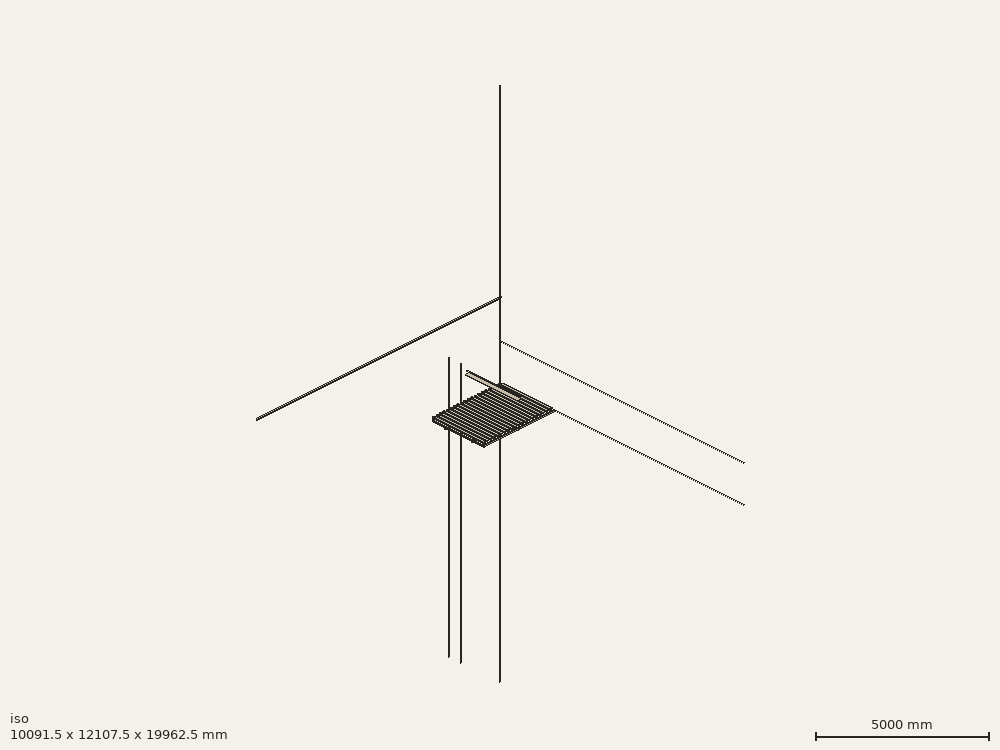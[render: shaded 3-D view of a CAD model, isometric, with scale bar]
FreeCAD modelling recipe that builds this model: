
FCSTD DOCUMENT  (FreeCAD 0.15R4671 (Git))
Label: Assemblage
License: All rights reserved
LicenseURL: http://en.wikipedia.org/wiki/All_rights_reserved
objects: Part::Extrusion×475, Sketcher::SketchObject×454, Part::Cut×180, Part::MultiFuse×62, Part::Chamfer×60, Part::Fuse×40, Part::Fillet×40, App::DocumentObjectGroup×35, Part::Feature×20, PartDesign::Pocket×18, PartDesign::LinearPattern×6, PartDesign::Pad×2
note: 1377 computed .brp shape members not serialized (recipe doc carries the construction recipe); baked Part::Feature solids carry a one-line shape summary decoded from their .brp

FEATURE [Sketcher::SketchObject] Sketch
  Placement = pos=(0,0,0) rot=(1,0,0;1.5708rad)
  sketch-geometry (8):
    g0: LineSegment StartX=-21.15 StartY=16.15 StartZ=0 EndX=-16.15 EndY=21.15 EndZ=0
    g1: LineSegment StartX=-16.15 StartY=21.15 StartZ=0 EndX=16.15 EndY=21.15 EndZ=0
    g2: LineSegment StartX=16.15 StartY=21.15 StartZ=0 EndX=21.15 EndY=16.15 EndZ=0
    g3: LineSegment StartX=21.15 StartY=16.15 StartZ=0 EndX=21.15 EndY=-16.15 EndZ=0
    g4: LineSegment StartX=21.15 StartY=-16.15 StartZ=0 EndX=16.15 EndY=-21.15 EndZ=0
    g5: LineSegment StartX=16.15 StartY=-21.15 StartZ=0 EndX=-16.15 EndY=-21.15 EndZ=0
    g6: LineSegment StartX=-16.15 StartY=-21.15 StartZ=0 EndX=-21.15 EndY=-16.15 EndZ=0
    g7: LineSegment StartX=-21.15 StartY=-16.15 StartZ=0 EndX=-21.15 EndY=16.15 EndZ=0
  constraints (21):
    c: Coincident(g0,g1)
    c: Horizontal(g1)
    c: Coincident(g1,g2)
    c: Coincident(g2,g3)
    c: Vertical(g3)
    c: Coincident(g3,g4)
    c: Coincident(g4,g5)
    c: Horizontal(g5)
    c: Coincident(g5,g6)
    c: Coincident(g6,g7)
    c: Coincident(g7,g0)
    c: Angle(g7,g0) = 2.35619
    c: Distance(g0,g7) = 5
    c: Distance(g2,g7) = 42.3
    c: Distance(g5,g1) = 42.3
    c: Symmetric(g6,g3,g-2)
    c: Symmetric(g5,g4,g-2)
    c: Symmetric(g0,g2,g-2)
    c: Symmetric(g0,g1,g-2)
    c: Symmetric(g0,g6,g-1)
    c: Symmetric(g0,g5,g-1)
FEATURE [Part::Extrusion] Extrude
  Base = -> Sketch
  Dir = (0,48,0)
  Solid = true
FEATURE [Sketcher::SketchObject] Sketch001
  Placement = pos=(0,0,0) rot=(1,0,0;1.5708rad)
  Support = -> Extrude [Face9]
  sketch-geometry (1):
    g0: Circle CenterX=0 CenterY=0 CenterZ=0 NormalX=0 NormalY=0 NormalZ=1 Radius=11
  constraints (2):
    c: Coincident(g0,g-1)
    c: Radius(g0) = 11
FEATURE [Part::Extrusion] Extrude001
  Base = -> Sketch001
  Dir = (0,-2,0)
  Solid = true
FEATURE [Sketcher::SketchObject] Sketch002
  Placement = pos=(0,-2,0) rot=(1,0,0;1.5708rad)
  Support = -> Extrude001 [Face3]
  sketch-geometry (1):
    g0: Circle CenterX=0 CenterY=0 CenterZ=0 NormalX=0 NormalY=0 NormalZ=1 Radius=2.5
  constraints (2):
    c: Coincident(g0,g-1)
    c: Radius(g0) = 2.5
FEATURE [Part::Extrusion] Extrude002
  Base = -> Sketch002
  Dir = (0,-22,0)
  Solid = true
FEATURE [Part::Chamfer] Chamfer
  Base = -> Extrude002
  Edges = 1 edges r=0.8: [Edge3]
FEATURE [Sketcher::SketchObject] Sketch003
  Placement = pos=(0,0,0) rot=(1,0,0;1.5708rad)
  Support = -> Extrude [Face9]
  sketch-geometry (4):
    g0: Circle CenterX=-15.5 CenterY=15.5 CenterZ=0 NormalX=0 NormalY=0 NormalZ=1 Radius=2
    g1: Circle CenterX=15.5 CenterY=15.5 CenterZ=0 NormalX=0 NormalY=0 NormalZ=1 Radius=2
    g2: Circle CenterX=-15.5 CenterY=-15.5 CenterZ=0 NormalX=0 NormalY=0 NormalZ=1 Radius=2
    g3: Circle CenterX=15.5 CenterY=-15.5 CenterZ=0 NormalX=0 NormalY=0 NormalZ=1 Radius=2
  constraints (9):
    c: Distance(g0,g1) = 31
    c: Distance(g0,g2) = 31
    c: Symmetric(g0,g2,g-1)
    c: Symmetric(g0,g1,g-2)
    c: Symmetric(g2,g3,g-2)
    c: Radius(g0) = 2
    c: Equal(g0,g1)
    c: Equal(g0,g2)
    c: Equal(g0,g3)
FEATURE [Part::Extrusion] Extrude003
  Base = -> Sketch003
  Dir = (0,4.5,0)
  Solid = true
FEATURE [Part::Cut] Cut
  Base = -> Extrude
  Tool = -> Extrude003
FEATURE [Sketcher::SketchObject] Sketch004
  Placement = pos=(0,0,0) rot=(1,0,0;1.5708rad)
  sketch-geometry (1):
    g0: Circle CenterX=0 CenterY=0 CenterZ=0 NormalX=0 NormalY=0 NormalZ=1 Radius=9
  constraints (2):
    c: Coincident(g0,g-1)
    c: Radius(g0) = 9
FEATURE [Part::Extrusion] Extrude004
  Base = -> Sketch004
  Dir = (0,25,0)
  Solid = true
FEATURE [Sketcher::SketchObject] Sketch005
  Placement = pos=(0,0,0) rot=(1,0,0;1.5708rad)
  sketch-geometry (1):
    g0: Circle CenterX=0 CenterY=0 CenterZ=0 NormalX=0 NormalY=0 NormalZ=1 Radius=2.5
  constraints (2):
    c: Coincident(g0,g-1)
    c: Radius(g0) = 2.5
FEATURE [Part::Extrusion] Extrude005
  Base = -> Sketch005
  Dir = (0,10,0)
  Solid = true
FEATURE [Part::Cut] Cut001
  Base = -> Extrude004
  Tool = -> Extrude005
FEATURE [Sketcher::SketchObject] Sketch006
  Placement = pos=(0,25,0) rot=(0,0.707107,0.707107;3.14159rad)
  Support = -> Cut001 [Face3]
  sketch-geometry (1):
    g0: Circle CenterX=0 CenterY=0 CenterZ=0 NormalX=0 NormalY=0 NormalZ=1 Radius=4
  constraints (2):
    c: Coincident(g0,g-1)
    c: Radius(g0) = 4
FEATURE [Part::Extrusion] Extrude006
  Base = -> Sketch006
  Dir = (0,-10,0)
  Solid = true
FEATURE [Part::Cut] Cut002  label="Accouplement_001"
  Base = -> Cut001
  Placement = pos=(0,-12,0) rot=(1,0,0;3.14159rad)
  Tool = -> Extrude006
FEATURE [Part::Fuse] Fusion
  Base = -> Extrude001
  Tool = -> Cut
FEATURE [Part::Fuse] Fusion001  label="Moteur_001"
  Base = -> Chamfer
  Tool = -> Fusion
FEATURE [Sketcher::SketchObject] Sketch007
  Placement = pos=(0,0,0) rot=(1,0,0;1.5708rad)
  sketch-geometry (4):
    g0: LineSegment StartX=-50 StartY=0 StartZ=0 EndX=-47 EndY=0 EndZ=0
    g1: LineSegment StartX=47 StartY=0 StartZ=0 EndX=50 EndY=0 EndZ=0
    g2: ArcOfCircle CenterX=0 CenterY=0 CenterZ=0 NormalX=0 NormalY=0 NormalZ=1 Radius=47 StartAngle=3.14159 EndAngle=6.28319
    g3: ArcOfCircle CenterX=0 CenterY=0 CenterZ=0 NormalX=0 NormalY=0 NormalZ=1 Radius=50 StartAngle=3.14159 EndAngle=6.28319
  constraints (13):
    c: Horizontal(g0)
    c: PointOnObject(g1,g-1)
    c: Horizontal(g1)
    c: Coincident(g2,g-1)
    c: PointOnObject(g2,g-1)
    c: Coincident(g3,g-1)
    c: Coincident(g3,g1)
    c: PointOnObject(g3,g-1)
    c: Coincident(g0,g3)
    c: Coincident(g0,g2)
    c: Distance(g0,g1) = 100
    c: Distance(g0,g0) = 3
    c: Coincident(g1,g2)
FEATURE [Part::Extrusion] Extrude007  label="Demi_tube_sous_miroir_001"
  Base = -> Sketch007
  Dir = (0,2000,0)
  Placement = pos=(0,-62,20) rot=(0,0,1;3.14159rad)
  Solid = true
FEATURE [Part::Feature] Part__Feature  label="Coussinet_autolub_C2-151-8-128_001"
  Placement = pos=(0,-46,0) rot=(0,0,1;1.5708rad)
  shape: bbox 16 x 8 x 16 mm, 12 faces (baked)
FEATURE [Sketcher::SketchObject] Sketch008
  Placement = pos=(0,0,0) rot=(1,0,0;1.5708rad)
  sketch-geometry (21):
    g0: Circle CenterX=0 CenterY=0 CenterZ=0 NormalX=0 NormalY=0 NormalZ=1 Radius=6
    g1: LineSegment StartX=-20.5 StartY=15 StartZ=0 EndX=20.5 EndY=15 EndZ=0
    g2: ArcOfCircle CenterX=20.5 CenterY=13 CenterZ=0 NormalX=0 NormalY=0 NormalZ=1 Radius=2 StartAngle=6.28319 EndAngle=7.85398
    g3: LineSegment StartX=22.5 StartY=13 StartZ=0 EndX=22.5 EndY=-73 EndZ=0
    g4: LineSegment StartX=-22.5 StartY=13 StartZ=0 EndX=-22.5 EndY=-73 EndZ=0
    g5: ArcOfCircle CenterX=-20.5 CenterY=13 CenterZ=0 NormalX=0 NormalY=0 NormalZ=1 Radius=2 StartAngle=1.5708 EndAngle=3.14159
    g6: ArcOfCircle CenterX=-20.5 CenterY=-73 CenterZ=0 NormalX=0 NormalY=0 NormalZ=1 Radius=2 StartAngle=3.14159 EndAngle=4.71239
    g7: ArcOfCircle CenterX=20.5 CenterY=-73 CenterZ=0 NormalX=0 NormalY=0 NormalZ=1 Radius=2 StartAngle=4.71239 EndAngle=6.28319
    g8: LineSegment StartX=-20.5 StartY=-75 StartZ=0 EndX=20.5 EndY=-75 EndZ=0
    g9: ArcOfCircle CenterX=0 CenterY=-16.7 CenterZ=0 NormalX=0 NormalY=0 NormalZ=1 Radius=1.5 StartAngle=0 EndAngle=3.14159
    g10: ArcOfCircle CenterX=0 CenterY=-24.3 CenterZ=0 NormalX=0 NormalY=0 NormalZ=1 Radius=1.5 StartAngle=3.14159 EndAngle=6.28319
    g11: LineSegment StartX=-1.5 StartY=-16.7 StartZ=0 EndX=-1.5 EndY=-24.3 EndZ=0
    g12: LineSegment StartX=1.5 StartY=-16.7 StartZ=0 EndX=1.5 EndY=-24.3 EndZ=0
    g13: Circle CenterX=-12.5 CenterY=-45 CenterZ=0 NormalX=0 NormalY=0 NormalZ=1 Radius=3.5
    g14: Circle CenterX=12.5 CenterY=-45 CenterZ=0 NormalX=0 NormalY=0 NormalZ=1 Radius=3.5
    g15: Circle CenterX=-12.5 CenterY=-65 CenterZ=0 NormalX=0 NormalY=0 NormalZ=1 Radius=3.5
    g16: Circle CenterX=12.5 CenterY=-65 CenterZ=0 NormalX=0 NormalY=0 NormalZ=1 Radius=3.5
    g17: LineSegment [constr] StartX=-12.5 StartY=-45 StartZ=0 EndX=12.5 EndY=-45 EndZ=0
    g18: LineSegment [constr] StartX=-12.5 StartY=-45 StartZ=0 EndX=-12.5 EndY=-65 EndZ=0
    g19: LineSegment [constr] StartX=-12.5 StartY=-65 StartZ=0 EndX=12.5 EndY=-65 EndZ=0
    g20: LineSegment [constr] StartX=12.5 StartY=-45 StartZ=0 EndX=12.5 EndY=-65 EndZ=0
  constraints (59):
    c: Coincident(g0,g-1)
    c: Radius(g0) = 6
    c: Horizontal(g1)
    c: Coincident(g2,g1)
    c: Coincident(g3,g2)
    c: Vertical(g3)
    c: Vertical(g4)
    c: Coincident(g5,g1)
    c: Coincident(g5,g4)
    c: Coincident(g7,g3)
    c: Coincident(g8,g6)
    c: Coincident(g8,g7)
    c: Tangent(g8,g7)
    c: Tangent(g5,g4)
    c: Tangent(g5,g1)
    c: Tangent(g1,g2)
    c: Tangent(g2,g3)
    c: Coincident(g4,g6)
    c: Tangent(g6,g4)
    c: Tangent(g6,g8)
    c: Horizontal(g8)
    c: Tangent(g7,g3)
    c: Distance(g4,g2) = 45
    c: Symmetric(g4,g2,g-2)
    c: Distance(g1,g6) = 90
    c: DistanceY(g-1,g1) = 15
    c: Tangent(g9,g12) = 1.5708
    c: Tangent(g9,g11) = -1.5708
    c: Tangent(g11,g10) = -1.5708
    c: Tangent(g12,g10) = 1.5708
    c: Vertical(g11)
    c: Equal(g9,g10)
    c: PointOnObject(g9,g-2)
    c: Distance(g-1,g9) = 16.7
    c: Distance(g9,g10) = 7.6
    c: Radius(g9) = 1.5
    c: Radius(g13) = 3.5
    c: Equal(g13,g14)
    c: Equal(g13,g16)
    c: Equal(g13,g15)
    c: Radius(g5) = 2
    c: Equal(g5,g7)
    c: Equal(g5,g6)
    c: DistanceY(g-1,g13) = -45
    c: Coincident(g17,g13)
    c: Coincident(g17,g14)
    c: Horizontal(g17)
    c: Coincident(g18,g13)
    c: Coincident(g18,g15)
    c: Coincident(g19,g15)
    c: Coincident(g19,g16)
    c: Horizontal(g19)
    c: Coincident(g20,g14)
    c: Coincident(g20,g16)
    c: Vertical(g18)
    c: Vertical(g20)
    c: Distance(g13,g15) = 20
    c: Distance(g13,g14) = 25
    c: Symmetric(g13,g14,g-2)
FEATURE [Part::Extrusion] Extrude008  label="Plaque_support_001"
  Base = -> Sketch008
  Dir = (0,6,0)
  Placement = pos=(0,-46,0) rot=(0,0,1;0rad)
  Solid = true
FEATURE [Sketcher::SketchObject] Sketch009
  Placement = pos=(0,0,0) rot=(0.57735,0.57735,0.57735;2.0944rad)
  sketch-geometry (8):
    g0: LineSegment StartX=0 StartY=33 StartZ=0 EndX=-2 EndY=33 EndZ=0
    g1: LineSegment StartX=-2 StartY=33 StartZ=0 EndX=-2 EndY=-24 EndZ=0
    g2: ArcOfCircle CenterX=-4 CenterY=-24 CenterZ=0 NormalX=0 NormalY=0 NormalZ=1 Radius=2 StartAngle=4.71239 EndAngle=6.28319
    g3: LineSegment StartX=-4 StartY=-26 StartZ=0 EndX=-38 EndY=-26 EndZ=0
    g4: LineSegment StartX=-38 StartY=-26 StartZ=0 EndX=-38 EndY=-28 EndZ=0
    g5: LineSegment StartX=-38 StartY=-28 StartZ=0 EndX=-4 EndY=-28 EndZ=0
    g6: ArcOfCircle CenterX=-4 CenterY=-24 CenterZ=0 NormalX=0 NormalY=0 NormalZ=1 Radius=4 StartAngle=4.71239 EndAngle=6.28319
    g7: LineSegment StartX=0 StartY=-24 StartZ=0 EndX=0 EndY=33 EndZ=0
  constraints (22):
    c: PointOnObject(g0,g-2)
    c: Horizontal(g0)
    c: Coincident(g0,g1)
    c: Vertical(g1)
    c: Tangent(g1,g2) = 1.5708
    c: Tangent(g2,g3) = 1.5708
    c: Coincident(g3,g4)
    c: Vertical(g4)
    c: Coincident(g4,g5)
    c: Horizontal(g5)
    c: Tangent(g5,g6) = -1.5708
    c: PointOnObject(g6,g-2)
    c: Tangent(g6,g7) = -1.5708
    c: Coincident(g7,g0)
    c: Horizontal(g3)
    c: DistanceX(g0,g0) = 2
    c: Radius(g2) = 2
    c: Radius(g6) = 4
    c: DistanceY(g3,g4) = -2
    c: Distance(g-1,g0) = 33
    c: DistanceY(g-1,g5) = -28
    c: DistanceX(g6,g4) = -38
FEATURE [Part::Extrusion] Extrude009
  Base = -> Sketch009
  Dir = (-32.5,0,0)
  Solid = true
FEATURE [Part::Extrusion] Extrude010
  Base = -> Sketch009
  Dir = (32.5,0,0)
  Solid = true
FEATURE [Part::MultiFuse] Fusion002
  Shapes = -> [Extrude009,Extrude010]
FEATURE [Sketcher::SketchObject] Sketch010
  Placement = pos=(0,-2,0) rot=(1,0,0;1.5708rad)
  Support = -> Fusion002 [Face3]
  sketch-geometry (9):
    g0: ArcOfCircle CenterX=0 CenterY=0 CenterZ=0 NormalX=0 NormalY=0 NormalZ=1 Radius=32.5 StartAngle=0 EndAngle=3.14159
    g1: LineSegment StartX=-32.5 StartY=0 StartZ=0 EndX=-32.5 EndY=34 EndZ=0
    g2: LineSegment StartX=-32.5 StartY=34 StartZ=0 EndX=32.5 EndY=34 EndZ=0
    g3: LineSegment StartX=32.5 StartY=34 StartZ=0 EndX=32.5 EndY=0 EndZ=0
    g4: Circle CenterX=0 CenterY=0 CenterZ=0 NormalX=0 NormalY=0 NormalZ=1 Radius=11
    g5: Circle CenterX=-15.5 CenterY=15.5 CenterZ=0 NormalX=0 NormalY=0 NormalZ=1 Radius=2
    g6: Circle CenterX=15.5 CenterY=15.5 CenterZ=0 NormalX=0 NormalY=0 NormalZ=1 Radius=2
    g7: Circle CenterX=-15.5 CenterY=-15.5 CenterZ=0 NormalX=0 NormalY=0 NormalZ=1 Radius=2
    g8: Circle CenterX=15.5 CenterY=-15.5 CenterZ=0 NormalX=0 NormalY=0 NormalZ=1 Radius=2
  constraints (23):
    c: Coincident(g0,g-1)
    c: PointOnObject(g0,g-1)
    c: PointOnObject(g0,g-1)
    c: Coincident(g1,g0)
    c: Vertical(g1)
    c: Coincident(g1,g2)
    c: Horizontal(g2)
    c: Coincident(g2,g3)
    c: Coincident(g3,g0)
    c: Vertical(g3)
    c: DistanceY(g1,g0) = -34
    c: Coincident(g4,g-1)
    c: Radius(g4) = 11
    c: DistanceX(g1,g2) = 65
    c: Radius(g5) = 2
    c: Equal(g5,g6)
    c: Equal(g5,g8)
    c: Equal(g5,g7)
    c: Symmetric(g5,g6,g-2)
    c: Symmetric(g5,g7,g-1)
    c: Symmetric(g7,g8,g-2)
    c: DistanceX(g5,g6) = 31
    c: DistanceY(g5,g7) = -31
FEATURE [Part::Extrusion] Extrude011
  Base = -> Sketch010
  Dir = (0,2,0)
  Solid = true
FEATURE [Part::Cut] Cut003
  Base = -> Fusion002
  Tool = -> Extrude011
FEATURE [Sketcher::SketchObject] Sketch011
  ExternalGeometry = -> [Cut003]
  Placement = pos=(0,0,-26) rot=(0,0,1;0rad)
  Support = -> Cut003 [Face5]
  sketch-geometry (5):
    g0: Circle CenterX=-25 CenterY=-12 CenterZ=0 NormalX=0 NormalY=0 NormalZ=1 Radius=3.5
    g1: Circle CenterX=-25 CenterY=-30 CenterZ=0 NormalX=0 NormalY=0 NormalZ=1 Radius=3.5
    g2: Circle CenterX=25 CenterY=-12 CenterZ=0 NormalX=0 NormalY=0 NormalZ=1 Radius=3.5
    g3: Circle CenterX=25 CenterY=-30 CenterZ=0 NormalX=0 NormalY=0 NormalZ=1 Radius=3.5
    g4: LineSegment [constr] StartX=-25 StartY=-12 StartZ=0 EndX=-25 EndY=-30 EndZ=0
  constraints (12):
    c: Radius(g0) = 3.5
    c: Equal(g0,g2)
    c: Equal(g0,g3)
    c: Equal(g0,g1)
    c: Symmetric(g0,g2,g-2)
    c: Symmetric(g1,g3,g-2)
    c: Coincident(g4,g0)
    c: Coincident(g4,g1)
    c: Vertical(g4)
    c: DistanceY(g0,g1) = -18
    c: DistanceY(g-3,g1) = 8
    c: DistanceX(g0,g2) = 50
FEATURE [Part::Extrusion] Extrude012
  Base = -> Sketch011
  Dir = (0,0,-2)
  Solid = true
FEATURE [Part::Cut] Cut004
  Base = -> Cut003
  Tool = -> Extrude012
FEATURE [Part::Fillet] Fillet  label="Plaque_moteur_001"
  Base = -> Cut004
  Edges = 2 edges r=4: [Edge5,Edge59]
FEATURE [Sketcher::SketchObject] Sketch012
  Placement = pos=(0,0,0) rot=(1,0,0;1.5708rad)
  sketch-geometry (4):
    g0: LineSegment StartX=-3.15 StartY=5.95 StartZ=0 EndX=3.15 EndY=5.95 EndZ=0
    g1: LineSegment StartX=3.15 StartY=5.95 StartZ=0 EndX=3.15 EndY=-5.95 EndZ=0
    g2: LineSegment StartX=3.15 StartY=-5.95 StartZ=0 EndX=-3.15 EndY=-5.95 EndZ=0
    g3: LineSegment StartX=-3.15 StartY=-5.95 StartZ=0 EndX=-3.15 EndY=5.95 EndZ=0
  constraints (12):
    c: Coincident(g0,g1)
    c: Coincident(g1,g2)
    c: Coincident(g2,g3)
    c: Coincident(g3,g0)
    c: Horizontal(g0)
    c: Horizontal(g2)
    c: Vertical(g1)
    c: Vertical(g3)
    c: DistanceX(g0,g0) = 6.3
    c: DistanceY(g0,g2) = -11.9
    c: Symmetric(g0,g0,g-2)
    c: Symmetric(g0,g1,g-1)
FEATURE [Part::Extrusion] Extrude013
  Base = -> Sketch012
  Dir = (0,-10.8,0)
  Solid = true
FEATURE [Sketcher::SketchObject] Sketch013
  ExternalGeometry = -> [Extrude013]
  Placement = pos=(0,-10.8,0) rot=(1,0,0;1.5708rad)
  Support = -> Extrude013 [Face6]
  sketch-geometry (4):
    g0: LineSegment StartX=-3.15 StartY=1.55 StartZ=0 EndX=3.15 EndY=1.55 EndZ=0
    g1: LineSegment StartX=3.15 StartY=1.55 StartZ=0 EndX=3.15 EndY=-1.55 EndZ=0
    g2: LineSegment StartX=3.15 StartY=-1.55 StartZ=0 EndX=-3.15 EndY=-1.55 EndZ=0
    g3: LineSegment StartX=-3.15 StartY=-1.55 StartZ=0 EndX=-3.15 EndY=1.55 EndZ=0
  constraints (12):
    c: Coincident(g0,g1)
    c: Coincident(g1,g2)
    c: Coincident(g2,g3)
    c: Coincident(g3,g0)
    c: Horizontal(g0)
    c: Horizontal(g2)
    c: Vertical(g1)
    c: Vertical(g3)
    c: PointOnObject(g0,g-4)
    c: PointOnObject(g0,g-3)
    c: DistanceY(g0,g2) = -3.1
    c: Symmetric(g0,g1,g-1)
FEATURE [Part::Extrusion] Extrude014
  Base = -> Sketch013
  Dir = (0,7.7,0)
  Solid = true
FEATURE [Part::Cut] Cut005
  Base = -> Extrude013
  Tool = -> Extrude014
FEATURE [Part::Chamfer] Chamfer001
  Base = -> Cut005
  Edges = 4 edges r=0.5: [Edge7,Edge9,Edge15,Edge17]
FEATURE [Part::Chamfer] Chamfer002
  Base = -> Chamfer001
  Edges = 1 edges r=1.2: [Edge13]
FEATURE [Sketcher::SketchObject] Sketch014
  ExternalGeometry = -> [Chamfer002]
  Placement = pos=(0,0,5.95) rot=(0,0,1;0rad)
  Support = -> Chamfer002 [Face5]
  sketch-geometry (4):
    g0: LineSegment StartX=-3 StartY=0 StartZ=0 EndX=3 EndY=0 EndZ=0
    g1: LineSegment StartX=3 StartY=0 StartZ=0 EndX=3 EndY=-3.1 EndZ=0
    g2: LineSegment StartX=3 StartY=-3.1 StartZ=0 EndX=-3 EndY=-3.1 EndZ=0
    g3: LineSegment StartX=-3 StartY=-3.1 StartZ=0 EndX=-3 EndY=0 EndZ=0
  constraints (12):
    c: Coincident(g0,g1)
    c: Coincident(g1,g2)
    c: Coincident(g2,g3)
    c: Coincident(g3,g0)
    c: Horizontal(g0)
    c: Horizontal(g2)
    c: Vertical(g1)
    c: Vertical(g3)
    c: PointOnObject(g0,g-1)
    c: DistanceX(g-3,g0) = 0.15
    c: Symmetric(g0,g0,g-2)
    c: DistanceY(g0,g1) = -3.1
FEATURE [Part::Extrusion] Extrude015
  Base = -> Sketch014
  Dir = (0,0,6.3)
  Solid = true
FEATURE [Sketcher::SketchObject] Sketch015
  ExternalGeometry = -> [Extrude015]
  Placement = pos=(0,-3.1,0) rot=(1,0,0;1.5708rad)
  Support = -> Extrude015 [Face3]
  sketch-geometry (1):
    g0: Circle CenterX=0 CenterY=9.5 CenterZ=0 NormalX=0 NormalY=0 NormalZ=1 Radius=1.65
  constraints (3):
    c: PointOnObject(g0,g-2)
    c: Radius(g0) = 1.65
    c: DistanceY(g0,g-3) = -3.55
FEATURE [Part::Extrusion] Extrude016
  Base = -> Sketch015
  Dir = (0,6,0)
  Solid = true
FEATURE [Part::Cut] Cut006
  Base = -> Extrude015
  Tool = -> Extrude016
FEATURE [Part::Fillet] Fillet001
  Base = -> Cut006
  Edges = 2 edges r=1.35: [Edge8,Edge11]
FEATURE [Part::MultiFuse] Fusion003
  Shapes = -> [Chamfer002]
FEATURE [Sketcher::SketchObject] Sketch016
  Placement = pos=(0,0,0) rot=(0,0.707107,0.707107;3.14159rad)
  Support = -> Fusion003 [Face7]
  sketch-geometry (4):
    g0: Circle CenterX=-1.27 CenterY=3.8 CenterZ=0 NormalX=0 NormalY=0 NormalZ=1 Radius=0.2
    g1: Circle CenterX=1.27 CenterY=3.8 CenterZ=0 NormalX=0 NormalY=0 NormalZ=1 Radius=0.2
    g2: Circle CenterX=-1.27 CenterY=-3.8 CenterZ=0 NormalX=0 NormalY=0 NormalZ=1 Radius=0.2
    g3: Circle CenterX=1.27 CenterY=-3.8 CenterZ=0 NormalX=0 NormalY=0 NormalZ=1 Radius=0.2
  constraints (9):
    c: Radius(g0) = 0.2
    c: Equal(g0,g1)
    c: Equal(g0,g3)
    c: Equal(g0,g2)
    c: Symmetric(g0,g1,g-2)
    c: Symmetric(g2,g3,g-2)
    c: Symmetric(g0,g2,g-1)
    c: DistanceX(g0,g1) = 2.54
    c: DistanceY(g1,g3) = -7.6
FEATURE [Part::Extrusion] Extrude017
  Base = -> Sketch016
  Dir = (0,7.8,0)
  Solid = true
FEATURE [Part::MultiFuse] Fusion004  label="Capteur_optique_001"
  Placement = pos=(0,-46,-20.7) rot=(0,0,1;0rad)
  Shapes = -> [Fusion003,Fillet001,Extrude017]
FEATURE [Sketcher::SketchObject] Sketch017
  Placement = pos=(0,0,0) rot=(1,0,0;1.5708rad)
  sketch-geometry (1):
    g0: Circle CenterX=0 CenterY=0 CenterZ=0 NormalX=0 NormalY=0 NormalZ=1 Radius=4
  constraints (2):
    c: Coincident(g0,g-1)
    c: Radius(g0) = 4
FEATURE [Part::Extrusion] Extrude018
  Base = -> Sketch017
  Dir = (0,50,0)
  Solid = true
FEATURE [Sketcher::SketchObject] Sketch018
  Placement = pos=(0,0,0) rot=(0.57735,0.57735,0.57735;2.0944rad)
  sketch-geometry (1):
    g0: Circle CenterX=6 CenterY=0 CenterZ=0 NormalX=0 NormalY=0 NormalZ=1 Radius=2
  constraints (3):
    c: DistanceX(g-1,g0) = 6
    c: Radius(g0) = 2
    c: PointOnObject(g0,g-1)
FEATURE [Part::Extrusion] Extrude019
  Base = -> Sketch018
  Dir = (4,0,0)
  Solid = true
FEATURE [Part::Extrusion] Extrude020
  Base = -> Sketch018
  Dir = (-4,0,0)
  Solid = true
FEATURE [Part::Cut] Cut007
  Base = -> Extrude018
  Tool = -> Extrude019
FEATURE [Part::Cut] Cut008  label="Axe_D8_001"
  Base = -> Cut007
  Placement = pos=(0,-86,0) rot=(0,0,1;0rad)
  Tool = -> Extrude020
FEATURE [Sketcher::SketchObject] Sketch019
  Placement = pos=(0,0,0) rot=(1,0,0;1.5708rad)
  sketch-geometry (1):
    g0: Circle CenterX=0 CenterY=0 CenterZ=0 NormalX=0 NormalY=0 NormalZ=1 Radius=2
  constraints (2):
    c: Coincident(g0,g-1)
    c: Radius(g0) = 2
FEATURE [Part::Extrusion] Extrude021  label="Axe_D4_001"
  Base = -> Sketch019
  Dir = (0,103.6,0)
  Placement = pos=(51.8,-80,0) rot=(0,0,1;1.5708rad)
  Solid = true
FEATURE [Sketcher::SketchObject] Sketch020
  Placement = pos=(0,0,0) rot=(1,0,0;1.5708rad)
  sketch-geometry (8):
    g0: LineSegment StartX=-50 StartY=0 StartZ=0 EndX=50 EndY=0 EndZ=0
    g1: LineSegment StartX=50 StartY=0 StartZ=0 EndX=50 EndY=-2 EndZ=0
    g2: LineSegment StartX=50 StartY=-2 StartZ=0 EndX=47 EndY=-2 EndZ=0
    g3: LineSegment StartX=47 StartY=-2 StartZ=0 EndX=44 EndY=-16 EndZ=0
    g4: LineSegment StartX=44 StartY=-16 StartZ=0 EndX=-44 EndY=-16 EndZ=0
    g5: LineSegment StartX=-44 StartY=-16 StartZ=0 EndX=-47 EndY=-2 EndZ=0
    g6: LineSegment StartX=-47 StartY=-2 StartZ=0 EndX=-50 EndY=-2 EndZ=0
    g7: LineSegment StartX=-50 StartY=-2 StartZ=0 EndX=-50 EndY=0 EndZ=0
  constraints (24):
    c: PointOnObject(g0,g-1)
    c: Horizontal(g0)
    c: Coincident(g0,g1)
    c: Vertical(g1)
    c: Coincident(g1,g2)
    c: Horizontal(g2)
    c: Coincident(g2,g3)
    c: Coincident(g3,g4)
    c: Horizontal(g4)
    c: Coincident(g4,g5)
    c: Coincident(g5,g6)
    c: Horizontal(g6)
    c: Coincident(g6,g7)
    c: Coincident(g7,g0)
    c: Vertical(g7)
    c: DistanceY(g0,g6) = -2
    c: DistanceX(g6,g5) = 3
    c: DistanceX(g0,g0) = 100
    c: Symmetric(g0,g0,g-2)
    c: Symmetric(g6,g1,g-2)
    c: Symmetric(g5,g2,g-2)
    c: Symmetric(g4,g3,g-2)
    c: DistanceX(g4,g3) = 88
    c: DistanceY(g0,g4) = -16
FEATURE [Part::Extrusion] Extrude022  label="Plaque_alveolaire_001"
  Base = -> Sketch020
  Dir = (0,2000,0)
  Placement = pos=(0,-62,22) rot=(0,0,1;3.14159rad)
  Solid = true
FEATURE [App::DocumentObjectGroup] Groupe  label="Assemblage_miroir_001"
  Group = -> [Cut002,Fusion001,Extrude007,Part__Feature,Extrude008,Fillet,Fusion004,Cut008,Extrude021,Extrude022]
FEATURE [Sketcher::SketchObject] Sketch021
  Placement = pos=(0,0,0) rot=(1,0,0;1.5708rad)
  sketch-geometry (8):
    g0: LineSegment StartX=-21.15 StartY=16.15 StartZ=0 EndX=-16.15 EndY=21.15 EndZ=0
    g1: LineSegment StartX=-16.15 StartY=21.15 StartZ=0 EndX=16.15 EndY=21.15 EndZ=0
    g2: LineSegment StartX=16.15 StartY=21.15 StartZ=0 EndX=21.15 EndY=16.15 EndZ=0
    g3: LineSegment StartX=21.15 StartY=16.15 StartZ=0 EndX=21.15 EndY=-16.15 EndZ=0
    g4: LineSegment StartX=21.15 StartY=-16.15 StartZ=0 EndX=16.15 EndY=-21.15 EndZ=0
    g5: LineSegment StartX=16.15 StartY=-21.15 StartZ=0 EndX=-16.15 EndY=-21.15 EndZ=0
    g6: LineSegment StartX=-16.15 StartY=-21.15 StartZ=0 EndX=-21.15 EndY=-16.15 EndZ=0
    g7: LineSegment StartX=-21.15 StartY=-16.15 StartZ=0 EndX=-21.15 EndY=16.15 EndZ=0
  constraints (21):
    c: Coincident(g0,g1)
    c: Horizontal(g1)
    c: Coincident(g1,g2)
    c: Coincident(g2,g3)
    c: Vertical(g3)
    c: Coincident(g3,g4)
    c: Coincident(g4,g5)
    c: Horizontal(g5)
    c: Coincident(g5,g6)
    c: Coincident(g6,g7)
    c: Coincident(g7,g0)
    c: Angle(g7,g0) = 2.35619
    c: Distance(g0,g7) = 5
    c: Distance(g2,g7) = 42.3
    c: Distance(g5,g1) = 42.3
    c: Symmetric(g6,g3,g-2)
    c: Symmetric(g5,g4,g-2)
    c: Symmetric(g0,g2,g-2)
    c: Symmetric(g0,g1,g-2)
    c: Symmetric(g0,g6,g-1)
    c: Symmetric(g0,g5,g-1)
FEATURE [Part::Extrusion] Extrude023
  Base = -> Sketch021
  Dir = (0,48,0)
  Solid = true
FEATURE [Sketcher::SketchObject] Sketch022
  Placement = pos=(0,0,0) rot=(1,0,0;1.5708rad)
  Support = -> Extrude023 [Face9]
  sketch-geometry (1):
    g0: Circle CenterX=0 CenterY=0 CenterZ=0 NormalX=0 NormalY=0 NormalZ=1 Radius=11
  constraints (2):
    c: Coincident(g0,g-1)
    c: Radius(g0) = 11
FEATURE [Part::Extrusion] Extrude024
  Base = -> Sketch022
  Dir = (0,-2,0)
  Solid = true
FEATURE [Sketcher::SketchObject] Sketch023
  Placement = pos=(0,-2,0) rot=(1,0,0;1.5708rad)
  Support = -> Extrude024 [Face3]
  sketch-geometry (1):
    g0: Circle CenterX=0 CenterY=0 CenterZ=0 NormalX=0 NormalY=0 NormalZ=1 Radius=2.5
  constraints (2):
    c: Coincident(g0,g-1)
    c: Radius(g0) = 2.5
FEATURE [Part::Extrusion] Extrude025
  Base = -> Sketch023
  Dir = (0,-22,0)
  Solid = true
FEATURE [Part::Chamfer] Chamfer003
  Base = -> Extrude025
  Edges = 1 edges r=0.8: [Edge3]
FEATURE [Sketcher::SketchObject] Sketch024
  Placement = pos=(0,0,0) rot=(1,0,0;1.5708rad)
  Support = -> Extrude023 [Face9]
  sketch-geometry (4):
    g0: Circle CenterX=-15.5 CenterY=15.5 CenterZ=0 NormalX=0 NormalY=0 NormalZ=1 Radius=2
    g1: Circle CenterX=15.5 CenterY=15.5 CenterZ=0 NormalX=0 NormalY=0 NormalZ=1 Radius=2
    g2: Circle CenterX=-15.5 CenterY=-15.5 CenterZ=0 NormalX=0 NormalY=0 NormalZ=1 Radius=2
    g3: Circle CenterX=15.5 CenterY=-15.5 CenterZ=0 NormalX=0 NormalY=0 NormalZ=1 Radius=2
  constraints (9):
    c: Distance(g0,g1) = 31
    c: Distance(g0,g2) = 31
    c: Symmetric(g0,g2,g-1)
    c: Symmetric(g0,g1,g-2)
    c: Symmetric(g2,g3,g-2)
    c: Radius(g0) = 2
    c: Equal(g0,g1)
    c: Equal(g0,g2)
    c: Equal(g0,g3)
FEATURE [Part::Extrusion] Extrude026
  Base = -> Sketch024
  Dir = (0,4.5,0)
  Solid = true
FEATURE [Part::Cut] Cut009
  Base = -> Extrude023
  Tool = -> Extrude026
FEATURE [Sketcher::SketchObject] Sketch025
  Placement = pos=(0,0,0) rot=(1,0,0;1.5708rad)
  sketch-geometry (1):
    g0: Circle CenterX=0 CenterY=0 CenterZ=0 NormalX=0 NormalY=0 NormalZ=1 Radius=9
  constraints (2):
    c: Coincident(g0,g-1)
    c: Radius(g0) = 9
FEATURE [Part::Extrusion] Extrude027
  Base = -> Sketch025
  Dir = (0,25,0)
  Solid = true
FEATURE [Sketcher::SketchObject] Sketch026
  Placement = pos=(0,0,0) rot=(1,0,0;1.5708rad)
  sketch-geometry (1):
    g0: Circle CenterX=0 CenterY=0 CenterZ=0 NormalX=0 NormalY=0 NormalZ=1 Radius=2.5
  constraints (2):
    c: Coincident(g0,g-1)
    c: Radius(g0) = 2.5
FEATURE [Part::Extrusion] Extrude028
  Base = -> Sketch026
  Dir = (0,10,0)
  Solid = true
FEATURE [Part::Cut] Cut010
  Base = -> Extrude027
  Tool = -> Extrude028
FEATURE [Sketcher::SketchObject] Sketch027
  Placement = pos=(0,25,0) rot=(0,0.707107,0.707107;3.14159rad)
  Support = -> Cut010 [Face3]
  sketch-geometry (1):
    g0: Circle CenterX=0 CenterY=0 CenterZ=0 NormalX=0 NormalY=0 NormalZ=1 Radius=4
  constraints (2):
    c: Coincident(g0,g-1)
    c: Radius(g0) = 4
FEATURE [Part::Extrusion] Extrude029
  Base = -> Sketch027
  Dir = (0,-10,0)
  Solid = true
FEATURE [Part::Cut] Cut011  label="Accouplement_002"
  Base = -> Cut010
  Placement = pos=(-143,-12,0) rot=(1,0,0;3.14159rad)
  Tool = -> Extrude029
FEATURE [Part::Fuse] Fusion005
  Base = -> Extrude024
  Tool = -> Cut009
FEATURE [Part::Fuse] Fusion006  label="Moteur_002"
  Base = -> Chamfer003
  Placement = pos=(-143,0,0) rot=(0,0,1;0rad)
  Tool = -> Fusion005
FEATURE [Sketcher::SketchObject] Sketch028
  Placement = pos=(0,0,0) rot=(1,0,0;1.5708rad)
  sketch-geometry (4):
    g0: LineSegment StartX=-50 StartY=0 StartZ=0 EndX=-47 EndY=0 EndZ=0
    g1: LineSegment StartX=47 StartY=0 StartZ=0 EndX=50 EndY=0 EndZ=0
    g2: ArcOfCircle CenterX=0 CenterY=0 CenterZ=0 NormalX=0 NormalY=0 NormalZ=1 Radius=47 StartAngle=3.14159 EndAngle=6.28319
    g3: ArcOfCircle CenterX=0 CenterY=0 CenterZ=0 NormalX=0 NormalY=0 NormalZ=1 Radius=50 StartAngle=3.14159 EndAngle=6.28319
  constraints (13):
    c: Horizontal(g0)
    c: PointOnObject(g1,g-1)
    c: Horizontal(g1)
    c: Coincident(g2,g-1)
    c: PointOnObject(g2,g-1)
    c: Coincident(g3,g-1)
    c: Coincident(g3,g1)
    c: PointOnObject(g3,g-1)
    c: Coincident(g0,g3)
    c: Coincident(g0,g2)
    c: Distance(g0,g1) = 100
    c: Distance(g0,g0) = 3
    c: Coincident(g1,g2)
FEATURE [Part::Extrusion] Extrude030  label="Demi_tube_sous_miroir_002"
  Base = -> Sketch028
  Dir = (0,2000,0)
  Placement = pos=(-143,-62,20) rot=(0,0,1;3.14159rad)
  Solid = true
FEATURE [Part::Feature] Part__Feature001  label="Coussinet_autolub_C2-151-8-128_002"
  Placement = pos=(-143,-46,0) rot=(0,0,1;1.5708rad)
  shape: bbox 16 x 8 x 16 mm, 12 faces (baked)
FEATURE [Sketcher::SketchObject] Sketch029
  Placement = pos=(0,0,0) rot=(1,0,0;1.5708rad)
  sketch-geometry (21):
    g0: Circle CenterX=0 CenterY=0 CenterZ=0 NormalX=0 NormalY=0 NormalZ=1 Radius=6
    g1: LineSegment StartX=-20.5 StartY=15 StartZ=0 EndX=20.5 EndY=15 EndZ=0
    g2: ArcOfCircle CenterX=20.5 CenterY=13 CenterZ=0 NormalX=0 NormalY=0 NormalZ=1 Radius=2 StartAngle=6.28319 EndAngle=7.85398
    g3: LineSegment StartX=22.5 StartY=13 StartZ=0 EndX=22.5 EndY=-73 EndZ=0
    g4: LineSegment StartX=-22.5 StartY=13 StartZ=0 EndX=-22.5 EndY=-73 EndZ=0
    g5: ArcOfCircle CenterX=-20.5 CenterY=13 CenterZ=0 NormalX=0 NormalY=0 NormalZ=1 Radius=2 StartAngle=1.5708 EndAngle=3.14159
    g6: ArcOfCircle CenterX=-20.5 CenterY=-73 CenterZ=0 NormalX=0 NormalY=0 NormalZ=1 Radius=2 StartAngle=3.14159 EndAngle=4.71239
    g7: ArcOfCircle CenterX=20.5 CenterY=-73 CenterZ=0 NormalX=0 NormalY=0 NormalZ=1 Radius=2 StartAngle=4.71239 EndAngle=6.28319
    g8: LineSegment StartX=-20.5 StartY=-75 StartZ=0 EndX=20.5 EndY=-75 EndZ=0
    g9: ArcOfCircle CenterX=0 CenterY=-16.7 CenterZ=0 NormalX=0 NormalY=0 NormalZ=1 Radius=1.5 StartAngle=0 EndAngle=3.14159
    g10: ArcOfCircle CenterX=0 CenterY=-24.3 CenterZ=0 NormalX=0 NormalY=0 NormalZ=1 Radius=1.5 StartAngle=3.14159 EndAngle=6.28319
    g11: LineSegment StartX=-1.5 StartY=-16.7 StartZ=0 EndX=-1.5 EndY=-24.3 EndZ=0
    g12: LineSegment StartX=1.5 StartY=-16.7 StartZ=0 EndX=1.5 EndY=-24.3 EndZ=0
    g13: Circle CenterX=-12.5 CenterY=-45 CenterZ=0 NormalX=0 NormalY=0 NormalZ=1 Radius=3.5
    g14: Circle CenterX=12.5 CenterY=-45 CenterZ=0 NormalX=0 NormalY=0 NormalZ=1 Radius=3.5
    g15: Circle CenterX=-12.5 CenterY=-65 CenterZ=0 NormalX=0 NormalY=0 NormalZ=1 Radius=3.5
    g16: Circle CenterX=12.5 CenterY=-65 CenterZ=0 NormalX=0 NormalY=0 NormalZ=1 Radius=3.5
    g17: LineSegment [constr] StartX=-12.5 StartY=-45 StartZ=0 EndX=12.5 EndY=-45 EndZ=0
    g18: LineSegment [constr] StartX=-12.5 StartY=-45 StartZ=0 EndX=-12.5 EndY=-65 EndZ=0
    g19: LineSegment [constr] StartX=-12.5 StartY=-65 StartZ=0 EndX=12.5 EndY=-65 EndZ=0
    g20: LineSegment [constr] StartX=12.5 StartY=-45 StartZ=0 EndX=12.5 EndY=-65 EndZ=0
  constraints (59):
    c: Coincident(g0,g-1)
    c: Radius(g0) = 6
    c: Horizontal(g1)
    c: Coincident(g2,g1)
    c: Coincident(g3,g2)
    c: Vertical(g3)
    c: Vertical(g4)
    c: Coincident(g5,g1)
    c: Coincident(g5,g4)
    c: Coincident(g7,g3)
    c: Coincident(g8,g6)
    c: Coincident(g8,g7)
    c: Tangent(g8,g7)
    c: Tangent(g5,g4)
    c: Tangent(g5,g1)
    c: Tangent(g1,g2)
    c: Tangent(g2,g3)
    c: Coincident(g4,g6)
    c: Tangent(g6,g4)
    c: Tangent(g6,g8)
    c: Horizontal(g8)
    c: Tangent(g7,g3)
    c: Distance(g4,g2) = 45
    c: Symmetric(g4,g2,g-2)
    c: Distance(g1,g6) = 90
    c: DistanceY(g-1,g1) = 15
    c: Tangent(g9,g12) = 1.5708
    c: Tangent(g9,g11) = -1.5708
    c: Tangent(g11,g10) = -1.5708
    c: Tangent(g12,g10) = 1.5708
    c: Vertical(g11)
    c: Equal(g9,g10)
    c: PointOnObject(g9,g-2)
    c: Distance(g-1,g9) = 16.7
    c: Distance(g9,g10) = 7.6
    c: Radius(g9) = 1.5
    c: Radius(g13) = 3.5
    c: Equal(g13,g14)
    c: Equal(g13,g16)
    c: Equal(g13,g15)
    c: Radius(g5) = 2
    c: Equal(g5,g7)
    c: Equal(g5,g6)
    c: DistanceY(g-1,g13) = -45
    c: Coincident(g17,g13)
    c: Coincident(g17,g14)
    c: Horizontal(g17)
    c: Coincident(g18,g13)
    c: Coincident(g18,g15)
    c: Coincident(g19,g15)
    c: Coincident(g19,g16)
    c: Horizontal(g19)
    c: Coincident(g20,g14)
    c: Coincident(g20,g16)
    c: Vertical(g18)
    c: Vertical(g20)
    c: Distance(g13,g15) = 20
    c: Distance(g13,g14) = 25
    c: Symmetric(g13,g14,g-2)
FEATURE [Part::Extrusion] Extrude031  label="Plaque_support_002"
  Base = -> Sketch029
  Dir = (0,6,0)
  Placement = pos=(-143,-46,0) rot=(0,0,1;0rad)
  Solid = true
FEATURE [Sketcher::SketchObject] Sketch030
  Placement = pos=(0,0,0) rot=(0.57735,0.57735,0.57735;2.0944rad)
  sketch-geometry (8):
    g0: LineSegment StartX=0 StartY=33 StartZ=0 EndX=-2 EndY=33 EndZ=0
    g1: LineSegment StartX=-2 StartY=33 StartZ=0 EndX=-2 EndY=-24 EndZ=0
    g2: ArcOfCircle CenterX=-4 CenterY=-24 CenterZ=0 NormalX=0 NormalY=0 NormalZ=1 Radius=2 StartAngle=4.71239 EndAngle=6.28319
    g3: LineSegment StartX=-4 StartY=-26 StartZ=0 EndX=-38 EndY=-26 EndZ=0
    g4: LineSegment StartX=-38 StartY=-26 StartZ=0 EndX=-38 EndY=-28 EndZ=0
    g5: LineSegment StartX=-38 StartY=-28 StartZ=0 EndX=-4 EndY=-28 EndZ=0
    g6: ArcOfCircle CenterX=-4 CenterY=-24 CenterZ=0 NormalX=0 NormalY=0 NormalZ=1 Radius=4 StartAngle=4.71239 EndAngle=6.28319
    g7: LineSegment StartX=0 StartY=-24 StartZ=0 EndX=0 EndY=33 EndZ=0
  constraints (22):
    c: PointOnObject(g0,g-2)
    c: Horizontal(g0)
    c: Coincident(g0,g1)
    c: Vertical(g1)
    c: Tangent(g1,g2) = 1.5708
    c: Tangent(g2,g3) = 1.5708
    c: Coincident(g3,g4)
    c: Vertical(g4)
    c: Coincident(g4,g5)
    c: Horizontal(g5)
    c: Tangent(g5,g6) = -1.5708
    c: PointOnObject(g6,g-2)
    c: Tangent(g6,g7) = -1.5708
    c: Coincident(g7,g0)
    c: Horizontal(g3)
    c: DistanceX(g0,g0) = 2
    c: Radius(g2) = 2
    c: Radius(g6) = 4
    c: DistanceY(g3,g4) = -2
    c: Distance(g-1,g0) = 33
    c: DistanceY(g-1,g5) = -28
    c: DistanceX(g6,g4) = -38
FEATURE [Part::Extrusion] Extrude032
  Base = -> Sketch030
  Dir = (-32.5,0,0)
  Solid = true
FEATURE [Part::Extrusion] Extrude033
  Base = -> Sketch030
  Dir = (32.5,0,0)
  Solid = true
FEATURE [Part::MultiFuse] Fusion007
  Shapes = -> [Extrude032,Extrude033]
FEATURE [Sketcher::SketchObject] Sketch031
  Placement = pos=(0,-2,0) rot=(1,0,0;1.5708rad)
  Support = -> Fusion007 [Face3]
  sketch-geometry (9):
    g0: ArcOfCircle CenterX=0 CenterY=0 CenterZ=0 NormalX=0 NormalY=0 NormalZ=1 Radius=32.5 StartAngle=0 EndAngle=3.14159
    g1: LineSegment StartX=-32.5 StartY=0 StartZ=0 EndX=-32.5 EndY=34 EndZ=0
    g2: LineSegment StartX=-32.5 StartY=34 StartZ=0 EndX=32.5 EndY=34 EndZ=0
    g3: LineSegment StartX=32.5 StartY=34 StartZ=0 EndX=32.5 EndY=0 EndZ=0
    g4: Circle CenterX=0 CenterY=0 CenterZ=0 NormalX=0 NormalY=0 NormalZ=1 Radius=11
    g5: Circle CenterX=-15.5 CenterY=15.5 CenterZ=0 NormalX=0 NormalY=0 NormalZ=1 Radius=2
    g6: Circle CenterX=15.5 CenterY=15.5 CenterZ=0 NormalX=0 NormalY=0 NormalZ=1 Radius=2
    g7: Circle CenterX=-15.5 CenterY=-15.5 CenterZ=0 NormalX=0 NormalY=0 NormalZ=1 Radius=2
    g8: Circle CenterX=15.5 CenterY=-15.5 CenterZ=0 NormalX=0 NormalY=0 NormalZ=1 Radius=2
  constraints (23):
    c: Coincident(g0,g-1)
    c: PointOnObject(g0,g-1)
    c: PointOnObject(g0,g-1)
    c: Coincident(g1,g0)
    c: Vertical(g1)
    c: Coincident(g1,g2)
    c: Horizontal(g2)
    c: Coincident(g2,g3)
    c: Coincident(g3,g0)
    c: Vertical(g3)
    c: DistanceY(g1,g0) = -34
    c: Coincident(g4,g-1)
    c: Radius(g4) = 11
    c: DistanceX(g1,g2) = 65
    c: Radius(g5) = 2
    c: Equal(g5,g6)
    c: Equal(g5,g8)
    c: Equal(g5,g7)
    c: Symmetric(g5,g6,g-2)
    c: Symmetric(g5,g7,g-1)
    c: Symmetric(g7,g8,g-2)
    c: DistanceX(g5,g6) = 31
    c: DistanceY(g5,g7) = -31
FEATURE [Part::Extrusion] Extrude034
  Base = -> Sketch031
  Dir = (0,2,0)
  Solid = true
FEATURE [Part::Cut] Cut012
  Base = -> Fusion007
  Tool = -> Extrude034
FEATURE [Sketcher::SketchObject] Sketch032
  ExternalGeometry = -> [Cut012]
  Placement = pos=(0,0,-26) rot=(0,0,1;0rad)
  Support = -> Cut012 [Face5]
  sketch-geometry (5):
    g0: Circle CenterX=-25 CenterY=-12 CenterZ=0 NormalX=0 NormalY=0 NormalZ=1 Radius=3.5
    g1: Circle CenterX=-25 CenterY=-30 CenterZ=0 NormalX=0 NormalY=0 NormalZ=1 Radius=3.5
    g2: Circle CenterX=25 CenterY=-12 CenterZ=0 NormalX=0 NormalY=0 NormalZ=1 Radius=3.5
    g3: Circle CenterX=25 CenterY=-30 CenterZ=0 NormalX=0 NormalY=0 NormalZ=1 Radius=3.5
    g4: LineSegment [constr] StartX=-25 StartY=-12 StartZ=0 EndX=-25 EndY=-30 EndZ=0
  constraints (12):
    c: Radius(g0) = 3.5
    c: Equal(g0,g2)
    c: Equal(g0,g3)
    c: Equal(g0,g1)
    c: Symmetric(g0,g2,g-2)
    c: Symmetric(g1,g3,g-2)
    c: Coincident(g4,g0)
    c: Coincident(g4,g1)
    c: Vertical(g4)
    c: DistanceY(g0,g1) = -18
    c: DistanceY(g-3,g1) = 8
    c: DistanceX(g0,g2) = 50
FEATURE [Part::Extrusion] Extrude035
  Base = -> Sketch032
  Dir = (0,0,-2)
  Solid = true
FEATURE [Part::Cut] Cut013
  Base = -> Cut012
  Tool = -> Extrude035
FEATURE [Part::Fillet] Fillet002  label="Plaque_moteur_002"
  Base = -> Cut013
  Edges = 2 edges r=4: [Edge5,Edge59]
  Placement = pos=(-143,0,0) rot=(0,0,1;0rad)
FEATURE [Sketcher::SketchObject] Sketch033
  Placement = pos=(0,0,0) rot=(1,0,0;1.5708rad)
  sketch-geometry (4):
    g0: LineSegment StartX=-3.15 StartY=5.95 StartZ=0 EndX=3.15 EndY=5.95 EndZ=0
    g1: LineSegment StartX=3.15 StartY=5.95 StartZ=0 EndX=3.15 EndY=-5.95 EndZ=0
    g2: LineSegment StartX=3.15 StartY=-5.95 StartZ=0 EndX=-3.15 EndY=-5.95 EndZ=0
    g3: LineSegment StartX=-3.15 StartY=-5.95 StartZ=0 EndX=-3.15 EndY=5.95 EndZ=0
  constraints (12):
    c: Coincident(g0,g1)
    c: Coincident(g1,g2)
    c: Coincident(g2,g3)
    c: Coincident(g3,g0)
    c: Horizontal(g0)
    c: Horizontal(g2)
    c: Vertical(g1)
    c: Vertical(g3)
    c: DistanceX(g0,g0) = 6.3
    c: DistanceY(g0,g2) = -11.9
    c: Symmetric(g0,g0,g-2)
    c: Symmetric(g0,g1,g-1)
FEATURE [Part::Extrusion] Extrude036
  Base = -> Sketch033
  Dir = (0,-10.8,0)
  Solid = true
FEATURE [Sketcher::SketchObject] Sketch034
  ExternalGeometry = -> [Extrude036]
  Placement = pos=(0,-10.8,0) rot=(1,0,0;1.5708rad)
  Support = -> Extrude036 [Face6]
  sketch-geometry (4):
    g0: LineSegment StartX=-3.15 StartY=1.55 StartZ=0 EndX=3.15 EndY=1.55 EndZ=0
    g1: LineSegment StartX=3.15 StartY=1.55 StartZ=0 EndX=3.15 EndY=-1.55 EndZ=0
    g2: LineSegment StartX=3.15 StartY=-1.55 StartZ=0 EndX=-3.15 EndY=-1.55 EndZ=0
    g3: LineSegment StartX=-3.15 StartY=-1.55 StartZ=0 EndX=-3.15 EndY=1.55 EndZ=0
  constraints (12):
    c: Coincident(g0,g1)
    c: Coincident(g1,g2)
    c: Coincident(g2,g3)
    c: Coincident(g3,g0)
    c: Horizontal(g0)
    c: Horizontal(g2)
    c: Vertical(g1)
    c: Vertical(g3)
    c: PointOnObject(g0,g-4)
    c: PointOnObject(g0,g-3)
    c: DistanceY(g0,g2) = -3.1
    c: Symmetric(g0,g1,g-1)
FEATURE [Part::Extrusion] Extrude037
  Base = -> Sketch034
  Dir = (0,7.7,0)
  Solid = true
FEATURE [Part::Cut] Cut014
  Base = -> Extrude036
  Tool = -> Extrude037
FEATURE [Part::Chamfer] Chamfer004
  Base = -> Cut014
  Edges = 4 edges r=0.5: [Edge7,Edge9,Edge15,Edge17]
FEATURE [Part::Chamfer] Chamfer005
  Base = -> Chamfer004
  Edges = 1 edges r=1.2: [Edge13]
FEATURE [Sketcher::SketchObject] Sketch035
  ExternalGeometry = -> [Chamfer005]
  Placement = pos=(0,0,5.95) rot=(0,0,1;0rad)
  Support = -> Chamfer005 [Face5]
  sketch-geometry (4):
    g0: LineSegment StartX=-3 StartY=0 StartZ=0 EndX=3 EndY=0 EndZ=0
    g1: LineSegment StartX=3 StartY=0 StartZ=0 EndX=3 EndY=-3.1 EndZ=0
    g2: LineSegment StartX=3 StartY=-3.1 StartZ=0 EndX=-3 EndY=-3.1 EndZ=0
    g3: LineSegment StartX=-3 StartY=-3.1 StartZ=0 EndX=-3 EndY=0 EndZ=0
  constraints (12):
    c: Coincident(g0,g1)
    c: Coincident(g1,g2)
    c: Coincident(g2,g3)
    c: Coincident(g3,g0)
    c: Horizontal(g0)
    c: Horizontal(g2)
    c: Vertical(g1)
    c: Vertical(g3)
    c: PointOnObject(g0,g-1)
    c: DistanceX(g-3,g0) = 0.15
    c: Symmetric(g0,g0,g-2)
    c: DistanceY(g0,g1) = -3.1
FEATURE [Part::Extrusion] Extrude038
  Base = -> Sketch035
  Dir = (0,0,6.3)
  Solid = true
FEATURE [Sketcher::SketchObject] Sketch036
  ExternalGeometry = -> [Extrude038]
  Placement = pos=(0,-3.1,0) rot=(1,0,0;1.5708rad)
  Support = -> Extrude038 [Face3]
  sketch-geometry (1):
    g0: Circle CenterX=0 CenterY=9.5 CenterZ=0 NormalX=0 NormalY=0 NormalZ=1 Radius=1.65
  constraints (3):
    c: PointOnObject(g0,g-2)
    c: Radius(g0) = 1.65
    c: DistanceY(g0,g-3) = -3.55
FEATURE [Part::Extrusion] Extrude039
  Base = -> Sketch036
  Dir = (0,6,0)
  Solid = true
FEATURE [Part::Cut] Cut015
  Base = -> Extrude038
  Tool = -> Extrude039
FEATURE [Part::Fillet] Fillet003
  Base = -> Cut015
  Edges = 2 edges r=1.35: [Edge8,Edge11]
FEATURE [Part::MultiFuse] Fusion008
  Shapes = -> [Chamfer005]
FEATURE [Sketcher::SketchObject] Sketch037
  Placement = pos=(0,0,0) rot=(0,0.707107,0.707107;3.14159rad)
  Support = -> Fusion008 [Face7]
  sketch-geometry (4):
    g0: Circle CenterX=-1.27 CenterY=3.8 CenterZ=0 NormalX=0 NormalY=0 NormalZ=1 Radius=0.2
    g1: Circle CenterX=1.27 CenterY=3.8 CenterZ=0 NormalX=0 NormalY=0 NormalZ=1 Radius=0.2
    g2: Circle CenterX=-1.27 CenterY=-3.8 CenterZ=0 NormalX=0 NormalY=0 NormalZ=1 Radius=0.2
    g3: Circle CenterX=1.27 CenterY=-3.8 CenterZ=0 NormalX=0 NormalY=0 NormalZ=1 Radius=0.2
  constraints (9):
    c: Radius(g0) = 0.2
    c: Equal(g0,g1)
    c: Equal(g0,g3)
    c: Equal(g0,g2)
    c: Symmetric(g0,g1,g-2)
    c: Symmetric(g2,g3,g-2)
    c: Symmetric(g0,g2,g-1)
    c: DistanceX(g0,g1) = 2.54
    c: DistanceY(g1,g3) = -7.6
FEATURE [Part::Extrusion] Extrude040
  Base = -> Sketch037
  Dir = (0,7.8,0)
  Solid = true
FEATURE [Part::MultiFuse] Fusion009  label="Capteur_optique_002"
  Placement = pos=(-143,-46,-20.7) rot=(0,0,1;0rad)
  Shapes = -> [Fusion008,Fillet003,Extrude040]
FEATURE [Sketcher::SketchObject] Sketch038
  Placement = pos=(0,0,0) rot=(1,0,0;1.5708rad)
  sketch-geometry (1):
    g0: Circle CenterX=0 CenterY=0 CenterZ=0 NormalX=0 NormalY=0 NormalZ=1 Radius=4
  constraints (2):
    c: Coincident(g0,g-1)
    c: Radius(g0) = 4
FEATURE [Part::Extrusion] Extrude041
  Base = -> Sketch038
  Dir = (0,50,0)
  Solid = true
FEATURE [Sketcher::SketchObject] Sketch039
  Placement = pos=(0,0,0) rot=(0.57735,0.57735,0.57735;2.0944rad)
  sketch-geometry (1):
    g0: Circle CenterX=6 CenterY=0 CenterZ=0 NormalX=0 NormalY=0 NormalZ=1 Radius=2
  constraints (3):
    c: DistanceX(g-1,g0) = 6
    c: Radius(g0) = 2
    c: PointOnObject(g0,g-1)
FEATURE [Part::Extrusion] Extrude042
  Base = -> Sketch039
  Dir = (4,0,0)
  Solid = true
FEATURE [Part::Extrusion] Extrude043
  Base = -> Sketch039
  Dir = (-4,0,0)
  Solid = true
FEATURE [Part::Cut] Cut016
  Base = -> Extrude041
  Tool = -> Extrude042
FEATURE [Part::Cut] Cut017  label="Axe_D8_002"
  Base = -> Cut016
  Placement = pos=(-143,-86,0) rot=(0,0,1;0rad)
  Tool = -> Extrude043
FEATURE [Sketcher::SketchObject] Sketch040
  Placement = pos=(0,0,0) rot=(1,0,0;1.5708rad)
  sketch-geometry (1):
    g0: Circle CenterX=0 CenterY=0 CenterZ=0 NormalX=0 NormalY=0 NormalZ=1 Radius=2
  constraints (2):
    c: Coincident(g0,g-1)
    c: Radius(g0) = 2
FEATURE [Part::Extrusion] Extrude044  label="Axe_D4_002"
  Base = -> Sketch040
  Dir = (0,103.6,0)
  Placement = pos=(-91.2,-80,0) rot=(0,0,1;1.5708rad)
  Solid = true
FEATURE [Sketcher::SketchObject] Sketch041
  Placement = pos=(0,0,0) rot=(1,0,0;1.5708rad)
  sketch-geometry (8):
    g0: LineSegment StartX=-50 StartY=0 StartZ=0 EndX=50 EndY=0 EndZ=0
    g1: LineSegment StartX=50 StartY=0 StartZ=0 EndX=50 EndY=-2 EndZ=0
    g2: LineSegment StartX=50 StartY=-2 StartZ=0 EndX=47 EndY=-2 EndZ=0
    g3: LineSegment StartX=47 StartY=-2 StartZ=0 EndX=44 EndY=-16 EndZ=0
    g4: LineSegment StartX=44 StartY=-16 StartZ=0 EndX=-44 EndY=-16 EndZ=0
    g5: LineSegment StartX=-44 StartY=-16 StartZ=0 EndX=-47 EndY=-2 EndZ=0
    g6: LineSegment StartX=-47 StartY=-2 StartZ=0 EndX=-50 EndY=-2 EndZ=0
    g7: LineSegment StartX=-50 StartY=-2 StartZ=0 EndX=-50 EndY=0 EndZ=0
  constraints (24):
    c: PointOnObject(g0,g-1)
    c: Horizontal(g0)
    c: Coincident(g0,g1)
    c: Vertical(g1)
    c: Coincident(g1,g2)
    c: Horizontal(g2)
    c: Coincident(g2,g3)
    c: Coincident(g3,g4)
    c: Horizontal(g4)
    c: Coincident(g4,g5)
    c: Coincident(g5,g6)
    c: Horizontal(g6)
    c: Coincident(g6,g7)
    c: Coincident(g7,g0)
    c: Vertical(g7)
    c: DistanceY(g0,g6) = -2
    c: DistanceX(g6,g5) = 3
    c: DistanceX(g0,g0) = 100
    c: Symmetric(g0,g0,g-2)
    c: Symmetric(g6,g1,g-2)
    c: Symmetric(g5,g2,g-2)
    c: Symmetric(g4,g3,g-2)
    c: DistanceX(g4,g3) = 88
    c: DistanceY(g0,g4) = -16
FEATURE [Part::Extrusion] Extrude045  label="Plaque_alveolaire_002"
  Base = -> Sketch041
  Dir = (0,2000,0)
  Placement = pos=(-143,-62,22) rot=(0,0,1;3.14159rad)
  Solid = true
FEATURE [App::DocumentObjectGroup] Groupe001  label="Assemblage_miroir X=-143_001"
  Group = -> [Cut011,Fusion006,Extrude030,Part__Feature001,Extrude031,Fillet002,Fusion009,Cut017,Extrude044,Extrude045]
FEATURE [Sketcher::SketchObject] Sketch064
  Placement = pos=(0,0,0) rot=(1,0,0;1.5708rad)
  sketch-geometry (8):
    g0: LineSegment StartX=-21.15 StartY=16.15 StartZ=0 EndX=-16.15 EndY=21.15 EndZ=0
    g1: LineSegment StartX=-16.15 StartY=21.15 StartZ=0 EndX=16.15 EndY=21.15 EndZ=0
    g2: LineSegment StartX=16.15 StartY=21.15 StartZ=0 EndX=21.15 EndY=16.15 EndZ=0
    g3: LineSegment StartX=21.15 StartY=16.15 StartZ=0 EndX=21.15 EndY=-16.15 EndZ=0
    g4: LineSegment StartX=21.15 StartY=-16.15 StartZ=0 EndX=16.15 EndY=-21.15 EndZ=0
    g5: LineSegment StartX=16.15 StartY=-21.15 StartZ=0 EndX=-16.15 EndY=-21.15 EndZ=0
    g6: LineSegment StartX=-16.15 StartY=-21.15 StartZ=0 EndX=-21.15 EndY=-16.15 EndZ=0
    g7: LineSegment StartX=-21.15 StartY=-16.15 StartZ=0 EndX=-21.15 EndY=16.15 EndZ=0
  constraints (21):
    c: Coincident(g0,g1)
    c: Horizontal(g1)
    c: Coincident(g1,g2)
    c: Coincident(g2,g3)
    c: Vertical(g3)
    c: Coincident(g3,g4)
    c: Coincident(g4,g5)
    c: Horizontal(g5)
    c: Coincident(g5,g6)
    c: Coincident(g6,g7)
    c: Coincident(g7,g0)
    c: Angle(g7,g0) = 2.35619
    c: Distance(g0,g7) = 5
    c: Distance(g2,g7) = 42.3
    c: Distance(g5,g1) = 42.3
    c: Symmetric(g6,g3,g-2)
    c: Symmetric(g5,g4,g-2)
    c: Symmetric(g0,g2,g-2)
    c: Symmetric(g0,g1,g-2)
    c: Symmetric(g0,g6,g-1)
    c: Symmetric(g0,g5,g-1)
FEATURE [Part::Extrusion] Extrude097
  Base = -> Sketch064
  Dir = (0,48,0)
  Solid = true
FEATURE [Sketcher::SketchObject] Sketch065
  Placement = pos=(0,0,0) rot=(1,0,0;1.5708rad)
  Support = -> Extrude097 [Face9]
  sketch-geometry (1):
    g0: Circle CenterX=0 CenterY=0 CenterZ=0 NormalX=0 NormalY=0 NormalZ=1 Radius=11
  constraints (2):
    c: Coincident(g0,g-1)
    c: Radius(g0) = 11
FEATURE [Part::Extrusion] Extrude098
  Base = -> Sketch065
  Dir = (0,-2,0)
  Solid = true
FEATURE [Sketcher::SketchObject] Sketch066
  Placement = pos=(0,-2,0) rot=(1,0,0;1.5708rad)
  Support = -> Extrude098 [Face3]
  sketch-geometry (1):
    g0: Circle CenterX=0 CenterY=0 CenterZ=0 NormalX=0 NormalY=0 NormalZ=1 Radius=2.5
  constraints (2):
    c: Coincident(g0,g-1)
    c: Radius(g0) = 2.5
FEATURE [Part::Extrusion] Extrude099
  Base = -> Sketch066
  Dir = (0,-22,0)
  Solid = true
FEATURE [Part::Chamfer] Chamfer009
  Base = -> Extrude099
  Edges = 1 edges r=0.8: [Edge3]
FEATURE [Sketcher::SketchObject] Sketch067
  Placement = pos=(0,0,0) rot=(1,0,0;1.5708rad)
  Support = -> Extrude097 [Face9]
  sketch-geometry (4):
    g0: Circle CenterX=-15.5 CenterY=15.5 CenterZ=0 NormalX=0 NormalY=0 NormalZ=1 Radius=2
    g1: Circle CenterX=15.5 CenterY=15.5 CenterZ=0 NormalX=0 NormalY=0 NormalZ=1 Radius=2
    g2: Circle CenterX=-15.5 CenterY=-15.5 CenterZ=0 NormalX=0 NormalY=0 NormalZ=1 Radius=2
    g3: Circle CenterX=15.5 CenterY=-15.5 CenterZ=0 NormalX=0 NormalY=0 NormalZ=1 Radius=2
  constraints (9):
    c: Distance(g0,g1) = 31
    c: Distance(g0,g2) = 31
    c: Symmetric(g0,g2,g-1)
    c: Symmetric(g0,g1,g-2)
    c: Symmetric(g2,g3,g-2)
    c: Radius(g0) = 2
    c: Equal(g0,g1)
    c: Equal(g0,g2)
    c: Equal(g0,g3)
FEATURE [Part::Extrusion] Extrude100
  Base = -> Sketch067
  Dir = (0,4.5,0)
  Solid = true
FEATURE [Part::Cut] Cut038
  Base = -> Extrude097
  Tool = -> Extrude100
FEATURE [Sketcher::SketchObject] Sketch068
  Placement = pos=(0,0,0) rot=(1,0,0;1.5708rad)
  sketch-geometry (1):
    g0: Circle CenterX=0 CenterY=0 CenterZ=0 NormalX=0 NormalY=0 NormalZ=1 Radius=9
  constraints (2):
    c: Coincident(g0,g-1)
    c: Radius(g0) = 9
FEATURE [Part::Extrusion] Extrude101
  Base = -> Sketch068
  Dir = (0,25,0)
  Solid = true
FEATURE [Sketcher::SketchObject] Sketch069
  Placement = pos=(0,0,0) rot=(1,0,0;1.5708rad)
  sketch-geometry (1):
    g0: Circle CenterX=0 CenterY=0 CenterZ=0 NormalX=0 NormalY=0 NormalZ=1 Radius=2.5
  constraints (2):
    c: Coincident(g0,g-1)
    c: Radius(g0) = 2.5
FEATURE [Part::Extrusion] Extrude102
  Base = -> Sketch069
  Dir = (0,10,0)
  Solid = true
FEATURE [Part::Cut] Cut039
  Base = -> Extrude101
  Tool = -> Extrude102
FEATURE [Sketcher::SketchObject] Sketch070
  Placement = pos=(0,25,0) rot=(0,0.707107,0.707107;3.14159rad)
  Support = -> Cut039 [Face3]
  sketch-geometry (1):
    g0: Circle CenterX=0 CenterY=0 CenterZ=0 NormalX=0 NormalY=0 NormalZ=1 Radius=4
  constraints (2):
    c: Coincident(g0,g-1)
    c: Radius(g0) = 4
FEATURE [Part::Extrusion] Extrude103
  Base = -> Sketch070
  Dir = (0,-10,0)
  Solid = true
FEATURE [Part::Cut] Cut040  label="Accouplement_003"
  Base = -> Cut039
  Placement = pos=(-286,-12,0) rot=(1,0,0;3.14159rad)
  Tool = -> Extrude103
FEATURE [Part::Fuse] Fusion022
  Base = -> Extrude098
  Tool = -> Cut038
FEATURE [Part::Fuse] Fusion023  label="Moteur_003"
  Base = -> Chamfer009
  Placement = pos=(-286,0,0) rot=(0,0,1;0rad)
  Tool = -> Fusion022
FEATURE [Sketcher::SketchObject] Sketch071
  Placement = pos=(0,0,0) rot=(1,0,0;1.5708rad)
  sketch-geometry (4):
    g0: LineSegment StartX=-50 StartY=0 StartZ=0 EndX=-47 EndY=0 EndZ=0
    g1: LineSegment StartX=47 StartY=0 StartZ=0 EndX=50 EndY=0 EndZ=0
    g2: ArcOfCircle CenterX=0 CenterY=0 CenterZ=0 NormalX=0 NormalY=0 NormalZ=1 Radius=47 StartAngle=3.14159 EndAngle=6.28319
    g3: ArcOfCircle CenterX=0 CenterY=0 CenterZ=0 NormalX=0 NormalY=0 NormalZ=1 Radius=50 StartAngle=3.14159 EndAngle=6.28319
  constraints (13):
    c: Horizontal(g0)
    c: PointOnObject(g1,g-1)
    c: Horizontal(g1)
    c: Coincident(g2,g-1)
    c: PointOnObject(g2,g-1)
    c: Coincident(g3,g-1)
    c: Coincident(g3,g1)
    c: PointOnObject(g3,g-1)
    c: Coincident(g0,g3)
    c: Coincident(g0,g2)
    c: Distance(g0,g1) = 100
    c: Distance(g0,g0) = 3
    c: Coincident(g1,g2)
FEATURE [Part::Extrusion] Extrude104  label="Demi_tube_sous_miroir_003"
  Base = -> Sketch071
  Dir = (0,2000,0)
  Placement = pos=(-286,-62,20) rot=(0,0,1;3.14159rad)
  Solid = true
FEATURE [Part::Feature] Part__Feature005  label="Coussinet_autolub_C2-151-8-128_003"
  Placement = pos=(-286,-46,0) rot=(0,0,1;1.5708rad)
  shape: bbox 16 x 8 x 16 mm, 12 faces (baked)
FEATURE [Sketcher::SketchObject] Sketch072
  Placement = pos=(0,0,0) rot=(1,0,0;1.5708rad)
  sketch-geometry (21):
    g0: Circle CenterX=0 CenterY=0 CenterZ=0 NormalX=0 NormalY=0 NormalZ=1 Radius=6
    g1: LineSegment StartX=-20.5 StartY=15 StartZ=0 EndX=20.5 EndY=15 EndZ=0
    g2: ArcOfCircle CenterX=20.5 CenterY=13 CenterZ=0 NormalX=0 NormalY=0 NormalZ=1 Radius=2 StartAngle=6.28319 EndAngle=7.85398
    g3: LineSegment StartX=22.5 StartY=13 StartZ=0 EndX=22.5 EndY=-73 EndZ=0
    g4: LineSegment StartX=-22.5 StartY=13 StartZ=0 EndX=-22.5 EndY=-73 EndZ=0
    g5: ArcOfCircle CenterX=-20.5 CenterY=13 CenterZ=0 NormalX=0 NormalY=0 NormalZ=1 Radius=2 StartAngle=1.5708 EndAngle=3.14159
    g6: ArcOfCircle CenterX=-20.5 CenterY=-73 CenterZ=0 NormalX=0 NormalY=0 NormalZ=1 Radius=2 StartAngle=3.14159 EndAngle=4.71239
    g7: ArcOfCircle CenterX=20.5 CenterY=-73 CenterZ=0 NormalX=0 NormalY=0 NormalZ=1 Radius=2 StartAngle=4.71239 EndAngle=6.28319
    g8: LineSegment StartX=-20.5 StartY=-75 StartZ=0 EndX=20.5 EndY=-75 EndZ=0
    g9: ArcOfCircle CenterX=0 CenterY=-16.7 CenterZ=0 NormalX=0 NormalY=0 NormalZ=1 Radius=1.5 StartAngle=0 EndAngle=3.14159
    g10: ArcOfCircle CenterX=0 CenterY=-24.3 CenterZ=0 NormalX=0 NormalY=0 NormalZ=1 Radius=1.5 StartAngle=3.14159 EndAngle=6.28319
    g11: LineSegment StartX=-1.5 StartY=-16.7 StartZ=0 EndX=-1.5 EndY=-24.3 EndZ=0
    g12: LineSegment StartX=1.5 StartY=-16.7 StartZ=0 EndX=1.5 EndY=-24.3 EndZ=0
    g13: Circle CenterX=-12.5 CenterY=-45 CenterZ=0 NormalX=0 NormalY=0 NormalZ=1 Radius=3.5
    g14: Circle CenterX=12.5 CenterY=-45 CenterZ=0 NormalX=0 NormalY=0 NormalZ=1 Radius=3.5
    g15: Circle CenterX=-12.5 CenterY=-65 CenterZ=0 NormalX=0 NormalY=0 NormalZ=1 Radius=3.5
    g16: Circle CenterX=12.5 CenterY=-65 CenterZ=0 NormalX=0 NormalY=0 NormalZ=1 Radius=3.5
    g17: LineSegment [constr] StartX=-12.5 StartY=-45 StartZ=0 EndX=12.5 EndY=-45 EndZ=0
    g18: LineSegment [constr] StartX=-12.5 StartY=-45 StartZ=0 EndX=-12.5 EndY=-65 EndZ=0
    g19: LineSegment [constr] StartX=-12.5 StartY=-65 StartZ=0 EndX=12.5 EndY=-65 EndZ=0
    g20: LineSegment [constr] StartX=12.5 StartY=-45 StartZ=0 EndX=12.5 EndY=-65 EndZ=0
  constraints (59):
    c: Coincident(g0,g-1)
    c: Radius(g0) = 6
    c: Horizontal(g1)
    c: Coincident(g2,g1)
    c: Coincident(g3,g2)
    c: Vertical(g3)
    c: Vertical(g4)
    c: Coincident(g5,g1)
    c: Coincident(g5,g4)
    c: Coincident(g7,g3)
    c: Coincident(g8,g6)
    c: Coincident(g8,g7)
    c: Tangent(g8,g7)
    c: Tangent(g5,g4)
    c: Tangent(g5,g1)
    c: Tangent(g1,g2)
    c: Tangent(g2,g3)
    c: Coincident(g4,g6)
    c: Tangent(g6,g4)
    c: Tangent(g6,g8)
    c: Horizontal(g8)
    c: Tangent(g7,g3)
    c: Distance(g4,g2) = 45
    c: Symmetric(g4,g2,g-2)
    c: Distance(g1,g6) = 90
    c: DistanceY(g-1,g1) = 15
    c: Tangent(g9,g12) = 1.5708
    c: Tangent(g9,g11) = -1.5708
    c: Tangent(g11,g10) = -1.5708
    c: Tangent(g12,g10) = 1.5708
    c: Vertical(g11)
    c: Equal(g9,g10)
    c: PointOnObject(g9,g-2)
    c: Distance(g-1,g9) = 16.7
    c: Distance(g9,g10) = 7.6
    c: Radius(g9) = 1.5
    c: Radius(g13) = 3.5
    c: Equal(g13,g14)
    c: Equal(g13,g16)
    c: Equal(g13,g15)
    c: Radius(g5) = 2
    c: Equal(g5,g7)
    c: Equal(g5,g6)
    c: DistanceY(g-1,g13) = -45
    c: Coincident(g17,g13)
    c: Coincident(g17,g14)
    c: Horizontal(g17)
    c: Coincident(g18,g13)
    c: Coincident(g18,g15)
    c: Coincident(g19,g15)
    c: Coincident(g19,g16)
    c: Horizontal(g19)
    c: Coincident(g20,g14)
    c: Coincident(g20,g16)
    c: Vertical(g18)
    c: Vertical(g20)
    c: Distance(g13,g15) = 20
    c: Distance(g13,g14) = 25
    c: Symmetric(g13,g14,g-2)
FEATURE [Part::Extrusion] Extrude105  label="Plaque_support_003"
  Base = -> Sketch072
  Dir = (0,6,0)
  Placement = pos=(-286,-46,0) rot=(0,0,1;0rad)
  Solid = true
FEATURE [Sketcher::SketchObject] Sketch073
  Placement = pos=(0,0,0) rot=(0.57735,0.57735,0.57735;2.0944rad)
  sketch-geometry (8):
    g0: LineSegment StartX=0 StartY=33 StartZ=0 EndX=-2 EndY=33 EndZ=0
    g1: LineSegment StartX=-2 StartY=33 StartZ=0 EndX=-2 EndY=-24 EndZ=0
    g2: ArcOfCircle CenterX=-4 CenterY=-24 CenterZ=0 NormalX=0 NormalY=0 NormalZ=1 Radius=2 StartAngle=4.71239 EndAngle=6.28319
    g3: LineSegment StartX=-4 StartY=-26 StartZ=0 EndX=-38 EndY=-26 EndZ=0
    g4: LineSegment StartX=-38 StartY=-26 StartZ=0 EndX=-38 EndY=-28 EndZ=0
    g5: LineSegment StartX=-38 StartY=-28 StartZ=0 EndX=-4 EndY=-28 EndZ=0
    g6: ArcOfCircle CenterX=-4 CenterY=-24 CenterZ=0 NormalX=0 NormalY=0 NormalZ=1 Radius=4 StartAngle=4.71239 EndAngle=6.28319
    g7: LineSegment StartX=0 StartY=-24 StartZ=0 EndX=0 EndY=33 EndZ=0
  constraints (22):
    c: PointOnObject(g0,g-2)
    c: Horizontal(g0)
    c: Coincident(g0,g1)
    c: Vertical(g1)
    c: Tangent(g1,g2) = 1.5708
    c: Tangent(g2,g3) = 1.5708
    c: Coincident(g3,g4)
    c: Vertical(g4)
    c: Coincident(g4,g5)
    c: Horizontal(g5)
    c: Tangent(g5,g6) = -1.5708
    c: PointOnObject(g6,g-2)
    c: Tangent(g6,g7) = -1.5708
    c: Coincident(g7,g0)
    c: Horizontal(g3)
    c: DistanceX(g0,g0) = 2
    c: Radius(g2) = 2
    c: Radius(g6) = 4
    c: DistanceY(g3,g4) = -2
    c: Distance(g-1,g0) = 33
    c: DistanceY(g-1,g5) = -28
    c: DistanceX(g6,g4) = -38
FEATURE [Part::Extrusion] Extrude106
  Base = -> Sketch073
  Dir = (-32.5,0,0)
  Solid = true
FEATURE [Part::Extrusion] Extrude107
  Base = -> Sketch073
  Dir = (32.5,0,0)
  Solid = true
FEATURE [Part::MultiFuse] Fusion024
  Shapes = -> [Extrude106,Extrude107]
FEATURE [Sketcher::SketchObject] Sketch074
  Placement = pos=(0,-2,0) rot=(1,0,0;1.5708rad)
  Support = -> Fusion024 [Face3]
  sketch-geometry (9):
    g0: ArcOfCircle CenterX=0 CenterY=0 CenterZ=0 NormalX=0 NormalY=0 NormalZ=1 Radius=32.5 StartAngle=0 EndAngle=3.14159
    g1: LineSegment StartX=-32.5 StartY=0 StartZ=0 EndX=-32.5 EndY=34 EndZ=0
    g2: LineSegment StartX=-32.5 StartY=34 StartZ=0 EndX=32.5 EndY=34 EndZ=0
    g3: LineSegment StartX=32.5 StartY=34 StartZ=0 EndX=32.5 EndY=0 EndZ=0
    g4: Circle CenterX=0 CenterY=0 CenterZ=0 NormalX=0 NormalY=0 NormalZ=1 Radius=11
    g5: Circle CenterX=-15.5 CenterY=15.5 CenterZ=0 NormalX=0 NormalY=0 NormalZ=1 Radius=2
    g6: Circle CenterX=15.5 CenterY=15.5 CenterZ=0 NormalX=0 NormalY=0 NormalZ=1 Radius=2
    g7: Circle CenterX=-15.5 CenterY=-15.5 CenterZ=0 NormalX=0 NormalY=0 NormalZ=1 Radius=2
    g8: Circle CenterX=15.5 CenterY=-15.5 CenterZ=0 NormalX=0 NormalY=0 NormalZ=1 Radius=2
  constraints (23):
    c: Coincident(g0,g-1)
    c: PointOnObject(g0,g-1)
    c: PointOnObject(g0,g-1)
    c: Coincident(g1,g0)
    c: Vertical(g1)
    c: Coincident(g1,g2)
    c: Horizontal(g2)
    c: Coincident(g2,g3)
    c: Coincident(g3,g0)
    c: Vertical(g3)
    c: DistanceY(g1,g0) = -34
    c: Coincident(g4,g-1)
    c: Radius(g4) = 11
    c: DistanceX(g1,g2) = 65
    c: Radius(g5) = 2
    c: Equal(g5,g6)
    c: Equal(g5,g8)
    c: Equal(g5,g7)
    c: Symmetric(g5,g6,g-2)
    c: Symmetric(g5,g7,g-1)
    c: Symmetric(g7,g8,g-2)
    c: DistanceX(g5,g6) = 31
    c: DistanceY(g5,g7) = -31
FEATURE [Part::Extrusion] Extrude108
  Base = -> Sketch074
  Dir = (0,2,0)
  Solid = true
FEATURE [Part::Cut] Cut041
  Base = -> Fusion024
  Tool = -> Extrude108
FEATURE [Sketcher::SketchObject] Sketch075
  ExternalGeometry = -> [Cut041]
  Placement = pos=(0,0,-26) rot=(0,0,1;0rad)
  Support = -> Cut041 [Face5]
  sketch-geometry (5):
    g0: Circle CenterX=-25 CenterY=-12 CenterZ=0 NormalX=0 NormalY=0 NormalZ=1 Radius=3.5
    g1: Circle CenterX=-25 CenterY=-30 CenterZ=0 NormalX=0 NormalY=0 NormalZ=1 Radius=3.5
    g2: Circle CenterX=25 CenterY=-12 CenterZ=0 NormalX=0 NormalY=0 NormalZ=1 Radius=3.5
    g3: Circle CenterX=25 CenterY=-30 CenterZ=0 NormalX=0 NormalY=0 NormalZ=1 Radius=3.5
    g4: LineSegment [constr] StartX=-25 StartY=-12 StartZ=0 EndX=-25 EndY=-30 EndZ=0
  constraints (12):
    c: Radius(g0) = 3.5
    c: Equal(g0,g2)
    c: Equal(g0,g3)
    c: Equal(g0,g1)
    c: Symmetric(g0,g2,g-2)
    c: Symmetric(g1,g3,g-2)
    c: Coincident(g4,g0)
    c: Coincident(g4,g1)
    c: Vertical(g4)
    c: DistanceY(g0,g1) = -18
    c: DistanceY(g-3,g1) = 8
    c: DistanceX(g0,g2) = 50
FEATURE [Part::Extrusion] Extrude109
  Base = -> Sketch075
  Dir = (0,0,-2)
  Solid = true
FEATURE [Part::Cut] Cut042
  Base = -> Cut041
  Tool = -> Extrude109
FEATURE [Part::Fillet] Fillet009  label="Plaque_moteur_003"
  Base = -> Cut042
  Edges = 2 edges r=4: [Edge5,Edge59]
  Placement = pos=(-286,0,0) rot=(0,0,1;0rad)
FEATURE [Sketcher::SketchObject] Sketch076
  Placement = pos=(0,0,0) rot=(1,0,0;1.5708rad)
  sketch-geometry (4):
    g0: LineSegment StartX=-3.15 StartY=5.95 StartZ=0 EndX=3.15 EndY=5.95 EndZ=0
    g1: LineSegment StartX=3.15 StartY=5.95 StartZ=0 EndX=3.15 EndY=-5.95 EndZ=0
    g2: LineSegment StartX=3.15 StartY=-5.95 StartZ=0 EndX=-3.15 EndY=-5.95 EndZ=0
    g3: LineSegment StartX=-3.15 StartY=-5.95 StartZ=0 EndX=-3.15 EndY=5.95 EndZ=0
  constraints (12):
    c: Coincident(g0,g1)
    c: Coincident(g1,g2)
    c: Coincident(g2,g3)
    c: Coincident(g3,g0)
    c: Horizontal(g0)
    c: Horizontal(g2)
    c: Vertical(g1)
    c: Vertical(g3)
    c: DistanceX(g0,g0) = 6.3
    c: DistanceY(g0,g2) = -11.9
    c: Symmetric(g0,g0,g-2)
    c: Symmetric(g0,g1,g-1)
FEATURE [Part::Extrusion] Extrude110
  Base = -> Sketch076
  Dir = (0,-10.8,0)
  Solid = true
FEATURE [Sketcher::SketchObject] Sketch077
  ExternalGeometry = -> [Extrude110]
  Placement = pos=(0,-10.8,0) rot=(1,0,0;1.5708rad)
  Support = -> Extrude110 [Face6]
  sketch-geometry (4):
    g0: LineSegment StartX=-3.15 StartY=1.55 StartZ=0 EndX=3.15 EndY=1.55 EndZ=0
    g1: LineSegment StartX=3.15 StartY=1.55 StartZ=0 EndX=3.15 EndY=-1.55 EndZ=0
    g2: LineSegment StartX=3.15 StartY=-1.55 StartZ=0 EndX=-3.15 EndY=-1.55 EndZ=0
    g3: LineSegment StartX=-3.15 StartY=-1.55 StartZ=0 EndX=-3.15 EndY=1.55 EndZ=0
  constraints (12):
    c: Coincident(g0,g1)
    c: Coincident(g1,g2)
    c: Coincident(g2,g3)
    c: Coincident(g3,g0)
    c: Horizontal(g0)
    c: Horizontal(g2)
    c: Vertical(g1)
    c: Vertical(g3)
    c: PointOnObject(g0,g-4)
    c: PointOnObject(g0,g-3)
    c: DistanceY(g0,g2) = -3.1
    c: Symmetric(g0,g1,g-1)
FEATURE [Part::Extrusion] Extrude111
  Base = -> Sketch077
  Dir = (0,7.7,0)
  Solid = true
FEATURE [Part::Cut] Cut043
  Base = -> Extrude110
  Tool = -> Extrude111
FEATURE [Part::Chamfer] Chamfer010
  Base = -> Cut043
  Edges = 4 edges r=0.5: [Edge7,Edge9,Edge15,Edge17]
FEATURE [Part::Chamfer] Chamfer011
  Base = -> Chamfer010
  Edges = 1 edges r=1.2: [Edge13]
FEATURE [Sketcher::SketchObject] Sketch078
  ExternalGeometry = -> [Chamfer011]
  Placement = pos=(0,0,5.95) rot=(0,0,1;0rad)
  Support = -> Chamfer011 [Face5]
  sketch-geometry (4):
    g0: LineSegment StartX=-3 StartY=0 StartZ=0 EndX=3 EndY=0 EndZ=0
    g1: LineSegment StartX=3 StartY=0 StartZ=0 EndX=3 EndY=-3.1 EndZ=0
    g2: LineSegment StartX=3 StartY=-3.1 StartZ=0 EndX=-3 EndY=-3.1 EndZ=0
    g3: LineSegment StartX=-3 StartY=-3.1 StartZ=0 EndX=-3 EndY=0 EndZ=0
  constraints (12):
    c: Coincident(g0,g1)
    c: Coincident(g1,g2)
    c: Coincident(g2,g3)
    c: Coincident(g3,g0)
    c: Horizontal(g0)
    c: Horizontal(g2)
    c: Vertical(g1)
    c: Vertical(g3)
    c: PointOnObject(g0,g-1)
    c: DistanceX(g-3,g0) = 0.15
    c: Symmetric(g0,g0,g-2)
    c: DistanceY(g0,g1) = -3.1
FEATURE [Part::Extrusion] Extrude112
  Base = -> Sketch078
  Dir = (0,0,6.3)
  Solid = true
FEATURE [Sketcher::SketchObject] Sketch079
  ExternalGeometry = -> [Extrude112]
  Placement = pos=(0,-3.1,0) rot=(1,0,0;1.5708rad)
  Support = -> Extrude112 [Face3]
  sketch-geometry (1):
    g0: Circle CenterX=0 CenterY=9.5 CenterZ=0 NormalX=0 NormalY=0 NormalZ=1 Radius=1.65
  constraints (3):
    c: PointOnObject(g0,g-2)
    c: Radius(g0) = 1.65
    c: DistanceY(g0,g-3) = -3.55
FEATURE [Part::Extrusion] Extrude113
  Base = -> Sketch079
  Dir = (0,6,0)
  Solid = true
FEATURE [Part::Cut] Cut044
  Base = -> Extrude112
  Tool = -> Extrude113
FEATURE [Part::Fillet] Fillet010
  Base = -> Cut044
  Edges = 2 edges r=1.35: [Edge8,Edge11]
FEATURE [Part::MultiFuse] Fusion025
  Shapes = -> [Chamfer011]
FEATURE [Sketcher::SketchObject] Sketch080
  Placement = pos=(0,0,0) rot=(0,0.707107,0.707107;3.14159rad)
  Support = -> Fusion025 [Face7]
  sketch-geometry (4):
    g0: Circle CenterX=-1.27 CenterY=3.8 CenterZ=0 NormalX=0 NormalY=0 NormalZ=1 Radius=0.2
    g1: Circle CenterX=1.27 CenterY=3.8 CenterZ=0 NormalX=0 NormalY=0 NormalZ=1 Radius=0.2
    g2: Circle CenterX=-1.27 CenterY=-3.8 CenterZ=0 NormalX=0 NormalY=0 NormalZ=1 Radius=0.2
    g3: Circle CenterX=1.27 CenterY=-3.8 CenterZ=0 NormalX=0 NormalY=0 NormalZ=1 Radius=0.2
  constraints (9):
    c: Radius(g0) = 0.2
    c: Equal(g0,g1)
    c: Equal(g0,g3)
    c: Equal(g0,g2)
    c: Symmetric(g0,g1,g-2)
    c: Symmetric(g2,g3,g-2)
    c: Symmetric(g0,g2,g-1)
    c: DistanceX(g0,g1) = 2.54
    c: DistanceY(g1,g3) = -7.6
FEATURE [Part::Extrusion] Extrude114
  Base = -> Sketch080
  Dir = (0,7.8,0)
  Solid = true
FEATURE [Part::MultiFuse] Fusion026  label="Capteur_optique_003"
  Placement = pos=(-286,-46,-20.7) rot=(0,0,1;0rad)
  Shapes = -> [Fusion025,Fillet010,Extrude114]
FEATURE [Sketcher::SketchObject] Sketch081
  Placement = pos=(0,0,0) rot=(1,0,0;1.5708rad)
  sketch-geometry (1):
    g0: Circle CenterX=0 CenterY=0 CenterZ=0 NormalX=0 NormalY=0 NormalZ=1 Radius=4
  constraints (2):
    c: Coincident(g0,g-1)
    c: Radius(g0) = 4
FEATURE [Part::Extrusion] Extrude115
  Base = -> Sketch081
  Dir = (0,50,0)
  Solid = true
FEATURE [Sketcher::SketchObject] Sketch082
  Placement = pos=(0,0,0) rot=(0.57735,0.57735,0.57735;2.0944rad)
  sketch-geometry (1):
    g0: Circle CenterX=6 CenterY=0 CenterZ=0 NormalX=0 NormalY=0 NormalZ=1 Radius=2
  constraints (3):
    c: DistanceX(g-1,g0) = 6
    c: Radius(g0) = 2
    c: PointOnObject(g0,g-1)
FEATURE [Part::Extrusion] Extrude116
  Base = -> Sketch082
  Dir = (4,0,0)
  Solid = true
FEATURE [Part::Extrusion] Extrude117
  Base = -> Sketch082
  Dir = (-4,0,0)
  Solid = true
FEATURE [Part::Cut] Cut045
  Base = -> Extrude115
  Tool = -> Extrude116
FEATURE [Part::Cut] Cut046  label="Axe_D8_003"
  Base = -> Cut045
  Placement = pos=(-286,-86,0) rot=(0,0,1;0rad)
  Tool = -> Extrude117
FEATURE [Sketcher::SketchObject] Sketch083
  Placement = pos=(0,0,0) rot=(1,0,0;1.5708rad)
  sketch-geometry (1):
    g0: Circle CenterX=0 CenterY=0 CenterZ=0 NormalX=0 NormalY=0 NormalZ=1 Radius=2
  constraints (2):
    c: Coincident(g0,g-1)
    c: Radius(g0) = 2
FEATURE [Part::Extrusion] Extrude118  label="Axe_D4_003"
  Base = -> Sketch083
  Dir = (0,103.6,0)
  Placement = pos=(-234.2,-80,0) rot=(0,0,1;1.5708rad)
  Solid = true
FEATURE [Sketcher::SketchObject] Sketch084
  Placement = pos=(0,0,0) rot=(1,0,0;1.5708rad)
  sketch-geometry (8):
    g0: LineSegment StartX=-50 StartY=0 StartZ=0 EndX=50 EndY=0 EndZ=0
    g1: LineSegment StartX=50 StartY=0 StartZ=0 EndX=50 EndY=-2 EndZ=0
    g2: LineSegment StartX=50 StartY=-2 StartZ=0 EndX=47 EndY=-2 EndZ=0
    g3: LineSegment StartX=47 StartY=-2 StartZ=0 EndX=44 EndY=-16 EndZ=0
    g4: LineSegment StartX=44 StartY=-16 StartZ=0 EndX=-44 EndY=-16 EndZ=0
    g5: LineSegment StartX=-44 StartY=-16 StartZ=0 EndX=-47 EndY=-2 EndZ=0
    g6: LineSegment StartX=-47 StartY=-2 StartZ=0 EndX=-50 EndY=-2 EndZ=0
    g7: LineSegment StartX=-50 StartY=-2 StartZ=0 EndX=-50 EndY=0 EndZ=0
  constraints (24):
    c: PointOnObject(g0,g-1)
    c: Horizontal(g0)
    c: Coincident(g0,g1)
    c: Vertical(g1)
    c: Coincident(g1,g2)
    c: Horizontal(g2)
    c: Coincident(g2,g3)
    c: Coincident(g3,g4)
    c: Horizontal(g4)
    c: Coincident(g4,g5)
    c: Coincident(g5,g6)
    c: Horizontal(g6)
    c: Coincident(g6,g7)
    c: Coincident(g7,g0)
    c: Vertical(g7)
    c: DistanceY(g0,g6) = -2
    c: DistanceX(g6,g5) = 3
    c: DistanceX(g0,g0) = 100
    c: Symmetric(g0,g0,g-2)
    c: Symmetric(g6,g1,g-2)
    c: Symmetric(g5,g2,g-2)
    c: Symmetric(g4,g3,g-2)
    c: DistanceX(g4,g3) = 88
    c: DistanceY(g0,g4) = -16
FEATURE [Part::Extrusion] Extrude119  label="Plaque_alveolaire_003"
  Base = -> Sketch084
  Dir = (0,2000,0)
  Placement = pos=(-286,-62,22) rot=(0,0,1;3.14159rad)
  Solid = true
FEATURE [App::DocumentObjectGroup] Groupe005  label="Assemblage_miroir X=-286_001"
  Group = -> [Cut040,Fusion023,Extrude104,Part__Feature005,Extrude105,Fillet009,Fusion026,Cut046,Extrude118,Extrude119]
FEATURE [Sketcher::SketchObject] Sketch086
  Placement = pos=(0,0,0) rot=(1,0,0;1.5708rad)
  sketch-geometry (8):
    g0: LineSegment StartX=-21.15 StartY=16.15 StartZ=0 EndX=-16.15 EndY=21.15 EndZ=0
    g1: LineSegment StartX=-16.15 StartY=21.15 StartZ=0 EndX=16.15 EndY=21.15 EndZ=0
    g2: LineSegment StartX=16.15 StartY=21.15 StartZ=0 EndX=21.15 EndY=16.15 EndZ=0
    g3: LineSegment StartX=21.15 StartY=16.15 StartZ=0 EndX=21.15 EndY=-16.15 EndZ=0
    g4: LineSegment StartX=21.15 StartY=-16.15 StartZ=0 EndX=16.15 EndY=-21.15 EndZ=0
    g5: LineSegment StartX=16.15 StartY=-21.15 StartZ=0 EndX=-16.15 EndY=-21.15 EndZ=0
    g6: LineSegment StartX=-16.15 StartY=-21.15 StartZ=0 EndX=-21.15 EndY=-16.15 EndZ=0
    g7: LineSegment StartX=-21.15 StartY=-16.15 StartZ=0 EndX=-21.15 EndY=16.15 EndZ=0
  constraints (21):
    c: Coincident(g0,g1)
    c: Horizontal(g1)
    c: Coincident(g1,g2)
    c: Coincident(g2,g3)
    c: Vertical(g3)
    c: Coincident(g3,g4)
    c: Coincident(g4,g5)
    c: Horizontal(g5)
    c: Coincident(g5,g6)
    c: Coincident(g6,g7)
    c: Coincident(g7,g0)
    c: Angle(g7,g0) = 2.35619
    c: Distance(g0,g7) = 5
    c: Distance(g2,g7) = 42.3
    c: Distance(g5,g1) = 42.3
    c: Symmetric(g6,g3,g-2)
    c: Symmetric(g5,g4,g-2)
    c: Symmetric(g0,g2,g-2)
    c: Symmetric(g0,g1,g-2)
    c: Symmetric(g0,g6,g-1)
    c: Symmetric(g0,g5,g-1)
FEATURE [Part::Extrusion] Extrude121
  Base = -> Sketch086
  Dir = (0,48,0)
  Solid = true
FEATURE [Sketcher::SketchObject] Sketch087
  Placement = pos=(0,0,0) rot=(1,0,0;1.5708rad)
  Support = -> Extrude121 [Face9]
  sketch-geometry (1):
    g0: Circle CenterX=0 CenterY=0 CenterZ=0 NormalX=0 NormalY=0 NormalZ=1 Radius=11
  constraints (2):
    c: Coincident(g0,g-1)
    c: Radius(g0) = 11
FEATURE [Part::Extrusion] Extrude122
  Base = -> Sketch087
  Dir = (0,-2,0)
  Solid = true
FEATURE [Sketcher::SketchObject] Sketch088
  Placement = pos=(0,-2,0) rot=(1,0,0;1.5708rad)
  Support = -> Extrude122 [Face3]
  sketch-geometry (1):
    g0: Circle CenterX=0 CenterY=0 CenterZ=0 NormalX=0 NormalY=0 NormalZ=1 Radius=2.5
  constraints (2):
    c: Coincident(g0,g-1)
    c: Radius(g0) = 2.5
FEATURE [Part::Extrusion] Extrude123
  Base = -> Sketch088
  Dir = (0,-22,0)
  Solid = true
FEATURE [Part::Chamfer] Chamfer012
  Base = -> Extrude123
  Edges = 1 edges r=0.8: [Edge3]
FEATURE [Sketcher::SketchObject] Sketch089
  Placement = pos=(0,0,0) rot=(1,0,0;1.5708rad)
  Support = -> Extrude121 [Face9]
  sketch-geometry (4):
    g0: Circle CenterX=-15.5 CenterY=15.5 CenterZ=0 NormalX=0 NormalY=0 NormalZ=1 Radius=2
    g1: Circle CenterX=15.5 CenterY=15.5 CenterZ=0 NormalX=0 NormalY=0 NormalZ=1 Radius=2
    g2: Circle CenterX=-15.5 CenterY=-15.5 CenterZ=0 NormalX=0 NormalY=0 NormalZ=1 Radius=2
    g3: Circle CenterX=15.5 CenterY=-15.5 CenterZ=0 NormalX=0 NormalY=0 NormalZ=1 Radius=2
  constraints (9):
    c: Distance(g0,g1) = 31
    c: Distance(g0,g2) = 31
    c: Symmetric(g0,g2,g-1)
    c: Symmetric(g0,g1,g-2)
    c: Symmetric(g2,g3,g-2)
    c: Radius(g0) = 2
    c: Equal(g0,g1)
    c: Equal(g0,g2)
    c: Equal(g0,g3)
FEATURE [Part::Extrusion] Extrude124
  Base = -> Sketch089
  Dir = (0,4.5,0)
  Solid = true
FEATURE [Part::Cut] Cut047
  Base = -> Extrude121
  Tool = -> Extrude124
FEATURE [Sketcher::SketchObject] Sketch090
  Placement = pos=(0,0,0) rot=(1,0,0;1.5708rad)
  sketch-geometry (1):
    g0: Circle CenterX=0 CenterY=0 CenterZ=0 NormalX=0 NormalY=0 NormalZ=1 Radius=9
  constraints (2):
    c: Coincident(g0,g-1)
    c: Radius(g0) = 9
FEATURE [Part::Extrusion] Extrude125
  Base = -> Sketch090
  Dir = (0,25,0)
  Solid = true
FEATURE [Sketcher::SketchObject] Sketch091
  Placement = pos=(0,0,0) rot=(1,0,0;1.5708rad)
  sketch-geometry (1):
    g0: Circle CenterX=0 CenterY=0 CenterZ=0 NormalX=0 NormalY=0 NormalZ=1 Radius=2.5
  constraints (2):
    c: Coincident(g0,g-1)
    c: Radius(g0) = 2.5
FEATURE [Part::Extrusion] Extrude126
  Base = -> Sketch091
  Dir = (0,10,0)
  Solid = true
FEATURE [Part::Cut] Cut048
  Base = -> Extrude125
  Tool = -> Extrude126
FEATURE [Sketcher::SketchObject] Sketch092
  Placement = pos=(0,25,0) rot=(0,0.707107,0.707107;3.14159rad)
  Support = -> Cut048 [Face3]
  sketch-geometry (1):
    g0: Circle CenterX=0 CenterY=0 CenterZ=0 NormalX=0 NormalY=0 NormalZ=1 Radius=4
  constraints (2):
    c: Coincident(g0,g-1)
    c: Radius(g0) = 4
FEATURE [Part::Extrusion] Extrude127
  Base = -> Sketch092
  Dir = (0,-10,0)
  Solid = true
FEATURE [Part::Cut] Cut049  label="Accouplement_004"
  Base = -> Cut048
  Placement = pos=(-429,-12,0) rot=(1,0,0;3.14159rad)
  Tool = -> Extrude127
FEATURE [Part::Fuse] Fusion027
  Base = -> Extrude122
  Tool = -> Cut047
FEATURE [Part::Fuse] Fusion028  label="Moteur_004"
  Base = -> Chamfer012
  Placement = pos=(-429,0,0) rot=(0,0,1;0rad)
  Tool = -> Fusion027
FEATURE [Sketcher::SketchObject] Sketch093
  Placement = pos=(0,0,0) rot=(1,0,0;1.5708rad)
  sketch-geometry (4):
    g0: LineSegment StartX=-50 StartY=0 StartZ=0 EndX=-47 EndY=0 EndZ=0
    g1: LineSegment StartX=47 StartY=0 StartZ=0 EndX=50 EndY=0 EndZ=0
    g2: ArcOfCircle CenterX=0 CenterY=0 CenterZ=0 NormalX=0 NormalY=0 NormalZ=1 Radius=47 StartAngle=3.14159 EndAngle=6.28319
    g3: ArcOfCircle CenterX=0 CenterY=0 CenterZ=0 NormalX=0 NormalY=0 NormalZ=1 Radius=50 StartAngle=3.14159 EndAngle=6.28319
  constraints (13):
    c: Horizontal(g0)
    c: PointOnObject(g1,g-1)
    c: Horizontal(g1)
    c: Coincident(g2,g-1)
    c: PointOnObject(g2,g-1)
    c: Coincident(g3,g-1)
    c: Coincident(g3,g1)
    c: PointOnObject(g3,g-1)
    c: Coincident(g0,g3)
    c: Coincident(g0,g2)
    c: Distance(g0,g1) = 100
    c: Distance(g0,g0) = 3
    c: Coincident(g1,g2)
FEATURE [Part::Extrusion] Extrude128  label="Demi_tube_sous_miroir_004"
  Base = -> Sketch093
  Dir = (0,2000,0)
  Placement = pos=(-429,-62,20) rot=(0,0,1;3.14159rad)
  Solid = true
FEATURE [Part::Feature] Part__Feature006  label="Coussinet_autolub_C2-151-8-128_004"
  Placement = pos=(-429,-46,0) rot=(0,0,1;1.5708rad)
  shape: bbox 16 x 8 x 16 mm, 12 faces (baked)
FEATURE [Sketcher::SketchObject] Sketch094
  Placement = pos=(0,0,0) rot=(1,0,0;1.5708rad)
  sketch-geometry (21):
    g0: Circle CenterX=0 CenterY=0 CenterZ=0 NormalX=0 NormalY=0 NormalZ=1 Radius=6
    g1: LineSegment StartX=-20.5 StartY=15 StartZ=0 EndX=20.5 EndY=15 EndZ=0
    g2: ArcOfCircle CenterX=20.5 CenterY=13 CenterZ=0 NormalX=0 NormalY=0 NormalZ=1 Radius=2 StartAngle=6.28319 EndAngle=7.85398
    g3: LineSegment StartX=22.5 StartY=13 StartZ=0 EndX=22.5 EndY=-73 EndZ=0
    g4: LineSegment StartX=-22.5 StartY=13 StartZ=0 EndX=-22.5 EndY=-73 EndZ=0
    g5: ArcOfCircle CenterX=-20.5 CenterY=13 CenterZ=0 NormalX=0 NormalY=0 NormalZ=1 Radius=2 StartAngle=1.5708 EndAngle=3.14159
    g6: ArcOfCircle CenterX=-20.5 CenterY=-73 CenterZ=0 NormalX=0 NormalY=0 NormalZ=1 Radius=2 StartAngle=3.14159 EndAngle=4.71239
    g7: ArcOfCircle CenterX=20.5 CenterY=-73 CenterZ=0 NormalX=0 NormalY=0 NormalZ=1 Radius=2 StartAngle=4.71239 EndAngle=6.28319
    g8: LineSegment StartX=-20.5 StartY=-75 StartZ=0 EndX=20.5 EndY=-75 EndZ=0
    g9: ArcOfCircle CenterX=0 CenterY=-16.7 CenterZ=0 NormalX=0 NormalY=0 NormalZ=1 Radius=1.5 StartAngle=0 EndAngle=3.14159
    g10: ArcOfCircle CenterX=0 CenterY=-24.3 CenterZ=0 NormalX=0 NormalY=0 NormalZ=1 Radius=1.5 StartAngle=3.14159 EndAngle=6.28319
    g11: LineSegment StartX=-1.5 StartY=-16.7 StartZ=0 EndX=-1.5 EndY=-24.3 EndZ=0
    g12: LineSegment StartX=1.5 StartY=-16.7 StartZ=0 EndX=1.5 EndY=-24.3 EndZ=0
    g13: Circle CenterX=-12.5 CenterY=-45 CenterZ=0 NormalX=0 NormalY=0 NormalZ=1 Radius=3.5
    g14: Circle CenterX=12.5 CenterY=-45 CenterZ=0 NormalX=0 NormalY=0 NormalZ=1 Radius=3.5
    g15: Circle CenterX=-12.5 CenterY=-65 CenterZ=0 NormalX=0 NormalY=0 NormalZ=1 Radius=3.5
    g16: Circle CenterX=12.5 CenterY=-65 CenterZ=0 NormalX=0 NormalY=0 NormalZ=1 Radius=3.5
    g17: LineSegment [constr] StartX=-12.5 StartY=-45 StartZ=0 EndX=12.5 EndY=-45 EndZ=0
    g18: LineSegment [constr] StartX=-12.5 StartY=-45 StartZ=0 EndX=-12.5 EndY=-65 EndZ=0
    g19: LineSegment [constr] StartX=-12.5 StartY=-65 StartZ=0 EndX=12.5 EndY=-65 EndZ=0
    g20: LineSegment [constr] StartX=12.5 StartY=-45 StartZ=0 EndX=12.5 EndY=-65 EndZ=0
  constraints (59):
    c: Coincident(g0,g-1)
    c: Radius(g0) = 6
    c: Horizontal(g1)
    c: Coincident(g2,g1)
    c: Coincident(g3,g2)
    c: Vertical(g3)
    c: Vertical(g4)
    c: Coincident(g5,g1)
    c: Coincident(g5,g4)
    c: Coincident(g7,g3)
    c: Coincident(g8,g6)
    c: Coincident(g8,g7)
    c: Tangent(g8,g7)
    c: Tangent(g5,g4)
    c: Tangent(g5,g1)
    c: Tangent(g1,g2)
    c: Tangent(g2,g3)
    c: Coincident(g4,g6)
    c: Tangent(g6,g4)
    c: Tangent(g6,g8)
    c: Horizontal(g8)
    c: Tangent(g7,g3)
    c: Distance(g4,g2) = 45
    c: Symmetric(g4,g2,g-2)
    c: Distance(g1,g6) = 90
    c: DistanceY(g-1,g1) = 15
    c: Tangent(g9,g12) = 1.5708
    c: Tangent(g9,g11) = -1.5708
    c: Tangent(g11,g10) = -1.5708
    c: Tangent(g12,g10) = 1.5708
    c: Vertical(g11)
    c: Equal(g9,g10)
    c: PointOnObject(g9,g-2)
    c: Distance(g-1,g9) = 16.7
    c: Distance(g9,g10) = 7.6
    c: Radius(g9) = 1.5
    c: Radius(g13) = 3.5
    c: Equal(g13,g14)
    c: Equal(g13,g16)
    c: Equal(g13,g15)
    c: Radius(g5) = 2
    c: Equal(g5,g7)
    c: Equal(g5,g6)
    c: DistanceY(g-1,g13) = -45
    c: Coincident(g17,g13)
    c: Coincident(g17,g14)
    c: Horizontal(g17)
    c: Coincident(g18,g13)
    c: Coincident(g18,g15)
    c: Coincident(g19,g15)
    c: Coincident(g19,g16)
    c: Horizontal(g19)
    c: Coincident(g20,g14)
    c: Coincident(g20,g16)
    c: Vertical(g18)
    c: Vertical(g20)
    c: Distance(g13,g15) = 20
    c: Distance(g13,g14) = 25
    c: Symmetric(g13,g14,g-2)
FEATURE [Part::Extrusion] Extrude129  label="Plaque_support_004"
  Base = -> Sketch094
  Dir = (0,6,0)
  Placement = pos=(-429,-46,0) rot=(0,0,1;0rad)
  Solid = true
FEATURE [Sketcher::SketchObject] Sketch095
  Placement = pos=(0,0,0) rot=(0.57735,0.57735,0.57735;2.0944rad)
  sketch-geometry (8):
    g0: LineSegment StartX=0 StartY=33 StartZ=0 EndX=-2 EndY=33 EndZ=0
    g1: LineSegment StartX=-2 StartY=33 StartZ=0 EndX=-2 EndY=-24 EndZ=0
    g2: ArcOfCircle CenterX=-4 CenterY=-24 CenterZ=0 NormalX=0 NormalY=0 NormalZ=1 Radius=2 StartAngle=4.71239 EndAngle=6.28319
    g3: LineSegment StartX=-4 StartY=-26 StartZ=0 EndX=-38 EndY=-26 EndZ=0
    g4: LineSegment StartX=-38 StartY=-26 StartZ=0 EndX=-38 EndY=-28 EndZ=0
    g5: LineSegment StartX=-38 StartY=-28 StartZ=0 EndX=-4 EndY=-28 EndZ=0
    g6: ArcOfCircle CenterX=-4 CenterY=-24 CenterZ=0 NormalX=0 NormalY=0 NormalZ=1 Radius=4 StartAngle=4.71239 EndAngle=6.28319
    g7: LineSegment StartX=0 StartY=-24 StartZ=0 EndX=0 EndY=33 EndZ=0
  constraints (22):
    c: PointOnObject(g0,g-2)
    c: Horizontal(g0)
    c: Coincident(g0,g1)
    c: Vertical(g1)
    c: Tangent(g1,g2) = 1.5708
    c: Tangent(g2,g3) = 1.5708
    c: Coincident(g3,g4)
    c: Vertical(g4)
    c: Coincident(g4,g5)
    c: Horizontal(g5)
    c: Tangent(g5,g6) = -1.5708
    c: PointOnObject(g6,g-2)
    c: Tangent(g6,g7) = -1.5708
    c: Coincident(g7,g0)
    c: Horizontal(g3)
    c: DistanceX(g0,g0) = 2
    c: Radius(g2) = 2
    c: Radius(g6) = 4
    c: DistanceY(g3,g4) = -2
    c: Distance(g-1,g0) = 33
    c: DistanceY(g-1,g5) = -28
    c: DistanceX(g6,g4) = -38
FEATURE [Part::Extrusion] Extrude130
  Base = -> Sketch095
  Dir = (-32.5,0,0)
  Solid = true
FEATURE [Part::Extrusion] Extrude131
  Base = -> Sketch095
  Dir = (32.5,0,0)
  Solid = true
FEATURE [Part::MultiFuse] Fusion029
  Shapes = -> [Extrude130,Extrude131]
FEATURE [Sketcher::SketchObject] Sketch096
  Placement = pos=(0,-2,0) rot=(1,0,0;1.5708rad)
  Support = -> Fusion029 [Face3]
  sketch-geometry (9):
    g0: ArcOfCircle CenterX=0 CenterY=0 CenterZ=0 NormalX=0 NormalY=0 NormalZ=1 Radius=32.5 StartAngle=0 EndAngle=3.14159
    g1: LineSegment StartX=-32.5 StartY=0 StartZ=0 EndX=-32.5 EndY=34 EndZ=0
    g2: LineSegment StartX=-32.5 StartY=34 StartZ=0 EndX=32.5 EndY=34 EndZ=0
    g3: LineSegment StartX=32.5 StartY=34 StartZ=0 EndX=32.5 EndY=0 EndZ=0
    g4: Circle CenterX=0 CenterY=0 CenterZ=0 NormalX=0 NormalY=0 NormalZ=1 Radius=11
    g5: Circle CenterX=-15.5 CenterY=15.5 CenterZ=0 NormalX=0 NormalY=0 NormalZ=1 Radius=2
    g6: Circle CenterX=15.5 CenterY=15.5 CenterZ=0 NormalX=0 NormalY=0 NormalZ=1 Radius=2
    g7: Circle CenterX=-15.5 CenterY=-15.5 CenterZ=0 NormalX=0 NormalY=0 NormalZ=1 Radius=2
    g8: Circle CenterX=15.5 CenterY=-15.5 CenterZ=0 NormalX=0 NormalY=0 NormalZ=1 Radius=2
  constraints (23):
    c: Coincident(g0,g-1)
    c: PointOnObject(g0,g-1)
    c: PointOnObject(g0,g-1)
    c: Coincident(g1,g0)
    c: Vertical(g1)
    c: Coincident(g1,g2)
    c: Horizontal(g2)
    c: Coincident(g2,g3)
    c: Coincident(g3,g0)
    c: Vertical(g3)
    c: DistanceY(g1,g0) = -34
    c: Coincident(g4,g-1)
    c: Radius(g4) = 11
    c: DistanceX(g1,g2) = 65
    c: Radius(g5) = 2
    c: Equal(g5,g6)
    c: Equal(g5,g8)
    c: Equal(g5,g7)
    c: Symmetric(g5,g6,g-2)
    c: Symmetric(g5,g7,g-1)
    c: Symmetric(g7,g8,g-2)
    c: DistanceX(g5,g6) = 31
    c: DistanceY(g5,g7) = -31
FEATURE [Part::Extrusion] Extrude132
  Base = -> Sketch096
  Dir = (0,2,0)
  Solid = true
FEATURE [Part::Cut] Cut050
  Base = -> Fusion029
  Tool = -> Extrude132
FEATURE [Sketcher::SketchObject] Sketch097
  ExternalGeometry = -> [Cut050]
  Placement = pos=(0,0,-26) rot=(0,0,1;0rad)
  Support = -> Cut050 [Face5]
  sketch-geometry (5):
    g0: Circle CenterX=-25 CenterY=-12 CenterZ=0 NormalX=0 NormalY=0 NormalZ=1 Radius=3.5
    g1: Circle CenterX=-25 CenterY=-30 CenterZ=0 NormalX=0 NormalY=0 NormalZ=1 Radius=3.5
    g2: Circle CenterX=25 CenterY=-12 CenterZ=0 NormalX=0 NormalY=0 NormalZ=1 Radius=3.5
    g3: Circle CenterX=25 CenterY=-30 CenterZ=0 NormalX=0 NormalY=0 NormalZ=1 Radius=3.5
    g4: LineSegment [constr] StartX=-25 StartY=-12 StartZ=0 EndX=-25 EndY=-30 EndZ=0
  constraints (12):
    c: Radius(g0) = 3.5
    c: Equal(g0,g2)
    c: Equal(g0,g3)
    c: Equal(g0,g1)
    c: Symmetric(g0,g2,g-2)
    c: Symmetric(g1,g3,g-2)
    c: Coincident(g4,g0)
    c: Coincident(g4,g1)
    c: Vertical(g4)
    c: DistanceY(g0,g1) = -18
    c: DistanceY(g-3,g1) = 8
    c: DistanceX(g0,g2) = 50
FEATURE [Part::Extrusion] Extrude133
  Base = -> Sketch097
  Dir = (0,0,-2)
  Solid = true
FEATURE [Part::Cut] Cut051
  Base = -> Cut050
  Tool = -> Extrude133
FEATURE [Part::Fillet] Fillet011  label="Plaque_moteur_004"
  Base = -> Cut051
  Edges = 2 edges r=4: [Edge5,Edge59]
  Placement = pos=(-429,0,0) rot=(0,0,1;0rad)
FEATURE [Sketcher::SketchObject] Sketch098
  Placement = pos=(0,0,0) rot=(1,0,0;1.5708rad)
  sketch-geometry (4):
    g0: LineSegment StartX=-3.15 StartY=5.95 StartZ=0 EndX=3.15 EndY=5.95 EndZ=0
    g1: LineSegment StartX=3.15 StartY=5.95 StartZ=0 EndX=3.15 EndY=-5.95 EndZ=0
    g2: LineSegment StartX=3.15 StartY=-5.95 StartZ=0 EndX=-3.15 EndY=-5.95 EndZ=0
    g3: LineSegment StartX=-3.15 StartY=-5.95 StartZ=0 EndX=-3.15 EndY=5.95 EndZ=0
  constraints (12):
    c: Coincident(g0,g1)
    c: Coincident(g1,g2)
    c: Coincident(g2,g3)
    c: Coincident(g3,g0)
    c: Horizontal(g0)
    c: Horizontal(g2)
    c: Vertical(g1)
    c: Vertical(g3)
    c: DistanceX(g0,g0) = 6.3
    c: DistanceY(g0,g2) = -11.9
    c: Symmetric(g0,g0,g-2)
    c: Symmetric(g0,g1,g-1)
FEATURE [Part::Extrusion] Extrude134
  Base = -> Sketch098
  Dir = (0,-10.8,0)
  Solid = true
FEATURE [Sketcher::SketchObject] Sketch099
  ExternalGeometry = -> [Extrude134]
  Placement = pos=(0,-10.8,0) rot=(1,0,0;1.5708rad)
  Support = -> Extrude134 [Face6]
  sketch-geometry (4):
    g0: LineSegment StartX=-3.15 StartY=1.55 StartZ=0 EndX=3.15 EndY=1.55 EndZ=0
    g1: LineSegment StartX=3.15 StartY=1.55 StartZ=0 EndX=3.15 EndY=-1.55 EndZ=0
    g2: LineSegment StartX=3.15 StartY=-1.55 StartZ=0 EndX=-3.15 EndY=-1.55 EndZ=0
    g3: LineSegment StartX=-3.15 StartY=-1.55 StartZ=0 EndX=-3.15 EndY=1.55 EndZ=0
  constraints (12):
    c: Coincident(g0,g1)
    c: Coincident(g1,g2)
    c: Coincident(g2,g3)
    c: Coincident(g3,g0)
    c: Horizontal(g0)
    c: Horizontal(g2)
    c: Vertical(g1)
    c: Vertical(g3)
    c: PointOnObject(g0,g-4)
    c: PointOnObject(g0,g-3)
    c: DistanceY(g0,g2) = -3.1
    c: Symmetric(g0,g1,g-1)
FEATURE [Part::Extrusion] Extrude135
  Base = -> Sketch099
  Dir = (0,7.7,0)
  Solid = true
FEATURE [Part::Cut] Cut052
  Base = -> Extrude134
  Tool = -> Extrude135
FEATURE [Part::Chamfer] Chamfer013
  Base = -> Cut052
  Edges = 4 edges r=0.5: [Edge7,Edge9,Edge15,Edge17]
FEATURE [Part::Chamfer] Chamfer014
  Base = -> Chamfer013
  Edges = 1 edges r=1.2: [Edge13]
FEATURE [Sketcher::SketchObject] Sketch100
  ExternalGeometry = -> [Chamfer014]
  Placement = pos=(0,0,5.95) rot=(0,0,1;0rad)
  Support = -> Chamfer014 [Face5]
  sketch-geometry (4):
    g0: LineSegment StartX=-3 StartY=0 StartZ=0 EndX=3 EndY=0 EndZ=0
    g1: LineSegment StartX=3 StartY=0 StartZ=0 EndX=3 EndY=-3.1 EndZ=0
    g2: LineSegment StartX=3 StartY=-3.1 StartZ=0 EndX=-3 EndY=-3.1 EndZ=0
    g3: LineSegment StartX=-3 StartY=-3.1 StartZ=0 EndX=-3 EndY=0 EndZ=0
  constraints (12):
    c: Coincident(g0,g1)
    c: Coincident(g1,g2)
    c: Coincident(g2,g3)
    c: Coincident(g3,g0)
    c: Horizontal(g0)
    c: Horizontal(g2)
    c: Vertical(g1)
    c: Vertical(g3)
    c: PointOnObject(g0,g-1)
    c: DistanceX(g-3,g0) = 0.15
    c: Symmetric(g0,g0,g-2)
    c: DistanceY(g0,g1) = -3.1
FEATURE [Part::Extrusion] Extrude136
  Base = -> Sketch100
  Dir = (0,0,6.3)
  Solid = true
FEATURE [Sketcher::SketchObject] Sketch101
  ExternalGeometry = -> [Extrude136]
  Placement = pos=(0,-3.1,0) rot=(1,0,0;1.5708rad)
  Support = -> Extrude136 [Face3]
  sketch-geometry (1):
    g0: Circle CenterX=0 CenterY=9.5 CenterZ=0 NormalX=0 NormalY=0 NormalZ=1 Radius=1.65
  constraints (3):
    c: PointOnObject(g0,g-2)
    c: Radius(g0) = 1.65
    c: DistanceY(g0,g-3) = -3.55
FEATURE [Part::Extrusion] Extrude137
  Base = -> Sketch101
  Dir = (0,6,0)
  Solid = true
FEATURE [Part::Cut] Cut053
  Base = -> Extrude136
  Tool = -> Extrude137
FEATURE [Part::Fillet] Fillet012
  Base = -> Cut053
  Edges = 2 edges r=1.35: [Edge8,Edge11]
FEATURE [Part::MultiFuse] Fusion030
  Shapes = -> [Chamfer014]
FEATURE [Sketcher::SketchObject] Sketch102
  Placement = pos=(0,0,0) rot=(0,0.707107,0.707107;3.14159rad)
  Support = -> Fusion030 [Face7]
  sketch-geometry (4):
    g0: Circle CenterX=-1.27 CenterY=3.8 CenterZ=0 NormalX=0 NormalY=0 NormalZ=1 Radius=0.2
    g1: Circle CenterX=1.27 CenterY=3.8 CenterZ=0 NormalX=0 NormalY=0 NormalZ=1 Radius=0.2
    g2: Circle CenterX=-1.27 CenterY=-3.8 CenterZ=0 NormalX=0 NormalY=0 NormalZ=1 Radius=0.2
    g3: Circle CenterX=1.27 CenterY=-3.8 CenterZ=0 NormalX=0 NormalY=0 NormalZ=1 Radius=0.2
  constraints (9):
    c: Radius(g0) = 0.2
    c: Equal(g0,g1)
    c: Equal(g0,g3)
    c: Equal(g0,g2)
    c: Symmetric(g0,g1,g-2)
    c: Symmetric(g2,g3,g-2)
    c: Symmetric(g0,g2,g-1)
    c: DistanceX(g0,g1) = 2.54
    c: DistanceY(g1,g3) = -7.6
FEATURE [Part::Extrusion] Extrude138
  Base = -> Sketch102
  Dir = (0,7.8,0)
  Solid = true
FEATURE [Part::MultiFuse] Fusion031  label="Capteur_optique_004"
  Placement = pos=(-429,-46,-20.7) rot=(0,0,1;0rad)
  Shapes = -> [Fusion030,Fillet012,Extrude138]
FEATURE [Sketcher::SketchObject] Sketch103
  Placement = pos=(0,0,0) rot=(1,0,0;1.5708rad)
  sketch-geometry (1):
    g0: Circle CenterX=0 CenterY=0 CenterZ=0 NormalX=0 NormalY=0 NormalZ=1 Radius=4
  constraints (2):
    c: Coincident(g0,g-1)
    c: Radius(g0) = 4
FEATURE [Part::Extrusion] Extrude139
  Base = -> Sketch103
  Dir = (0,50,0)
  Solid = true
FEATURE [Sketcher::SketchObject] Sketch104
  Placement = pos=(0,0,0) rot=(0.57735,0.57735,0.57735;2.0944rad)
  sketch-geometry (1):
    g0: Circle CenterX=6 CenterY=0 CenterZ=0 NormalX=0 NormalY=0 NormalZ=1 Radius=2
  constraints (3):
    c: DistanceX(g-1,g0) = 6
    c: Radius(g0) = 2
    c: PointOnObject(g0,g-1)
FEATURE [Part::Extrusion] Extrude140
  Base = -> Sketch104
  Dir = (4,0,0)
  Solid = true
FEATURE [Part::Extrusion] Extrude141
  Base = -> Sketch104
  Dir = (-4,0,0)
  Solid = true
FEATURE [Part::Cut] Cut054
  Base = -> Extrude139
  Tool = -> Extrude140
FEATURE [Part::Cut] Cut055  label="Axe_D8_004"
  Base = -> Cut054
  Placement = pos=(-429,-86,0) rot=(0,0,1;0rad)
  Tool = -> Extrude141
FEATURE [Sketcher::SketchObject] Sketch105
  Placement = pos=(0,0,0) rot=(1,0,0;1.5708rad)
  sketch-geometry (1):
    g0: Circle CenterX=0 CenterY=0 CenterZ=0 NormalX=0 NormalY=0 NormalZ=1 Radius=2
  constraints (2):
    c: Coincident(g0,g-1)
    c: Radius(g0) = 2
FEATURE [Part::Extrusion] Extrude142  label="Axe_D4_004"
  Base = -> Sketch105
  Dir = (0,103.6,0)
  Placement = pos=(-377.2,-80,0) rot=(0,0,1;1.5708rad)
  Solid = true
FEATURE [Sketcher::SketchObject] Sketch106
  Placement = pos=(0,0,0) rot=(1,0,0;1.5708rad)
  sketch-geometry (8):
    g0: LineSegment StartX=-50 StartY=0 StartZ=0 EndX=50 EndY=0 EndZ=0
    g1: LineSegment StartX=50 StartY=0 StartZ=0 EndX=50 EndY=-2 EndZ=0
    g2: LineSegment StartX=50 StartY=-2 StartZ=0 EndX=47 EndY=-2 EndZ=0
    g3: LineSegment StartX=47 StartY=-2 StartZ=0 EndX=44 EndY=-16 EndZ=0
    g4: LineSegment StartX=44 StartY=-16 StartZ=0 EndX=-44 EndY=-16 EndZ=0
    g5: LineSegment StartX=-44 StartY=-16 StartZ=0 EndX=-47 EndY=-2 EndZ=0
    g6: LineSegment StartX=-47 StartY=-2 StartZ=0 EndX=-50 EndY=-2 EndZ=0
    g7: LineSegment StartX=-50 StartY=-2 StartZ=0 EndX=-50 EndY=0 EndZ=0
  constraints (24):
    c: PointOnObject(g0,g-1)
    c: Horizontal(g0)
    c: Coincident(g0,g1)
    c: Vertical(g1)
    c: Coincident(g1,g2)
    c: Horizontal(g2)
    c: Coincident(g2,g3)
    c: Coincident(g3,g4)
    c: Horizontal(g4)
    c: Coincident(g4,g5)
    c: Coincident(g5,g6)
    c: Horizontal(g6)
    c: Coincident(g6,g7)
    c: Coincident(g7,g0)
    c: Vertical(g7)
    c: DistanceY(g0,g6) = -2
    c: DistanceX(g6,g5) = 3
    c: DistanceX(g0,g0) = 100
    c: Symmetric(g0,g0,g-2)
    c: Symmetric(g6,g1,g-2)
    c: Symmetric(g5,g2,g-2)
    c: Symmetric(g4,g3,g-2)
    c: DistanceX(g4,g3) = 88
    c: DistanceY(g0,g4) = -16
FEATURE [Part::Extrusion] Extrude143  label="Plaque_alveolaire_004"
  Base = -> Sketch106
  Dir = (0,2000,0)
  Placement = pos=(-429,-62,22) rot=(0,0,1;3.14159rad)
  Solid = true
FEATURE [App::DocumentObjectGroup] Groupe006  label="Assemblage_miroir X=-429_001"
  Group = -> [Cut049,Fusion028,Extrude128,Part__Feature006,Extrude129,Fillet011,Fusion031,Cut055,Extrude142,Extrude143]
FEATURE [Sketcher::SketchObject] Sketch107
  Placement = pos=(0,0,0) rot=(1,0,0;1.5708rad)
  sketch-geometry (8):
    g0: LineSegment StartX=-21.15 StartY=16.15 StartZ=0 EndX=-16.15 EndY=21.15 EndZ=0
    g1: LineSegment StartX=-16.15 StartY=21.15 StartZ=0 EndX=16.15 EndY=21.15 EndZ=0
    g2: LineSegment StartX=16.15 StartY=21.15 StartZ=0 EndX=21.15 EndY=16.15 EndZ=0
    g3: LineSegment StartX=21.15 StartY=16.15 StartZ=0 EndX=21.15 EndY=-16.15 EndZ=0
    g4: LineSegment StartX=21.15 StartY=-16.15 StartZ=0 EndX=16.15 EndY=-21.15 EndZ=0
    g5: LineSegment StartX=16.15 StartY=-21.15 StartZ=0 EndX=-16.15 EndY=-21.15 EndZ=0
    g6: LineSegment StartX=-16.15 StartY=-21.15 StartZ=0 EndX=-21.15 EndY=-16.15 EndZ=0
    g7: LineSegment StartX=-21.15 StartY=-16.15 StartZ=0 EndX=-21.15 EndY=16.15 EndZ=0
  constraints (21):
    c: Coincident(g0,g1)
    c: Horizontal(g1)
    c: Coincident(g1,g2)
    c: Coincident(g2,g3)
    c: Vertical(g3)
    c: Coincident(g3,g4)
    c: Coincident(g4,g5)
    c: Horizontal(g5)
    c: Coincident(g5,g6)
    c: Coincident(g6,g7)
    c: Coincident(g7,g0)
    c: Angle(g7,g0) = 2.35619
    c: Distance(g0,g7) = 5
    c: Distance(g2,g7) = 42.3
    c: Distance(g5,g1) = 42.3
    c: Symmetric(g6,g3,g-2)
    c: Symmetric(g5,g4,g-2)
    c: Symmetric(g0,g2,g-2)
    c: Symmetric(g0,g1,g-2)
    c: Symmetric(g0,g6,g-1)
    c: Symmetric(g0,g5,g-1)
FEATURE [Part::Extrusion] Extrude144
  Base = -> Sketch107
  Dir = (0,48,0)
  Solid = true
FEATURE [Sketcher::SketchObject] Sketch108
  Placement = pos=(0,0,0) rot=(1,0,0;1.5708rad)
  Support = -> Extrude144 [Face9]
  sketch-geometry (1):
    g0: Circle CenterX=0 CenterY=0 CenterZ=0 NormalX=0 NormalY=0 NormalZ=1 Radius=11
  constraints (2):
    c: Coincident(g0,g-1)
    c: Radius(g0) = 11
FEATURE [Part::Extrusion] Extrude145
  Base = -> Sketch108
  Dir = (0,-2,0)
  Solid = true
FEATURE [Sketcher::SketchObject] Sketch109
  Placement = pos=(0,-2,0) rot=(1,0,0;1.5708rad)
  Support = -> Extrude145 [Face3]
  sketch-geometry (1):
    g0: Circle CenterX=0 CenterY=0 CenterZ=0 NormalX=0 NormalY=0 NormalZ=1 Radius=2.5
  constraints (2):
    c: Coincident(g0,g-1)
    c: Radius(g0) = 2.5
FEATURE [Part::Extrusion] Extrude146
  Base = -> Sketch109
  Dir = (0,-22,0)
  Solid = true
FEATURE [Part::Chamfer] Chamfer015
  Base = -> Extrude146
  Edges = 1 edges r=0.8: [Edge3]
FEATURE [Sketcher::SketchObject] Sketch110
  Placement = pos=(0,0,0) rot=(1,0,0;1.5708rad)
  Support = -> Extrude144 [Face9]
  sketch-geometry (4):
    g0: Circle CenterX=-15.5 CenterY=15.5 CenterZ=0 NormalX=0 NormalY=0 NormalZ=1 Radius=2
    g1: Circle CenterX=15.5 CenterY=15.5 CenterZ=0 NormalX=0 NormalY=0 NormalZ=1 Radius=2
    g2: Circle CenterX=-15.5 CenterY=-15.5 CenterZ=0 NormalX=0 NormalY=0 NormalZ=1 Radius=2
    g3: Circle CenterX=15.5 CenterY=-15.5 CenterZ=0 NormalX=0 NormalY=0 NormalZ=1 Radius=2
  constraints (9):
    c: Distance(g0,g1) = 31
    c: Distance(g0,g2) = 31
    c: Symmetric(g0,g2,g-1)
    c: Symmetric(g0,g1,g-2)
    c: Symmetric(g2,g3,g-2)
    c: Radius(g0) = 2
    c: Equal(g0,g1)
    c: Equal(g0,g2)
    c: Equal(g0,g3)
FEATURE [Part::Extrusion] Extrude147
  Base = -> Sketch110
  Dir = (0,4.5,0)
  Solid = true
FEATURE [Part::Cut] Cut056
  Base = -> Extrude144
  Tool = -> Extrude147
FEATURE [Sketcher::SketchObject] Sketch111
  Placement = pos=(0,0,0) rot=(1,0,0;1.5708rad)
  sketch-geometry (1):
    g0: Circle CenterX=0 CenterY=0 CenterZ=0 NormalX=0 NormalY=0 NormalZ=1 Radius=9
  constraints (2):
    c: Coincident(g0,g-1)
    c: Radius(g0) = 9
FEATURE [Part::Extrusion] Extrude148
  Base = -> Sketch111
  Dir = (0,25,0)
  Solid = true
FEATURE [Sketcher::SketchObject] Sketch112
  Placement = pos=(0,0,0) rot=(1,0,0;1.5708rad)
  sketch-geometry (1):
    g0: Circle CenterX=0 CenterY=0 CenterZ=0 NormalX=0 NormalY=0 NormalZ=1 Radius=2.5
  constraints (2):
    c: Coincident(g0,g-1)
    c: Radius(g0) = 2.5
FEATURE [Part::Extrusion] Extrude149
  Base = -> Sketch112
  Dir = (0,10,0)
  Solid = true
FEATURE [Part::Cut] Cut057
  Base = -> Extrude148
  Tool = -> Extrude149
FEATURE [Sketcher::SketchObject] Sketch113
  Placement = pos=(0,25,0) rot=(0,0.707107,0.707107;3.14159rad)
  Support = -> Cut057 [Face3]
  sketch-geometry (1):
    g0: Circle CenterX=0 CenterY=0 CenterZ=0 NormalX=0 NormalY=0 NormalZ=1 Radius=4
  constraints (2):
    c: Coincident(g0,g-1)
    c: Radius(g0) = 4
FEATURE [Part::Extrusion] Extrude150
  Base = -> Sketch113
  Dir = (0,-10,0)
  Solid = true
FEATURE [Part::Cut] Cut058  label="Accouplement_005"
  Base = -> Cut057
  Placement = pos=(-572,-12,0) rot=(1,0,0;3.14159rad)
  Tool = -> Extrude150
FEATURE [Part::Fuse] Fusion032
  Base = -> Extrude145
  Tool = -> Cut056
FEATURE [Part::Fuse] Fusion033  label="Moteur_005"
  Base = -> Chamfer015
  Placement = pos=(-572,0,0) rot=(0,0,1;0rad)
  Tool = -> Fusion032
FEATURE [Sketcher::SketchObject] Sketch114
  Placement = pos=(0,0,0) rot=(1,0,0;1.5708rad)
  sketch-geometry (4):
    g0: LineSegment StartX=-50 StartY=0 StartZ=0 EndX=-47 EndY=0 EndZ=0
    g1: LineSegment StartX=47 StartY=0 StartZ=0 EndX=50 EndY=0 EndZ=0
    g2: ArcOfCircle CenterX=0 CenterY=0 CenterZ=0 NormalX=0 NormalY=0 NormalZ=1 Radius=47 StartAngle=3.14159 EndAngle=6.28319
    g3: ArcOfCircle CenterX=0 CenterY=0 CenterZ=0 NormalX=0 NormalY=0 NormalZ=1 Radius=50 StartAngle=3.14159 EndAngle=6.28319
  constraints (13):
    c: Horizontal(g0)
    c: PointOnObject(g1,g-1)
    c: Horizontal(g1)
    c: Coincident(g2,g-1)
    c: PointOnObject(g2,g-1)
    c: Coincident(g3,g-1)
    c: Coincident(g3,g1)
    c: PointOnObject(g3,g-1)
    c: Coincident(g0,g3)
    c: Coincident(g0,g2)
    c: Distance(g0,g1) = 100
    c: Distance(g0,g0) = 3
    c: Coincident(g1,g2)
FEATURE [Part::Extrusion] Extrude151  label="Demi_tube_sous_miroir_005"
  Base = -> Sketch114
  Dir = (0,2000,0)
  Placement = pos=(-572,-62,20) rot=(0,0,1;3.14159rad)
  Solid = true
FEATURE [Part::Feature] Part__Feature007  label="Coussinet_autolub_C2-151-8-128_005"
  Placement = pos=(-572,-46,0) rot=(0,0,1;1.5708rad)
  shape: bbox 16 x 8 x 16 mm, 12 faces (baked)
FEATURE [Sketcher::SketchObject] Sketch115
  Placement = pos=(0,0,0) rot=(1,0,0;1.5708rad)
  sketch-geometry (21):
    g0: Circle CenterX=0 CenterY=0 CenterZ=0 NormalX=0 NormalY=0 NormalZ=1 Radius=6
    g1: LineSegment StartX=-20.5 StartY=15 StartZ=0 EndX=20.5 EndY=15 EndZ=0
    g2: ArcOfCircle CenterX=20.5 CenterY=13 CenterZ=0 NormalX=0 NormalY=0 NormalZ=1 Radius=2 StartAngle=6.28319 EndAngle=7.85398
    g3: LineSegment StartX=22.5 StartY=13 StartZ=0 EndX=22.5 EndY=-73 EndZ=0
    g4: LineSegment StartX=-22.5 StartY=13 StartZ=0 EndX=-22.5 EndY=-73 EndZ=0
    g5: ArcOfCircle CenterX=-20.5 CenterY=13 CenterZ=0 NormalX=0 NormalY=0 NormalZ=1 Radius=2 StartAngle=1.5708 EndAngle=3.14159
    g6: ArcOfCircle CenterX=-20.5 CenterY=-73 CenterZ=0 NormalX=0 NormalY=0 NormalZ=1 Radius=2 StartAngle=3.14159 EndAngle=4.71239
    g7: ArcOfCircle CenterX=20.5 CenterY=-73 CenterZ=0 NormalX=0 NormalY=0 NormalZ=1 Radius=2 StartAngle=4.71239 EndAngle=6.28319
    g8: LineSegment StartX=-20.5 StartY=-75 StartZ=0 EndX=20.5 EndY=-75 EndZ=0
    g9: ArcOfCircle CenterX=0 CenterY=-16.7 CenterZ=0 NormalX=0 NormalY=0 NormalZ=1 Radius=1.5 StartAngle=0 EndAngle=3.14159
    g10: ArcOfCircle CenterX=0 CenterY=-24.3 CenterZ=0 NormalX=0 NormalY=0 NormalZ=1 Radius=1.5 StartAngle=3.14159 EndAngle=6.28319
    g11: LineSegment StartX=-1.5 StartY=-16.7 StartZ=0 EndX=-1.5 EndY=-24.3 EndZ=0
    g12: LineSegment StartX=1.5 StartY=-16.7 StartZ=0 EndX=1.5 EndY=-24.3 EndZ=0
    g13: Circle CenterX=-12.5 CenterY=-45 CenterZ=0 NormalX=0 NormalY=0 NormalZ=1 Radius=3.5
    g14: Circle CenterX=12.5 CenterY=-45 CenterZ=0 NormalX=0 NormalY=0 NormalZ=1 Radius=3.5
    g15: Circle CenterX=-12.5 CenterY=-65 CenterZ=0 NormalX=0 NormalY=0 NormalZ=1 Radius=3.5
    g16: Circle CenterX=12.5 CenterY=-65 CenterZ=0 NormalX=0 NormalY=0 NormalZ=1 Radius=3.5
    g17: LineSegment [constr] StartX=-12.5 StartY=-45 StartZ=0 EndX=12.5 EndY=-45 EndZ=0
    g18: LineSegment [constr] StartX=-12.5 StartY=-45 StartZ=0 EndX=-12.5 EndY=-65 EndZ=0
    g19: LineSegment [constr] StartX=-12.5 StartY=-65 StartZ=0 EndX=12.5 EndY=-65 EndZ=0
    g20: LineSegment [constr] StartX=12.5 StartY=-45 StartZ=0 EndX=12.5 EndY=-65 EndZ=0
  constraints (59):
    c: Coincident(g0,g-1)
    c: Radius(g0) = 6
    c: Horizontal(g1)
    c: Coincident(g2,g1)
    c: Coincident(g3,g2)
    c: Vertical(g3)
    c: Vertical(g4)
    c: Coincident(g5,g1)
    c: Coincident(g5,g4)
    c: Coincident(g7,g3)
    c: Coincident(g8,g6)
    c: Coincident(g8,g7)
    c: Tangent(g8,g7)
    c: Tangent(g5,g4)
    c: Tangent(g5,g1)
    c: Tangent(g1,g2)
    c: Tangent(g2,g3)
    c: Coincident(g4,g6)
    c: Tangent(g6,g4)
    c: Tangent(g6,g8)
    c: Horizontal(g8)
    c: Tangent(g7,g3)
    c: Distance(g4,g2) = 45
    c: Symmetric(g4,g2,g-2)
    c: Distance(g1,g6) = 90
    c: DistanceY(g-1,g1) = 15
    c: Tangent(g9,g12) = 1.5708
    c: Tangent(g9,g11) = -1.5708
    c: Tangent(g11,g10) = -1.5708
    c: Tangent(g12,g10) = 1.5708
    c: Vertical(g11)
    c: Equal(g9,g10)
    c: PointOnObject(g9,g-2)
    c: Distance(g-1,g9) = 16.7
    c: Distance(g9,g10) = 7.6
    c: Radius(g9) = 1.5
    c: Radius(g13) = 3.5
    c: Equal(g13,g14)
    c: Equal(g13,g16)
    c: Equal(g13,g15)
    c: Radius(g5) = 2
    c: Equal(g5,g7)
    c: Equal(g5,g6)
    c: DistanceY(g-1,g13) = -45
    c: Coincident(g17,g13)
    c: Coincident(g17,g14)
    c: Horizontal(g17)
    c: Coincident(g18,g13)
    c: Coincident(g18,g15)
    c: Coincident(g19,g15)
    c: Coincident(g19,g16)
    c: Horizontal(g19)
    c: Coincident(g20,g14)
    c: Coincident(g20,g16)
    c: Vertical(g18)
    c: Vertical(g20)
    c: Distance(g13,g15) = 20
    c: Distance(g13,g14) = 25
    c: Symmetric(g13,g14,g-2)
FEATURE [Part::Extrusion] Extrude152  label="Plaque_support_005"
  Base = -> Sketch115
  Dir = (0,6,0)
  Placement = pos=(-572,-46,0) rot=(0,0,1;0rad)
  Solid = true
FEATURE [Sketcher::SketchObject] Sketch116
  Placement = pos=(0,0,0) rot=(0.57735,0.57735,0.57735;2.0944rad)
  sketch-geometry (8):
    g0: LineSegment StartX=0 StartY=33 StartZ=0 EndX=-2 EndY=33 EndZ=0
    g1: LineSegment StartX=-2 StartY=33 StartZ=0 EndX=-2 EndY=-24 EndZ=0
    g2: ArcOfCircle CenterX=-4 CenterY=-24 CenterZ=0 NormalX=0 NormalY=0 NormalZ=1 Radius=2 StartAngle=4.71239 EndAngle=6.28319
    g3: LineSegment StartX=-4 StartY=-26 StartZ=0 EndX=-38 EndY=-26 EndZ=0
    g4: LineSegment StartX=-38 StartY=-26 StartZ=0 EndX=-38 EndY=-28 EndZ=0
    g5: LineSegment StartX=-38 StartY=-28 StartZ=0 EndX=-4 EndY=-28 EndZ=0
    g6: ArcOfCircle CenterX=-4 CenterY=-24 CenterZ=0 NormalX=0 NormalY=0 NormalZ=1 Radius=4 StartAngle=4.71239 EndAngle=6.28319
    g7: LineSegment StartX=0 StartY=-24 StartZ=0 EndX=0 EndY=33 EndZ=0
  constraints (22):
    c: PointOnObject(g0,g-2)
    c: Horizontal(g0)
    c: Coincident(g0,g1)
    c: Vertical(g1)
    c: Tangent(g1,g2) = 1.5708
    c: Tangent(g2,g3) = 1.5708
    c: Coincident(g3,g4)
    c: Vertical(g4)
    c: Coincident(g4,g5)
    c: Horizontal(g5)
    c: Tangent(g5,g6) = -1.5708
    c: PointOnObject(g6,g-2)
    c: Tangent(g6,g7) = -1.5708
    c: Coincident(g7,g0)
    c: Horizontal(g3)
    c: DistanceX(g0,g0) = 2
    c: Radius(g2) = 2
    c: Radius(g6) = 4
    c: DistanceY(g3,g4) = -2
    c: Distance(g-1,g0) = 33
    c: DistanceY(g-1,g5) = -28
    c: DistanceX(g6,g4) = -38
FEATURE [Part::Extrusion] Extrude153
  Base = -> Sketch116
  Dir = (-32.5,0,0)
  Solid = true
FEATURE [Part::Extrusion] Extrude154
  Base = -> Sketch116
  Dir = (32.5,0,0)
  Solid = true
FEATURE [Part::MultiFuse] Fusion034
  Shapes = -> [Extrude153,Extrude154]
FEATURE [Sketcher::SketchObject] Sketch117
  Placement = pos=(0,-2,0) rot=(1,0,0;1.5708rad)
  Support = -> Fusion034 [Face3]
  sketch-geometry (9):
    g0: ArcOfCircle CenterX=0 CenterY=0 CenterZ=0 NormalX=0 NormalY=0 NormalZ=1 Radius=32.5 StartAngle=0 EndAngle=3.14159
    g1: LineSegment StartX=-32.5 StartY=0 StartZ=0 EndX=-32.5 EndY=34 EndZ=0
    g2: LineSegment StartX=-32.5 StartY=34 StartZ=0 EndX=32.5 EndY=34 EndZ=0
    g3: LineSegment StartX=32.5 StartY=34 StartZ=0 EndX=32.5 EndY=0 EndZ=0
    g4: Circle CenterX=0 CenterY=0 CenterZ=0 NormalX=0 NormalY=0 NormalZ=1 Radius=11
    g5: Circle CenterX=-15.5 CenterY=15.5 CenterZ=0 NormalX=0 NormalY=0 NormalZ=1 Radius=2
    g6: Circle CenterX=15.5 CenterY=15.5 CenterZ=0 NormalX=0 NormalY=0 NormalZ=1 Radius=2
    g7: Circle CenterX=-15.5 CenterY=-15.5 CenterZ=0 NormalX=0 NormalY=0 NormalZ=1 Radius=2
    g8: Circle CenterX=15.5 CenterY=-15.5 CenterZ=0 NormalX=0 NormalY=0 NormalZ=1 Radius=2
  constraints (23):
    c: Coincident(g0,g-1)
    c: PointOnObject(g0,g-1)
    c: PointOnObject(g0,g-1)
    c: Coincident(g1,g0)
    c: Vertical(g1)
    c: Coincident(g1,g2)
    c: Horizontal(g2)
    c: Coincident(g2,g3)
    c: Coincident(g3,g0)
    c: Vertical(g3)
    c: DistanceY(g1,g0) = -34
    c: Coincident(g4,g-1)
    c: Radius(g4) = 11
    c: DistanceX(g1,g2) = 65
    c: Radius(g5) = 2
    c: Equal(g5,g6)
    c: Equal(g5,g8)
    c: Equal(g5,g7)
    c: Symmetric(g5,g6,g-2)
    c: Symmetric(g5,g7,g-1)
    c: Symmetric(g7,g8,g-2)
    c: DistanceX(g5,g6) = 31
    c: DistanceY(g5,g7) = -31
FEATURE [Part::Extrusion] Extrude155
  Base = -> Sketch117
  Dir = (0,2,0)
  Solid = true
FEATURE [Part::Cut] Cut059
  Base = -> Fusion034
  Tool = -> Extrude155
FEATURE [Sketcher::SketchObject] Sketch118
  ExternalGeometry = -> [Cut059]
  Placement = pos=(0,0,-26) rot=(0,0,1;0rad)
  Support = -> Cut059 [Face5]
  sketch-geometry (5):
    g0: Circle CenterX=-25 CenterY=-12 CenterZ=0 NormalX=0 NormalY=0 NormalZ=1 Radius=3.5
    g1: Circle CenterX=-25 CenterY=-30 CenterZ=0 NormalX=0 NormalY=0 NormalZ=1 Radius=3.5
    g2: Circle CenterX=25 CenterY=-12 CenterZ=0 NormalX=0 NormalY=0 NormalZ=1 Radius=3.5
    g3: Circle CenterX=25 CenterY=-30 CenterZ=0 NormalX=0 NormalY=0 NormalZ=1 Radius=3.5
    g4: LineSegment [constr] StartX=-25 StartY=-12 StartZ=0 EndX=-25 EndY=-30 EndZ=0
  constraints (12):
    c: Radius(g0) = 3.5
    c: Equal(g0,g2)
    c: Equal(g0,g3)
    c: Equal(g0,g1)
    c: Symmetric(g0,g2,g-2)
    c: Symmetric(g1,g3,g-2)
    c: Coincident(g4,g0)
    c: Coincident(g4,g1)
    c: Vertical(g4)
    c: DistanceY(g0,g1) = -18
    c: DistanceY(g-3,g1) = 8
    c: DistanceX(g0,g2) = 50
FEATURE [Part::Extrusion] Extrude156
  Base = -> Sketch118
  Dir = (0,0,-2)
  Solid = true
FEATURE [Part::Cut] Cut060
  Base = -> Cut059
  Tool = -> Extrude156
FEATURE [Part::Fillet] Fillet013  label="Plaque_moteur_005"
  Base = -> Cut060
  Edges = 2 edges r=4: [Edge5,Edge59]
  Placement = pos=(-572,0,0) rot=(0,0,1;0rad)
FEATURE [Sketcher::SketchObject] Sketch119
  Placement = pos=(0,0,0) rot=(1,0,0;1.5708rad)
  sketch-geometry (4):
    g0: LineSegment StartX=-3.15 StartY=5.95 StartZ=0 EndX=3.15 EndY=5.95 EndZ=0
    g1: LineSegment StartX=3.15 StartY=5.95 StartZ=0 EndX=3.15 EndY=-5.95 EndZ=0
    g2: LineSegment StartX=3.15 StartY=-5.95 StartZ=0 EndX=-3.15 EndY=-5.95 EndZ=0
    g3: LineSegment StartX=-3.15 StartY=-5.95 StartZ=0 EndX=-3.15 EndY=5.95 EndZ=0
  constraints (12):
    c: Coincident(g0,g1)
    c: Coincident(g1,g2)
    c: Coincident(g2,g3)
    c: Coincident(g3,g0)
    c: Horizontal(g0)
    c: Horizontal(g2)
    c: Vertical(g1)
    c: Vertical(g3)
    c: DistanceX(g0,g0) = 6.3
    c: DistanceY(g0,g2) = -11.9
    c: Symmetric(g0,g0,g-2)
    c: Symmetric(g0,g1,g-1)
FEATURE [Part::Extrusion] Extrude157
  Base = -> Sketch119
  Dir = (0,-10.8,0)
  Solid = true
FEATURE [Sketcher::SketchObject] Sketch120
  ExternalGeometry = -> [Extrude157]
  Placement = pos=(0,-10.8,0) rot=(1,0,0;1.5708rad)
  Support = -> Extrude157 [Face6]
  sketch-geometry (4):
    g0: LineSegment StartX=-3.15 StartY=1.55 StartZ=0 EndX=3.15 EndY=1.55 EndZ=0
    g1: LineSegment StartX=3.15 StartY=1.55 StartZ=0 EndX=3.15 EndY=-1.55 EndZ=0
    g2: LineSegment StartX=3.15 StartY=-1.55 StartZ=0 EndX=-3.15 EndY=-1.55 EndZ=0
    g3: LineSegment StartX=-3.15 StartY=-1.55 StartZ=0 EndX=-3.15 EndY=1.55 EndZ=0
  constraints (12):
    c: Coincident(g0,g1)
    c: Coincident(g1,g2)
    c: Coincident(g2,g3)
    c: Coincident(g3,g0)
    c: Horizontal(g0)
    c: Horizontal(g2)
    c: Vertical(g1)
    c: Vertical(g3)
    c: PointOnObject(g0,g-4)
    c: PointOnObject(g0,g-3)
    c: DistanceY(g0,g2) = -3.1
    c: Symmetric(g0,g1,g-1)
FEATURE [Part::Extrusion] Extrude158
  Base = -> Sketch120
  Dir = (0,7.7,0)
  Solid = true
FEATURE [Part::Cut] Cut061
  Base = -> Extrude157
  Tool = -> Extrude158
FEATURE [Part::Chamfer] Chamfer016
  Base = -> Cut061
  Edges = 4 edges r=0.5: [Edge7,Edge9,Edge15,Edge17]
FEATURE [Part::Chamfer] Chamfer017
  Base = -> Chamfer016
  Edges = 1 edges r=1.2: [Edge13]
FEATURE [Sketcher::SketchObject] Sketch121
  ExternalGeometry = -> [Chamfer017]
  Placement = pos=(0,0,5.95) rot=(0,0,1;0rad)
  Support = -> Chamfer017 [Face5]
  sketch-geometry (4):
    g0: LineSegment StartX=-3 StartY=0 StartZ=0 EndX=3 EndY=0 EndZ=0
    g1: LineSegment StartX=3 StartY=0 StartZ=0 EndX=3 EndY=-3.1 EndZ=0
    g2: LineSegment StartX=3 StartY=-3.1 StartZ=0 EndX=-3 EndY=-3.1 EndZ=0
    g3: LineSegment StartX=-3 StartY=-3.1 StartZ=0 EndX=-3 EndY=0 EndZ=0
  constraints (12):
    c: Coincident(g0,g1)
    c: Coincident(g1,g2)
    c: Coincident(g2,g3)
    c: Coincident(g3,g0)
    c: Horizontal(g0)
    c: Horizontal(g2)
    c: Vertical(g1)
    c: Vertical(g3)
    c: PointOnObject(g0,g-1)
    c: DistanceX(g-3,g0) = 0.15
    c: Symmetric(g0,g0,g-2)
    c: DistanceY(g0,g1) = -3.1
FEATURE [Part::Extrusion] Extrude159
  Base = -> Sketch121
  Dir = (0,0,6.3)
  Solid = true
FEATURE [Sketcher::SketchObject] Sketch122
  ExternalGeometry = -> [Extrude159]
  Placement = pos=(0,-3.1,0) rot=(1,0,0;1.5708rad)
  Support = -> Extrude159 [Face3]
  sketch-geometry (1):
    g0: Circle CenterX=0 CenterY=9.5 CenterZ=0 NormalX=0 NormalY=0 NormalZ=1 Radius=1.65
  constraints (3):
    c: PointOnObject(g0,g-2)
    c: Radius(g0) = 1.65
    c: DistanceY(g0,g-3) = -3.55
FEATURE [Part::Extrusion] Extrude160
  Base = -> Sketch122
  Dir = (0,6,0)
  Solid = true
FEATURE [Part::Cut] Cut062
  Base = -> Extrude159
  Tool = -> Extrude160
FEATURE [Part::Fillet] Fillet014
  Base = -> Cut062
  Edges = 2 edges r=1.35: [Edge8,Edge11]
FEATURE [Part::MultiFuse] Fusion035
  Shapes = -> [Chamfer017]
FEATURE [Sketcher::SketchObject] Sketch123
  Placement = pos=(0,0,0) rot=(0,0.707107,0.707107;3.14159rad)
  Support = -> Fusion035 [Face7]
  sketch-geometry (4):
    g0: Circle CenterX=-1.27 CenterY=3.8 CenterZ=0 NormalX=0 NormalY=0 NormalZ=1 Radius=0.2
    g1: Circle CenterX=1.27 CenterY=3.8 CenterZ=0 NormalX=0 NormalY=0 NormalZ=1 Radius=0.2
    g2: Circle CenterX=-1.27 CenterY=-3.8 CenterZ=0 NormalX=0 NormalY=0 NormalZ=1 Radius=0.2
    g3: Circle CenterX=1.27 CenterY=-3.8 CenterZ=0 NormalX=0 NormalY=0 NormalZ=1 Radius=0.2
  constraints (9):
    c: Radius(g0) = 0.2
    c: Equal(g0,g1)
    c: Equal(g0,g3)
    c: Equal(g0,g2)
    c: Symmetric(g0,g1,g-2)
    c: Symmetric(g2,g3,g-2)
    c: Symmetric(g0,g2,g-1)
    c: DistanceX(g0,g1) = 2.54
    c: DistanceY(g1,g3) = -7.6
FEATURE [Part::Extrusion] Extrude161
  Base = -> Sketch123
  Dir = (0,7.8,0)
  Solid = true
FEATURE [Part::MultiFuse] Fusion036  label="Capteur_optique_005"
  Placement = pos=(-572,-46,-20.7) rot=(0,0,1;0rad)
  Shapes = -> [Fusion035,Fillet014,Extrude161]
FEATURE [Sketcher::SketchObject] Sketch124
  Placement = pos=(0,0,0) rot=(1,0,0;1.5708rad)
  sketch-geometry (1):
    g0: Circle CenterX=0 CenterY=0 CenterZ=0 NormalX=0 NormalY=0 NormalZ=1 Radius=4
  constraints (2):
    c: Coincident(g0,g-1)
    c: Radius(g0) = 4
FEATURE [Part::Extrusion] Extrude162
  Base = -> Sketch124
  Dir = (0,50,0)
  Solid = true
FEATURE [Sketcher::SketchObject] Sketch125
  Placement = pos=(0,0,0) rot=(0.57735,0.57735,0.57735;2.0944rad)
  sketch-geometry (1):
    g0: Circle CenterX=6 CenterY=0 CenterZ=0 NormalX=0 NormalY=0 NormalZ=1 Radius=2
  constraints (3):
    c: DistanceX(g-1,g0) = 6
    c: Radius(g0) = 2
    c: PointOnObject(g0,g-1)
FEATURE [Part::Extrusion] Extrude163
  Base = -> Sketch125
  Dir = (4,0,0)
  Solid = true
FEATURE [Part::Extrusion] Extrude164
  Base = -> Sketch125
  Dir = (-4,0,0)
  Solid = true
FEATURE [Part::Cut] Cut063
  Base = -> Extrude162
  Tool = -> Extrude163
FEATURE [Part::Cut] Cut064  label="Axe_D8_005"
  Base = -> Cut063
  Placement = pos=(-572,-86,0) rot=(0,0,1;0rad)
  Tool = -> Extrude164
FEATURE [Sketcher::SketchObject] Sketch126
  Placement = pos=(0,0,0) rot=(1,0,0;1.5708rad)
  sketch-geometry (1):
    g0: Circle CenterX=0 CenterY=0 CenterZ=0 NormalX=0 NormalY=0 NormalZ=1 Radius=2
  constraints (2):
    c: Coincident(g0,g-1)
    c: Radius(g0) = 2
FEATURE [Part::Extrusion] Extrude165  label="Axe_D4_005"
  Base = -> Sketch126
  Dir = (0,103.6,0)
  Placement = pos=(-520.2,-80,0) rot=(0,0,1;1.5708rad)
  Solid = true
FEATURE [Sketcher::SketchObject] Sketch127
  Placement = pos=(0,0,0) rot=(1,0,0;1.5708rad)
  sketch-geometry (8):
    g0: LineSegment StartX=-50 StartY=0 StartZ=0 EndX=50 EndY=0 EndZ=0
    g1: LineSegment StartX=50 StartY=0 StartZ=0 EndX=50 EndY=-2 EndZ=0
    g2: LineSegment StartX=50 StartY=-2 StartZ=0 EndX=47 EndY=-2 EndZ=0
    g3: LineSegment StartX=47 StartY=-2 StartZ=0 EndX=44 EndY=-16 EndZ=0
    g4: LineSegment StartX=44 StartY=-16 StartZ=0 EndX=-44 EndY=-16 EndZ=0
    g5: LineSegment StartX=-44 StartY=-16 StartZ=0 EndX=-47 EndY=-2 EndZ=0
    g6: LineSegment StartX=-47 StartY=-2 StartZ=0 EndX=-50 EndY=-2 EndZ=0
    g7: LineSegment StartX=-50 StartY=-2 StartZ=0 EndX=-50 EndY=0 EndZ=0
  constraints (24):
    c: PointOnObject(g0,g-1)
    c: Horizontal(g0)
    c: Coincident(g0,g1)
    c: Vertical(g1)
    c: Coincident(g1,g2)
    c: Horizontal(g2)
    c: Coincident(g2,g3)
    c: Coincident(g3,g4)
    c: Horizontal(g4)
    c: Coincident(g4,g5)
    c: Coincident(g5,g6)
    c: Horizontal(g6)
    c: Coincident(g6,g7)
    c: Coincident(g7,g0)
    c: Vertical(g7)
    c: DistanceY(g0,g6) = -2
    c: DistanceX(g6,g5) = 3
    c: DistanceX(g0,g0) = 100
    c: Symmetric(g0,g0,g-2)
    c: Symmetric(g6,g1,g-2)
    c: Symmetric(g5,g2,g-2)
    c: Symmetric(g4,g3,g-2)
    c: DistanceX(g4,g3) = 88
    c: DistanceY(g0,g4) = -16
FEATURE [Part::Extrusion] Extrude166  label="Plaque_alveolaire_005"
  Base = -> Sketch127
  Dir = (0,2000,0)
  Placement = pos=(-572,-62,22) rot=(0,0,1;3.14159rad)
  Solid = true
FEATURE [App::DocumentObjectGroup] Groupe007  label="Assemblage_miroir X=-572_001"
  Group = -> [Cut058,Fusion033,Extrude151,Part__Feature007,Extrude152,Fillet013,Fusion036,Cut064,Extrude165,Extrude166]
FEATURE [Sketcher::SketchObject] Sketch128
  Placement = pos=(0,0,0) rot=(1,0,0;1.5708rad)
  sketch-geometry (8):
    g0: LineSegment StartX=-21.15 StartY=16.15 StartZ=0 EndX=-16.15 EndY=21.15 EndZ=0
    g1: LineSegment StartX=-16.15 StartY=21.15 StartZ=0 EndX=16.15 EndY=21.15 EndZ=0
    g2: LineSegment StartX=16.15 StartY=21.15 StartZ=0 EndX=21.15 EndY=16.15 EndZ=0
    g3: LineSegment StartX=21.15 StartY=16.15 StartZ=0 EndX=21.15 EndY=-16.15 EndZ=0
    g4: LineSegment StartX=21.15 StartY=-16.15 StartZ=0 EndX=16.15 EndY=-21.15 EndZ=0
    g5: LineSegment StartX=16.15 StartY=-21.15 StartZ=0 EndX=-16.15 EndY=-21.15 EndZ=0
    g6: LineSegment StartX=-16.15 StartY=-21.15 StartZ=0 EndX=-21.15 EndY=-16.15 EndZ=0
    g7: LineSegment StartX=-21.15 StartY=-16.15 StartZ=0 EndX=-21.15 EndY=16.15 EndZ=0
  constraints (21):
    c: Coincident(g0,g1)
    c: Horizontal(g1)
    c: Coincident(g1,g2)
    c: Coincident(g2,g3)
    c: Vertical(g3)
    c: Coincident(g3,g4)
    c: Coincident(g4,g5)
    c: Horizontal(g5)
    c: Coincident(g5,g6)
    c: Coincident(g6,g7)
    c: Coincident(g7,g0)
    c: Angle(g7,g0) = 2.35619
    c: Distance(g0,g7) = 5
    c: Distance(g2,g7) = 42.3
    c: Distance(g5,g1) = 42.3
    c: Symmetric(g6,g3,g-2)
    c: Symmetric(g5,g4,g-2)
    c: Symmetric(g0,g2,g-2)
    c: Symmetric(g0,g1,g-2)
    c: Symmetric(g0,g6,g-1)
    c: Symmetric(g0,g5,g-1)
FEATURE [Part::Extrusion] Extrude167
  Base = -> Sketch128
  Dir = (0,48,0)
  Solid = true
FEATURE [Sketcher::SketchObject] Sketch129
  Placement = pos=(0,0,0) rot=(1,0,0;1.5708rad)
  Support = -> Extrude167 [Face9]
  sketch-geometry (1):
    g0: Circle CenterX=0 CenterY=0 CenterZ=0 NormalX=0 NormalY=0 NormalZ=1 Radius=11
  constraints (2):
    c: Coincident(g0,g-1)
    c: Radius(g0) = 11
FEATURE [Part::Extrusion] Extrude168
  Base = -> Sketch129
  Dir = (0,-2,0)
  Solid = true
FEATURE [Sketcher::SketchObject] Sketch130
  Placement = pos=(0,-2,0) rot=(1,0,0;1.5708rad)
  Support = -> Extrude168 [Face3]
  sketch-geometry (1):
    g0: Circle CenterX=0 CenterY=0 CenterZ=0 NormalX=0 NormalY=0 NormalZ=1 Radius=2.5
  constraints (2):
    c: Coincident(g0,g-1)
    c: Radius(g0) = 2.5
FEATURE [Part::Extrusion] Extrude169
  Base = -> Sketch130
  Dir = (0,-22,0)
  Solid = true
FEATURE [Part::Chamfer] Chamfer018
  Base = -> Extrude169
  Edges = 1 edges r=0.8: [Edge3]
FEATURE [Sketcher::SketchObject] Sketch131
  Placement = pos=(0,0,0) rot=(1,0,0;1.5708rad)
  Support = -> Extrude167 [Face9]
  sketch-geometry (4):
    g0: Circle CenterX=-15.5 CenterY=15.5 CenterZ=0 NormalX=0 NormalY=0 NormalZ=1 Radius=2
    g1: Circle CenterX=15.5 CenterY=15.5 CenterZ=0 NormalX=0 NormalY=0 NormalZ=1 Radius=2
    g2: Circle CenterX=-15.5 CenterY=-15.5 CenterZ=0 NormalX=0 NormalY=0 NormalZ=1 Radius=2
    g3: Circle CenterX=15.5 CenterY=-15.5 CenterZ=0 NormalX=0 NormalY=0 NormalZ=1 Radius=2
  constraints (9):
    c: Distance(g0,g1) = 31
    c: Distance(g0,g2) = 31
    c: Symmetric(g0,g2,g-1)
    c: Symmetric(g0,g1,g-2)
    c: Symmetric(g2,g3,g-2)
    c: Radius(g0) = 2
    c: Equal(g0,g1)
    c: Equal(g0,g2)
    c: Equal(g0,g3)
FEATURE [Part::Extrusion] Extrude170
  Base = -> Sketch131
  Dir = (0,4.5,0)
  Solid = true
FEATURE [Part::Cut] Cut065
  Base = -> Extrude167
  Tool = -> Extrude170
FEATURE [Sketcher::SketchObject] Sketch132
  Placement = pos=(0,0,0) rot=(1,0,0;1.5708rad)
  sketch-geometry (1):
    g0: Circle CenterX=0 CenterY=0 CenterZ=0 NormalX=0 NormalY=0 NormalZ=1 Radius=9
  constraints (2):
    c: Coincident(g0,g-1)
    c: Radius(g0) = 9
FEATURE [Part::Extrusion] Extrude171
  Base = -> Sketch132
  Dir = (0,25,0)
  Solid = true
FEATURE [Sketcher::SketchObject] Sketch133
  Placement = pos=(0,0,0) rot=(1,0,0;1.5708rad)
  sketch-geometry (1):
    g0: Circle CenterX=0 CenterY=0 CenterZ=0 NormalX=0 NormalY=0 NormalZ=1 Radius=2.5
  constraints (2):
    c: Coincident(g0,g-1)
    c: Radius(g0) = 2.5
FEATURE [Part::Extrusion] Extrude172
  Base = -> Sketch133
  Dir = (0,10,0)
  Solid = true
FEATURE [Part::Cut] Cut066
  Base = -> Extrude171
  Tool = -> Extrude172
FEATURE [Sketcher::SketchObject] Sketch134
  Placement = pos=(0,25,0) rot=(0,0.707107,0.707107;3.14159rad)
  Support = -> Cut066 [Face3]
  sketch-geometry (1):
    g0: Circle CenterX=0 CenterY=0 CenterZ=0 NormalX=0 NormalY=0 NormalZ=1 Radius=4
  constraints (2):
    c: Coincident(g0,g-1)
    c: Radius(g0) = 4
FEATURE [Part::Extrusion] Extrude173
  Base = -> Sketch134
  Dir = (0,-10,0)
  Solid = true
FEATURE [Part::Cut] Cut067  label="Accouplement_006"
  Base = -> Cut066
  Placement = pos=(-715,-12,0) rot=(1,0,0;3.14159rad)
  Tool = -> Extrude173
FEATURE [Part::Fuse] Fusion037
  Base = -> Extrude168
  Tool = -> Cut065
FEATURE [Part::Fuse] Fusion038  label="Moteur_006"
  Base = -> Chamfer018
  Placement = pos=(-715,0,0) rot=(0,0,1;0rad)
  Tool = -> Fusion037
FEATURE [Sketcher::SketchObject] Sketch135
  Placement = pos=(0,0,0) rot=(1,0,0;1.5708rad)
  sketch-geometry (4):
    g0: LineSegment StartX=-50 StartY=0 StartZ=0 EndX=-47 EndY=0 EndZ=0
    g1: LineSegment StartX=47 StartY=0 StartZ=0 EndX=50 EndY=0 EndZ=0
    g2: ArcOfCircle CenterX=0 CenterY=0 CenterZ=0 NormalX=0 NormalY=0 NormalZ=1 Radius=47 StartAngle=3.14159 EndAngle=6.28319
    g3: ArcOfCircle CenterX=0 CenterY=0 CenterZ=0 NormalX=0 NormalY=0 NormalZ=1 Radius=50 StartAngle=3.14159 EndAngle=6.28319
  constraints (13):
    c: Horizontal(g0)
    c: PointOnObject(g1,g-1)
    c: Horizontal(g1)
    c: Coincident(g2,g-1)
    c: PointOnObject(g2,g-1)
    c: Coincident(g3,g-1)
    c: Coincident(g3,g1)
    c: PointOnObject(g3,g-1)
    c: Coincident(g0,g3)
    c: Coincident(g0,g2)
    c: Distance(g0,g1) = 100
    c: Distance(g0,g0) = 3
    c: Coincident(g1,g2)
FEATURE [Part::Extrusion] Extrude174  label="Demi_tube_sous_miroir_006"
  Base = -> Sketch135
  Dir = (0,2000,0)
  Placement = pos=(-715,-62,20) rot=(0,0,1;3.14159rad)
  Solid = true
FEATURE [Part::Feature] Part__Feature008  label="Coussinet_autolub_C2-151-8-128_006"
  Placement = pos=(-715,-46,0) rot=(0,0,1;1.5708rad)
  shape: bbox 16 x 8 x 16 mm, 12 faces (baked)
FEATURE [Sketcher::SketchObject] Sketch136
  Placement = pos=(0,0,0) rot=(1,0,0;1.5708rad)
  sketch-geometry (21):
    g0: Circle CenterX=0 CenterY=0 CenterZ=0 NormalX=0 NormalY=0 NormalZ=1 Radius=6
    g1: LineSegment StartX=-20.5 StartY=15 StartZ=0 EndX=20.5 EndY=15 EndZ=0
    g2: ArcOfCircle CenterX=20.5 CenterY=13 CenterZ=0 NormalX=0 NormalY=0 NormalZ=1 Radius=2 StartAngle=6.28319 EndAngle=7.85398
    g3: LineSegment StartX=22.5 StartY=13 StartZ=0 EndX=22.5 EndY=-73 EndZ=0
    g4: LineSegment StartX=-22.5 StartY=13 StartZ=0 EndX=-22.5 EndY=-73 EndZ=0
    g5: ArcOfCircle CenterX=-20.5 CenterY=13 CenterZ=0 NormalX=0 NormalY=0 NormalZ=1 Radius=2 StartAngle=1.5708 EndAngle=3.14159
    g6: ArcOfCircle CenterX=-20.5 CenterY=-73 CenterZ=0 NormalX=0 NormalY=0 NormalZ=1 Radius=2 StartAngle=3.14159 EndAngle=4.71239
    g7: ArcOfCircle CenterX=20.5 CenterY=-73 CenterZ=0 NormalX=0 NormalY=0 NormalZ=1 Radius=2 StartAngle=4.71239 EndAngle=6.28319
    g8: LineSegment StartX=-20.5 StartY=-75 StartZ=0 EndX=20.5 EndY=-75 EndZ=0
    g9: ArcOfCircle CenterX=0 CenterY=-16.7 CenterZ=0 NormalX=0 NormalY=0 NormalZ=1 Radius=1.5 StartAngle=0 EndAngle=3.14159
    g10: ArcOfCircle CenterX=0 CenterY=-24.3 CenterZ=0 NormalX=0 NormalY=0 NormalZ=1 Radius=1.5 StartAngle=3.14159 EndAngle=6.28319
    g11: LineSegment StartX=-1.5 StartY=-16.7 StartZ=0 EndX=-1.5 EndY=-24.3 EndZ=0
    g12: LineSegment StartX=1.5 StartY=-16.7 StartZ=0 EndX=1.5 EndY=-24.3 EndZ=0
    g13: Circle CenterX=-12.5 CenterY=-45 CenterZ=0 NormalX=0 NormalY=0 NormalZ=1 Radius=3.5
    g14: Circle CenterX=12.5 CenterY=-45 CenterZ=0 NormalX=0 NormalY=0 NormalZ=1 Radius=3.5
    g15: Circle CenterX=-12.5 CenterY=-65 CenterZ=0 NormalX=0 NormalY=0 NormalZ=1 Radius=3.5
    g16: Circle CenterX=12.5 CenterY=-65 CenterZ=0 NormalX=0 NormalY=0 NormalZ=1 Radius=3.5
    g17: LineSegment [constr] StartX=-12.5 StartY=-45 StartZ=0 EndX=12.5 EndY=-45 EndZ=0
    g18: LineSegment [constr] StartX=-12.5 StartY=-45 StartZ=0 EndX=-12.5 EndY=-65 EndZ=0
    g19: LineSegment [constr] StartX=-12.5 StartY=-65 StartZ=0 EndX=12.5 EndY=-65 EndZ=0
    g20: LineSegment [constr] StartX=12.5 StartY=-45 StartZ=0 EndX=12.5 EndY=-65 EndZ=0
  constraints (59):
    c: Coincident(g0,g-1)
    c: Radius(g0) = 6
    c: Horizontal(g1)
    c: Coincident(g2,g1)
    c: Coincident(g3,g2)
    c: Vertical(g3)
    c: Vertical(g4)
    c: Coincident(g5,g1)
    c: Coincident(g5,g4)
    c: Coincident(g7,g3)
    c: Coincident(g8,g6)
    c: Coincident(g8,g7)
    c: Tangent(g8,g7)
    c: Tangent(g5,g4)
    c: Tangent(g5,g1)
    c: Tangent(g1,g2)
    c: Tangent(g2,g3)
    c: Coincident(g4,g6)
    c: Tangent(g6,g4)
    c: Tangent(g6,g8)
    c: Horizontal(g8)
    c: Tangent(g7,g3)
    c: Distance(g4,g2) = 45
    c: Symmetric(g4,g2,g-2)
    c: Distance(g1,g6) = 90
    c: DistanceY(g-1,g1) = 15
    c: Tangent(g9,g12) = 1.5708
    c: Tangent(g9,g11) = -1.5708
    c: Tangent(g11,g10) = -1.5708
    c: Tangent(g12,g10) = 1.5708
    c: Vertical(g11)
    c: Equal(g9,g10)
    c: PointOnObject(g9,g-2)
    c: Distance(g-1,g9) = 16.7
    c: Distance(g9,g10) = 7.6
    c: Radius(g9) = 1.5
    c: Radius(g13) = 3.5
    c: Equal(g13,g14)
    c: Equal(g13,g16)
    c: Equal(g13,g15)
    c: Radius(g5) = 2
    c: Equal(g5,g7)
    c: Equal(g5,g6)
    c: DistanceY(g-1,g13) = -45
    c: Coincident(g17,g13)
    c: Coincident(g17,g14)
    c: Horizontal(g17)
    c: Coincident(g18,g13)
    c: Coincident(g18,g15)
    c: Coincident(g19,g15)
    c: Coincident(g19,g16)
    c: Horizontal(g19)
    c: Coincident(g20,g14)
    c: Coincident(g20,g16)
    c: Vertical(g18)
    c: Vertical(g20)
    c: Distance(g13,g15) = 20
    c: Distance(g13,g14) = 25
    c: Symmetric(g13,g14,g-2)
FEATURE [Part::Extrusion] Extrude175  label="Plaque_support_006"
  Base = -> Sketch136
  Dir = (0,6,0)
  Placement = pos=(-715,-46,0) rot=(0,0,1;0rad)
  Solid = true
FEATURE [Sketcher::SketchObject] Sketch137
  Placement = pos=(0,0,0) rot=(0.57735,0.57735,0.57735;2.0944rad)
  sketch-geometry (8):
    g0: LineSegment StartX=0 StartY=33 StartZ=0 EndX=-2 EndY=33 EndZ=0
    g1: LineSegment StartX=-2 StartY=33 StartZ=0 EndX=-2 EndY=-24 EndZ=0
    g2: ArcOfCircle CenterX=-4 CenterY=-24 CenterZ=0 NormalX=0 NormalY=0 NormalZ=1 Radius=2 StartAngle=4.71239 EndAngle=6.28319
    g3: LineSegment StartX=-4 StartY=-26 StartZ=0 EndX=-38 EndY=-26 EndZ=0
    g4: LineSegment StartX=-38 StartY=-26 StartZ=0 EndX=-38 EndY=-28 EndZ=0
    g5: LineSegment StartX=-38 StartY=-28 StartZ=0 EndX=-4 EndY=-28 EndZ=0
    g6: ArcOfCircle CenterX=-4 CenterY=-24 CenterZ=0 NormalX=0 NormalY=0 NormalZ=1 Radius=4 StartAngle=4.71239 EndAngle=6.28319
    g7: LineSegment StartX=0 StartY=-24 StartZ=0 EndX=0 EndY=33 EndZ=0
  constraints (22):
    c: PointOnObject(g0,g-2)
    c: Horizontal(g0)
    c: Coincident(g0,g1)
    c: Vertical(g1)
    c: Tangent(g1,g2) = 1.5708
    c: Tangent(g2,g3) = 1.5708
    c: Coincident(g3,g4)
    c: Vertical(g4)
    c: Coincident(g4,g5)
    c: Horizontal(g5)
    c: Tangent(g5,g6) = -1.5708
    c: PointOnObject(g6,g-2)
    c: Tangent(g6,g7) = -1.5708
    c: Coincident(g7,g0)
    c: Horizontal(g3)
    c: DistanceX(g0,g0) = 2
    c: Radius(g2) = 2
    c: Radius(g6) = 4
    c: DistanceY(g3,g4) = -2
    c: Distance(g-1,g0) = 33
    c: DistanceY(g-1,g5) = -28
    c: DistanceX(g6,g4) = -38
FEATURE [Part::Extrusion] Extrude176
  Base = -> Sketch137
  Dir = (-32.5,0,0)
  Solid = true
FEATURE [Part::Extrusion] Extrude177
  Base = -> Sketch137
  Dir = (32.5,0,0)
  Solid = true
FEATURE [Part::MultiFuse] Fusion039
  Shapes = -> [Extrude176,Extrude177]
FEATURE [Sketcher::SketchObject] Sketch138
  Placement = pos=(0,-2,0) rot=(1,0,0;1.5708rad)
  Support = -> Fusion039 [Face3]
  sketch-geometry (9):
    g0: ArcOfCircle CenterX=0 CenterY=0 CenterZ=0 NormalX=0 NormalY=0 NormalZ=1 Radius=32.5 StartAngle=0 EndAngle=3.14159
    g1: LineSegment StartX=-32.5 StartY=0 StartZ=0 EndX=-32.5 EndY=34 EndZ=0
    g2: LineSegment StartX=-32.5 StartY=34 StartZ=0 EndX=32.5 EndY=34 EndZ=0
    g3: LineSegment StartX=32.5 StartY=34 StartZ=0 EndX=32.5 EndY=0 EndZ=0
    g4: Circle CenterX=0 CenterY=0 CenterZ=0 NormalX=0 NormalY=0 NormalZ=1 Radius=11
    g5: Circle CenterX=-15.5 CenterY=15.5 CenterZ=0 NormalX=0 NormalY=0 NormalZ=1 Radius=2
    g6: Circle CenterX=15.5 CenterY=15.5 CenterZ=0 NormalX=0 NormalY=0 NormalZ=1 Radius=2
    g7: Circle CenterX=-15.5 CenterY=-15.5 CenterZ=0 NormalX=0 NormalY=0 NormalZ=1 Radius=2
    g8: Circle CenterX=15.5 CenterY=-15.5 CenterZ=0 NormalX=0 NormalY=0 NormalZ=1 Radius=2
  constraints (23):
    c: Coincident(g0,g-1)
    c: PointOnObject(g0,g-1)
    c: PointOnObject(g0,g-1)
    c: Coincident(g1,g0)
    c: Vertical(g1)
    c: Coincident(g1,g2)
    c: Horizontal(g2)
    c: Coincident(g2,g3)
    c: Coincident(g3,g0)
    c: Vertical(g3)
    c: DistanceY(g1,g0) = -34
    c: Coincident(g4,g-1)
    c: Radius(g4) = 11
    c: DistanceX(g1,g2) = 65
    c: Radius(g5) = 2
    c: Equal(g5,g6)
    c: Equal(g5,g8)
    c: Equal(g5,g7)
    c: Symmetric(g5,g6,g-2)
    c: Symmetric(g5,g7,g-1)
    c: Symmetric(g7,g8,g-2)
    c: DistanceX(g5,g6) = 31
    c: DistanceY(g5,g7) = -31
FEATURE [Part::Extrusion] Extrude178
  Base = -> Sketch138
  Dir = (0,2,0)
  Solid = true
FEATURE [Part::Cut] Cut068
  Base = -> Fusion039
  Tool = -> Extrude178
FEATURE [Sketcher::SketchObject] Sketch139
  ExternalGeometry = -> [Cut068]
  Placement = pos=(0,0,-26) rot=(0,0,1;0rad)
  Support = -> Cut068 [Face5]
  sketch-geometry (5):
    g0: Circle CenterX=-25 CenterY=-12 CenterZ=0 NormalX=0 NormalY=0 NormalZ=1 Radius=3.5
    g1: Circle CenterX=-25 CenterY=-30 CenterZ=0 NormalX=0 NormalY=0 NormalZ=1 Radius=3.5
    g2: Circle CenterX=25 CenterY=-12 CenterZ=0 NormalX=0 NormalY=0 NormalZ=1 Radius=3.5
    g3: Circle CenterX=25 CenterY=-30 CenterZ=0 NormalX=0 NormalY=0 NormalZ=1 Radius=3.5
    g4: LineSegment [constr] StartX=-25 StartY=-12 StartZ=0 EndX=-25 EndY=-30 EndZ=0
  constraints (12):
    c: Radius(g0) = 3.5
    c: Equal(g0,g2)
    c: Equal(g0,g3)
    c: Equal(g0,g1)
    c: Symmetric(g0,g2,g-2)
    c: Symmetric(g1,g3,g-2)
    c: Coincident(g4,g0)
    c: Coincident(g4,g1)
    c: Vertical(g4)
    c: DistanceY(g0,g1) = -18
    c: DistanceY(g-3,g1) = 8
    c: DistanceX(g0,g2) = 50
FEATURE [Part::Extrusion] Extrude179
  Base = -> Sketch139
  Dir = (0,0,-2)
  Solid = true
FEATURE [Part::Cut] Cut069
  Base = -> Cut068
  Tool = -> Extrude179
FEATURE [Part::Fillet] Fillet015  label="Plaque_moteur_006"
  Base = -> Cut069
  Edges = 2 edges r=4: [Edge5,Edge59]
  Placement = pos=(-715,0,0) rot=(0,0,1;0rad)
FEATURE [Sketcher::SketchObject] Sketch140
  Placement = pos=(0,0,0) rot=(1,0,0;1.5708rad)
  sketch-geometry (4):
    g0: LineSegment StartX=-3.15 StartY=5.95 StartZ=0 EndX=3.15 EndY=5.95 EndZ=0
    g1: LineSegment StartX=3.15 StartY=5.95 StartZ=0 EndX=3.15 EndY=-5.95 EndZ=0
    g2: LineSegment StartX=3.15 StartY=-5.95 StartZ=0 EndX=-3.15 EndY=-5.95 EndZ=0
    g3: LineSegment StartX=-3.15 StartY=-5.95 StartZ=0 EndX=-3.15 EndY=5.95 EndZ=0
  constraints (12):
    c: Coincident(g0,g1)
    c: Coincident(g1,g2)
    c: Coincident(g2,g3)
    c: Coincident(g3,g0)
    c: Horizontal(g0)
    c: Horizontal(g2)
    c: Vertical(g1)
    c: Vertical(g3)
    c: DistanceX(g0,g0) = 6.3
    c: DistanceY(g0,g2) = -11.9
    c: Symmetric(g0,g0,g-2)
    c: Symmetric(g0,g1,g-1)
FEATURE [Part::Extrusion] Extrude180
  Base = -> Sketch140
  Dir = (0,-10.8,0)
  Solid = true
FEATURE [Sketcher::SketchObject] Sketch141
  ExternalGeometry = -> [Extrude180]
  Placement = pos=(0,-10.8,0) rot=(1,0,0;1.5708rad)
  Support = -> Extrude180 [Face6]
  sketch-geometry (4):
    g0: LineSegment StartX=-3.15 StartY=1.55 StartZ=0 EndX=3.15 EndY=1.55 EndZ=0
    g1: LineSegment StartX=3.15 StartY=1.55 StartZ=0 EndX=3.15 EndY=-1.55 EndZ=0
    g2: LineSegment StartX=3.15 StartY=-1.55 StartZ=0 EndX=-3.15 EndY=-1.55 EndZ=0
    g3: LineSegment StartX=-3.15 StartY=-1.55 StartZ=0 EndX=-3.15 EndY=1.55 EndZ=0
  constraints (12):
    c: Coincident(g0,g1)
    c: Coincident(g1,g2)
    c: Coincident(g2,g3)
    c: Coincident(g3,g0)
    c: Horizontal(g0)
    c: Horizontal(g2)
    c: Vertical(g1)
    c: Vertical(g3)
    c: PointOnObject(g0,g-4)
    c: PointOnObject(g0,g-3)
    c: DistanceY(g0,g2) = -3.1
    c: Symmetric(g0,g1,g-1)
FEATURE [Part::Extrusion] Extrude181
  Base = -> Sketch141
  Dir = (0,7.7,0)
  Solid = true
FEATURE [Part::Cut] Cut070
  Base = -> Extrude180
  Tool = -> Extrude181
FEATURE [Part::Chamfer] Chamfer019
  Base = -> Cut070
  Edges = 4 edges r=0.5: [Edge7,Edge9,Edge15,Edge17]
FEATURE [Part::Chamfer] Chamfer020
  Base = -> Chamfer019
  Edges = 1 edges r=1.2: [Edge13]
FEATURE [Sketcher::SketchObject] Sketch142
  ExternalGeometry = -> [Chamfer020]
  Placement = pos=(0,0,5.95) rot=(0,0,1;0rad)
  Support = -> Chamfer020 [Face5]
  sketch-geometry (4):
    g0: LineSegment StartX=-3 StartY=0 StartZ=0 EndX=3 EndY=0 EndZ=0
    g1: LineSegment StartX=3 StartY=0 StartZ=0 EndX=3 EndY=-3.1 EndZ=0
    g2: LineSegment StartX=3 StartY=-3.1 StartZ=0 EndX=-3 EndY=-3.1 EndZ=0
    g3: LineSegment StartX=-3 StartY=-3.1 StartZ=0 EndX=-3 EndY=0 EndZ=0
  constraints (12):
    c: Coincident(g0,g1)
    c: Coincident(g1,g2)
    c: Coincident(g2,g3)
    c: Coincident(g3,g0)
    c: Horizontal(g0)
    c: Horizontal(g2)
    c: Vertical(g1)
    c: Vertical(g3)
    c: PointOnObject(g0,g-1)
    c: DistanceX(g-3,g0) = 0.15
    c: Symmetric(g0,g0,g-2)
    c: DistanceY(g0,g1) = -3.1
FEATURE [Part::Extrusion] Extrude182
  Base = -> Sketch142
  Dir = (0,0,6.3)
  Solid = true
FEATURE [Sketcher::SketchObject] Sketch143
  ExternalGeometry = -> [Extrude182]
  Placement = pos=(0,-3.1,0) rot=(1,0,0;1.5708rad)
  Support = -> Extrude182 [Face3]
  sketch-geometry (1):
    g0: Circle CenterX=0 CenterY=9.5 CenterZ=0 NormalX=0 NormalY=0 NormalZ=1 Radius=1.65
  constraints (3):
    c: PointOnObject(g0,g-2)
    c: Radius(g0) = 1.65
    c: DistanceY(g0,g-3) = -3.55
FEATURE [Part::Extrusion] Extrude183
  Base = -> Sketch143
  Dir = (0,6,0)
  Solid = true
FEATURE [Part::Cut] Cut071
  Base = -> Extrude182
  Tool = -> Extrude183
FEATURE [Part::Fillet] Fillet016
  Base = -> Cut071
  Edges = 2 edges r=1.35: [Edge8,Edge11]
FEATURE [Part::MultiFuse] Fusion040
  Shapes = -> [Chamfer020]
FEATURE [Sketcher::SketchObject] Sketch144
  Placement = pos=(0,0,0) rot=(0,0.707107,0.707107;3.14159rad)
  Support = -> Fusion040 [Face7]
  sketch-geometry (4):
    g0: Circle CenterX=-1.27 CenterY=3.8 CenterZ=0 NormalX=0 NormalY=0 NormalZ=1 Radius=0.2
    g1: Circle CenterX=1.27 CenterY=3.8 CenterZ=0 NormalX=0 NormalY=0 NormalZ=1 Radius=0.2
    g2: Circle CenterX=-1.27 CenterY=-3.8 CenterZ=0 NormalX=0 NormalY=0 NormalZ=1 Radius=0.2
    g3: Circle CenterX=1.27 CenterY=-3.8 CenterZ=0 NormalX=0 NormalY=0 NormalZ=1 Radius=0.2
  constraints (9):
    c: Radius(g0) = 0.2
    c: Equal(g0,g1)
    c: Equal(g0,g3)
    c: Equal(g0,g2)
    c: Symmetric(g0,g1,g-2)
    c: Symmetric(g2,g3,g-2)
    c: Symmetric(g0,g2,g-1)
    c: DistanceX(g0,g1) = 2.54
    c: DistanceY(g1,g3) = -7.6
FEATURE [Part::Extrusion] Extrude184
  Base = -> Sketch144
  Dir = (0,7.8,0)
  Solid = true
FEATURE [Part::MultiFuse] Fusion041  label="Capteur_optique_006"
  Placement = pos=(-715,-46,-20.7) rot=(0,0,1;0rad)
  Shapes = -> [Fusion040,Fillet016,Extrude184]
FEATURE [Sketcher::SketchObject] Sketch145
  Placement = pos=(0,0,0) rot=(1,0,0;1.5708rad)
  sketch-geometry (1):
    g0: Circle CenterX=0 CenterY=0 CenterZ=0 NormalX=0 NormalY=0 NormalZ=1 Radius=4
  constraints (2):
    c: Coincident(g0,g-1)
    c: Radius(g0) = 4
FEATURE [Part::Extrusion] Extrude185
  Base = -> Sketch145
  Dir = (0,50,0)
  Solid = true
FEATURE [Sketcher::SketchObject] Sketch146
  Placement = pos=(0,0,0) rot=(0.57735,0.57735,0.57735;2.0944rad)
  sketch-geometry (1):
    g0: Circle CenterX=6 CenterY=0 CenterZ=0 NormalX=0 NormalY=0 NormalZ=1 Radius=2
  constraints (3):
    c: DistanceX(g-1,g0) = 6
    c: Radius(g0) = 2
    c: PointOnObject(g0,g-1)
FEATURE [Part::Extrusion] Extrude186
  Base = -> Sketch146
  Dir = (4,0,0)
  Solid = true
FEATURE [Part::Extrusion] Extrude187
  Base = -> Sketch146
  Dir = (-4,0,0)
  Solid = true
FEATURE [Part::Cut] Cut072
  Base = -> Extrude185
  Tool = -> Extrude186
FEATURE [Part::Cut] Cut073  label="Axe_D8_006"
  Base = -> Cut072
  Placement = pos=(-715,-86,0) rot=(0,0,1;0rad)
  Tool = -> Extrude187
FEATURE [Sketcher::SketchObject] Sketch147
  Placement = pos=(0,0,0) rot=(1,0,0;1.5708rad)
  sketch-geometry (1):
    g0: Circle CenterX=0 CenterY=0 CenterZ=0 NormalX=0 NormalY=0 NormalZ=1 Radius=2
  constraints (2):
    c: Coincident(g0,g-1)
    c: Radius(g0) = 2
FEATURE [Part::Extrusion] Extrude188  label="Axe_D4_006"
  Base = -> Sketch147
  Dir = (0,103.6,0)
  Placement = pos=(-663.2,-80,0) rot=(0,0,1;1.5708rad)
  Solid = true
FEATURE [Sketcher::SketchObject] Sketch148
  Placement = pos=(0,0,0) rot=(1,0,0;1.5708rad)
  sketch-geometry (8):
    g0: LineSegment StartX=-50 StartY=0 StartZ=0 EndX=50 EndY=0 EndZ=0
    g1: LineSegment StartX=50 StartY=0 StartZ=0 EndX=50 EndY=-2 EndZ=0
    g2: LineSegment StartX=50 StartY=-2 StartZ=0 EndX=47 EndY=-2 EndZ=0
    g3: LineSegment StartX=47 StartY=-2 StartZ=0 EndX=44 EndY=-16 EndZ=0
    g4: LineSegment StartX=44 StartY=-16 StartZ=0 EndX=-44 EndY=-16 EndZ=0
    g5: LineSegment StartX=-44 StartY=-16 StartZ=0 EndX=-47 EndY=-2 EndZ=0
    g6: LineSegment StartX=-47 StartY=-2 StartZ=0 EndX=-50 EndY=-2 EndZ=0
    g7: LineSegment StartX=-50 StartY=-2 StartZ=0 EndX=-50 EndY=0 EndZ=0
  constraints (24):
    c: PointOnObject(g0,g-1)
    c: Horizontal(g0)
    c: Coincident(g0,g1)
    c: Vertical(g1)
    c: Coincident(g1,g2)
    c: Horizontal(g2)
    c: Coincident(g2,g3)
    c: Coincident(g3,g4)
    c: Horizontal(g4)
    c: Coincident(g4,g5)
    c: Coincident(g5,g6)
    c: Horizontal(g6)
    c: Coincident(g6,g7)
    c: Coincident(g7,g0)
    c: Vertical(g7)
    c: DistanceY(g0,g6) = -2
    c: DistanceX(g6,g5) = 3
    c: DistanceX(g0,g0) = 100
    c: Symmetric(g0,g0,g-2)
    c: Symmetric(g6,g1,g-2)
    c: Symmetric(g5,g2,g-2)
    c: Symmetric(g4,g3,g-2)
    c: DistanceX(g4,g3) = 88
    c: DistanceY(g0,g4) = -16
FEATURE [Part::Extrusion] Extrude189  label="Plaque_alveolaire_006"
  Base = -> Sketch148
  Dir = (0,2000,0)
  Placement = pos=(-715,-62,22) rot=(0,0,1;3.14159rad)
  Solid = true
FEATURE [App::DocumentObjectGroup] Groupe008  label="Assemblage_miroir X=-715_001"
  Group = -> [Cut067,Fusion038,Extrude174,Part__Feature008,Extrude175,Fillet015,Fusion041,Cut073,Extrude188,Extrude189]
FEATURE [Sketcher::SketchObject] Sketch149
  Placement = pos=(0,0,0) rot=(1,0,0;1.5708rad)
  sketch-geometry (8):
    g0: LineSegment StartX=-21.15 StartY=16.15 StartZ=0 EndX=-16.15 EndY=21.15 EndZ=0
    g1: LineSegment StartX=-16.15 StartY=21.15 StartZ=0 EndX=16.15 EndY=21.15 EndZ=0
    g2: LineSegment StartX=16.15 StartY=21.15 StartZ=0 EndX=21.15 EndY=16.15 EndZ=0
    g3: LineSegment StartX=21.15 StartY=16.15 StartZ=0 EndX=21.15 EndY=-16.15 EndZ=0
    g4: LineSegment StartX=21.15 StartY=-16.15 StartZ=0 EndX=16.15 EndY=-21.15 EndZ=0
    g5: LineSegment StartX=16.15 StartY=-21.15 StartZ=0 EndX=-16.15 EndY=-21.15 EndZ=0
    g6: LineSegment StartX=-16.15 StartY=-21.15 StartZ=0 EndX=-21.15 EndY=-16.15 EndZ=0
    g7: LineSegment StartX=-21.15 StartY=-16.15 StartZ=0 EndX=-21.15 EndY=16.15 EndZ=0
  constraints (21):
    c: Coincident(g0,g1)
    c: Horizontal(g1)
    c: Coincident(g1,g2)
    c: Coincident(g2,g3)
    c: Vertical(g3)
    c: Coincident(g3,g4)
    c: Coincident(g4,g5)
    c: Horizontal(g5)
    c: Coincident(g5,g6)
    c: Coincident(g6,g7)
    c: Coincident(g7,g0)
    c: Angle(g7,g0) = 2.35619
    c: Distance(g0,g7) = 5
    c: Distance(g2,g7) = 42.3
    c: Distance(g5,g1) = 42.3
    c: Symmetric(g6,g3,g-2)
    c: Symmetric(g5,g4,g-2)
    c: Symmetric(g0,g2,g-2)
    c: Symmetric(g0,g1,g-2)
    c: Symmetric(g0,g6,g-1)
    c: Symmetric(g0,g5,g-1)
FEATURE [Part::Extrusion] Extrude190
  Base = -> Sketch149
  Dir = (0,48,0)
  Solid = true
FEATURE [Sketcher::SketchObject] Sketch150
  Placement = pos=(0,0,0) rot=(1,0,0;1.5708rad)
  Support = -> Extrude190 [Face9]
  sketch-geometry (1):
    g0: Circle CenterX=0 CenterY=0 CenterZ=0 NormalX=0 NormalY=0 NormalZ=1 Radius=11
  constraints (2):
    c: Coincident(g0,g-1)
    c: Radius(g0) = 11
FEATURE [Part::Extrusion] Extrude191
  Base = -> Sketch150
  Dir = (0,-2,0)
  Solid = true
FEATURE [Sketcher::SketchObject] Sketch151
  Placement = pos=(0,-2,0) rot=(1,0,0;1.5708rad)
  Support = -> Extrude191 [Face3]
  sketch-geometry (1):
    g0: Circle CenterX=0 CenterY=0 CenterZ=0 NormalX=0 NormalY=0 NormalZ=1 Radius=2.5
  constraints (2):
    c: Coincident(g0,g-1)
    c: Radius(g0) = 2.5
FEATURE [Part::Extrusion] Extrude192
  Base = -> Sketch151
  Dir = (0,-22,0)
  Solid = true
FEATURE [Part::Chamfer] Chamfer021
  Base = -> Extrude192
  Edges = 1 edges r=0.8: [Edge3]
FEATURE [Sketcher::SketchObject] Sketch152
  Placement = pos=(0,0,0) rot=(1,0,0;1.5708rad)
  Support = -> Extrude190 [Face9]
  sketch-geometry (4):
    g0: Circle CenterX=-15.5 CenterY=15.5 CenterZ=0 NormalX=0 NormalY=0 NormalZ=1 Radius=2
    g1: Circle CenterX=15.5 CenterY=15.5 CenterZ=0 NormalX=0 NormalY=0 NormalZ=1 Radius=2
    g2: Circle CenterX=-15.5 CenterY=-15.5 CenterZ=0 NormalX=0 NormalY=0 NormalZ=1 Radius=2
    g3: Circle CenterX=15.5 CenterY=-15.5 CenterZ=0 NormalX=0 NormalY=0 NormalZ=1 Radius=2
  constraints (9):
    c: Distance(g0,g1) = 31
    c: Distance(g0,g2) = 31
    c: Symmetric(g0,g2,g-1)
    c: Symmetric(g0,g1,g-2)
    c: Symmetric(g2,g3,g-2)
    c: Radius(g0) = 2
    c: Equal(g0,g1)
    c: Equal(g0,g2)
    c: Equal(g0,g3)
FEATURE [Part::Extrusion] Extrude193
  Base = -> Sketch152
  Dir = (0,4.5,0)
  Solid = true
FEATURE [Part::Cut] Cut074
  Base = -> Extrude190
  Tool = -> Extrude193
FEATURE [Sketcher::SketchObject] Sketch153
  Placement = pos=(0,0,0) rot=(1,0,0;1.5708rad)
  sketch-geometry (1):
    g0: Circle CenterX=0 CenterY=0 CenterZ=0 NormalX=0 NormalY=0 NormalZ=1 Radius=9
  constraints (2):
    c: Coincident(g0,g-1)
    c: Radius(g0) = 9
FEATURE [Part::Extrusion] Extrude194
  Base = -> Sketch153
  Dir = (0,25,0)
  Solid = true
FEATURE [Sketcher::SketchObject] Sketch154
  Placement = pos=(0,0,0) rot=(1,0,0;1.5708rad)
  sketch-geometry (1):
    g0: Circle CenterX=0 CenterY=0 CenterZ=0 NormalX=0 NormalY=0 NormalZ=1 Radius=2.5
  constraints (2):
    c: Coincident(g0,g-1)
    c: Radius(g0) = 2.5
FEATURE [Part::Extrusion] Extrude195
  Base = -> Sketch154
  Dir = (0,10,0)
  Solid = true
FEATURE [Part::Cut] Cut075
  Base = -> Extrude194
  Tool = -> Extrude195
FEATURE [Sketcher::SketchObject] Sketch155
  Placement = pos=(0,25,0) rot=(0,0.707107,0.707107;3.14159rad)
  Support = -> Cut075 [Face3]
  sketch-geometry (1):
    g0: Circle CenterX=0 CenterY=0 CenterZ=0 NormalX=0 NormalY=0 NormalZ=1 Radius=4
  constraints (2):
    c: Coincident(g0,g-1)
    c: Radius(g0) = 4
FEATURE [Part::Extrusion] Extrude196
  Base = -> Sketch155
  Dir = (0,-10,0)
  Solid = true
FEATURE [Part::Cut] Cut076  label="Accouplement_007"
  Base = -> Cut075
  Placement = pos=(-858,-12,0) rot=(1,0,0;3.14159rad)
  Tool = -> Extrude196
FEATURE [Part::Fuse] Fusion042
  Base = -> Extrude191
  Tool = -> Cut074
FEATURE [Part::Fuse] Fusion043  label="Moteur_007"
  Base = -> Chamfer021
  Placement = pos=(-858,0,0) rot=(0,0,1;0rad)
  Tool = -> Fusion042
FEATURE [Sketcher::SketchObject] Sketch156
  Placement = pos=(0,0,0) rot=(1,0,0;1.5708rad)
  sketch-geometry (4):
    g0: LineSegment StartX=-50 StartY=0 StartZ=0 EndX=-47 EndY=0 EndZ=0
    g1: LineSegment StartX=47 StartY=0 StartZ=0 EndX=50 EndY=0 EndZ=0
    g2: ArcOfCircle CenterX=0 CenterY=0 CenterZ=0 NormalX=0 NormalY=0 NormalZ=1 Radius=47 StartAngle=3.14159 EndAngle=6.28319
    g3: ArcOfCircle CenterX=0 CenterY=0 CenterZ=0 NormalX=0 NormalY=0 NormalZ=1 Radius=50 StartAngle=3.14159 EndAngle=6.28319
  constraints (13):
    c: Horizontal(g0)
    c: PointOnObject(g1,g-1)
    c: Horizontal(g1)
    c: Coincident(g2,g-1)
    c: PointOnObject(g2,g-1)
    c: Coincident(g3,g-1)
    c: Coincident(g3,g1)
    c: PointOnObject(g3,g-1)
    c: Coincident(g0,g3)
    c: Coincident(g0,g2)
    c: Distance(g0,g1) = 100
    c: Distance(g0,g0) = 3
    c: Coincident(g1,g2)
FEATURE [Part::Extrusion] Extrude197  label="Demi_tube_sous_miroir_007"
  Base = -> Sketch156
  Dir = (0,2000,0)
  Placement = pos=(-858,-62,20) rot=(0,0,1;3.14159rad)
  Solid = true
FEATURE [Part::Feature] Part__Feature009  label="Coussinet_autolub_C2-151-8-128_007"
  Placement = pos=(-858,-46,0) rot=(0,0,1;1.5708rad)
  shape: bbox 16 x 8 x 16 mm, 12 faces (baked)
FEATURE [Sketcher::SketchObject] Sketch157
  Placement = pos=(0,0,0) rot=(1,0,0;1.5708rad)
  sketch-geometry (21):
    g0: Circle CenterX=0 CenterY=0 CenterZ=0 NormalX=0 NormalY=0 NormalZ=1 Radius=6
    g1: LineSegment StartX=-20.5 StartY=15 StartZ=0 EndX=20.5 EndY=15 EndZ=0
    g2: ArcOfCircle CenterX=20.5 CenterY=13 CenterZ=0 NormalX=0 NormalY=0 NormalZ=1 Radius=2 StartAngle=6.28319 EndAngle=7.85398
    g3: LineSegment StartX=22.5 StartY=13 StartZ=0 EndX=22.5 EndY=-73 EndZ=0
    g4: LineSegment StartX=-22.5 StartY=13 StartZ=0 EndX=-22.5 EndY=-73 EndZ=0
    g5: ArcOfCircle CenterX=-20.5 CenterY=13 CenterZ=0 NormalX=0 NormalY=0 NormalZ=1 Radius=2 StartAngle=1.5708 EndAngle=3.14159
    g6: ArcOfCircle CenterX=-20.5 CenterY=-73 CenterZ=0 NormalX=0 NormalY=0 NormalZ=1 Radius=2 StartAngle=3.14159 EndAngle=4.71239
    g7: ArcOfCircle CenterX=20.5 CenterY=-73 CenterZ=0 NormalX=0 NormalY=0 NormalZ=1 Radius=2 StartAngle=4.71239 EndAngle=6.28319
    g8: LineSegment StartX=-20.5 StartY=-75 StartZ=0 EndX=20.5 EndY=-75 EndZ=0
    g9: ArcOfCircle CenterX=0 CenterY=-16.7 CenterZ=0 NormalX=0 NormalY=0 NormalZ=1 Radius=1.5 StartAngle=0 EndAngle=3.14159
    g10: ArcOfCircle CenterX=0 CenterY=-24.3 CenterZ=0 NormalX=0 NormalY=0 NormalZ=1 Radius=1.5 StartAngle=3.14159 EndAngle=6.28319
    g11: LineSegment StartX=-1.5 StartY=-16.7 StartZ=0 EndX=-1.5 EndY=-24.3 EndZ=0
    g12: LineSegment StartX=1.5 StartY=-16.7 StartZ=0 EndX=1.5 EndY=-24.3 EndZ=0
    g13: Circle CenterX=-12.5 CenterY=-45 CenterZ=0 NormalX=0 NormalY=0 NormalZ=1 Radius=3.5
    g14: Circle CenterX=12.5 CenterY=-45 CenterZ=0 NormalX=0 NormalY=0 NormalZ=1 Radius=3.5
    g15: Circle CenterX=-12.5 CenterY=-65 CenterZ=0 NormalX=0 NormalY=0 NormalZ=1 Radius=3.5
    g16: Circle CenterX=12.5 CenterY=-65 CenterZ=0 NormalX=0 NormalY=0 NormalZ=1 Radius=3.5
    g17: LineSegment [constr] StartX=-12.5 StartY=-45 StartZ=0 EndX=12.5 EndY=-45 EndZ=0
    g18: LineSegment [constr] StartX=-12.5 StartY=-45 StartZ=0 EndX=-12.5 EndY=-65 EndZ=0
    g19: LineSegment [constr] StartX=-12.5 StartY=-65 StartZ=0 EndX=12.5 EndY=-65 EndZ=0
    g20: LineSegment [constr] StartX=12.5 StartY=-45 StartZ=0 EndX=12.5 EndY=-65 EndZ=0
  constraints (59):
    c: Coincident(g0,g-1)
    c: Radius(g0) = 6
    c: Horizontal(g1)
    c: Coincident(g2,g1)
    c: Coincident(g3,g2)
    c: Vertical(g3)
    c: Vertical(g4)
    c: Coincident(g5,g1)
    c: Coincident(g5,g4)
    c: Coincident(g7,g3)
    c: Coincident(g8,g6)
    c: Coincident(g8,g7)
    c: Tangent(g8,g7)
    c: Tangent(g5,g4)
    c: Tangent(g5,g1)
    c: Tangent(g1,g2)
    c: Tangent(g2,g3)
    c: Coincident(g4,g6)
    c: Tangent(g6,g4)
    c: Tangent(g6,g8)
    c: Horizontal(g8)
    c: Tangent(g7,g3)
    c: Distance(g4,g2) = 45
    c: Symmetric(g4,g2,g-2)
    c: Distance(g1,g6) = 90
    c: DistanceY(g-1,g1) = 15
    c: Tangent(g9,g12) = 1.5708
    c: Tangent(g9,g11) = -1.5708
    c: Tangent(g11,g10) = -1.5708
    c: Tangent(g12,g10) = 1.5708
    c: Vertical(g11)
    c: Equal(g9,g10)
    c: PointOnObject(g9,g-2)
    c: Distance(g-1,g9) = 16.7
    c: Distance(g9,g10) = 7.6
    c: Radius(g9) = 1.5
    c: Radius(g13) = 3.5
    c: Equal(g13,g14)
    c: Equal(g13,g16)
    c: Equal(g13,g15)
    c: Radius(g5) = 2
    c: Equal(g5,g7)
    c: Equal(g5,g6)
    c: DistanceY(g-1,g13) = -45
    c: Coincident(g17,g13)
    c: Coincident(g17,g14)
    c: Horizontal(g17)
    c: Coincident(g18,g13)
    c: Coincident(g18,g15)
    c: Coincident(g19,g15)
    c: Coincident(g19,g16)
    c: Horizontal(g19)
    c: Coincident(g20,g14)
    c: Coincident(g20,g16)
    c: Vertical(g18)
    c: Vertical(g20)
    c: Distance(g13,g15) = 20
    c: Distance(g13,g14) = 25
    c: Symmetric(g13,g14,g-2)
FEATURE [Part::Extrusion] Extrude198  label="Plaque_support_007"
  Base = -> Sketch157
  Dir = (0,6,0)
  Placement = pos=(-858,-46,0) rot=(0,0,1;0rad)
  Solid = true
FEATURE [Sketcher::SketchObject] Sketch158
  Placement = pos=(0,0,0) rot=(0.57735,0.57735,0.57735;2.0944rad)
  sketch-geometry (8):
    g0: LineSegment StartX=0 StartY=33 StartZ=0 EndX=-2 EndY=33 EndZ=0
    g1: LineSegment StartX=-2 StartY=33 StartZ=0 EndX=-2 EndY=-24 EndZ=0
    g2: ArcOfCircle CenterX=-4 CenterY=-24 CenterZ=0 NormalX=0 NormalY=0 NormalZ=1 Radius=2 StartAngle=4.71239 EndAngle=6.28319
    g3: LineSegment StartX=-4 StartY=-26 StartZ=0 EndX=-38 EndY=-26 EndZ=0
    g4: LineSegment StartX=-38 StartY=-26 StartZ=0 EndX=-38 EndY=-28 EndZ=0
    g5: LineSegment StartX=-38 StartY=-28 StartZ=0 EndX=-4 EndY=-28 EndZ=0
    g6: ArcOfCircle CenterX=-4 CenterY=-24 CenterZ=0 NormalX=0 NormalY=0 NormalZ=1 Radius=4 StartAngle=4.71239 EndAngle=6.28319
    g7: LineSegment StartX=0 StartY=-24 StartZ=0 EndX=0 EndY=33 EndZ=0
  constraints (22):
    c: PointOnObject(g0,g-2)
    c: Horizontal(g0)
    c: Coincident(g0,g1)
    c: Vertical(g1)
    c: Tangent(g1,g2) = 1.5708
    c: Tangent(g2,g3) = 1.5708
    c: Coincident(g3,g4)
    c: Vertical(g4)
    c: Coincident(g4,g5)
    c: Horizontal(g5)
    c: Tangent(g5,g6) = -1.5708
    c: PointOnObject(g6,g-2)
    c: Tangent(g6,g7) = -1.5708
    c: Coincident(g7,g0)
    c: Horizontal(g3)
    c: DistanceX(g0,g0) = 2
    c: Radius(g2) = 2
    c: Radius(g6) = 4
    c: DistanceY(g3,g4) = -2
    c: Distance(g-1,g0) = 33
    c: DistanceY(g-1,g5) = -28
    c: DistanceX(g6,g4) = -38
FEATURE [Part::Extrusion] Extrude199
  Base = -> Sketch158
  Dir = (-32.5,0,0)
  Solid = true
FEATURE [Part::Extrusion] Extrude200
  Base = -> Sketch158
  Dir = (32.5,0,0)
  Solid = true
FEATURE [Part::MultiFuse] Fusion044
  Shapes = -> [Extrude199,Extrude200]
FEATURE [Sketcher::SketchObject] Sketch159
  Placement = pos=(0,-2,0) rot=(1,0,0;1.5708rad)
  Support = -> Fusion044 [Face3]
  sketch-geometry (9):
    g0: ArcOfCircle CenterX=0 CenterY=0 CenterZ=0 NormalX=0 NormalY=0 NormalZ=1 Radius=32.5 StartAngle=0 EndAngle=3.14159
    g1: LineSegment StartX=-32.5 StartY=0 StartZ=0 EndX=-32.5 EndY=34 EndZ=0
    g2: LineSegment StartX=-32.5 StartY=34 StartZ=0 EndX=32.5 EndY=34 EndZ=0
    g3: LineSegment StartX=32.5 StartY=34 StartZ=0 EndX=32.5 EndY=0 EndZ=0
    g4: Circle CenterX=0 CenterY=0 CenterZ=0 NormalX=0 NormalY=0 NormalZ=1 Radius=11
    g5: Circle CenterX=-15.5 CenterY=15.5 CenterZ=0 NormalX=0 NormalY=0 NormalZ=1 Radius=2
    g6: Circle CenterX=15.5 CenterY=15.5 CenterZ=0 NormalX=0 NormalY=0 NormalZ=1 Radius=2
    g7: Circle CenterX=-15.5 CenterY=-15.5 CenterZ=0 NormalX=0 NormalY=0 NormalZ=1 Radius=2
    g8: Circle CenterX=15.5 CenterY=-15.5 CenterZ=0 NormalX=0 NormalY=0 NormalZ=1 Radius=2
  constraints (23):
    c: Coincident(g0,g-1)
    c: PointOnObject(g0,g-1)
    c: PointOnObject(g0,g-1)
    c: Coincident(g1,g0)
    c: Vertical(g1)
    c: Coincident(g1,g2)
    c: Horizontal(g2)
    c: Coincident(g2,g3)
    c: Coincident(g3,g0)
    c: Vertical(g3)
    c: DistanceY(g1,g0) = -34
    c: Coincident(g4,g-1)
    c: Radius(g4) = 11
    c: DistanceX(g1,g2) = 65
    c: Radius(g5) = 2
    c: Equal(g5,g6)
    c: Equal(g5,g8)
    c: Equal(g5,g7)
    c: Symmetric(g5,g6,g-2)
    c: Symmetric(g5,g7,g-1)
    c: Symmetric(g7,g8,g-2)
    c: DistanceX(g5,g6) = 31
    c: DistanceY(g5,g7) = -31
FEATURE [Part::Extrusion] Extrude201
  Base = -> Sketch159
  Dir = (0,2,0)
  Solid = true
FEATURE [Part::Cut] Cut077
  Base = -> Fusion044
  Tool = -> Extrude201
FEATURE [Sketcher::SketchObject] Sketch160
  ExternalGeometry = -> [Cut077]
  Placement = pos=(0,0,-26) rot=(0,0,1;0rad)
  Support = -> Cut077 [Face5]
  sketch-geometry (5):
    g0: Circle CenterX=-25 CenterY=-12 CenterZ=0 NormalX=0 NormalY=0 NormalZ=1 Radius=3.5
    g1: Circle CenterX=-25 CenterY=-30 CenterZ=0 NormalX=0 NormalY=0 NormalZ=1 Radius=3.5
    g2: Circle CenterX=25 CenterY=-12 CenterZ=0 NormalX=0 NormalY=0 NormalZ=1 Radius=3.5
    g3: Circle CenterX=25 CenterY=-30 CenterZ=0 NormalX=0 NormalY=0 NormalZ=1 Radius=3.5
    g4: LineSegment [constr] StartX=-25 StartY=-12 StartZ=0 EndX=-25 EndY=-30 EndZ=0
  constraints (12):
    c: Radius(g0) = 3.5
    c: Equal(g0,g2)
    c: Equal(g0,g3)
    c: Equal(g0,g1)
    c: Symmetric(g0,g2,g-2)
    c: Symmetric(g1,g3,g-2)
    c: Coincident(g4,g0)
    c: Coincident(g4,g1)
    c: Vertical(g4)
    c: DistanceY(g0,g1) = -18
    c: DistanceY(g-3,g1) = 8
    c: DistanceX(g0,g2) = 50
FEATURE [Part::Extrusion] Extrude202
  Base = -> Sketch160
  Dir = (0,0,-2)
  Solid = true
FEATURE [Part::Cut] Cut078
  Base = -> Cut077
  Tool = -> Extrude202
FEATURE [Part::Fillet] Fillet017  label="Plaque_moteur_007"
  Base = -> Cut078
  Edges = 2 edges r=4: [Edge5,Edge59]
  Placement = pos=(-858,0,0) rot=(0,0,1;0rad)
FEATURE [Sketcher::SketchObject] Sketch161
  Placement = pos=(0,0,0) rot=(1,0,0;1.5708rad)
  sketch-geometry (4):
    g0: LineSegment StartX=-3.15 StartY=5.95 StartZ=0 EndX=3.15 EndY=5.95 EndZ=0
    g1: LineSegment StartX=3.15 StartY=5.95 StartZ=0 EndX=3.15 EndY=-5.95 EndZ=0
    g2: LineSegment StartX=3.15 StartY=-5.95 StartZ=0 EndX=-3.15 EndY=-5.95 EndZ=0
    g3: LineSegment StartX=-3.15 StartY=-5.95 StartZ=0 EndX=-3.15 EndY=5.95 EndZ=0
  constraints (12):
    c: Coincident(g0,g1)
    c: Coincident(g1,g2)
    c: Coincident(g2,g3)
    c: Coincident(g3,g0)
    c: Horizontal(g0)
    c: Horizontal(g2)
    c: Vertical(g1)
    c: Vertical(g3)
    c: DistanceX(g0,g0) = 6.3
    c: DistanceY(g0,g2) = -11.9
    c: Symmetric(g0,g0,g-2)
    c: Symmetric(g0,g1,g-1)
FEATURE [Part::Extrusion] Extrude203
  Base = -> Sketch161
  Dir = (0,-10.8,0)
  Solid = true
FEATURE [Sketcher::SketchObject] Sketch162
  ExternalGeometry = -> [Extrude203]
  Placement = pos=(0,-10.8,0) rot=(1,0,0;1.5708rad)
  Support = -> Extrude203 [Face6]
  sketch-geometry (4):
    g0: LineSegment StartX=-3.15 StartY=1.55 StartZ=0 EndX=3.15 EndY=1.55 EndZ=0
    g1: LineSegment StartX=3.15 StartY=1.55 StartZ=0 EndX=3.15 EndY=-1.55 EndZ=0
    g2: LineSegment StartX=3.15 StartY=-1.55 StartZ=0 EndX=-3.15 EndY=-1.55 EndZ=0
    g3: LineSegment StartX=-3.15 StartY=-1.55 StartZ=0 EndX=-3.15 EndY=1.55 EndZ=0
  constraints (12):
    c: Coincident(g0,g1)
    c: Coincident(g1,g2)
    c: Coincident(g2,g3)
    c: Coincident(g3,g0)
    c: Horizontal(g0)
    c: Horizontal(g2)
    c: Vertical(g1)
    c: Vertical(g3)
    c: PointOnObject(g0,g-4)
    c: PointOnObject(g0,g-3)
    c: DistanceY(g0,g2) = -3.1
    c: Symmetric(g0,g1,g-1)
FEATURE [Part::Extrusion] Extrude204
  Base = -> Sketch162
  Dir = (0,7.7,0)
  Solid = true
FEATURE [Part::Cut] Cut079
  Base = -> Extrude203
  Tool = -> Extrude204
FEATURE [Part::Chamfer] Chamfer022
  Base = -> Cut079
  Edges = 4 edges r=0.5: [Edge7,Edge9,Edge15,Edge17]
FEATURE [Part::Chamfer] Chamfer023
  Base = -> Chamfer022
  Edges = 1 edges r=1.2: [Edge13]
FEATURE [Sketcher::SketchObject] Sketch163
  ExternalGeometry = -> [Chamfer023]
  Placement = pos=(0,0,5.95) rot=(0,0,1;0rad)
  Support = -> Chamfer023 [Face5]
  sketch-geometry (4):
    g0: LineSegment StartX=-3 StartY=0 StartZ=0 EndX=3 EndY=0 EndZ=0
    g1: LineSegment StartX=3 StartY=0 StartZ=0 EndX=3 EndY=-3.1 EndZ=0
    g2: LineSegment StartX=3 StartY=-3.1 StartZ=0 EndX=-3 EndY=-3.1 EndZ=0
    g3: LineSegment StartX=-3 StartY=-3.1 StartZ=0 EndX=-3 EndY=0 EndZ=0
  constraints (12):
    c: Coincident(g0,g1)
    c: Coincident(g1,g2)
    c: Coincident(g2,g3)
    c: Coincident(g3,g0)
    c: Horizontal(g0)
    c: Horizontal(g2)
    c: Vertical(g1)
    c: Vertical(g3)
    c: PointOnObject(g0,g-1)
    c: DistanceX(g-3,g0) = 0.15
    c: Symmetric(g0,g0,g-2)
    c: DistanceY(g0,g1) = -3.1
FEATURE [Part::Extrusion] Extrude205
  Base = -> Sketch163
  Dir = (0,0,6.3)
  Solid = true
FEATURE [Sketcher::SketchObject] Sketch164
  ExternalGeometry = -> [Extrude205]
  Placement = pos=(0,-3.1,0) rot=(1,0,0;1.5708rad)
  Support = -> Extrude205 [Face3]
  sketch-geometry (1):
    g0: Circle CenterX=0 CenterY=9.5 CenterZ=0 NormalX=0 NormalY=0 NormalZ=1 Radius=1.65
  constraints (3):
    c: PointOnObject(g0,g-2)
    c: Radius(g0) = 1.65
    c: DistanceY(g0,g-3) = -3.55
FEATURE [Part::Extrusion] Extrude206
  Base = -> Sketch164
  Dir = (0,6,0)
  Solid = true
FEATURE [Part::Cut] Cut080
  Base = -> Extrude205
  Tool = -> Extrude206
FEATURE [Part::Fillet] Fillet018
  Base = -> Cut080
  Edges = 2 edges r=1.35: [Edge8,Edge11]
FEATURE [Part::MultiFuse] Fusion045
  Shapes = -> [Chamfer023]
FEATURE [Sketcher::SketchObject] Sketch165
  Placement = pos=(0,0,0) rot=(0,0.707107,0.707107;3.14159rad)
  Support = -> Fusion045 [Face7]
  sketch-geometry (4):
    g0: Circle CenterX=-1.27 CenterY=3.8 CenterZ=0 NormalX=0 NormalY=0 NormalZ=1 Radius=0.2
    g1: Circle CenterX=1.27 CenterY=3.8 CenterZ=0 NormalX=0 NormalY=0 NormalZ=1 Radius=0.2
    g2: Circle CenterX=-1.27 CenterY=-3.8 CenterZ=0 NormalX=0 NormalY=0 NormalZ=1 Radius=0.2
    g3: Circle CenterX=1.27 CenterY=-3.8 CenterZ=0 NormalX=0 NormalY=0 NormalZ=1 Radius=0.2
  constraints (9):
    c: Radius(g0) = 0.2
    c: Equal(g0,g1)
    c: Equal(g0,g3)
    c: Equal(g0,g2)
    c: Symmetric(g0,g1,g-2)
    c: Symmetric(g2,g3,g-2)
    c: Symmetric(g0,g2,g-1)
    c: DistanceX(g0,g1) = 2.54
    c: DistanceY(g1,g3) = -7.6
FEATURE [Part::Extrusion] Extrude207
  Base = -> Sketch165
  Dir = (0,7.8,0)
  Solid = true
FEATURE [Part::MultiFuse] Fusion046  label="Capteur_optique_007"
  Placement = pos=(-858,-46,-20.7) rot=(0,0,1;0rad)
  Shapes = -> [Fusion045,Fillet018,Extrude207]
FEATURE [Sketcher::SketchObject] Sketch166
  Placement = pos=(0,0,0) rot=(1,0,0;1.5708rad)
  sketch-geometry (1):
    g0: Circle CenterX=0 CenterY=0 CenterZ=0 NormalX=0 NormalY=0 NormalZ=1 Radius=4
  constraints (2):
    c: Coincident(g0,g-1)
    c: Radius(g0) = 4
FEATURE [Part::Extrusion] Extrude208
  Base = -> Sketch166
  Dir = (0,50,0)
  Solid = true
FEATURE [Sketcher::SketchObject] Sketch167
  Placement = pos=(0,0,0) rot=(0.57735,0.57735,0.57735;2.0944rad)
  sketch-geometry (1):
    g0: Circle CenterX=6 CenterY=0 CenterZ=0 NormalX=0 NormalY=0 NormalZ=1 Radius=2
  constraints (3):
    c: DistanceX(g-1,g0) = 6
    c: Radius(g0) = 2
    c: PointOnObject(g0,g-1)
FEATURE [Part::Extrusion] Extrude209
  Base = -> Sketch167
  Dir = (4,0,0)
  Solid = true
FEATURE [Part::Extrusion] Extrude210
  Base = -> Sketch167
  Dir = (-4,0,0)
  Solid = true
FEATURE [Part::Cut] Cut081
  Base = -> Extrude208
  Tool = -> Extrude209
FEATURE [Part::Cut] Cut082  label="Axe_D8_007"
  Base = -> Cut081
  Placement = pos=(-858,-86,0) rot=(0,0,1;0rad)
  Tool = -> Extrude210
FEATURE [Sketcher::SketchObject] Sketch168
  Placement = pos=(0,0,0) rot=(1,0,0;1.5708rad)
  sketch-geometry (1):
    g0: Circle CenterX=0 CenterY=0 CenterZ=0 NormalX=0 NormalY=0 NormalZ=1 Radius=2
  constraints (2):
    c: Coincident(g0,g-1)
    c: Radius(g0) = 2
FEATURE [Part::Extrusion] Extrude211  label="Axe_D4_007"
  Base = -> Sketch168
  Dir = (0,103.6,0)
  Placement = pos=(-806.2,-80,0) rot=(0,0,1;1.5708rad)
  Solid = true
FEATURE [Sketcher::SketchObject] Sketch169
  Placement = pos=(0,0,0) rot=(1,0,0;1.5708rad)
  sketch-geometry (8):
    g0: LineSegment StartX=-50 StartY=0 StartZ=0 EndX=50 EndY=0 EndZ=0
    g1: LineSegment StartX=50 StartY=0 StartZ=0 EndX=50 EndY=-2 EndZ=0
    g2: LineSegment StartX=50 StartY=-2 StartZ=0 EndX=47 EndY=-2 EndZ=0
    g3: LineSegment StartX=47 StartY=-2 StartZ=0 EndX=44 EndY=-16 EndZ=0
    g4: LineSegment StartX=44 StartY=-16 StartZ=0 EndX=-44 EndY=-16 EndZ=0
    g5: LineSegment StartX=-44 StartY=-16 StartZ=0 EndX=-47 EndY=-2 EndZ=0
    g6: LineSegment StartX=-47 StartY=-2 StartZ=0 EndX=-50 EndY=-2 EndZ=0
    g7: LineSegment StartX=-50 StartY=-2 StartZ=0 EndX=-50 EndY=0 EndZ=0
  constraints (24):
    c: PointOnObject(g0,g-1)
    c: Horizontal(g0)
    c: Coincident(g0,g1)
    c: Vertical(g1)
    c: Coincident(g1,g2)
    c: Horizontal(g2)
    c: Coincident(g2,g3)
    c: Coincident(g3,g4)
    c: Horizontal(g4)
    c: Coincident(g4,g5)
    c: Coincident(g5,g6)
    c: Horizontal(g6)
    c: Coincident(g6,g7)
    c: Coincident(g7,g0)
    c: Vertical(g7)
    c: DistanceY(g0,g6) = -2
    c: DistanceX(g6,g5) = 3
    c: DistanceX(g0,g0) = 100
    c: Symmetric(g0,g0,g-2)
    c: Symmetric(g6,g1,g-2)
    c: Symmetric(g5,g2,g-2)
    c: Symmetric(g4,g3,g-2)
    c: DistanceX(g4,g3) = 88
    c: DistanceY(g0,g4) = -16
FEATURE [Part::Extrusion] Extrude212  label="Plaque_alveolaire_007"
  Base = -> Sketch169
  Dir = (0,2000,0)
  Placement = pos=(-858,-62,22) rot=(0,0,1;3.14159rad)
  Solid = true
FEATURE [App::DocumentObjectGroup] Groupe009  label="Assemblage_miroir X=-858_001"
  Group = -> [Cut076,Fusion043,Extrude197,Part__Feature009,Extrude198,Fillet017,Fusion046,Cut082,Extrude211,Extrude212]
FEATURE [Sketcher::SketchObject] Sketch170
  Placement = pos=(0,0,0) rot=(1,0,0;1.5708rad)
  sketch-geometry (8):
    g0: LineSegment StartX=-21.15 StartY=16.15 StartZ=0 EndX=-16.15 EndY=21.15 EndZ=0
    g1: LineSegment StartX=-16.15 StartY=21.15 StartZ=0 EndX=16.15 EndY=21.15 EndZ=0
    g2: LineSegment StartX=16.15 StartY=21.15 StartZ=0 EndX=21.15 EndY=16.15 EndZ=0
    g3: LineSegment StartX=21.15 StartY=16.15 StartZ=0 EndX=21.15 EndY=-16.15 EndZ=0
    g4: LineSegment StartX=21.15 StartY=-16.15 StartZ=0 EndX=16.15 EndY=-21.15 EndZ=0
    g5: LineSegment StartX=16.15 StartY=-21.15 StartZ=0 EndX=-16.15 EndY=-21.15 EndZ=0
    g6: LineSegment StartX=-16.15 StartY=-21.15 StartZ=0 EndX=-21.15 EndY=-16.15 EndZ=0
    g7: LineSegment StartX=-21.15 StartY=-16.15 StartZ=0 EndX=-21.15 EndY=16.15 EndZ=0
  constraints (21):
    c: Coincident(g0,g1)
    c: Horizontal(g1)
    c: Coincident(g1,g2)
    c: Coincident(g2,g3)
    c: Vertical(g3)
    c: Coincident(g3,g4)
    c: Coincident(g4,g5)
    c: Horizontal(g5)
    c: Coincident(g5,g6)
    c: Coincident(g6,g7)
    c: Coincident(g7,g0)
    c: Angle(g7,g0) = 2.35619
    c: Distance(g0,g7) = 5
    c: Distance(g2,g7) = 42.3
    c: Distance(g5,g1) = 42.3
    c: Symmetric(g6,g3,g-2)
    c: Symmetric(g5,g4,g-2)
    c: Symmetric(g0,g2,g-2)
    c: Symmetric(g0,g1,g-2)
    c: Symmetric(g0,g6,g-1)
    c: Symmetric(g0,g5,g-1)
FEATURE [Part::Extrusion] Extrude213
  Base = -> Sketch170
  Dir = (0,48,0)
  Solid = true
FEATURE [Sketcher::SketchObject] Sketch171
  Placement = pos=(0,0,0) rot=(1,0,0;1.5708rad)
  Support = -> Extrude213 [Face9]
  sketch-geometry (1):
    g0: Circle CenterX=0 CenterY=0 CenterZ=0 NormalX=0 NormalY=0 NormalZ=1 Radius=11
  constraints (2):
    c: Coincident(g0,g-1)
    c: Radius(g0) = 11
FEATURE [Part::Extrusion] Extrude214
  Base = -> Sketch171
  Dir = (0,-2,0)
  Solid = true
FEATURE [Sketcher::SketchObject] Sketch172
  Placement = pos=(0,-2,0) rot=(1,0,0;1.5708rad)
  Support = -> Extrude214 [Face3]
  sketch-geometry (1):
    g0: Circle CenterX=0 CenterY=0 CenterZ=0 NormalX=0 NormalY=0 NormalZ=1 Radius=2.5
  constraints (2):
    c: Coincident(g0,g-1)
    c: Radius(g0) = 2.5
FEATURE [Part::Extrusion] Extrude215
  Base = -> Sketch172
  Dir = (0,-22,0)
  Solid = true
FEATURE [Part::Chamfer] Chamfer024
  Base = -> Extrude215
  Edges = 1 edges r=0.8: [Edge3]
FEATURE [Sketcher::SketchObject] Sketch173
  Placement = pos=(0,0,0) rot=(1,0,0;1.5708rad)
  Support = -> Extrude213 [Face9]
  sketch-geometry (4):
    g0: Circle CenterX=-15.5 CenterY=15.5 CenterZ=0 NormalX=0 NormalY=0 NormalZ=1 Radius=2
    g1: Circle CenterX=15.5 CenterY=15.5 CenterZ=0 NormalX=0 NormalY=0 NormalZ=1 Radius=2
    g2: Circle CenterX=-15.5 CenterY=-15.5 CenterZ=0 NormalX=0 NormalY=0 NormalZ=1 Radius=2
    g3: Circle CenterX=15.5 CenterY=-15.5 CenterZ=0 NormalX=0 NormalY=0 NormalZ=1 Radius=2
  constraints (9):
    c: Distance(g0,g1) = 31
    c: Distance(g0,g2) = 31
    c: Symmetric(g0,g2,g-1)
    c: Symmetric(g0,g1,g-2)
    c: Symmetric(g2,g3,g-2)
    c: Radius(g0) = 2
    c: Equal(g0,g1)
    c: Equal(g0,g2)
    c: Equal(g0,g3)
FEATURE [Part::Extrusion] Extrude216
  Base = -> Sketch173
  Dir = (0,4.5,0)
  Solid = true
FEATURE [Part::Cut] Cut083
  Base = -> Extrude213
  Tool = -> Extrude216
FEATURE [Sketcher::SketchObject] Sketch174
  Placement = pos=(0,0,0) rot=(1,0,0;1.5708rad)
  sketch-geometry (1):
    g0: Circle CenterX=0 CenterY=0 CenterZ=0 NormalX=0 NormalY=0 NormalZ=1 Radius=9
  constraints (2):
    c: Coincident(g0,g-1)
    c: Radius(g0) = 9
FEATURE [Part::Extrusion] Extrude217
  Base = -> Sketch174
  Dir = (0,25,0)
  Solid = true
FEATURE [Sketcher::SketchObject] Sketch175
  Placement = pos=(0,0,0) rot=(1,0,0;1.5708rad)
  sketch-geometry (1):
    g0: Circle CenterX=0 CenterY=0 CenterZ=0 NormalX=0 NormalY=0 NormalZ=1 Radius=2.5
  constraints (2):
    c: Coincident(g0,g-1)
    c: Radius(g0) = 2.5
FEATURE [Part::Extrusion] Extrude218
  Base = -> Sketch175
  Dir = (0,10,0)
  Solid = true
FEATURE [Part::Cut] Cut084
  Base = -> Extrude217
  Tool = -> Extrude218
FEATURE [Sketcher::SketchObject] Sketch176
  Placement = pos=(0,25,0) rot=(0,0.707107,0.707107;3.14159rad)
  Support = -> Cut084 [Face3]
  sketch-geometry (1):
    g0: Circle CenterX=0 CenterY=0 CenterZ=0 NormalX=0 NormalY=0 NormalZ=1 Radius=4
  constraints (2):
    c: Coincident(g0,g-1)
    c: Radius(g0) = 4
FEATURE [Part::Extrusion] Extrude219
  Base = -> Sketch176
  Dir = (0,-10,0)
  Solid = true
FEATURE [Part::Cut] Cut085  label="Accouplement_008"
  Base = -> Cut084
  Placement = pos=(-1001,-12,0) rot=(1,0,0;3.14159rad)
  Tool = -> Extrude219
FEATURE [Part::Fuse] Fusion047
  Base = -> Extrude214
  Tool = -> Cut083
FEATURE [Part::Fuse] Fusion048  label="Moteur_008"
  Base = -> Chamfer024
  Placement = pos=(-1001,0,0) rot=(0,0,1;0rad)
  Tool = -> Fusion047
FEATURE [Sketcher::SketchObject] Sketch177
  Placement = pos=(0,0,0) rot=(1,0,0;1.5708rad)
  sketch-geometry (4):
    g0: LineSegment StartX=-50 StartY=0 StartZ=0 EndX=-47 EndY=0 EndZ=0
    g1: LineSegment StartX=47 StartY=0 StartZ=0 EndX=50 EndY=0 EndZ=0
    g2: ArcOfCircle CenterX=0 CenterY=0 CenterZ=0 NormalX=0 NormalY=0 NormalZ=1 Radius=47 StartAngle=3.14159 EndAngle=6.28319
    g3: ArcOfCircle CenterX=0 CenterY=0 CenterZ=0 NormalX=0 NormalY=0 NormalZ=1 Radius=50 StartAngle=3.14159 EndAngle=6.28319
  constraints (13):
    c: Horizontal(g0)
    c: PointOnObject(g1,g-1)
    c: Horizontal(g1)
    c: Coincident(g2,g-1)
    c: PointOnObject(g2,g-1)
    c: Coincident(g3,g-1)
    c: Coincident(g3,g1)
    c: PointOnObject(g3,g-1)
    c: Coincident(g0,g3)
    c: Coincident(g0,g2)
    c: Distance(g0,g1) = 100
    c: Distance(g0,g0) = 3
    c: Coincident(g1,g2)
FEATURE [Part::Extrusion] Extrude220  label="Demi_tube_sous_miroir_008"
  Base = -> Sketch177
  Dir = (0,2000,0)
  Placement = pos=(-1001,-62,20) rot=(0,0,1;3.14159rad)
  Solid = true
FEATURE [Part::Feature] Part__Feature010  label="Coussinet_autolub_C2-151-8-128_008"
  Placement = pos=(-1001,-46,0) rot=(0,0,1;1.5708rad)
  shape: bbox 16 x 8 x 16 mm, 12 faces (baked)
FEATURE [Sketcher::SketchObject] Sketch178
  Placement = pos=(0,0,0) rot=(1,0,0;1.5708rad)
  sketch-geometry (21):
    g0: Circle CenterX=0 CenterY=0 CenterZ=0 NormalX=0 NormalY=0 NormalZ=1 Radius=6
    g1: LineSegment StartX=-20.5 StartY=15 StartZ=0 EndX=20.5 EndY=15 EndZ=0
    g2: ArcOfCircle CenterX=20.5 CenterY=13 CenterZ=0 NormalX=0 NormalY=0 NormalZ=1 Radius=2 StartAngle=6.28319 EndAngle=7.85398
    g3: LineSegment StartX=22.5 StartY=13 StartZ=0 EndX=22.5 EndY=-73 EndZ=0
    g4: LineSegment StartX=-22.5 StartY=13 StartZ=0 EndX=-22.5 EndY=-73 EndZ=0
    g5: ArcOfCircle CenterX=-20.5 CenterY=13 CenterZ=0 NormalX=0 NormalY=0 NormalZ=1 Radius=2 StartAngle=1.5708 EndAngle=3.14159
    g6: ArcOfCircle CenterX=-20.5 CenterY=-73 CenterZ=0 NormalX=0 NormalY=0 NormalZ=1 Radius=2 StartAngle=3.14159 EndAngle=4.71239
    g7: ArcOfCircle CenterX=20.5 CenterY=-73 CenterZ=0 NormalX=0 NormalY=0 NormalZ=1 Radius=2 StartAngle=4.71239 EndAngle=6.28319
    g8: LineSegment StartX=-20.5 StartY=-75 StartZ=0 EndX=20.5 EndY=-75 EndZ=0
    g9: ArcOfCircle CenterX=0 CenterY=-16.7 CenterZ=0 NormalX=0 NormalY=0 NormalZ=1 Radius=1.5 StartAngle=0 EndAngle=3.14159
    g10: ArcOfCircle CenterX=0 CenterY=-24.3 CenterZ=0 NormalX=0 NormalY=0 NormalZ=1 Radius=1.5 StartAngle=3.14159 EndAngle=6.28319
    g11: LineSegment StartX=-1.5 StartY=-16.7 StartZ=0 EndX=-1.5 EndY=-24.3 EndZ=0
    g12: LineSegment StartX=1.5 StartY=-16.7 StartZ=0 EndX=1.5 EndY=-24.3 EndZ=0
    g13: Circle CenterX=-12.5 CenterY=-45 CenterZ=0 NormalX=0 NormalY=0 NormalZ=1 Radius=3.5
    g14: Circle CenterX=12.5 CenterY=-45 CenterZ=0 NormalX=0 NormalY=0 NormalZ=1 Radius=3.5
    g15: Circle CenterX=-12.5 CenterY=-65 CenterZ=0 NormalX=0 NormalY=0 NormalZ=1 Radius=3.5
    g16: Circle CenterX=12.5 CenterY=-65 CenterZ=0 NormalX=0 NormalY=0 NormalZ=1 Radius=3.5
    g17: LineSegment [constr] StartX=-12.5 StartY=-45 StartZ=0 EndX=12.5 EndY=-45 EndZ=0
    g18: LineSegment [constr] StartX=-12.5 StartY=-45 StartZ=0 EndX=-12.5 EndY=-65 EndZ=0
    g19: LineSegment [constr] StartX=-12.5 StartY=-65 StartZ=0 EndX=12.5 EndY=-65 EndZ=0
    g20: LineSegment [constr] StartX=12.5 StartY=-45 StartZ=0 EndX=12.5 EndY=-65 EndZ=0
  constraints (59):
    c: Coincident(g0,g-1)
    c: Radius(g0) = 6
    c: Horizontal(g1)
    c: Coincident(g2,g1)
    c: Coincident(g3,g2)
    c: Vertical(g3)
    c: Vertical(g4)
    c: Coincident(g5,g1)
    c: Coincident(g5,g4)
    c: Coincident(g7,g3)
    c: Coincident(g8,g6)
    c: Coincident(g8,g7)
    c: Tangent(g8,g7)
    c: Tangent(g5,g4)
    c: Tangent(g5,g1)
    c: Tangent(g1,g2)
    c: Tangent(g2,g3)
    c: Coincident(g4,g6)
    c: Tangent(g6,g4)
    c: Tangent(g6,g8)
    c: Horizontal(g8)
    c: Tangent(g7,g3)
    c: Distance(g4,g2) = 45
    c: Symmetric(g4,g2,g-2)
    c: Distance(g1,g6) = 90
    c: DistanceY(g-1,g1) = 15
    c: Tangent(g9,g12) = 1.5708
    c: Tangent(g9,g11) = -1.5708
    c: Tangent(g11,g10) = -1.5708
    c: Tangent(g12,g10) = 1.5708
    c: Vertical(g11)
    c: Equal(g9,g10)
    c: PointOnObject(g9,g-2)
    c: Distance(g-1,g9) = 16.7
    c: Distance(g9,g10) = 7.6
    c: Radius(g9) = 1.5
    c: Radius(g13) = 3.5
    c: Equal(g13,g14)
    c: Equal(g13,g16)
    c: Equal(g13,g15)
    c: Radius(g5) = 2
    c: Equal(g5,g7)
    c: Equal(g5,g6)
    c: DistanceY(g-1,g13) = -45
    c: Coincident(g17,g13)
    c: Coincident(g17,g14)
    c: Horizontal(g17)
    c: Coincident(g18,g13)
    c: Coincident(g18,g15)
    c: Coincident(g19,g15)
    c: Coincident(g19,g16)
    c: Horizontal(g19)
    c: Coincident(g20,g14)
    c: Coincident(g20,g16)
    c: Vertical(g18)
    c: Vertical(g20)
    c: Distance(g13,g15) = 20
    c: Distance(g13,g14) = 25
    c: Symmetric(g13,g14,g-2)
FEATURE [Part::Extrusion] Extrude221  label="Plaque_support_008"
  Base = -> Sketch178
  Dir = (0,6,0)
  Placement = pos=(-1001,-46,0) rot=(0,0,1;0rad)
  Solid = true
FEATURE [Sketcher::SketchObject] Sketch179
  Placement = pos=(0,0,0) rot=(0.57735,0.57735,0.57735;2.0944rad)
  sketch-geometry (8):
    g0: LineSegment StartX=0 StartY=33 StartZ=0 EndX=-2 EndY=33 EndZ=0
    g1: LineSegment StartX=-2 StartY=33 StartZ=0 EndX=-2 EndY=-24 EndZ=0
    g2: ArcOfCircle CenterX=-4 CenterY=-24 CenterZ=0 NormalX=0 NormalY=0 NormalZ=1 Radius=2 StartAngle=4.71239 EndAngle=6.28319
    g3: LineSegment StartX=-4 StartY=-26 StartZ=0 EndX=-38 EndY=-26 EndZ=0
    g4: LineSegment StartX=-38 StartY=-26 StartZ=0 EndX=-38 EndY=-28 EndZ=0
    g5: LineSegment StartX=-38 StartY=-28 StartZ=0 EndX=-4 EndY=-28 EndZ=0
    g6: ArcOfCircle CenterX=-4 CenterY=-24 CenterZ=0 NormalX=0 NormalY=0 NormalZ=1 Radius=4 StartAngle=4.71239 EndAngle=6.28319
    g7: LineSegment StartX=0 StartY=-24 StartZ=0 EndX=0 EndY=33 EndZ=0
  constraints (22):
    c: PointOnObject(g0,g-2)
    c: Horizontal(g0)
    c: Coincident(g0,g1)
    c: Vertical(g1)
    c: Tangent(g1,g2) = 1.5708
    c: Tangent(g2,g3) = 1.5708
    c: Coincident(g3,g4)
    c: Vertical(g4)
    c: Coincident(g4,g5)
    c: Horizontal(g5)
    c: Tangent(g5,g6) = -1.5708
    c: PointOnObject(g6,g-2)
    c: Tangent(g6,g7) = -1.5708
    c: Coincident(g7,g0)
    c: Horizontal(g3)
    c: DistanceX(g0,g0) = 2
    c: Radius(g2) = 2
    c: Radius(g6) = 4
    c: DistanceY(g3,g4) = -2
    c: Distance(g-1,g0) = 33
    c: DistanceY(g-1,g5) = -28
    c: DistanceX(g6,g4) = -38
FEATURE [Part::Extrusion] Extrude222
  Base = -> Sketch179
  Dir = (-32.5,0,0)
  Solid = true
FEATURE [Part::Extrusion] Extrude223
  Base = -> Sketch179
  Dir = (32.5,0,0)
  Solid = true
FEATURE [Part::MultiFuse] Fusion049
  Shapes = -> [Extrude222,Extrude223]
FEATURE [Sketcher::SketchObject] Sketch180
  Placement = pos=(0,-2,0) rot=(1,0,0;1.5708rad)
  Support = -> Fusion049 [Face3]
  sketch-geometry (9):
    g0: ArcOfCircle CenterX=0 CenterY=0 CenterZ=0 NormalX=0 NormalY=0 NormalZ=1 Radius=32.5 StartAngle=0 EndAngle=3.14159
    g1: LineSegment StartX=-32.5 StartY=0 StartZ=0 EndX=-32.5 EndY=34 EndZ=0
    g2: LineSegment StartX=-32.5 StartY=34 StartZ=0 EndX=32.5 EndY=34 EndZ=0
    g3: LineSegment StartX=32.5 StartY=34 StartZ=0 EndX=32.5 EndY=0 EndZ=0
    g4: Circle CenterX=0 CenterY=0 CenterZ=0 NormalX=0 NormalY=0 NormalZ=1 Radius=11
    g5: Circle CenterX=-15.5 CenterY=15.5 CenterZ=0 NormalX=0 NormalY=0 NormalZ=1 Radius=2
    g6: Circle CenterX=15.5 CenterY=15.5 CenterZ=0 NormalX=0 NormalY=0 NormalZ=1 Radius=2
    g7: Circle CenterX=-15.5 CenterY=-15.5 CenterZ=0 NormalX=0 NormalY=0 NormalZ=1 Radius=2
    g8: Circle CenterX=15.5 CenterY=-15.5 CenterZ=0 NormalX=0 NormalY=0 NormalZ=1 Radius=2
  constraints (23):
    c: Coincident(g0,g-1)
    c: PointOnObject(g0,g-1)
    c: PointOnObject(g0,g-1)
    c: Coincident(g1,g0)
    c: Vertical(g1)
    c: Coincident(g1,g2)
    c: Horizontal(g2)
    c: Coincident(g2,g3)
    c: Coincident(g3,g0)
    c: Vertical(g3)
    c: DistanceY(g1,g0) = -34
    c: Coincident(g4,g-1)
    c: Radius(g4) = 11
    c: DistanceX(g1,g2) = 65
    c: Radius(g5) = 2
    c: Equal(g5,g6)
    c: Equal(g5,g8)
    c: Equal(g5,g7)
    c: Symmetric(g5,g6,g-2)
    c: Symmetric(g5,g7,g-1)
    c: Symmetric(g7,g8,g-2)
    c: DistanceX(g5,g6) = 31
    c: DistanceY(g5,g7) = -31
FEATURE [Part::Extrusion] Extrude224
  Base = -> Sketch180
  Dir = (0,2,0)
  Solid = true
FEATURE [Part::Cut] Cut086
  Base = -> Fusion049
  Tool = -> Extrude224
FEATURE [Sketcher::SketchObject] Sketch181
  ExternalGeometry = -> [Cut086]
  Placement = pos=(0,0,-26) rot=(0,0,1;0rad)
  Support = -> Cut086 [Face5]
  sketch-geometry (5):
    g0: Circle CenterX=-25 CenterY=-12 CenterZ=0 NormalX=0 NormalY=0 NormalZ=1 Radius=3.5
    g1: Circle CenterX=-25 CenterY=-30 CenterZ=0 NormalX=0 NormalY=0 NormalZ=1 Radius=3.5
    g2: Circle CenterX=25 CenterY=-12 CenterZ=0 NormalX=0 NormalY=0 NormalZ=1 Radius=3.5
    g3: Circle CenterX=25 CenterY=-30 CenterZ=0 NormalX=0 NormalY=0 NormalZ=1 Radius=3.5
    g4: LineSegment [constr] StartX=-25 StartY=-12 StartZ=0 EndX=-25 EndY=-30 EndZ=0
  constraints (12):
    c: Radius(g0) = 3.5
    c: Equal(g0,g2)
    c: Equal(g0,g3)
    c: Equal(g0,g1)
    c: Symmetric(g0,g2,g-2)
    c: Symmetric(g1,g3,g-2)
    c: Coincident(g4,g0)
    c: Coincident(g4,g1)
    c: Vertical(g4)
    c: DistanceY(g0,g1) = -18
    c: DistanceY(g-3,g1) = 8
    c: DistanceX(g0,g2) = 50
FEATURE [Part::Extrusion] Extrude225
  Base = -> Sketch181
  Dir = (0,0,-2)
  Solid = true
FEATURE [Part::Cut] Cut087
  Base = -> Cut086
  Tool = -> Extrude225
FEATURE [Part::Fillet] Fillet019  label="Plaque_moteur_008"
  Base = -> Cut087
  Edges = 2 edges r=4: [Edge5,Edge59]
  Placement = pos=(-1001,0,0) rot=(0,0,1;0rad)
FEATURE [Sketcher::SketchObject] Sketch182
  Placement = pos=(0,0,0) rot=(1,0,0;1.5708rad)
  sketch-geometry (4):
    g0: LineSegment StartX=-3.15 StartY=5.95 StartZ=0 EndX=3.15 EndY=5.95 EndZ=0
    g1: LineSegment StartX=3.15 StartY=5.95 StartZ=0 EndX=3.15 EndY=-5.95 EndZ=0
    g2: LineSegment StartX=3.15 StartY=-5.95 StartZ=0 EndX=-3.15 EndY=-5.95 EndZ=0
    g3: LineSegment StartX=-3.15 StartY=-5.95 StartZ=0 EndX=-3.15 EndY=5.95 EndZ=0
  constraints (12):
    c: Coincident(g0,g1)
    c: Coincident(g1,g2)
    c: Coincident(g2,g3)
    c: Coincident(g3,g0)
    c: Horizontal(g0)
    c: Horizontal(g2)
    c: Vertical(g1)
    c: Vertical(g3)
    c: DistanceX(g0,g0) = 6.3
    c: DistanceY(g0,g2) = -11.9
    c: Symmetric(g0,g0,g-2)
    c: Symmetric(g0,g1,g-1)
FEATURE [Part::Extrusion] Extrude226
  Base = -> Sketch182
  Dir = (0,-10.8,0)
  Solid = true
FEATURE [Sketcher::SketchObject] Sketch183
  ExternalGeometry = -> [Extrude226]
  Placement = pos=(0,-10.8,0) rot=(1,0,0;1.5708rad)
  Support = -> Extrude226 [Face6]
  sketch-geometry (4):
    g0: LineSegment StartX=-3.15 StartY=1.55 StartZ=0 EndX=3.15 EndY=1.55 EndZ=0
    g1: LineSegment StartX=3.15 StartY=1.55 StartZ=0 EndX=3.15 EndY=-1.55 EndZ=0
    g2: LineSegment StartX=3.15 StartY=-1.55 StartZ=0 EndX=-3.15 EndY=-1.55 EndZ=0
    g3: LineSegment StartX=-3.15 StartY=-1.55 StartZ=0 EndX=-3.15 EndY=1.55 EndZ=0
  constraints (12):
    c: Coincident(g0,g1)
    c: Coincident(g1,g2)
    c: Coincident(g2,g3)
    c: Coincident(g3,g0)
    c: Horizontal(g0)
    c: Horizontal(g2)
    c: Vertical(g1)
    c: Vertical(g3)
    c: PointOnObject(g0,g-4)
    c: PointOnObject(g0,g-3)
    c: DistanceY(g0,g2) = -3.1
    c: Symmetric(g0,g1,g-1)
FEATURE [Part::Extrusion] Extrude227
  Base = -> Sketch183
  Dir = (0,7.7,0)
  Solid = true
FEATURE [Part::Cut] Cut088
  Base = -> Extrude226
  Tool = -> Extrude227
FEATURE [Part::Chamfer] Chamfer025
  Base = -> Cut088
  Edges = 4 edges r=0.5: [Edge7,Edge9,Edge15,Edge17]
FEATURE [Part::Chamfer] Chamfer026
  Base = -> Chamfer025
  Edges = 1 edges r=1.2: [Edge13]
FEATURE [Sketcher::SketchObject] Sketch184
  ExternalGeometry = -> [Chamfer026]
  Placement = pos=(0,0,5.95) rot=(0,0,1;0rad)
  Support = -> Chamfer026 [Face5]
  sketch-geometry (4):
    g0: LineSegment StartX=-3 StartY=0 StartZ=0 EndX=3 EndY=0 EndZ=0
    g1: LineSegment StartX=3 StartY=0 StartZ=0 EndX=3 EndY=-3.1 EndZ=0
    g2: LineSegment StartX=3 StartY=-3.1 StartZ=0 EndX=-3 EndY=-3.1 EndZ=0
    g3: LineSegment StartX=-3 StartY=-3.1 StartZ=0 EndX=-3 EndY=0 EndZ=0
  constraints (12):
    c: Coincident(g0,g1)
    c: Coincident(g1,g2)
    c: Coincident(g2,g3)
    c: Coincident(g3,g0)
    c: Horizontal(g0)
    c: Horizontal(g2)
    c: Vertical(g1)
    c: Vertical(g3)
    c: PointOnObject(g0,g-1)
    c: DistanceX(g-3,g0) = 0.15
    c: Symmetric(g0,g0,g-2)
    c: DistanceY(g0,g1) = -3.1
FEATURE [Part::Extrusion] Extrude228
  Base = -> Sketch184
  Dir = (0,0,6.3)
  Solid = true
FEATURE [Sketcher::SketchObject] Sketch185
  ExternalGeometry = -> [Extrude228]
  Placement = pos=(0,-3.1,0) rot=(1,0,0;1.5708rad)
  Support = -> Extrude228 [Face3]
  sketch-geometry (1):
    g0: Circle CenterX=0 CenterY=9.5 CenterZ=0 NormalX=0 NormalY=0 NormalZ=1 Radius=1.65
  constraints (3):
    c: PointOnObject(g0,g-2)
    c: Radius(g0) = 1.65
    c: DistanceY(g0,g-3) = -3.55
FEATURE [Part::Extrusion] Extrude229
  Base = -> Sketch185
  Dir = (0,6,0)
  Solid = true
FEATURE [Part::Cut] Cut089
  Base = -> Extrude228
  Tool = -> Extrude229
FEATURE [Part::Fillet] Fillet020
  Base = -> Cut089
  Edges = 2 edges r=1.35: [Edge8,Edge11]
FEATURE [Part::MultiFuse] Fusion050
  Shapes = -> [Chamfer026]
FEATURE [Sketcher::SketchObject] Sketch186
  Placement = pos=(0,0,0) rot=(0,0.707107,0.707107;3.14159rad)
  Support = -> Fusion050 [Face7]
  sketch-geometry (4):
    g0: Circle CenterX=-1.27 CenterY=3.8 CenterZ=0 NormalX=0 NormalY=0 NormalZ=1 Radius=0.2
    g1: Circle CenterX=1.27 CenterY=3.8 CenterZ=0 NormalX=0 NormalY=0 NormalZ=1 Radius=0.2
    g2: Circle CenterX=-1.27 CenterY=-3.8 CenterZ=0 NormalX=0 NormalY=0 NormalZ=1 Radius=0.2
    g3: Circle CenterX=1.27 CenterY=-3.8 CenterZ=0 NormalX=0 NormalY=0 NormalZ=1 Radius=0.2
  constraints (9):
    c: Radius(g0) = 0.2
    c: Equal(g0,g1)
    c: Equal(g0,g3)
    c: Equal(g0,g2)
    c: Symmetric(g0,g1,g-2)
    c: Symmetric(g2,g3,g-2)
    c: Symmetric(g0,g2,g-1)
    c: DistanceX(g0,g1) = 2.54
    c: DistanceY(g1,g3) = -7.6
FEATURE [Part::Extrusion] Extrude230
  Base = -> Sketch186
  Dir = (0,7.8,0)
  Solid = true
FEATURE [Part::MultiFuse] Fusion051  label="Capteur_optique_008"
  Placement = pos=(-1001,-46,-20.7) rot=(0,0,1;0rad)
  Shapes = -> [Fusion050,Fillet020,Extrude230]
FEATURE [Sketcher::SketchObject] Sketch187
  Placement = pos=(0,0,0) rot=(1,0,0;1.5708rad)
  sketch-geometry (1):
    g0: Circle CenterX=0 CenterY=0 CenterZ=0 NormalX=0 NormalY=0 NormalZ=1 Radius=4
  constraints (2):
    c: Coincident(g0,g-1)
    c: Radius(g0) = 4
FEATURE [Part::Extrusion] Extrude231
  Base = -> Sketch187
  Dir = (0,50,0)
  Solid = true
FEATURE [Sketcher::SketchObject] Sketch188
  Placement = pos=(0,0,0) rot=(0.57735,0.57735,0.57735;2.0944rad)
  sketch-geometry (1):
    g0: Circle CenterX=6 CenterY=0 CenterZ=0 NormalX=0 NormalY=0 NormalZ=1 Radius=2
  constraints (3):
    c: DistanceX(g-1,g0) = 6
    c: Radius(g0) = 2
    c: PointOnObject(g0,g-1)
FEATURE [Part::Extrusion] Extrude232
  Base = -> Sketch188
  Dir = (4,0,0)
  Solid = true
FEATURE [Part::Extrusion] Extrude233
  Base = -> Sketch188
  Dir = (-4,0,0)
  Solid = true
FEATURE [Part::Cut] Cut090
  Base = -> Extrude231
  Tool = -> Extrude232
FEATURE [Part::Cut] Cut091  label="Axe_D8_008"
  Base = -> Cut090
  Placement = pos=(-1001,-86,0) rot=(0,0,1;0rad)
  Tool = -> Extrude233
FEATURE [Sketcher::SketchObject] Sketch189
  Placement = pos=(0,0,0) rot=(1,0,0;1.5708rad)
  sketch-geometry (1):
    g0: Circle CenterX=0 CenterY=0 CenterZ=0 NormalX=0 NormalY=0 NormalZ=1 Radius=2
  constraints (2):
    c: Coincident(g0,g-1)
    c: Radius(g0) = 2
FEATURE [Part::Extrusion] Extrude234  label="Axe_D4_008"
  Base = -> Sketch189
  Dir = (0,103.6,0)
  Placement = pos=(-949.2,-80,0) rot=(0,0,1;1.5708rad)
  Solid = true
FEATURE [Sketcher::SketchObject] Sketch190
  Placement = pos=(0,0,0) rot=(1,0,0;1.5708rad)
  sketch-geometry (8):
    g0: LineSegment StartX=-50 StartY=0 StartZ=0 EndX=50 EndY=0 EndZ=0
    g1: LineSegment StartX=50 StartY=0 StartZ=0 EndX=50 EndY=-2 EndZ=0
    g2: LineSegment StartX=50 StartY=-2 StartZ=0 EndX=47 EndY=-2 EndZ=0
    g3: LineSegment StartX=47 StartY=-2 StartZ=0 EndX=44 EndY=-16 EndZ=0
    g4: LineSegment StartX=44 StartY=-16 StartZ=0 EndX=-44 EndY=-16 EndZ=0
    g5: LineSegment StartX=-44 StartY=-16 StartZ=0 EndX=-47 EndY=-2 EndZ=0
    g6: LineSegment StartX=-47 StartY=-2 StartZ=0 EndX=-50 EndY=-2 EndZ=0
    g7: LineSegment StartX=-50 StartY=-2 StartZ=0 EndX=-50 EndY=0 EndZ=0
  constraints (24):
    c: PointOnObject(g0,g-1)
    c: Horizontal(g0)
    c: Coincident(g0,g1)
    c: Vertical(g1)
    c: Coincident(g1,g2)
    c: Horizontal(g2)
    c: Coincident(g2,g3)
    c: Coincident(g3,g4)
    c: Horizontal(g4)
    c: Coincident(g4,g5)
    c: Coincident(g5,g6)
    c: Horizontal(g6)
    c: Coincident(g6,g7)
    c: Coincident(g7,g0)
    c: Vertical(g7)
    c: DistanceY(g0,g6) = -2
    c: DistanceX(g6,g5) = 3
    c: DistanceX(g0,g0) = 100
    c: Symmetric(g0,g0,g-2)
    c: Symmetric(g6,g1,g-2)
    c: Symmetric(g5,g2,g-2)
    c: Symmetric(g4,g3,g-2)
    c: DistanceX(g4,g3) = 88
    c: DistanceY(g0,g4) = -16
FEATURE [Part::Extrusion] Extrude235  label="Plaque_alveolaire_008"
  Base = -> Sketch190
  Dir = (0,2000,0)
  Placement = pos=(-1001,-62,22) rot=(0,0,1;3.14159rad)
  Solid = true
FEATURE [App::DocumentObjectGroup] Groupe010  label="Assemblage_miroir X=-1001_001"
  Group = -> [Cut085,Fusion048,Extrude220,Part__Feature010,Extrude221,Fillet019,Fusion051,Cut091,Extrude234,Extrude235]
FEATURE [Sketcher::SketchObject] Sketch191
  Placement = pos=(0,0,0) rot=(1,0,0;1.5708rad)
  sketch-geometry (8):
    g0: LineSegment StartX=-21.15 StartY=16.15 StartZ=0 EndX=-16.15 EndY=21.15 EndZ=0
    g1: LineSegment StartX=-16.15 StartY=21.15 StartZ=0 EndX=16.15 EndY=21.15 EndZ=0
    g2: LineSegment StartX=16.15 StartY=21.15 StartZ=0 EndX=21.15 EndY=16.15 EndZ=0
    g3: LineSegment StartX=21.15 StartY=16.15 StartZ=0 EndX=21.15 EndY=-16.15 EndZ=0
    g4: LineSegment StartX=21.15 StartY=-16.15 StartZ=0 EndX=16.15 EndY=-21.15 EndZ=0
    g5: LineSegment StartX=16.15 StartY=-21.15 StartZ=0 EndX=-16.15 EndY=-21.15 EndZ=0
    g6: LineSegment StartX=-16.15 StartY=-21.15 StartZ=0 EndX=-21.15 EndY=-16.15 EndZ=0
    g7: LineSegment StartX=-21.15 StartY=-16.15 StartZ=0 EndX=-21.15 EndY=16.15 EndZ=0
  constraints (21):
    c: Coincident(g0,g1)
    c: Horizontal(g1)
    c: Coincident(g1,g2)
    c: Coincident(g2,g3)
    c: Vertical(g3)
    c: Coincident(g3,g4)
    c: Coincident(g4,g5)
    c: Horizontal(g5)
    c: Coincident(g5,g6)
    c: Coincident(g6,g7)
    c: Coincident(g7,g0)
    c: Angle(g7,g0) = 2.35619
    c: Distance(g0,g7) = 5
    c: Distance(g2,g7) = 42.3
    c: Distance(g5,g1) = 42.3
    c: Symmetric(g6,g3,g-2)
    c: Symmetric(g5,g4,g-2)
    c: Symmetric(g0,g2,g-2)
    c: Symmetric(g0,g1,g-2)
    c: Symmetric(g0,g6,g-1)
    c: Symmetric(g0,g5,g-1)
FEATURE [Part::Extrusion] Extrude236
  Base = -> Sketch191
  Dir = (0,48,0)
  Solid = true
FEATURE [Sketcher::SketchObject] Sketch192
  Placement = pos=(0,0,0) rot=(1,0,0;1.5708rad)
  Support = -> Extrude236 [Face9]
  sketch-geometry (1):
    g0: Circle CenterX=0 CenterY=0 CenterZ=0 NormalX=0 NormalY=0 NormalZ=1 Radius=11
  constraints (2):
    c: Coincident(g0,g-1)
    c: Radius(g0) = 11
FEATURE [Part::Extrusion] Extrude237
  Base = -> Sketch192
  Dir = (0,-2,0)
  Solid = true
FEATURE [Sketcher::SketchObject] Sketch193
  Placement = pos=(0,-2,0) rot=(1,0,0;1.5708rad)
  Support = -> Extrude237 [Face3]
  sketch-geometry (1):
    g0: Circle CenterX=0 CenterY=0 CenterZ=0 NormalX=0 NormalY=0 NormalZ=1 Radius=2.5
  constraints (2):
    c: Coincident(g0,g-1)
    c: Radius(g0) = 2.5
FEATURE [Part::Extrusion] Extrude238
  Base = -> Sketch193
  Dir = (0,-22,0)
  Solid = true
FEATURE [Part::Chamfer] Chamfer027
  Base = -> Extrude238
  Edges = 1 edges r=0.8: [Edge3]
FEATURE [Sketcher::SketchObject] Sketch194
  Placement = pos=(0,0,0) rot=(1,0,0;1.5708rad)
  Support = -> Extrude236 [Face9]
  sketch-geometry (4):
    g0: Circle CenterX=-15.5 CenterY=15.5 CenterZ=0 NormalX=0 NormalY=0 NormalZ=1 Radius=2
    g1: Circle CenterX=15.5 CenterY=15.5 CenterZ=0 NormalX=0 NormalY=0 NormalZ=1 Radius=2
    g2: Circle CenterX=-15.5 CenterY=-15.5 CenterZ=0 NormalX=0 NormalY=0 NormalZ=1 Radius=2
    g3: Circle CenterX=15.5 CenterY=-15.5 CenterZ=0 NormalX=0 NormalY=0 NormalZ=1 Radius=2
  constraints (9):
    c: Distance(g0,g1) = 31
    c: Distance(g0,g2) = 31
    c: Symmetric(g0,g2,g-1)
    c: Symmetric(g0,g1,g-2)
    c: Symmetric(g2,g3,g-2)
    c: Radius(g0) = 2
    c: Equal(g0,g1)
    c: Equal(g0,g2)
    c: Equal(g0,g3)
FEATURE [Part::Extrusion] Extrude239
  Base = -> Sketch194
  Dir = (0,4.5,0)
  Solid = true
FEATURE [Part::Cut] Cut092
  Base = -> Extrude236
  Tool = -> Extrude239
FEATURE [Sketcher::SketchObject] Sketch195
  Placement = pos=(0,0,0) rot=(1,0,0;1.5708rad)
  sketch-geometry (1):
    g0: Circle CenterX=0 CenterY=0 CenterZ=0 NormalX=0 NormalY=0 NormalZ=1 Radius=9
  constraints (2):
    c: Coincident(g0,g-1)
    c: Radius(g0) = 9
FEATURE [Part::Extrusion] Extrude240
  Base = -> Sketch195
  Dir = (0,25,0)
  Solid = true
FEATURE [Sketcher::SketchObject] Sketch196
  Placement = pos=(0,0,0) rot=(1,0,0;1.5708rad)
  sketch-geometry (1):
    g0: Circle CenterX=0 CenterY=0 CenterZ=0 NormalX=0 NormalY=0 NormalZ=1 Radius=2.5
  constraints (2):
    c: Coincident(g0,g-1)
    c: Radius(g0) = 2.5
FEATURE [Part::Extrusion] Extrude241
  Base = -> Sketch196
  Dir = (0,10,0)
  Solid = true
FEATURE [Part::Cut] Cut093
  Base = -> Extrude240
  Tool = -> Extrude241
FEATURE [Sketcher::SketchObject] Sketch197
  Placement = pos=(0,25,0) rot=(0,0.707107,0.707107;3.14159rad)
  Support = -> Cut093 [Face3]
  sketch-geometry (1):
    g0: Circle CenterX=0 CenterY=0 CenterZ=0 NormalX=0 NormalY=0 NormalZ=1 Radius=4
  constraints (2):
    c: Coincident(g0,g-1)
    c: Radius(g0) = 4
FEATURE [Part::Extrusion] Extrude242
  Base = -> Sketch197
  Dir = (0,-10,0)
  Solid = true
FEATURE [Part::Cut] Cut094  label="Accouplement_009"
  Base = -> Cut093
  Placement = pos=(-1144,-12,0) rot=(1,0,0;3.14159rad)
  Tool = -> Extrude242
FEATURE [Part::Fuse] Fusion052
  Base = -> Extrude237
  Tool = -> Cut092
FEATURE [Part::Fuse] Fusion053  label="Moteur_009"
  Base = -> Chamfer027
  Placement = pos=(-1144,0,0) rot=(0,0,1;0rad)
  Tool = -> Fusion052
FEATURE [Sketcher::SketchObject] Sketch198
  Placement = pos=(0,0,0) rot=(1,0,0;1.5708rad)
  sketch-geometry (4):
    g0: LineSegment StartX=-50 StartY=0 StartZ=0 EndX=-47 EndY=0 EndZ=0
    g1: LineSegment StartX=47 StartY=0 StartZ=0 EndX=50 EndY=0 EndZ=0
    g2: ArcOfCircle CenterX=0 CenterY=0 CenterZ=0 NormalX=0 NormalY=0 NormalZ=1 Radius=47 StartAngle=3.14159 EndAngle=6.28319
    g3: ArcOfCircle CenterX=0 CenterY=0 CenterZ=0 NormalX=0 NormalY=0 NormalZ=1 Radius=50 StartAngle=3.14159 EndAngle=6.28319
  constraints (13):
    c: Horizontal(g0)
    c: PointOnObject(g1,g-1)
    c: Horizontal(g1)
    c: Coincident(g2,g-1)
    c: PointOnObject(g2,g-1)
    c: Coincident(g3,g-1)
    c: Coincident(g3,g1)
    c: PointOnObject(g3,g-1)
    c: Coincident(g0,g3)
    c: Coincident(g0,g2)
    c: Distance(g0,g1) = 100
    c: Distance(g0,g0) = 3
    c: Coincident(g1,g2)
FEATURE [Part::Extrusion] Extrude243  label="Demi_tube_sous_miroir_009"
  Base = -> Sketch198
  Dir = (0,2000,0)
  Placement = pos=(-1144,-62,20) rot=(0,0,1;3.14159rad)
  Solid = true
FEATURE [Part::Feature] Part__Feature011  label="Coussinet_autolub_C2-151-8-128_009"
  Placement = pos=(-1144,-46,0) rot=(0,0,1;1.5708rad)
  shape: bbox 16 x 8 x 16 mm, 12 faces (baked)
FEATURE [Sketcher::SketchObject] Sketch199
  Placement = pos=(0,0,0) rot=(1,0,0;1.5708rad)
  sketch-geometry (21):
    g0: Circle CenterX=0 CenterY=0 CenterZ=0 NormalX=0 NormalY=0 NormalZ=1 Radius=6
    g1: LineSegment StartX=-20.5 StartY=15 StartZ=0 EndX=20.5 EndY=15 EndZ=0
    g2: ArcOfCircle CenterX=20.5 CenterY=13 CenterZ=0 NormalX=0 NormalY=0 NormalZ=1 Radius=2 StartAngle=6.28319 EndAngle=7.85398
    g3: LineSegment StartX=22.5 StartY=13 StartZ=0 EndX=22.5 EndY=-73 EndZ=0
    g4: LineSegment StartX=-22.5 StartY=13 StartZ=0 EndX=-22.5 EndY=-73 EndZ=0
    g5: ArcOfCircle CenterX=-20.5 CenterY=13 CenterZ=0 NormalX=0 NormalY=0 NormalZ=1 Radius=2 StartAngle=1.5708 EndAngle=3.14159
    g6: ArcOfCircle CenterX=-20.5 CenterY=-73 CenterZ=0 NormalX=0 NormalY=0 NormalZ=1 Radius=2 StartAngle=3.14159 EndAngle=4.71239
    g7: ArcOfCircle CenterX=20.5 CenterY=-73 CenterZ=0 NormalX=0 NormalY=0 NormalZ=1 Radius=2 StartAngle=4.71239 EndAngle=6.28319
    g8: LineSegment StartX=-20.5 StartY=-75 StartZ=0 EndX=20.5 EndY=-75 EndZ=0
    g9: ArcOfCircle CenterX=0 CenterY=-16.7 CenterZ=0 NormalX=0 NormalY=0 NormalZ=1 Radius=1.5 StartAngle=0 EndAngle=3.14159
    g10: ArcOfCircle CenterX=0 CenterY=-24.3 CenterZ=0 NormalX=0 NormalY=0 NormalZ=1 Radius=1.5 StartAngle=3.14159 EndAngle=6.28319
    g11: LineSegment StartX=-1.5 StartY=-16.7 StartZ=0 EndX=-1.5 EndY=-24.3 EndZ=0
    g12: LineSegment StartX=1.5 StartY=-16.7 StartZ=0 EndX=1.5 EndY=-24.3 EndZ=0
    g13: Circle CenterX=-12.5 CenterY=-45 CenterZ=0 NormalX=0 NormalY=0 NormalZ=1 Radius=3.5
    g14: Circle CenterX=12.5 CenterY=-45 CenterZ=0 NormalX=0 NormalY=0 NormalZ=1 Radius=3.5
    g15: Circle CenterX=-12.5 CenterY=-65 CenterZ=0 NormalX=0 NormalY=0 NormalZ=1 Radius=3.5
    g16: Circle CenterX=12.5 CenterY=-65 CenterZ=0 NormalX=0 NormalY=0 NormalZ=1 Radius=3.5
    g17: LineSegment [constr] StartX=-12.5 StartY=-45 StartZ=0 EndX=12.5 EndY=-45 EndZ=0
    g18: LineSegment [constr] StartX=-12.5 StartY=-45 StartZ=0 EndX=-12.5 EndY=-65 EndZ=0
    g19: LineSegment [constr] StartX=-12.5 StartY=-65 StartZ=0 EndX=12.5 EndY=-65 EndZ=0
    g20: LineSegment [constr] StartX=12.5 StartY=-45 StartZ=0 EndX=12.5 EndY=-65 EndZ=0
  constraints (59):
    c: Coincident(g0,g-1)
    c: Radius(g0) = 6
    c: Horizontal(g1)
    c: Coincident(g2,g1)
    c: Coincident(g3,g2)
    c: Vertical(g3)
    c: Vertical(g4)
    c: Coincident(g5,g1)
    c: Coincident(g5,g4)
    c: Coincident(g7,g3)
    c: Coincident(g8,g6)
    c: Coincident(g8,g7)
    c: Tangent(g8,g7)
    c: Tangent(g5,g4)
    c: Tangent(g5,g1)
    c: Tangent(g1,g2)
    c: Tangent(g2,g3)
    c: Coincident(g4,g6)
    c: Tangent(g6,g4)
    c: Tangent(g6,g8)
    c: Horizontal(g8)
    c: Tangent(g7,g3)
    c: Distance(g4,g2) = 45
    c: Symmetric(g4,g2,g-2)
    c: Distance(g1,g6) = 90
    c: DistanceY(g-1,g1) = 15
    c: Tangent(g9,g12) = 1.5708
    c: Tangent(g9,g11) = -1.5708
    c: Tangent(g11,g10) = -1.5708
    c: Tangent(g12,g10) = 1.5708
    c: Vertical(g11)
    c: Equal(g9,g10)
    c: PointOnObject(g9,g-2)
    c: Distance(g-1,g9) = 16.7
    c: Distance(g9,g10) = 7.6
    c: Radius(g9) = 1.5
    c: Radius(g13) = 3.5
    c: Equal(g13,g14)
    c: Equal(g13,g16)
    c: Equal(g13,g15)
    c: Radius(g5) = 2
    c: Equal(g5,g7)
    c: Equal(g5,g6)
    c: DistanceY(g-1,g13) = -45
    c: Coincident(g17,g13)
    c: Coincident(g17,g14)
    c: Horizontal(g17)
    c: Coincident(g18,g13)
    c: Coincident(g18,g15)
    c: Coincident(g19,g15)
    c: Coincident(g19,g16)
    c: Horizontal(g19)
    c: Coincident(g20,g14)
    c: Coincident(g20,g16)
    c: Vertical(g18)
    c: Vertical(g20)
    c: Distance(g13,g15) = 20
    c: Distance(g13,g14) = 25
    c: Symmetric(g13,g14,g-2)
FEATURE [Part::Extrusion] Extrude244  label="Plaque_support_009"
  Base = -> Sketch199
  Dir = (0,6,0)
  Placement = pos=(-1144,-46,0) rot=(0,0,1;0rad)
  Solid = true
FEATURE [Sketcher::SketchObject] Sketch200
  Placement = pos=(0,0,0) rot=(0.57735,0.57735,0.57735;2.0944rad)
  sketch-geometry (8):
    g0: LineSegment StartX=0 StartY=33 StartZ=0 EndX=-2 EndY=33 EndZ=0
    g1: LineSegment StartX=-2 StartY=33 StartZ=0 EndX=-2 EndY=-24 EndZ=0
    g2: ArcOfCircle CenterX=-4 CenterY=-24 CenterZ=0 NormalX=0 NormalY=0 NormalZ=1 Radius=2 StartAngle=4.71239 EndAngle=6.28319
    g3: LineSegment StartX=-4 StartY=-26 StartZ=0 EndX=-38 EndY=-26 EndZ=0
    g4: LineSegment StartX=-38 StartY=-26 StartZ=0 EndX=-38 EndY=-28 EndZ=0
    g5: LineSegment StartX=-38 StartY=-28 StartZ=0 EndX=-4 EndY=-28 EndZ=0
    g6: ArcOfCircle CenterX=-4 CenterY=-24 CenterZ=0 NormalX=0 NormalY=0 NormalZ=1 Radius=4 StartAngle=4.71239 EndAngle=6.28319
    g7: LineSegment StartX=0 StartY=-24 StartZ=0 EndX=0 EndY=33 EndZ=0
  constraints (22):
    c: PointOnObject(g0,g-2)
    c: Horizontal(g0)
    c: Coincident(g0,g1)
    c: Vertical(g1)
    c: Tangent(g1,g2) = 1.5708
    c: Tangent(g2,g3) = 1.5708
    c: Coincident(g3,g4)
    c: Vertical(g4)
    c: Coincident(g4,g5)
    c: Horizontal(g5)
    c: Tangent(g5,g6) = -1.5708
    c: PointOnObject(g6,g-2)
    c: Tangent(g6,g7) = -1.5708
    c: Coincident(g7,g0)
    c: Horizontal(g3)
    c: DistanceX(g0,g0) = 2
    c: Radius(g2) = 2
    c: Radius(g6) = 4
    c: DistanceY(g3,g4) = -2
    c: Distance(g-1,g0) = 33
    c: DistanceY(g-1,g5) = -28
    c: DistanceX(g6,g4) = -38
FEATURE [Part::Extrusion] Extrude245
  Base = -> Sketch200
  Dir = (-32.5,0,0)
  Solid = true
FEATURE [Part::Extrusion] Extrude246
  Base = -> Sketch200
  Dir = (32.5,0,0)
  Solid = true
FEATURE [Part::MultiFuse] Fusion054
  Shapes = -> [Extrude245,Extrude246]
FEATURE [Sketcher::SketchObject] Sketch201
  Placement = pos=(0,-2,0) rot=(1,0,0;1.5708rad)
  Support = -> Fusion054 [Face3]
  sketch-geometry (9):
    g0: ArcOfCircle CenterX=0 CenterY=0 CenterZ=0 NormalX=0 NormalY=0 NormalZ=1 Radius=32.5 StartAngle=0 EndAngle=3.14159
    g1: LineSegment StartX=-32.5 StartY=0 StartZ=0 EndX=-32.5 EndY=34 EndZ=0
    g2: LineSegment StartX=-32.5 StartY=34 StartZ=0 EndX=32.5 EndY=34 EndZ=0
    g3: LineSegment StartX=32.5 StartY=34 StartZ=0 EndX=32.5 EndY=0 EndZ=0
    g4: Circle CenterX=0 CenterY=0 CenterZ=0 NormalX=0 NormalY=0 NormalZ=1 Radius=11
    g5: Circle CenterX=-15.5 CenterY=15.5 CenterZ=0 NormalX=0 NormalY=0 NormalZ=1 Radius=2
    g6: Circle CenterX=15.5 CenterY=15.5 CenterZ=0 NormalX=0 NormalY=0 NormalZ=1 Radius=2
    g7: Circle CenterX=-15.5 CenterY=-15.5 CenterZ=0 NormalX=0 NormalY=0 NormalZ=1 Radius=2
    g8: Circle CenterX=15.5 CenterY=-15.5 CenterZ=0 NormalX=0 NormalY=0 NormalZ=1 Radius=2
  constraints (23):
    c: Coincident(g0,g-1)
    c: PointOnObject(g0,g-1)
    c: PointOnObject(g0,g-1)
    c: Coincident(g1,g0)
    c: Vertical(g1)
    c: Coincident(g1,g2)
    c: Horizontal(g2)
    c: Coincident(g2,g3)
    c: Coincident(g3,g0)
    c: Vertical(g3)
    c: DistanceY(g1,g0) = -34
    c: Coincident(g4,g-1)
    c: Radius(g4) = 11
    c: DistanceX(g1,g2) = 65
    c: Radius(g5) = 2
    c: Equal(g5,g6)
    c: Equal(g5,g8)
    c: Equal(g5,g7)
    c: Symmetric(g5,g6,g-2)
    c: Symmetric(g5,g7,g-1)
    c: Symmetric(g7,g8,g-2)
    c: DistanceX(g5,g6) = 31
    c: DistanceY(g5,g7) = -31
FEATURE [Part::Extrusion] Extrude247
  Base = -> Sketch201
  Dir = (0,2,0)
  Solid = true
FEATURE [Part::Cut] Cut095
  Base = -> Fusion054
  Tool = -> Extrude247
FEATURE [Sketcher::SketchObject] Sketch202
  ExternalGeometry = -> [Cut095]
  Placement = pos=(0,0,-26) rot=(0,0,1;0rad)
  Support = -> Cut095 [Face5]
  sketch-geometry (5):
    g0: Circle CenterX=-25 CenterY=-12 CenterZ=0 NormalX=0 NormalY=0 NormalZ=1 Radius=3.5
    g1: Circle CenterX=-25 CenterY=-30 CenterZ=0 NormalX=0 NormalY=0 NormalZ=1 Radius=3.5
    g2: Circle CenterX=25 CenterY=-12 CenterZ=0 NormalX=0 NormalY=0 NormalZ=1 Radius=3.5
    g3: Circle CenterX=25 CenterY=-30 CenterZ=0 NormalX=0 NormalY=0 NormalZ=1 Radius=3.5
    g4: LineSegment [constr] StartX=-25 StartY=-12 StartZ=0 EndX=-25 EndY=-30 EndZ=0
  constraints (12):
    c: Radius(g0) = 3.5
    c: Equal(g0,g2)
    c: Equal(g0,g3)
    c: Equal(g0,g1)
    c: Symmetric(g0,g2,g-2)
    c: Symmetric(g1,g3,g-2)
    c: Coincident(g4,g0)
    c: Coincident(g4,g1)
    c: Vertical(g4)
    c: DistanceY(g0,g1) = -18
    c: DistanceY(g-3,g1) = 8
    c: DistanceX(g0,g2) = 50
FEATURE [Part::Extrusion] Extrude248
  Base = -> Sketch202
  Dir = (0,0,-2)
  Solid = true
FEATURE [Part::Cut] Cut096
  Base = -> Cut095
  Tool = -> Extrude248
FEATURE [Part::Fillet] Fillet021  label="Plaque_moteur_009"
  Base = -> Cut096
  Edges = 2 edges r=4: [Edge5,Edge59]
  Placement = pos=(-1144,0,0) rot=(0,0,1;0rad)
FEATURE [Sketcher::SketchObject] Sketch203
  Placement = pos=(0,0,0) rot=(1,0,0;1.5708rad)
  sketch-geometry (4):
    g0: LineSegment StartX=-3.15 StartY=5.95 StartZ=0 EndX=3.15 EndY=5.95 EndZ=0
    g1: LineSegment StartX=3.15 StartY=5.95 StartZ=0 EndX=3.15 EndY=-5.95 EndZ=0
    g2: LineSegment StartX=3.15 StartY=-5.95 StartZ=0 EndX=-3.15 EndY=-5.95 EndZ=0
    g3: LineSegment StartX=-3.15 StartY=-5.95 StartZ=0 EndX=-3.15 EndY=5.95 EndZ=0
  constraints (12):
    c: Coincident(g0,g1)
    c: Coincident(g1,g2)
    c: Coincident(g2,g3)
    c: Coincident(g3,g0)
    c: Horizontal(g0)
    c: Horizontal(g2)
    c: Vertical(g1)
    c: Vertical(g3)
    c: DistanceX(g0,g0) = 6.3
    c: DistanceY(g0,g2) = -11.9
    c: Symmetric(g0,g0,g-2)
    c: Symmetric(g0,g1,g-1)
FEATURE [Part::Extrusion] Extrude249
  Base = -> Sketch203
  Dir = (0,-10.8,0)
  Solid = true
FEATURE [Sketcher::SketchObject] Sketch204
  ExternalGeometry = -> [Extrude249]
  Placement = pos=(0,-10.8,0) rot=(1,0,0;1.5708rad)
  Support = -> Extrude249 [Face6]
  sketch-geometry (4):
    g0: LineSegment StartX=-3.15 StartY=1.55 StartZ=0 EndX=3.15 EndY=1.55 EndZ=0
    g1: LineSegment StartX=3.15 StartY=1.55 StartZ=0 EndX=3.15 EndY=-1.55 EndZ=0
    g2: LineSegment StartX=3.15 StartY=-1.55 StartZ=0 EndX=-3.15 EndY=-1.55 EndZ=0
    g3: LineSegment StartX=-3.15 StartY=-1.55 StartZ=0 EndX=-3.15 EndY=1.55 EndZ=0
  constraints (12):
    c: Coincident(g0,g1)
    c: Coincident(g1,g2)
    c: Coincident(g2,g3)
    c: Coincident(g3,g0)
    c: Horizontal(g0)
    c: Horizontal(g2)
    c: Vertical(g1)
    c: Vertical(g3)
    c: PointOnObject(g0,g-4)
    c: PointOnObject(g0,g-3)
    c: DistanceY(g0,g2) = -3.1
    c: Symmetric(g0,g1,g-1)
FEATURE [Part::Extrusion] Extrude250
  Base = -> Sketch204
  Dir = (0,7.7,0)
  Solid = true
FEATURE [Part::Cut] Cut097
  Base = -> Extrude249
  Tool = -> Extrude250
FEATURE [Part::Chamfer] Chamfer028
  Base = -> Cut097
  Edges = 4 edges r=0.5: [Edge7,Edge9,Edge15,Edge17]
FEATURE [Part::Chamfer] Chamfer029
  Base = -> Chamfer028
  Edges = 1 edges r=1.2: [Edge13]
FEATURE [Sketcher::SketchObject] Sketch205
  ExternalGeometry = -> [Chamfer029]
  Placement = pos=(0,0,5.95) rot=(0,0,1;0rad)
  Support = -> Chamfer029 [Face5]
  sketch-geometry (4):
    g0: LineSegment StartX=-3 StartY=0 StartZ=0 EndX=3 EndY=0 EndZ=0
    g1: LineSegment StartX=3 StartY=0 StartZ=0 EndX=3 EndY=-3.1 EndZ=0
    g2: LineSegment StartX=3 StartY=-3.1 StartZ=0 EndX=-3 EndY=-3.1 EndZ=0
    g3: LineSegment StartX=-3 StartY=-3.1 StartZ=0 EndX=-3 EndY=0 EndZ=0
  constraints (12):
    c: Coincident(g0,g1)
    c: Coincident(g1,g2)
    c: Coincident(g2,g3)
    c: Coincident(g3,g0)
    c: Horizontal(g0)
    c: Horizontal(g2)
    c: Vertical(g1)
    c: Vertical(g3)
    c: PointOnObject(g0,g-1)
    c: DistanceX(g-3,g0) = 0.15
    c: Symmetric(g0,g0,g-2)
    c: DistanceY(g0,g1) = -3.1
FEATURE [Part::Extrusion] Extrude251
  Base = -> Sketch205
  Dir = (0,0,6.3)
  Solid = true
FEATURE [Sketcher::SketchObject] Sketch206
  ExternalGeometry = -> [Extrude251]
  Placement = pos=(0,-3.1,0) rot=(1,0,0;1.5708rad)
  Support = -> Extrude251 [Face3]
  sketch-geometry (1):
    g0: Circle CenterX=0 CenterY=9.5 CenterZ=0 NormalX=0 NormalY=0 NormalZ=1 Radius=1.65
  constraints (3):
    c: PointOnObject(g0,g-2)
    c: Radius(g0) = 1.65
    c: DistanceY(g0,g-3) = -3.55
FEATURE [Part::Extrusion] Extrude252
  Base = -> Sketch206
  Dir = (0,6,0)
  Solid = true
FEATURE [Part::Cut] Cut098
  Base = -> Extrude251
  Tool = -> Extrude252
FEATURE [Part::Fillet] Fillet022
  Base = -> Cut098
  Edges = 2 edges r=1.35: [Edge8,Edge11]
FEATURE [Part::MultiFuse] Fusion055
  Shapes = -> [Chamfer029]
FEATURE [Sketcher::SketchObject] Sketch207
  Placement = pos=(0,0,0) rot=(0,0.707107,0.707107;3.14159rad)
  Support = -> Fusion055 [Face7]
  sketch-geometry (4):
    g0: Circle CenterX=-1.27 CenterY=3.8 CenterZ=0 NormalX=0 NormalY=0 NormalZ=1 Radius=0.2
    g1: Circle CenterX=1.27 CenterY=3.8 CenterZ=0 NormalX=0 NormalY=0 NormalZ=1 Radius=0.2
    g2: Circle CenterX=-1.27 CenterY=-3.8 CenterZ=0 NormalX=0 NormalY=0 NormalZ=1 Radius=0.2
    g3: Circle CenterX=1.27 CenterY=-3.8 CenterZ=0 NormalX=0 NormalY=0 NormalZ=1 Radius=0.2
  constraints (9):
    c: Radius(g0) = 0.2
    c: Equal(g0,g1)
    c: Equal(g0,g3)
    c: Equal(g0,g2)
    c: Symmetric(g0,g1,g-2)
    c: Symmetric(g2,g3,g-2)
    c: Symmetric(g0,g2,g-1)
    c: DistanceX(g0,g1) = 2.54
    c: DistanceY(g1,g3) = -7.6
FEATURE [Part::Extrusion] Extrude253
  Base = -> Sketch207
  Dir = (0,7.8,0)
  Solid = true
FEATURE [Part::MultiFuse] Fusion056  label="Capteur_optique_009"
  Placement = pos=(-1144,-46,-20.7) rot=(0,0,1;0rad)
  Shapes = -> [Fusion055,Fillet022,Extrude253]
FEATURE [Sketcher::SketchObject] Sketch208
  Placement = pos=(0,0,0) rot=(1,0,0;1.5708rad)
  sketch-geometry (1):
    g0: Circle CenterX=0 CenterY=0 CenterZ=0 NormalX=0 NormalY=0 NormalZ=1 Radius=4
  constraints (2):
    c: Coincident(g0,g-1)
    c: Radius(g0) = 4
FEATURE [Part::Extrusion] Extrude254
  Base = -> Sketch208
  Dir = (0,50,0)
  Solid = true
FEATURE [Sketcher::SketchObject] Sketch209
  Placement = pos=(0,0,0) rot=(0.57735,0.57735,0.57735;2.0944rad)
  sketch-geometry (1):
    g0: Circle CenterX=6 CenterY=0 CenterZ=0 NormalX=0 NormalY=0 NormalZ=1 Radius=2
  constraints (3):
    c: DistanceX(g-1,g0) = 6
    c: Radius(g0) = 2
    c: PointOnObject(g0,g-1)
FEATURE [Part::Extrusion] Extrude255
  Base = -> Sketch209
  Dir = (4,0,0)
  Solid = true
FEATURE [Part::Extrusion] Extrude256
  Base = -> Sketch209
  Dir = (-4,0,0)
  Solid = true
FEATURE [Part::Cut] Cut099
  Base = -> Extrude254
  Tool = -> Extrude255
FEATURE [Part::Cut] Cut100  label="Axe_D8_009"
  Base = -> Cut099
  Placement = pos=(-1144,-86,0) rot=(0,0,1;0rad)
  Tool = -> Extrude256
FEATURE [Sketcher::SketchObject] Sketch210
  Placement = pos=(0,0,0) rot=(1,0,0;1.5708rad)
  sketch-geometry (1):
    g0: Circle CenterX=0 CenterY=0 CenterZ=0 NormalX=0 NormalY=0 NormalZ=1 Radius=2
  constraints (2):
    c: Coincident(g0,g-1)
    c: Radius(g0) = 2
FEATURE [Part::Extrusion] Extrude257  label="Axe_D4_009"
  Base = -> Sketch210
  Dir = (0,103.6,0)
  Placement = pos=(-1092.2,-80,0) rot=(0,0,1;1.5708rad)
  Solid = true
FEATURE [Sketcher::SketchObject] Sketch211
  Placement = pos=(0,0,0) rot=(1,0,0;1.5708rad)
  sketch-geometry (8):
    g0: LineSegment StartX=-50 StartY=0 StartZ=0 EndX=50 EndY=0 EndZ=0
    g1: LineSegment StartX=50 StartY=0 StartZ=0 EndX=50 EndY=-2 EndZ=0
    g2: LineSegment StartX=50 StartY=-2 StartZ=0 EndX=47 EndY=-2 EndZ=0
    g3: LineSegment StartX=47 StartY=-2 StartZ=0 EndX=44 EndY=-16 EndZ=0
    g4: LineSegment StartX=44 StartY=-16 StartZ=0 EndX=-44 EndY=-16 EndZ=0
    g5: LineSegment StartX=-44 StartY=-16 StartZ=0 EndX=-47 EndY=-2 EndZ=0
    g6: LineSegment StartX=-47 StartY=-2 StartZ=0 EndX=-50 EndY=-2 EndZ=0
    g7: LineSegment StartX=-50 StartY=-2 StartZ=0 EndX=-50 EndY=0 EndZ=0
  constraints (24):
    c: PointOnObject(g0,g-1)
    c: Horizontal(g0)
    c: Coincident(g0,g1)
    c: Vertical(g1)
    c: Coincident(g1,g2)
    c: Horizontal(g2)
    c: Coincident(g2,g3)
    c: Coincident(g3,g4)
    c: Horizontal(g4)
    c: Coincident(g4,g5)
    c: Coincident(g5,g6)
    c: Horizontal(g6)
    c: Coincident(g6,g7)
    c: Coincident(g7,g0)
    c: Vertical(g7)
    c: DistanceY(g0,g6) = -2
    c: DistanceX(g6,g5) = 3
    c: DistanceX(g0,g0) = 100
    c: Symmetric(g0,g0,g-2)
    c: Symmetric(g6,g1,g-2)
    c: Symmetric(g5,g2,g-2)
    c: Symmetric(g4,g3,g-2)
    c: DistanceX(g4,g3) = 88
    c: DistanceY(g0,g4) = -16
FEATURE [Part::Extrusion] Extrude258  label="Plaque_alveolaire_009"
  Base = -> Sketch211
  Dir = (0,2000,0)
  Placement = pos=(-1144,-62,22) rot=(0,0,1;3.14159rad)
  Solid = true
FEATURE [App::DocumentObjectGroup] Groupe011  label="Assemblage_miroir X=-1144_001"
  Group = -> [Cut094,Fusion053,Extrude243,Part__Feature011,Extrude244,Fillet021,Fusion056,Cut100,Extrude257,Extrude258]
FEATURE [Sketcher::SketchObject] Sketch212
  Placement = pos=(0,0,0) rot=(1,0,0;1.5708rad)
  sketch-geometry (8):
    g0: LineSegment StartX=-21.15 StartY=16.15 StartZ=0 EndX=-16.15 EndY=21.15 EndZ=0
    g1: LineSegment StartX=-16.15 StartY=21.15 StartZ=0 EndX=16.15 EndY=21.15 EndZ=0
    g2: LineSegment StartX=16.15 StartY=21.15 StartZ=0 EndX=21.15 EndY=16.15 EndZ=0
    g3: LineSegment StartX=21.15 StartY=16.15 StartZ=0 EndX=21.15 EndY=-16.15 EndZ=0
    g4: LineSegment StartX=21.15 StartY=-16.15 StartZ=0 EndX=16.15 EndY=-21.15 EndZ=0
    g5: LineSegment StartX=16.15 StartY=-21.15 StartZ=0 EndX=-16.15 EndY=-21.15 EndZ=0
    g6: LineSegment StartX=-16.15 StartY=-21.15 StartZ=0 EndX=-21.15 EndY=-16.15 EndZ=0
    g7: LineSegment StartX=-21.15 StartY=-16.15 StartZ=0 EndX=-21.15 EndY=16.15 EndZ=0
  constraints (21):
    c: Coincident(g0,g1)
    c: Horizontal(g1)
    c: Coincident(g1,g2)
    c: Coincident(g2,g3)
    c: Vertical(g3)
    c: Coincident(g3,g4)
    c: Coincident(g4,g5)
    c: Horizontal(g5)
    c: Coincident(g5,g6)
    c: Coincident(g6,g7)
    c: Coincident(g7,g0)
    c: Angle(g7,g0) = 2.35619
    c: Distance(g0,g7) = 5
    c: Distance(g2,g7) = 42.3
    c: Distance(g5,g1) = 42.3
    c: Symmetric(g6,g3,g-2)
    c: Symmetric(g5,g4,g-2)
    c: Symmetric(g0,g2,g-2)
    c: Symmetric(g0,g1,g-2)
    c: Symmetric(g0,g6,g-1)
    c: Symmetric(g0,g5,g-1)
FEATURE [Part::Extrusion] Extrude259
  Base = -> Sketch212
  Dir = (0,48,0)
  Solid = true
FEATURE [Sketcher::SketchObject] Sketch213
  Placement = pos=(0,0,0) rot=(1,0,0;1.5708rad)
  Support = -> Extrude259 [Face9]
  sketch-geometry (1):
    g0: Circle CenterX=0 CenterY=0 CenterZ=0 NormalX=0 NormalY=0 NormalZ=1 Radius=11
  constraints (2):
    c: Coincident(g0,g-1)
    c: Radius(g0) = 11
FEATURE [Part::Extrusion] Extrude260
  Base = -> Sketch213
  Dir = (0,-2,0)
  Solid = true
FEATURE [Sketcher::SketchObject] Sketch214
  Placement = pos=(0,-2,0) rot=(1,0,0;1.5708rad)
  Support = -> Extrude260 [Face3]
  sketch-geometry (1):
    g0: Circle CenterX=0 CenterY=0 CenterZ=0 NormalX=0 NormalY=0 NormalZ=1 Radius=2.5
  constraints (2):
    c: Coincident(g0,g-1)
    c: Radius(g0) = 2.5
FEATURE [Part::Extrusion] Extrude261
  Base = -> Sketch214
  Dir = (0,-22,0)
  Solid = true
FEATURE [Part::Chamfer] Chamfer030
  Base = -> Extrude261
  Edges = 1 edges r=0.8: [Edge3]
FEATURE [Sketcher::SketchObject] Sketch215
  Placement = pos=(0,0,0) rot=(1,0,0;1.5708rad)
  Support = -> Extrude259 [Face9]
  sketch-geometry (4):
    g0: Circle CenterX=-15.5 CenterY=15.5 CenterZ=0 NormalX=0 NormalY=0 NormalZ=1 Radius=2
    g1: Circle CenterX=15.5 CenterY=15.5 CenterZ=0 NormalX=0 NormalY=0 NormalZ=1 Radius=2
    g2: Circle CenterX=-15.5 CenterY=-15.5 CenterZ=0 NormalX=0 NormalY=0 NormalZ=1 Radius=2
    g3: Circle CenterX=15.5 CenterY=-15.5 CenterZ=0 NormalX=0 NormalY=0 NormalZ=1 Radius=2
  constraints (9):
    c: Distance(g0,g1) = 31
    c: Distance(g0,g2) = 31
    c: Symmetric(g0,g2,g-1)
    c: Symmetric(g0,g1,g-2)
    c: Symmetric(g2,g3,g-2)
    c: Radius(g0) = 2
    c: Equal(g0,g1)
    c: Equal(g0,g2)
    c: Equal(g0,g3)
FEATURE [Part::Extrusion] Extrude262
  Base = -> Sketch215
  Dir = (0,4.5,0)
  Solid = true
FEATURE [Part::Cut] Cut101
  Base = -> Extrude259
  Tool = -> Extrude262
FEATURE [Sketcher::SketchObject] Sketch216
  Placement = pos=(0,0,0) rot=(1,0,0;1.5708rad)
  sketch-geometry (1):
    g0: Circle CenterX=0 CenterY=0 CenterZ=0 NormalX=0 NormalY=0 NormalZ=1 Radius=9
  constraints (2):
    c: Coincident(g0,g-1)
    c: Radius(g0) = 9
FEATURE [Part::Extrusion] Extrude263
  Base = -> Sketch216
  Dir = (0,25,0)
  Solid = true
FEATURE [Sketcher::SketchObject] Sketch217
  Placement = pos=(0,0,0) rot=(1,0,0;1.5708rad)
  sketch-geometry (1):
    g0: Circle CenterX=0 CenterY=0 CenterZ=0 NormalX=0 NormalY=0 NormalZ=1 Radius=2.5
  constraints (2):
    c: Coincident(g0,g-1)
    c: Radius(g0) = 2.5
FEATURE [Part::Extrusion] Extrude264
  Base = -> Sketch217
  Dir = (0,10,0)
  Solid = true
FEATURE [Part::Cut] Cut102
  Base = -> Extrude263
  Tool = -> Extrude264
FEATURE [Sketcher::SketchObject] Sketch218
  Placement = pos=(0,25,0) rot=(0,0.707107,0.707107;3.14159rad)
  Support = -> Cut102 [Face3]
  sketch-geometry (1):
    g0: Circle CenterX=0 CenterY=0 CenterZ=0 NormalX=0 NormalY=0 NormalZ=1 Radius=4
  constraints (2):
    c: Coincident(g0,g-1)
    c: Radius(g0) = 4
FEATURE [Part::Extrusion] Extrude265
  Base = -> Sketch218
  Dir = (0,-10,0)
  Solid = true
FEATURE [Part::Cut] Cut103  label="Accouplement_010"
  Base = -> Cut102
  Placement = pos=(-1287,-12,0) rot=(1,0,0;3.14159rad)
  Tool = -> Extrude265
FEATURE [Part::Fuse] Fusion057
  Base = -> Extrude260
  Tool = -> Cut101
FEATURE [Part::Fuse] Fusion058  label="Moteur_010"
  Base = -> Chamfer030
  Placement = pos=(-1287,0,0) rot=(0,0,1;0rad)
  Tool = -> Fusion057
FEATURE [Sketcher::SketchObject] Sketch219
  Placement = pos=(0,0,0) rot=(1,0,0;1.5708rad)
  sketch-geometry (4):
    g0: LineSegment StartX=-50 StartY=0 StartZ=0 EndX=-47 EndY=0 EndZ=0
    g1: LineSegment StartX=47 StartY=0 StartZ=0 EndX=50 EndY=0 EndZ=0
    g2: ArcOfCircle CenterX=0 CenterY=0 CenterZ=0 NormalX=0 NormalY=0 NormalZ=1 Radius=47 StartAngle=3.14159 EndAngle=6.28319
    g3: ArcOfCircle CenterX=0 CenterY=0 CenterZ=0 NormalX=0 NormalY=0 NormalZ=1 Radius=50 StartAngle=3.14159 EndAngle=6.28319
  constraints (13):
    c: Horizontal(g0)
    c: PointOnObject(g1,g-1)
    c: Horizontal(g1)
    c: Coincident(g2,g-1)
    c: PointOnObject(g2,g-1)
    c: Coincident(g3,g-1)
    c: Coincident(g3,g1)
    c: PointOnObject(g3,g-1)
    c: Coincident(g0,g3)
    c: Coincident(g0,g2)
    c: Distance(g0,g1) = 100
    c: Distance(g0,g0) = 3
    c: Coincident(g1,g2)
FEATURE [Part::Extrusion] Extrude266  label="Demi_tube_sous_miroir_010"
  Base = -> Sketch219
  Dir = (0,2000,0)
  Placement = pos=(-1287,-62,20) rot=(0,0,1;3.14159rad)
  Solid = true
FEATURE [Part::Feature] Part__Feature012  label="Coussinet_autolub_C2-151-8-128_010"
  Placement = pos=(-1287,-46,0) rot=(0,0,1;1.5708rad)
  shape: bbox 16 x 8 x 16 mm, 12 faces (baked)
FEATURE [Sketcher::SketchObject] Sketch220
  Placement = pos=(0,0,0) rot=(1,0,0;1.5708rad)
  sketch-geometry (21):
    g0: Circle CenterX=0 CenterY=0 CenterZ=0 NormalX=0 NormalY=0 NormalZ=1 Radius=6
    g1: LineSegment StartX=-20.5 StartY=15 StartZ=0 EndX=20.5 EndY=15 EndZ=0
    g2: ArcOfCircle CenterX=20.5 CenterY=13 CenterZ=0 NormalX=0 NormalY=0 NormalZ=1 Radius=2 StartAngle=6.28319 EndAngle=7.85398
    g3: LineSegment StartX=22.5 StartY=13 StartZ=0 EndX=22.5 EndY=-73 EndZ=0
    g4: LineSegment StartX=-22.5 StartY=13 StartZ=0 EndX=-22.5 EndY=-73 EndZ=0
    g5: ArcOfCircle CenterX=-20.5 CenterY=13 CenterZ=0 NormalX=0 NormalY=0 NormalZ=1 Radius=2 StartAngle=1.5708 EndAngle=3.14159
    g6: ArcOfCircle CenterX=-20.5 CenterY=-73 CenterZ=0 NormalX=0 NormalY=0 NormalZ=1 Radius=2 StartAngle=3.14159 EndAngle=4.71239
    g7: ArcOfCircle CenterX=20.5 CenterY=-73 CenterZ=0 NormalX=0 NormalY=0 NormalZ=1 Radius=2 StartAngle=4.71239 EndAngle=6.28319
    g8: LineSegment StartX=-20.5 StartY=-75 StartZ=0 EndX=20.5 EndY=-75 EndZ=0
    g9: ArcOfCircle CenterX=0 CenterY=-16.7 CenterZ=0 NormalX=0 NormalY=0 NormalZ=1 Radius=1.5 StartAngle=0 EndAngle=3.14159
    g10: ArcOfCircle CenterX=0 CenterY=-24.3 CenterZ=0 NormalX=0 NormalY=0 NormalZ=1 Radius=1.5 StartAngle=3.14159 EndAngle=6.28319
    g11: LineSegment StartX=-1.5 StartY=-16.7 StartZ=0 EndX=-1.5 EndY=-24.3 EndZ=0
    g12: LineSegment StartX=1.5 StartY=-16.7 StartZ=0 EndX=1.5 EndY=-24.3 EndZ=0
    g13: Circle CenterX=-12.5 CenterY=-45 CenterZ=0 NormalX=0 NormalY=0 NormalZ=1 Radius=3.5
    g14: Circle CenterX=12.5 CenterY=-45 CenterZ=0 NormalX=0 NormalY=0 NormalZ=1 Radius=3.5
    g15: Circle CenterX=-12.5 CenterY=-65 CenterZ=0 NormalX=0 NormalY=0 NormalZ=1 Radius=3.5
    g16: Circle CenterX=12.5 CenterY=-65 CenterZ=0 NormalX=0 NormalY=0 NormalZ=1 Radius=3.5
    g17: LineSegment [constr] StartX=-12.5 StartY=-45 StartZ=0 EndX=12.5 EndY=-45 EndZ=0
    g18: LineSegment [constr] StartX=-12.5 StartY=-45 StartZ=0 EndX=-12.5 EndY=-65 EndZ=0
    g19: LineSegment [constr] StartX=-12.5 StartY=-65 StartZ=0 EndX=12.5 EndY=-65 EndZ=0
    g20: LineSegment [constr] StartX=12.5 StartY=-45 StartZ=0 EndX=12.5 EndY=-65 EndZ=0
  constraints (59):
    c: Coincident(g0,g-1)
    c: Radius(g0) = 6
    c: Horizontal(g1)
    c: Coincident(g2,g1)
    c: Coincident(g3,g2)
    c: Vertical(g3)
    c: Vertical(g4)
    c: Coincident(g5,g1)
    c: Coincident(g5,g4)
    c: Coincident(g7,g3)
    c: Coincident(g8,g6)
    c: Coincident(g8,g7)
    c: Tangent(g8,g7)
    c: Tangent(g5,g4)
    c: Tangent(g5,g1)
    c: Tangent(g1,g2)
    c: Tangent(g2,g3)
    c: Coincident(g4,g6)
    c: Tangent(g6,g4)
    c: Tangent(g6,g8)
    c: Horizontal(g8)
    c: Tangent(g7,g3)
    c: Distance(g4,g2) = 45
    c: Symmetric(g4,g2,g-2)
    c: Distance(g1,g6) = 90
    c: DistanceY(g-1,g1) = 15
    c: Tangent(g9,g12) = 1.5708
    c: Tangent(g9,g11) = -1.5708
    c: Tangent(g11,g10) = -1.5708
    c: Tangent(g12,g10) = 1.5708
    c: Vertical(g11)
    c: Equal(g9,g10)
    c: PointOnObject(g9,g-2)
    c: Distance(g-1,g9) = 16.7
    c: Distance(g9,g10) = 7.6
    c: Radius(g9) = 1.5
    c: Radius(g13) = 3.5
    c: Equal(g13,g14)
    c: Equal(g13,g16)
    c: Equal(g13,g15)
    c: Radius(g5) = 2
    c: Equal(g5,g7)
    c: Equal(g5,g6)
    c: DistanceY(g-1,g13) = -45
    c: Coincident(g17,g13)
    c: Coincident(g17,g14)
    c: Horizontal(g17)
    c: Coincident(g18,g13)
    c: Coincident(g18,g15)
    c: Coincident(g19,g15)
    c: Coincident(g19,g16)
    c: Horizontal(g19)
    c: Coincident(g20,g14)
    c: Coincident(g20,g16)
    c: Vertical(g18)
    c: Vertical(g20)
    c: Distance(g13,g15) = 20
    c: Distance(g13,g14) = 25
    c: Symmetric(g13,g14,g-2)
FEATURE [Part::Extrusion] Extrude267  label="Plaque_support_010"
  Base = -> Sketch220
  Dir = (0,6,0)
  Placement = pos=(-1287,-46,0) rot=(0,0,1;0rad)
  Solid = true
FEATURE [Sketcher::SketchObject] Sketch221
  Placement = pos=(0,0,0) rot=(0.57735,0.57735,0.57735;2.0944rad)
  sketch-geometry (8):
    g0: LineSegment StartX=0 StartY=33 StartZ=0 EndX=-2 EndY=33 EndZ=0
    g1: LineSegment StartX=-2 StartY=33 StartZ=0 EndX=-2 EndY=-24 EndZ=0
    g2: ArcOfCircle CenterX=-4 CenterY=-24 CenterZ=0 NormalX=0 NormalY=0 NormalZ=1 Radius=2 StartAngle=4.71239 EndAngle=6.28319
    g3: LineSegment StartX=-4 StartY=-26 StartZ=0 EndX=-38 EndY=-26 EndZ=0
    g4: LineSegment StartX=-38 StartY=-26 StartZ=0 EndX=-38 EndY=-28 EndZ=0
    g5: LineSegment StartX=-38 StartY=-28 StartZ=0 EndX=-4 EndY=-28 EndZ=0
    g6: ArcOfCircle CenterX=-4 CenterY=-24 CenterZ=0 NormalX=0 NormalY=0 NormalZ=1 Radius=4 StartAngle=4.71239 EndAngle=6.28319
    g7: LineSegment StartX=0 StartY=-24 StartZ=0 EndX=0 EndY=33 EndZ=0
  constraints (22):
    c: PointOnObject(g0,g-2)
    c: Horizontal(g0)
    c: Coincident(g0,g1)
    c: Vertical(g1)
    c: Tangent(g1,g2) = 1.5708
    c: Tangent(g2,g3) = 1.5708
    c: Coincident(g3,g4)
    c: Vertical(g4)
    c: Coincident(g4,g5)
    c: Horizontal(g5)
    c: Tangent(g5,g6) = -1.5708
    c: PointOnObject(g6,g-2)
    c: Tangent(g6,g7) = -1.5708
    c: Coincident(g7,g0)
    c: Horizontal(g3)
    c: DistanceX(g0,g0) = 2
    c: Radius(g2) = 2
    c: Radius(g6) = 4
    c: DistanceY(g3,g4) = -2
    c: Distance(g-1,g0) = 33
    c: DistanceY(g-1,g5) = -28
    c: DistanceX(g6,g4) = -38
FEATURE [Part::Extrusion] Extrude268
  Base = -> Sketch221
  Dir = (-32.5,0,0)
  Solid = true
FEATURE [Part::Extrusion] Extrude269
  Base = -> Sketch221
  Dir = (32.5,0,0)
  Solid = true
FEATURE [Part::MultiFuse] Fusion059
  Shapes = -> [Extrude268,Extrude269]
FEATURE [Sketcher::SketchObject] Sketch222
  Placement = pos=(0,-2,0) rot=(1,0,0;1.5708rad)
  Support = -> Fusion059 [Face3]
  sketch-geometry (9):
    g0: ArcOfCircle CenterX=0 CenterY=0 CenterZ=0 NormalX=0 NormalY=0 NormalZ=1 Radius=32.5 StartAngle=0 EndAngle=3.14159
    g1: LineSegment StartX=-32.5 StartY=0 StartZ=0 EndX=-32.5 EndY=34 EndZ=0
    g2: LineSegment StartX=-32.5 StartY=34 StartZ=0 EndX=32.5 EndY=34 EndZ=0
    g3: LineSegment StartX=32.5 StartY=34 StartZ=0 EndX=32.5 EndY=0 EndZ=0
    g4: Circle CenterX=0 CenterY=0 CenterZ=0 NormalX=0 NormalY=0 NormalZ=1 Radius=11
    g5: Circle CenterX=-15.5 CenterY=15.5 CenterZ=0 NormalX=0 NormalY=0 NormalZ=1 Radius=2
    g6: Circle CenterX=15.5 CenterY=15.5 CenterZ=0 NormalX=0 NormalY=0 NormalZ=1 Radius=2
    g7: Circle CenterX=-15.5 CenterY=-15.5 CenterZ=0 NormalX=0 NormalY=0 NormalZ=1 Radius=2
    g8: Circle CenterX=15.5 CenterY=-15.5 CenterZ=0 NormalX=0 NormalY=0 NormalZ=1 Radius=2
  constraints (23):
    c: Coincident(g0,g-1)
    c: PointOnObject(g0,g-1)
    c: PointOnObject(g0,g-1)
    c: Coincident(g1,g0)
    c: Vertical(g1)
    c: Coincident(g1,g2)
    c: Horizontal(g2)
    c: Coincident(g2,g3)
    c: Coincident(g3,g0)
    c: Vertical(g3)
    c: DistanceY(g1,g0) = -34
    c: Coincident(g4,g-1)
    c: Radius(g4) = 11
    c: DistanceX(g1,g2) = 65
    c: Radius(g5) = 2
    c: Equal(g5,g6)
    c: Equal(g5,g8)
    c: Equal(g5,g7)
    c: Symmetric(g5,g6,g-2)
    c: Symmetric(g5,g7,g-1)
    c: Symmetric(g7,g8,g-2)
    c: DistanceX(g5,g6) = 31
    c: DistanceY(g5,g7) = -31
FEATURE [Part::Extrusion] Extrude270
  Base = -> Sketch222
  Dir = (0,2,0)
  Solid = true
FEATURE [Part::Cut] Cut104
  Base = -> Fusion059
  Tool = -> Extrude270
FEATURE [Sketcher::SketchObject] Sketch223
  ExternalGeometry = -> [Cut104]
  Placement = pos=(0,0,-26) rot=(0,0,1;0rad)
  Support = -> Cut104 [Face5]
  sketch-geometry (5):
    g0: Circle CenterX=-25 CenterY=-12 CenterZ=0 NormalX=0 NormalY=0 NormalZ=1 Radius=3.5
    g1: Circle CenterX=-25 CenterY=-30 CenterZ=0 NormalX=0 NormalY=0 NormalZ=1 Radius=3.5
    g2: Circle CenterX=25 CenterY=-12 CenterZ=0 NormalX=0 NormalY=0 NormalZ=1 Radius=3.5
    g3: Circle CenterX=25 CenterY=-30 CenterZ=0 NormalX=0 NormalY=0 NormalZ=1 Radius=3.5
    g4: LineSegment [constr] StartX=-25 StartY=-12 StartZ=0 EndX=-25 EndY=-30 EndZ=0
  constraints (12):
    c: Radius(g0) = 3.5
    c: Equal(g0,g2)
    c: Equal(g0,g3)
    c: Equal(g0,g1)
    c: Symmetric(g0,g2,g-2)
    c: Symmetric(g1,g3,g-2)
    c: Coincident(g4,g0)
    c: Coincident(g4,g1)
    c: Vertical(g4)
    c: DistanceY(g0,g1) = -18
    c: DistanceY(g-3,g1) = 8
    c: DistanceX(g0,g2) = 50
FEATURE [Part::Extrusion] Extrude271
  Base = -> Sketch223
  Dir = (0,0,-2)
  Solid = true
FEATURE [Part::Cut] Cut105
  Base = -> Cut104
  Tool = -> Extrude271
FEATURE [Part::Fillet] Fillet023  label="Plaque_moteur_010"
  Base = -> Cut105
  Edges = 2 edges r=4: [Edge5,Edge59]
  Placement = pos=(-1287,0,0) rot=(0,0,1;0rad)
FEATURE [Sketcher::SketchObject] Sketch224
  Placement = pos=(0,0,0) rot=(1,0,0;1.5708rad)
  sketch-geometry (4):
    g0: LineSegment StartX=-3.15 StartY=5.95 StartZ=0 EndX=3.15 EndY=5.95 EndZ=0
    g1: LineSegment StartX=3.15 StartY=5.95 StartZ=0 EndX=3.15 EndY=-5.95 EndZ=0
    g2: LineSegment StartX=3.15 StartY=-5.95 StartZ=0 EndX=-3.15 EndY=-5.95 EndZ=0
    g3: LineSegment StartX=-3.15 StartY=-5.95 StartZ=0 EndX=-3.15 EndY=5.95 EndZ=0
  constraints (12):
    c: Coincident(g0,g1)
    c: Coincident(g1,g2)
    c: Coincident(g2,g3)
    c: Coincident(g3,g0)
    c: Horizontal(g0)
    c: Horizontal(g2)
    c: Vertical(g1)
    c: Vertical(g3)
    c: DistanceX(g0,g0) = 6.3
    c: DistanceY(g0,g2) = -11.9
    c: Symmetric(g0,g0,g-2)
    c: Symmetric(g0,g1,g-1)
FEATURE [Part::Extrusion] Extrude272
  Base = -> Sketch224
  Dir = (0,-10.8,0)
  Solid = true
FEATURE [Sketcher::SketchObject] Sketch225
  ExternalGeometry = -> [Extrude272]
  Placement = pos=(0,-10.8,0) rot=(1,0,0;1.5708rad)
  Support = -> Extrude272 [Face6]
  sketch-geometry (4):
    g0: LineSegment StartX=-3.15 StartY=1.55 StartZ=0 EndX=3.15 EndY=1.55 EndZ=0
    g1: LineSegment StartX=3.15 StartY=1.55 StartZ=0 EndX=3.15 EndY=-1.55 EndZ=0
    g2: LineSegment StartX=3.15 StartY=-1.55 StartZ=0 EndX=-3.15 EndY=-1.55 EndZ=0
    g3: LineSegment StartX=-3.15 StartY=-1.55 StartZ=0 EndX=-3.15 EndY=1.55 EndZ=0
  constraints (12):
    c: Coincident(g0,g1)
    c: Coincident(g1,g2)
    c: Coincident(g2,g3)
    c: Coincident(g3,g0)
    c: Horizontal(g0)
    c: Horizontal(g2)
    c: Vertical(g1)
    c: Vertical(g3)
    c: PointOnObject(g0,g-4)
    c: PointOnObject(g0,g-3)
    c: DistanceY(g0,g2) = -3.1
    c: Symmetric(g0,g1,g-1)
FEATURE [Part::Extrusion] Extrude273
  Base = -> Sketch225
  Dir = (0,7.7,0)
  Solid = true
FEATURE [Part::Cut] Cut106
  Base = -> Extrude272
  Tool = -> Extrude273
FEATURE [Part::Chamfer] Chamfer031
  Base = -> Cut106
  Edges = 4 edges r=0.5: [Edge7,Edge9,Edge15,Edge17]
FEATURE [Part::Chamfer] Chamfer032
  Base = -> Chamfer031
  Edges = 1 edges r=1.2: [Edge13]
FEATURE [Sketcher::SketchObject] Sketch226
  ExternalGeometry = -> [Chamfer032]
  Placement = pos=(0,0,5.95) rot=(0,0,1;0rad)
  Support = -> Chamfer032 [Face5]
  sketch-geometry (4):
    g0: LineSegment StartX=-3 StartY=0 StartZ=0 EndX=3 EndY=0 EndZ=0
    g1: LineSegment StartX=3 StartY=0 StartZ=0 EndX=3 EndY=-3.1 EndZ=0
    g2: LineSegment StartX=3 StartY=-3.1 StartZ=0 EndX=-3 EndY=-3.1 EndZ=0
    g3: LineSegment StartX=-3 StartY=-3.1 StartZ=0 EndX=-3 EndY=0 EndZ=0
  constraints (12):
    c: Coincident(g0,g1)
    c: Coincident(g1,g2)
    c: Coincident(g2,g3)
    c: Coincident(g3,g0)
    c: Horizontal(g0)
    c: Horizontal(g2)
    c: Vertical(g1)
    c: Vertical(g3)
    c: PointOnObject(g0,g-1)
    c: DistanceX(g-3,g0) = 0.15
    c: Symmetric(g0,g0,g-2)
    c: DistanceY(g0,g1) = -3.1
FEATURE [Part::Extrusion] Extrude274
  Base = -> Sketch226
  Dir = (0,0,6.3)
  Solid = true
FEATURE [Sketcher::SketchObject] Sketch227
  ExternalGeometry = -> [Extrude274]
  Placement = pos=(0,-3.1,0) rot=(1,0,0;1.5708rad)
  Support = -> Extrude274 [Face3]
  sketch-geometry (1):
    g0: Circle CenterX=0 CenterY=9.5 CenterZ=0 NormalX=0 NormalY=0 NormalZ=1 Radius=1.65
  constraints (3):
    c: PointOnObject(g0,g-2)
    c: Radius(g0) = 1.65
    c: DistanceY(g0,g-3) = -3.55
FEATURE [Part::Extrusion] Extrude275
  Base = -> Sketch227
  Dir = (0,6,0)
  Solid = true
FEATURE [Part::Cut] Cut107
  Base = -> Extrude274
  Tool = -> Extrude275
FEATURE [Part::Fillet] Fillet024
  Base = -> Cut107
  Edges = 2 edges r=1.35: [Edge8,Edge11]
FEATURE [Part::MultiFuse] Fusion060
  Shapes = -> [Chamfer032]
FEATURE [Sketcher::SketchObject] Sketch228
  Placement = pos=(0,0,0) rot=(0,0.707107,0.707107;3.14159rad)
  Support = -> Fusion060 [Face7]
  sketch-geometry (4):
    g0: Circle CenterX=-1.27 CenterY=3.8 CenterZ=0 NormalX=0 NormalY=0 NormalZ=1 Radius=0.2
    g1: Circle CenterX=1.27 CenterY=3.8 CenterZ=0 NormalX=0 NormalY=0 NormalZ=1 Radius=0.2
    g2: Circle CenterX=-1.27 CenterY=-3.8 CenterZ=0 NormalX=0 NormalY=0 NormalZ=1 Radius=0.2
    g3: Circle CenterX=1.27 CenterY=-3.8 CenterZ=0 NormalX=0 NormalY=0 NormalZ=1 Radius=0.2
  constraints (9):
    c: Radius(g0) = 0.2
    c: Equal(g0,g1)
    c: Equal(g0,g3)
    c: Equal(g0,g2)
    c: Symmetric(g0,g1,g-2)
    c: Symmetric(g2,g3,g-2)
    c: Symmetric(g0,g2,g-1)
    c: DistanceX(g0,g1) = 2.54
    c: DistanceY(g1,g3) = -7.6
FEATURE [Part::Extrusion] Extrude276
  Base = -> Sketch228
  Dir = (0,7.8,0)
  Solid = true
FEATURE [Part::MultiFuse] Fusion061  label="Capteur_optique_010"
  Placement = pos=(-1287,-46,-20.7) rot=(0,0,1;0rad)
  Shapes = -> [Fusion060,Fillet024,Extrude276]
FEATURE [Sketcher::SketchObject] Sketch229
  Placement = pos=(0,0,0) rot=(1,0,0;1.5708rad)
  sketch-geometry (1):
    g0: Circle CenterX=0 CenterY=0 CenterZ=0 NormalX=0 NormalY=0 NormalZ=1 Radius=4
  constraints (2):
    c: Coincident(g0,g-1)
    c: Radius(g0) = 4
FEATURE [Part::Extrusion] Extrude277
  Base = -> Sketch229
  Dir = (0,50,0)
  Solid = true
FEATURE [Sketcher::SketchObject] Sketch230
  Placement = pos=(0,0,0) rot=(0.57735,0.57735,0.57735;2.0944rad)
  sketch-geometry (1):
    g0: Circle CenterX=6 CenterY=0 CenterZ=0 NormalX=0 NormalY=0 NormalZ=1 Radius=2
  constraints (3):
    c: DistanceX(g-1,g0) = 6
    c: Radius(g0) = 2
    c: PointOnObject(g0,g-1)
FEATURE [Part::Extrusion] Extrude278
  Base = -> Sketch230
  Dir = (4,0,0)
  Solid = true
FEATURE [Part::Extrusion] Extrude279
  Base = -> Sketch230
  Dir = (-4,0,0)
  Solid = true
FEATURE [Part::Cut] Cut108
  Base = -> Extrude277
  Tool = -> Extrude278
FEATURE [Part::Cut] Cut109  label="Axe_D8_010"
  Base = -> Cut108
  Placement = pos=(-1287,-86,0) rot=(0,0,1;0rad)
  Tool = -> Extrude279
FEATURE [Sketcher::SketchObject] Sketch231
  Placement = pos=(0,0,0) rot=(1,0,0;1.5708rad)
  sketch-geometry (1):
    g0: Circle CenterX=0 CenterY=0 CenterZ=0 NormalX=0 NormalY=0 NormalZ=1 Radius=2
  constraints (2):
    c: Coincident(g0,g-1)
    c: Radius(g0) = 2
FEATURE [Part::Extrusion] Extrude280  label="Axe_D4_010"
  Base = -> Sketch231
  Dir = (0,103.6,0)
  Placement = pos=(-1235.2,-80,0) rot=(0,0,1;1.5708rad)
  Solid = true
FEATURE [Sketcher::SketchObject] Sketch232
  Placement = pos=(0,0,0) rot=(1,0,0;1.5708rad)
  sketch-geometry (8):
    g0: LineSegment StartX=-50 StartY=0 StartZ=0 EndX=50 EndY=0 EndZ=0
    g1: LineSegment StartX=50 StartY=0 StartZ=0 EndX=50 EndY=-2 EndZ=0
    g2: LineSegment StartX=50 StartY=-2 StartZ=0 EndX=47 EndY=-2 EndZ=0
    g3: LineSegment StartX=47 StartY=-2 StartZ=0 EndX=44 EndY=-16 EndZ=0
    g4: LineSegment StartX=44 StartY=-16 StartZ=0 EndX=-44 EndY=-16 EndZ=0
    g5: LineSegment StartX=-44 StartY=-16 StartZ=0 EndX=-47 EndY=-2 EndZ=0
    g6: LineSegment StartX=-47 StartY=-2 StartZ=0 EndX=-50 EndY=-2 EndZ=0
    g7: LineSegment StartX=-50 StartY=-2 StartZ=0 EndX=-50 EndY=0 EndZ=0
  constraints (24):
    c: PointOnObject(g0,g-1)
    c: Horizontal(g0)
    c: Coincident(g0,g1)
    c: Vertical(g1)
    c: Coincident(g1,g2)
    c: Horizontal(g2)
    c: Coincident(g2,g3)
    c: Coincident(g3,g4)
    c: Horizontal(g4)
    c: Coincident(g4,g5)
    c: Coincident(g5,g6)
    c: Horizontal(g6)
    c: Coincident(g6,g7)
    c: Coincident(g7,g0)
    c: Vertical(g7)
    c: DistanceY(g0,g6) = -2
    c: DistanceX(g6,g5) = 3
    c: DistanceX(g0,g0) = 100
    c: Symmetric(g0,g0,g-2)
    c: Symmetric(g6,g1,g-2)
    c: Symmetric(g5,g2,g-2)
    c: Symmetric(g4,g3,g-2)
    c: DistanceX(g4,g3) = 88
    c: DistanceY(g0,g4) = -16
FEATURE [Part::Extrusion] Extrude281  label="Plaque_alveolaire_010"
  Base = -> Sketch232
  Dir = (0,2000,0)
  Placement = pos=(-1287,-62,22) rot=(0,0,1;3.14159rad)
  Solid = true
FEATURE [App::DocumentObjectGroup] Groupe012  label="Assemblage_miroir X=-1287_001"
  Group = -> [Cut103,Fusion058,Extrude266,Part__Feature012,Extrude267,Fillet023,Fusion061,Cut109,Extrude280,Extrude281]
FEATURE [Sketcher::SketchObject] Sketch235
  Placement = pos=(0,0,0) rot=(1,0,0;1.5708rad)
  sketch-geometry (10):
    g0: LineSegment StartX=14.1421 StartY=0 StartZ=0 EndX=0 EndY=14.1421 EndZ=0
    g1: LineSegment StartX=0 StartY=14.1421 StartZ=0 EndX=-14.1421 EndY=0 EndZ=0
    g2: LineSegment StartX=-14.1421 StartY=0 StartZ=0 EndX=0 EndY=-14.1421 EndZ=0
    g3: LineSegment StartX=0 StartY=-14.1421 StartZ=0 EndX=14.1421 EndY=0 EndZ=0
    g4: Circle [constr] CenterX=0 CenterY=0 CenterZ=0 NormalX=0 NormalY=0 NormalZ=1 Radius=14.1421
    g5: LineSegment StartX=11.3137 StartY=0 StartZ=0 EndX=0 EndY=11.3137 EndZ=0
    g6: LineSegment StartX=0 StartY=11.3137 StartZ=0 EndX=-11.3137 EndY=0 EndZ=0
    g7: LineSegment StartX=-11.3137 StartY=0 StartZ=0 EndX=0 EndY=-11.3137 EndZ=0
    g8: LineSegment StartX=0 StartY=-11.3137 StartZ=0 EndX=11.3137 EndY=0 EndZ=0
    g9: Circle [constr] CenterX=0 CenterY=0 CenterZ=0 NormalX=0 NormalY=0 NormalZ=1 Radius=11.3137
  constraints (30):
    c: Coincident(g0,g1)
    c: Coincident(g1,g2)
    c: Coincident(g2,g3)
    c: Coincident(g3,g0)
    c: Equal(g0,g1)
    c: Equal(g0,g2)
    c: Equal(g0,g3)
    c: PointOnObject(g0,g4)
    c: PointOnObject(g1,g4)
    c: PointOnObject(g2,g4)
    c: PointOnObject(g3,g4)
    c: Coincident(g1,g-1)
    c: Coincident(g5,g6)
    c: Coincident(g6,g7)
    c: Coincident(g7,g8)
    c: Coincident(g8,g5)
    c: Equal(g5,g6)
    c: Equal(g5,g7)
    c: Equal(g5,g8)
    c: PointOnObject(g5,g9)
    c: PointOnObject(g6,g9)
    c: PointOnObject(g7,g9)
    c: PointOnObject(g8,g9)
    c: Coincident(g6,g-1)
    c: Distance(g0,g1) = 20
    c: Coincident(g4,g-1)
    c: Coincident(g9,g-1)
    c: PointOnObject(g0,g-1)
    c: PointOnObject(g5,g-1)
    c: Distance(g5,g5) = 16
FEATURE [Part::Extrusion] Extrude286  label="Poutre_centrale_20x20x2_L2200"
  Base = -> Sketch235
  Dir = (0,2200,0)
  Placement = pos=(-1358.5,0,1000) rot=(0,0,1;3.14159rad)
  Solid = true
FEATURE [Sketcher::SketchObject] Sketch236
  Placement = pos=(0,0,0) rot=(1,0,0;1.5708rad)
  sketch-geometry (5):
    g0: LineSegment StartX=10 StartY=10 StartZ=0 EndX=-10 EndY=10 EndZ=0
    g1: LineSegment StartX=-10 StartY=10 StartZ=0 EndX=-10 EndY=-10 EndZ=0
    g2: LineSegment StartX=-10 StartY=-10 StartZ=0 EndX=10 EndY=-10 EndZ=0
    g3: LineSegment StartX=10 StartY=-10 StartZ=0 EndX=10 EndY=10 EndZ=0
    g4: Circle [constr] CenterX=0 CenterY=0 CenterZ=0 NormalX=0 NormalY=0 NormalZ=1 Radius=14.1421
  constraints (15):
    c: Coincident(g0,g1)
    c: Coincident(g1,g2)
    c: Coincident(g2,g3)
    c: Coincident(g3,g0)
    c: Equal(g0,g1)
    c: Equal(g0,g2)
    c: Equal(g0,g3)
    c: PointOnObject(g0,g4)
    c: PointOnObject(g1,g4)
    c: PointOnObject(g2,g4)
    c: PointOnObject(g3,g4)
    c: Coincident(g1,g-1)
    c: Horizontal(g0)
    c: DistanceX(g0,g0) = 20
    c: Coincident(g4,g-1)
FEATURE [Part::Extrusion] Extrude287
  Base = -> Sketch236
  Dir = (0,10,0)
  Solid = true
FEATURE [Part::Extrusion] Extrude288
  Base = -> Sketch236
  Dir = (0,-10,0)
  Solid = true
FEATURE [Part::MultiFuse] Fusion062
  Shapes = -> [Extrude287,Extrude288]
FEATURE [Sketcher::SketchObject] Sketch237
  Placement = pos=(0,-10,0) rot=(1,0,0;1.5708rad)
  Support = -> Fusion062 [Face10]
  sketch-geometry (5):
    g0: LineSegment StartX=8 StartY=-8 StartZ=0 EndX=8 EndY=8 EndZ=0
    g1: LineSegment StartX=8 StartY=8 StartZ=0 EndX=-8 EndY=8 EndZ=0
    g2: LineSegment StartX=-8 StartY=8 StartZ=0 EndX=-8 EndY=-8 EndZ=0
    g3: LineSegment StartX=-8 StartY=-8 StartZ=0 EndX=8 EndY=-8 EndZ=0
    g4: Circle [constr] CenterX=0 CenterY=0 CenterZ=0 NormalX=0 NormalY=0 NormalZ=1 Radius=11.3137
  constraints (15):
    c: Coincident(g0,g1)
    c: Coincident(g1,g2)
    c: Coincident(g2,g3)
    c: Coincident(g3,g0)
    c: Equal(g0,g1)
    c: Equal(g0,g2)
    c: Equal(g0,g3)
    c: PointOnObject(g0,g4)
    c: PointOnObject(g1,g4)
    c: PointOnObject(g2,g4)
    c: PointOnObject(g3,g4)
    c: Coincident(g1,g-1)
    c: Coincident(g4,g-1)
    c: Horizontal(g1)
    c: DistanceX(g1,g0) = 16
FEATURE [Part::Extrusion] Extrude289
  Base = -> Sketch237
  Dir = (0,-25,0)
  Solid = true
FEATURE [Sketcher::SketchObject] Sketch238
  Placement = pos=(10,0,0) rot=(0.57735,0.57735,0.57735;2.0944rad)
  Support = -> Fusion062 [Face9]
  sketch-geometry (5):
    g0: LineSegment StartX=8 StartY=-8 StartZ=0 EndX=8 EndY=8 EndZ=0
    g1: LineSegment StartX=8 StartY=8 StartZ=0 EndX=-8 EndY=8 EndZ=0
    g2: LineSegment StartX=-8 StartY=8 StartZ=0 EndX=-8 EndY=-8 EndZ=0
    g3: LineSegment StartX=-8 StartY=-8 StartZ=0 EndX=8 EndY=-8 EndZ=0
    g4: Circle [constr] CenterX=0 CenterY=0 CenterZ=0 NormalX=0 NormalY=0 NormalZ=1 Radius=11.3137
  constraints (15):
    c: Coincident(g0,g1)
    c: Coincident(g1,g2)
    c: Coincident(g2,g3)
    c: Coincident(g3,g0)
    c: Equal(g0,g1)
    c: Equal(g0,g2)
    c: Equal(g0,g3)
    c: PointOnObject(g0,g4)
    c: PointOnObject(g1,g4)
    c: PointOnObject(g2,g4)
    c: PointOnObject(g3,g4)
    c: Coincident(g1,g-1)
    c: Horizontal(g1)
    c: DistanceX(g1,g0) = 16
    c: Coincident(g4,g-1)
FEATURE [Part::Extrusion] Extrude290
  Base = -> Sketch238
  Dir = (25,0,0)
  Solid = true
FEATURE [Sketcher::SketchObject] Sketch239
  Placement = pos=(0,0,10) rot=(0,0,1;0rad)
  Support = -> Fusion062 [Face6]
  sketch-geometry (5):
    g0: LineSegment StartX=8 StartY=-8 StartZ=0 EndX=8 EndY=8 EndZ=0
    g1: LineSegment StartX=8 StartY=8 StartZ=0 EndX=-8 EndY=8 EndZ=0
    g2: LineSegment StartX=-8 StartY=8 StartZ=0 EndX=-8 EndY=-8 EndZ=0
    g3: LineSegment StartX=-8 StartY=-8 StartZ=0 EndX=8 EndY=-8 EndZ=0
    g4: Circle [constr] CenterX=0 CenterY=0 CenterZ=0 NormalX=0 NormalY=0 NormalZ=1 Radius=11.3137
  constraints (15):
    c: Coincident(g0,g1)
    c: Coincident(g1,g2)
    c: Coincident(g2,g3)
    c: Coincident(g3,g0)
    c: Equal(g0,g1)
    c: Equal(g0,g2)
    c: Equal(g0,g3)
    c: PointOnObject(g0,g4)
    c: PointOnObject(g1,g4)
    c: PointOnObject(g2,g4)
    c: PointOnObject(g3,g4)
    c: Coincident(g1,g-1)
    c: Horizontal(g1)
    c: DistanceX(g1,g0) = 16
    c: Coincident(g4,g-1)
FEATURE [Part::Extrusion] Extrude291
  Base = -> Sketch239
  Dir = (0,0,25)
  Solid = true
FEATURE [Part::MultiFuse] Fusion063  label="Raccord"
  Placement = pos=(-1358.5,10,1000) rot=(0,1,0;2.35619rad)
  Shapes = -> [Fusion062,Extrude289,Extrude290,Extrude291]
FEATURE [Sketcher::SketchObject] Sketch240
  Placement = pos=(0,0,0) rot=(1,0,0;1.5708rad)
  sketch-geometry (4):
    g0: LineSegment StartX=-88 StartY=4 StartZ=0 EndX=88 EndY=4 EndZ=0
    g1: LineSegment StartX=88 StartY=4 StartZ=0 EndX=88 EndY=-4 EndZ=0
    g2: LineSegment StartX=88 StartY=-4 StartZ=0 EndX=-88 EndY=-4 EndZ=0
    g3: LineSegment StartX=-88 StartY=-4 StartZ=0 EndX=-88 EndY=4 EndZ=0
  constraints (12):
    c: Coincident(g0,g1)
    c: Coincident(g1,g2)
    c: Coincident(g2,g3)
    c: Coincident(g3,g0)
    c: Horizontal(g0)
    c: Horizontal(g2)
    c: Vertical(g1)
    c: Vertical(g3)
    c: DistanceX(g0,g0) = 176
    c: DistanceY(g0,g2) = -8
    c: Symmetric(g0,g0,g-2)
    c: Symmetric(g0,g2,g-1)
FEATURE [Part::Extrusion] Extrude292  label="Vitre"
  Base = -> Sketch240
  Dir = (0,2150,0)
  Placement = pos=(-1358.5,0,900) rot=(0,0,1;3.14159rad)
  Solid = true
FEATURE [App::DocumentObjectGroup] Groupe014  label="Assemblage_absorbeur"
  Group = -> [Extrude286,Fusion063,Extrude292]
FEATURE [Sketcher::SketchObject] Sketch241
  Placement = pos=(0,0,0) rot=(1,0,0;1.5708rad)
  sketch-geometry (8):
    g0: LineSegment StartX=-21.15 StartY=16.15 StartZ=0 EndX=-16.15 EndY=21.15 EndZ=0
    g1: LineSegment StartX=-16.15 StartY=21.15 StartZ=0 EndX=16.15 EndY=21.15 EndZ=0
    g2: LineSegment StartX=16.15 StartY=21.15 StartZ=0 EndX=21.15 EndY=16.15 EndZ=0
    g3: LineSegment StartX=21.15 StartY=16.15 StartZ=0 EndX=21.15 EndY=-16.15 EndZ=0
    g4: LineSegment StartX=21.15 StartY=-16.15 StartZ=0 EndX=16.15 EndY=-21.15 EndZ=0
    g5: LineSegment StartX=16.15 StartY=-21.15 StartZ=0 EndX=-16.15 EndY=-21.15 EndZ=0
    g6: LineSegment StartX=-16.15 StartY=-21.15 StartZ=0 EndX=-21.15 EndY=-16.15 EndZ=0
    g7: LineSegment StartX=-21.15 StartY=-16.15 StartZ=0 EndX=-21.15 EndY=16.15 EndZ=0
  constraints (21):
    c: Coincident(g0,g1)
    c: Horizontal(g1)
    c: Coincident(g1,g2)
    c: Coincident(g2,g3)
    c: Vertical(g3)
    c: Coincident(g3,g4)
    c: Coincident(g4,g5)
    c: Horizontal(g5)
    c: Coincident(g5,g6)
    c: Coincident(g6,g7)
    c: Coincident(g7,g0)
    c: Angle(g7,g0) = 2.35619
    c: Distance(g0,g7) = 5
    c: Distance(g2,g7) = 42.3
    c: Distance(g5,g1) = 42.3
    c: Symmetric(g6,g3,g-2)
    c: Symmetric(g5,g4,g-2)
    c: Symmetric(g0,g2,g-2)
    c: Symmetric(g0,g1,g-2)
    c: Symmetric(g0,g6,g-1)
    c: Symmetric(g0,g5,g-1)
FEATURE [Part::Extrusion] Extrude293
  Base = -> Sketch241
  Dir = (0,48,0)
  Solid = true
FEATURE [Sketcher::SketchObject] Sketch242
  Placement = pos=(0,0,0) rot=(1,0,0;1.5708rad)
  Support = -> Extrude293 [Face9]
  sketch-geometry (1):
    g0: Circle CenterX=0 CenterY=0 CenterZ=0 NormalX=0 NormalY=0 NormalZ=1 Radius=11
  constraints (2):
    c: Coincident(g0,g-1)
    c: Radius(g0) = 11
FEATURE [Part::Extrusion] Extrude294
  Base = -> Sketch242
  Dir = (0,-2,0)
  Solid = true
FEATURE [Sketcher::SketchObject] Sketch243
  Placement = pos=(0,-2,0) rot=(1,0,0;1.5708rad)
  Support = -> Extrude294 [Face3]
  sketch-geometry (1):
    g0: Circle CenterX=0 CenterY=0 CenterZ=0 NormalX=0 NormalY=0 NormalZ=1 Radius=2.5
  constraints (2):
    c: Coincident(g0,g-1)
    c: Radius(g0) = 2.5
FEATURE [Part::Extrusion] Extrude295
  Base = -> Sketch243
  Dir = (0,-22,0)
  Solid = true
FEATURE [Part::Chamfer] Chamfer033
  Base = -> Extrude295
  Edges = 1 edges r=0.8: [Edge3]
FEATURE [Sketcher::SketchObject] Sketch244
  Placement = pos=(0,0,0) rot=(1,0,0;1.5708rad)
  Support = -> Extrude293 [Face9]
  sketch-geometry (4):
    g0: Circle CenterX=-15.5 CenterY=15.5 CenterZ=0 NormalX=0 NormalY=0 NormalZ=1 Radius=2
    g1: Circle CenterX=15.5 CenterY=15.5 CenterZ=0 NormalX=0 NormalY=0 NormalZ=1 Radius=2
    g2: Circle CenterX=-15.5 CenterY=-15.5 CenterZ=0 NormalX=0 NormalY=0 NormalZ=1 Radius=2
    g3: Circle CenterX=15.5 CenterY=-15.5 CenterZ=0 NormalX=0 NormalY=0 NormalZ=1 Radius=2
  constraints (9):
    c: Distance(g0,g1) = 31
    c: Distance(g0,g2) = 31
    c: Symmetric(g0,g2,g-1)
    c: Symmetric(g0,g1,g-2)
    c: Symmetric(g2,g3,g-2)
    c: Radius(g0) = 2
    c: Equal(g0,g1)
    c: Equal(g0,g2)
    c: Equal(g0,g3)
FEATURE [Part::Extrusion] Extrude296
  Base = -> Sketch244
  Dir = (0,4.5,0)
  Solid = true
FEATURE [Part::Cut] Cut110
  Base = -> Extrude293
  Tool = -> Extrude296
FEATURE [Sketcher::SketchObject] Sketch245
  Placement = pos=(0,0,0) rot=(1,0,0;1.5708rad)
  sketch-geometry (1):
    g0: Circle CenterX=0 CenterY=0 CenterZ=0 NormalX=0 NormalY=0 NormalZ=1 Radius=9
  constraints (2):
    c: Coincident(g0,g-1)
    c: Radius(g0) = 9
FEATURE [Part::Extrusion] Extrude297
  Base = -> Sketch245
  Dir = (0,25,0)
  Solid = true
FEATURE [Sketcher::SketchObject] Sketch246
  Placement = pos=(0,0,0) rot=(1,0,0;1.5708rad)
  sketch-geometry (1):
    g0: Circle CenterX=0 CenterY=0 CenterZ=0 NormalX=0 NormalY=0 NormalZ=1 Radius=2.5
  constraints (2):
    c: Coincident(g0,g-1)
    c: Radius(g0) = 2.5
FEATURE [Part::Extrusion] Extrude298
  Base = -> Sketch246
  Dir = (0,10,0)
  Solid = true
FEATURE [Part::Cut] Cut111
  Base = -> Extrude297
  Tool = -> Extrude298
FEATURE [Sketcher::SketchObject] Sketch247
  Placement = pos=(0,25,0) rot=(0,0.707107,0.707107;3.14159rad)
  Support = -> Cut111 [Face3]
  sketch-geometry (1):
    g0: Circle CenterX=0 CenterY=0 CenterZ=0 NormalX=0 NormalY=0 NormalZ=1 Radius=4
  constraints (2):
    c: Coincident(g0,g-1)
    c: Radius(g0) = 4
FEATURE [Part::Extrusion] Extrude299
  Base = -> Sketch247
  Dir = (0,-10,0)
  Solid = true
FEATURE [Part::Cut] Cut112  label="Accouplement_011"
  Base = -> Cut111
  Placement = pos=(-1430,-12,0) rot=(1,0,0;3.14159rad)
  Tool = -> Extrude299
FEATURE [Part::Fuse] Fusion064
  Base = -> Extrude294
  Tool = -> Cut110
FEATURE [Part::Fuse] Fusion065  label="Moteur_011"
  Base = -> Chamfer033
  Placement = pos=(-1430,0,0) rot=(0,0,1;0rad)
  Tool = -> Fusion064
FEATURE [Sketcher::SketchObject] Sketch248
  Placement = pos=(0,0,0) rot=(1,0,0;1.5708rad)
  sketch-geometry (4):
    g0: LineSegment StartX=-50 StartY=0 StartZ=0 EndX=-47 EndY=0 EndZ=0
    g1: LineSegment StartX=47 StartY=0 StartZ=0 EndX=50 EndY=0 EndZ=0
    g2: ArcOfCircle CenterX=0 CenterY=0 CenterZ=0 NormalX=0 NormalY=0 NormalZ=1 Radius=47 StartAngle=3.14159 EndAngle=6.28319
    g3: ArcOfCircle CenterX=0 CenterY=0 CenterZ=0 NormalX=0 NormalY=0 NormalZ=1 Radius=50 StartAngle=3.14159 EndAngle=6.28319
  constraints (13):
    c: Horizontal(g0)
    c: PointOnObject(g1,g-1)
    c: Horizontal(g1)
    c: Coincident(g2,g-1)
    c: PointOnObject(g2,g-1)
    c: Coincident(g3,g-1)
    c: Coincident(g3,g1)
    c: PointOnObject(g3,g-1)
    c: Coincident(g0,g3)
    c: Coincident(g0,g2)
    c: Distance(g0,g1) = 100
    c: Distance(g0,g0) = 3
    c: Coincident(g1,g2)
FEATURE [Part::Extrusion] Extrude300  label="Demi_tube_sous_miroir_011"
  Base = -> Sketch248
  Dir = (0,2000,0)
  Placement = pos=(-1430,-62,20) rot=(0,0,1;3.14159rad)
  Solid = true
FEATURE [Part::Feature] Part__Feature013  label="Coussinet_autolub_C2-151-8-128_011"
  Placement = pos=(-1430,-46,0) rot=(0,0,1;1.5708rad)
  shape: bbox 16 x 8 x 16 mm, 12 faces (baked)
FEATURE [Sketcher::SketchObject] Sketch249
  Placement = pos=(0,0,0) rot=(1,0,0;1.5708rad)
  sketch-geometry (21):
    g0: Circle CenterX=0 CenterY=0 CenterZ=0 NormalX=0 NormalY=0 NormalZ=1 Radius=6
    g1: LineSegment StartX=-20.5 StartY=15 StartZ=0 EndX=20.5 EndY=15 EndZ=0
    g2: ArcOfCircle CenterX=20.5 CenterY=13 CenterZ=0 NormalX=0 NormalY=0 NormalZ=1 Radius=2 StartAngle=6.28319 EndAngle=7.85398
    g3: LineSegment StartX=22.5 StartY=13 StartZ=0 EndX=22.5 EndY=-73 EndZ=0
    g4: LineSegment StartX=-22.5 StartY=13 StartZ=0 EndX=-22.5 EndY=-73 EndZ=0
    g5: ArcOfCircle CenterX=-20.5 CenterY=13 CenterZ=0 NormalX=0 NormalY=0 NormalZ=1 Radius=2 StartAngle=1.5708 EndAngle=3.14159
    g6: ArcOfCircle CenterX=-20.5 CenterY=-73 CenterZ=0 NormalX=0 NormalY=0 NormalZ=1 Radius=2 StartAngle=3.14159 EndAngle=4.71239
    g7: ArcOfCircle CenterX=20.5 CenterY=-73 CenterZ=0 NormalX=0 NormalY=0 NormalZ=1 Radius=2 StartAngle=4.71239 EndAngle=6.28319
    g8: LineSegment StartX=-20.5 StartY=-75 StartZ=0 EndX=20.5 EndY=-75 EndZ=0
    g9: ArcOfCircle CenterX=0 CenterY=-16.7 CenterZ=0 NormalX=0 NormalY=0 NormalZ=1 Radius=1.5 StartAngle=0 EndAngle=3.14159
    g10: ArcOfCircle CenterX=0 CenterY=-24.3 CenterZ=0 NormalX=0 NormalY=0 NormalZ=1 Radius=1.5 StartAngle=3.14159 EndAngle=6.28319
    g11: LineSegment StartX=-1.5 StartY=-16.7 StartZ=0 EndX=-1.5 EndY=-24.3 EndZ=0
    g12: LineSegment StartX=1.5 StartY=-16.7 StartZ=0 EndX=1.5 EndY=-24.3 EndZ=0
    g13: Circle CenterX=-12.5 CenterY=-45 CenterZ=0 NormalX=0 NormalY=0 NormalZ=1 Radius=3.5
    g14: Circle CenterX=12.5 CenterY=-45 CenterZ=0 NormalX=0 NormalY=0 NormalZ=1 Radius=3.5
    g15: Circle CenterX=-12.5 CenterY=-65 CenterZ=0 NormalX=0 NormalY=0 NormalZ=1 Radius=3.5
    g16: Circle CenterX=12.5 CenterY=-65 CenterZ=0 NormalX=0 NormalY=0 NormalZ=1 Radius=3.5
    g17: LineSegment [constr] StartX=-12.5 StartY=-45 StartZ=0 EndX=12.5 EndY=-45 EndZ=0
    g18: LineSegment [constr] StartX=-12.5 StartY=-45 StartZ=0 EndX=-12.5 EndY=-65 EndZ=0
    g19: LineSegment [constr] StartX=-12.5 StartY=-65 StartZ=0 EndX=12.5 EndY=-65 EndZ=0
    g20: LineSegment [constr] StartX=12.5 StartY=-45 StartZ=0 EndX=12.5 EndY=-65 EndZ=0
  constraints (59):
    c: Coincident(g0,g-1)
    c: Radius(g0) = 6
    c: Horizontal(g1)
    c: Coincident(g2,g1)
    c: Coincident(g3,g2)
    c: Vertical(g3)
    c: Vertical(g4)
    c: Coincident(g5,g1)
    c: Coincident(g5,g4)
    c: Coincident(g7,g3)
    c: Coincident(g8,g6)
    c: Coincident(g8,g7)
    c: Tangent(g8,g7)
    c: Tangent(g5,g4)
    c: Tangent(g5,g1)
    c: Tangent(g1,g2)
    c: Tangent(g2,g3)
    c: Coincident(g4,g6)
    c: Tangent(g6,g4)
    c: Tangent(g6,g8)
    c: Horizontal(g8)
    c: Tangent(g7,g3)
    c: Distance(g4,g2) = 45
    c: Symmetric(g4,g2,g-2)
    c: Distance(g1,g6) = 90
    c: DistanceY(g-1,g1) = 15
    c: Tangent(g9,g12) = 1.5708
    c: Tangent(g9,g11) = -1.5708
    c: Tangent(g11,g10) = -1.5708
    c: Tangent(g12,g10) = 1.5708
    c: Vertical(g11)
    c: Equal(g9,g10)
    c: PointOnObject(g9,g-2)
    c: Distance(g-1,g9) = 16.7
    c: Distance(g9,g10) = 7.6
    c: Radius(g9) = 1.5
    c: Radius(g13) = 3.5
    c: Equal(g13,g14)
    c: Equal(g13,g16)
    c: Equal(g13,g15)
    c: Radius(g5) = 2
    c: Equal(g5,g7)
    c: Equal(g5,g6)
    c: DistanceY(g-1,g13) = -45
    c: Coincident(g17,g13)
    c: Coincident(g17,g14)
    c: Horizontal(g17)
    c: Coincident(g18,g13)
    c: Coincident(g18,g15)
    c: Coincident(g19,g15)
    c: Coincident(g19,g16)
    c: Horizontal(g19)
    c: Coincident(g20,g14)
    c: Coincident(g20,g16)
    c: Vertical(g18)
    c: Vertical(g20)
    c: Distance(g13,g15) = 20
    c: Distance(g13,g14) = 25
    c: Symmetric(g13,g14,g-2)
FEATURE [Part::Extrusion] Extrude301  label="Plaque_support_011"
  Base = -> Sketch249
  Dir = (0,6,0)
  Placement = pos=(-1430,-46,0) rot=(0,0,1;0rad)
  Solid = true
FEATURE [Sketcher::SketchObject] Sketch250
  Placement = pos=(0,0,0) rot=(0.57735,0.57735,0.57735;2.0944rad)
  sketch-geometry (8):
    g0: LineSegment StartX=0 StartY=33 StartZ=0 EndX=-2 EndY=33 EndZ=0
    g1: LineSegment StartX=-2 StartY=33 StartZ=0 EndX=-2 EndY=-24 EndZ=0
    g2: ArcOfCircle CenterX=-4 CenterY=-24 CenterZ=0 NormalX=0 NormalY=0 NormalZ=1 Radius=2 StartAngle=4.71239 EndAngle=6.28319
    g3: LineSegment StartX=-4 StartY=-26 StartZ=0 EndX=-38 EndY=-26 EndZ=0
    g4: LineSegment StartX=-38 StartY=-26 StartZ=0 EndX=-38 EndY=-28 EndZ=0
    g5: LineSegment StartX=-38 StartY=-28 StartZ=0 EndX=-4 EndY=-28 EndZ=0
    g6: ArcOfCircle CenterX=-4 CenterY=-24 CenterZ=0 NormalX=0 NormalY=0 NormalZ=1 Radius=4 StartAngle=4.71239 EndAngle=6.28319
    g7: LineSegment StartX=0 StartY=-24 StartZ=0 EndX=0 EndY=33 EndZ=0
  constraints (22):
    c: PointOnObject(g0,g-2)
    c: Horizontal(g0)
    c: Coincident(g0,g1)
    c: Vertical(g1)
    c: Tangent(g1,g2) = 1.5708
    c: Tangent(g2,g3) = 1.5708
    c: Coincident(g3,g4)
    c: Vertical(g4)
    c: Coincident(g4,g5)
    c: Horizontal(g5)
    c: Tangent(g5,g6) = -1.5708
    c: PointOnObject(g6,g-2)
    c: Tangent(g6,g7) = -1.5708
    c: Coincident(g7,g0)
    c: Horizontal(g3)
    c: DistanceX(g0,g0) = 2
    c: Radius(g2) = 2
    c: Radius(g6) = 4
    c: DistanceY(g3,g4) = -2
    c: Distance(g-1,g0) = 33
    c: DistanceY(g-1,g5) = -28
    c: DistanceX(g6,g4) = -38
FEATURE [Part::Extrusion] Extrude302
  Base = -> Sketch250
  Dir = (-32.5,0,0)
  Solid = true
FEATURE [Part::Extrusion] Extrude303
  Base = -> Sketch250
  Dir = (32.5,0,0)
  Solid = true
FEATURE [Part::MultiFuse] Fusion066
  Shapes = -> [Extrude302,Extrude303]
FEATURE [Sketcher::SketchObject] Sketch251
  Placement = pos=(0,-2,0) rot=(1,0,0;1.5708rad)
  Support = -> Fusion066 [Face3]
  sketch-geometry (9):
    g0: ArcOfCircle CenterX=0 CenterY=0 CenterZ=0 NormalX=0 NormalY=0 NormalZ=1 Radius=32.5 StartAngle=0 EndAngle=3.14159
    g1: LineSegment StartX=-32.5 StartY=0 StartZ=0 EndX=-32.5 EndY=34 EndZ=0
    g2: LineSegment StartX=-32.5 StartY=34 StartZ=0 EndX=32.5 EndY=34 EndZ=0
    g3: LineSegment StartX=32.5 StartY=34 StartZ=0 EndX=32.5 EndY=0 EndZ=0
    g4: Circle CenterX=0 CenterY=0 CenterZ=0 NormalX=0 NormalY=0 NormalZ=1 Radius=11
    g5: Circle CenterX=-15.5 CenterY=15.5 CenterZ=0 NormalX=0 NormalY=0 NormalZ=1 Radius=2
    g6: Circle CenterX=15.5 CenterY=15.5 CenterZ=0 NormalX=0 NormalY=0 NormalZ=1 Radius=2
    g7: Circle CenterX=-15.5 CenterY=-15.5 CenterZ=0 NormalX=0 NormalY=0 NormalZ=1 Radius=2
    g8: Circle CenterX=15.5 CenterY=-15.5 CenterZ=0 NormalX=0 NormalY=0 NormalZ=1 Radius=2
  constraints (23):
    c: Coincident(g0,g-1)
    c: PointOnObject(g0,g-1)
    c: PointOnObject(g0,g-1)
    c: Coincident(g1,g0)
    c: Vertical(g1)
    c: Coincident(g1,g2)
    c: Horizontal(g2)
    c: Coincident(g2,g3)
    c: Coincident(g3,g0)
    c: Vertical(g3)
    c: DistanceY(g1,g0) = -34
    c: Coincident(g4,g-1)
    c: Radius(g4) = 11
    c: DistanceX(g1,g2) = 65
    c: Radius(g5) = 2
    c: Equal(g5,g6)
    c: Equal(g5,g8)
    c: Equal(g5,g7)
    c: Symmetric(g5,g6,g-2)
    c: Symmetric(g5,g7,g-1)
    c: Symmetric(g7,g8,g-2)
    c: DistanceX(g5,g6) = 31
    c: DistanceY(g5,g7) = -31
FEATURE [Part::Extrusion] Extrude304
  Base = -> Sketch251
  Dir = (0,2,0)
  Solid = true
FEATURE [Part::Cut] Cut113
  Base = -> Fusion066
  Tool = -> Extrude304
FEATURE [Sketcher::SketchObject] Sketch252
  ExternalGeometry = -> [Cut113]
  Placement = pos=(0,0,-26) rot=(0,0,1;0rad)
  Support = -> Cut113 [Face5]
  sketch-geometry (5):
    g0: Circle CenterX=-25 CenterY=-12 CenterZ=0 NormalX=0 NormalY=0 NormalZ=1 Radius=3.5
    g1: Circle CenterX=-25 CenterY=-30 CenterZ=0 NormalX=0 NormalY=0 NormalZ=1 Radius=3.5
    g2: Circle CenterX=25 CenterY=-12 CenterZ=0 NormalX=0 NormalY=0 NormalZ=1 Radius=3.5
    g3: Circle CenterX=25 CenterY=-30 CenterZ=0 NormalX=0 NormalY=0 NormalZ=1 Radius=3.5
    g4: LineSegment [constr] StartX=-25 StartY=-12 StartZ=0 EndX=-25 EndY=-30 EndZ=0
  constraints (12):
    c: Radius(g0) = 3.5
    c: Equal(g0,g2)
    c: Equal(g0,g3)
    c: Equal(g0,g1)
    c: Symmetric(g0,g2,g-2)
    c: Symmetric(g1,g3,g-2)
    c: Coincident(g4,g0)
    c: Coincident(g4,g1)
    c: Vertical(g4)
    c: DistanceY(g0,g1) = -18
    c: DistanceY(g-3,g1) = 8
    c: DistanceX(g0,g2) = 50
FEATURE [Part::Extrusion] Extrude305
  Base = -> Sketch252
  Dir = (0,0,-2)
  Solid = true
FEATURE [Part::Cut] Cut114
  Base = -> Cut113
  Tool = -> Extrude305
FEATURE [Part::Fillet] Fillet025  label="Plaque_moteur_011"
  Base = -> Cut114
  Edges = 2 edges r=4: [Edge5,Edge59]
  Placement = pos=(-1430,0,0) rot=(0,0,1;0rad)
FEATURE [Sketcher::SketchObject] Sketch253
  Placement = pos=(0,0,0) rot=(1,0,0;1.5708rad)
  sketch-geometry (4):
    g0: LineSegment StartX=-3.15 StartY=5.95 StartZ=0 EndX=3.15 EndY=5.95 EndZ=0
    g1: LineSegment StartX=3.15 StartY=5.95 StartZ=0 EndX=3.15 EndY=-5.95 EndZ=0
    g2: LineSegment StartX=3.15 StartY=-5.95 StartZ=0 EndX=-3.15 EndY=-5.95 EndZ=0
    g3: LineSegment StartX=-3.15 StartY=-5.95 StartZ=0 EndX=-3.15 EndY=5.95 EndZ=0
  constraints (12):
    c: Coincident(g0,g1)
    c: Coincident(g1,g2)
    c: Coincident(g2,g3)
    c: Coincident(g3,g0)
    c: Horizontal(g0)
    c: Horizontal(g2)
    c: Vertical(g1)
    c: Vertical(g3)
    c: DistanceX(g0,g0) = 6.3
    c: DistanceY(g0,g2) = -11.9
    c: Symmetric(g0,g0,g-2)
    c: Symmetric(g0,g1,g-1)
FEATURE [Part::Extrusion] Extrude306
  Base = -> Sketch253
  Dir = (0,-10.8,0)
  Solid = true
FEATURE [Sketcher::SketchObject] Sketch254
  ExternalGeometry = -> [Extrude306]
  Placement = pos=(0,-10.8,0) rot=(1,0,0;1.5708rad)
  Support = -> Extrude306 [Face6]
  sketch-geometry (4):
    g0: LineSegment StartX=-3.15 StartY=1.55 StartZ=0 EndX=3.15 EndY=1.55 EndZ=0
    g1: LineSegment StartX=3.15 StartY=1.55 StartZ=0 EndX=3.15 EndY=-1.55 EndZ=0
    g2: LineSegment StartX=3.15 StartY=-1.55 StartZ=0 EndX=-3.15 EndY=-1.55 EndZ=0
    g3: LineSegment StartX=-3.15 StartY=-1.55 StartZ=0 EndX=-3.15 EndY=1.55 EndZ=0
  constraints (12):
    c: Coincident(g0,g1)
    c: Coincident(g1,g2)
    c: Coincident(g2,g3)
    c: Coincident(g3,g0)
    c: Horizontal(g0)
    c: Horizontal(g2)
    c: Vertical(g1)
    c: Vertical(g3)
    c: PointOnObject(g0,g-4)
    c: PointOnObject(g0,g-3)
    c: DistanceY(g0,g2) = -3.1
    c: Symmetric(g0,g1,g-1)
FEATURE [Part::Extrusion] Extrude307
  Base = -> Sketch254
  Dir = (0,7.7,0)
  Solid = true
FEATURE [Part::Cut] Cut115
  Base = -> Extrude306
  Tool = -> Extrude307
FEATURE [Part::Chamfer] Chamfer034
  Base = -> Cut115
  Edges = 4 edges r=0.5: [Edge7,Edge9,Edge15,Edge17]
FEATURE [Part::Chamfer] Chamfer035
  Base = -> Chamfer034
  Edges = 1 edges r=1.2: [Edge13]
FEATURE [Sketcher::SketchObject] Sketch255
  ExternalGeometry = -> [Chamfer035]
  Placement = pos=(0,0,5.95) rot=(0,0,1;0rad)
  Support = -> Chamfer035 [Face5]
  sketch-geometry (4):
    g0: LineSegment StartX=-3 StartY=0 StartZ=0 EndX=3 EndY=0 EndZ=0
    g1: LineSegment StartX=3 StartY=0 StartZ=0 EndX=3 EndY=-3.1 EndZ=0
    g2: LineSegment StartX=3 StartY=-3.1 StartZ=0 EndX=-3 EndY=-3.1 EndZ=0
    g3: LineSegment StartX=-3 StartY=-3.1 StartZ=0 EndX=-3 EndY=0 EndZ=0
  constraints (12):
    c: Coincident(g0,g1)
    c: Coincident(g1,g2)
    c: Coincident(g2,g3)
    c: Coincident(g3,g0)
    c: Horizontal(g0)
    c: Horizontal(g2)
    c: Vertical(g1)
    c: Vertical(g3)
    c: PointOnObject(g0,g-1)
    c: DistanceX(g-3,g0) = 0.15
    c: Symmetric(g0,g0,g-2)
    c: DistanceY(g0,g1) = -3.1
FEATURE [Part::Extrusion] Extrude308
  Base = -> Sketch255
  Dir = (0,0,6.3)
  Solid = true
FEATURE [Sketcher::SketchObject] Sketch256
  ExternalGeometry = -> [Extrude308]
  Placement = pos=(0,-3.1,0) rot=(1,0,0;1.5708rad)
  Support = -> Extrude308 [Face3]
  sketch-geometry (1):
    g0: Circle CenterX=0 CenterY=9.5 CenterZ=0 NormalX=0 NormalY=0 NormalZ=1 Radius=1.65
  constraints (3):
    c: PointOnObject(g0,g-2)
    c: Radius(g0) = 1.65
    c: DistanceY(g0,g-3) = -3.55
FEATURE [Part::Extrusion] Extrude309
  Base = -> Sketch256
  Dir = (0,6,0)
  Solid = true
FEATURE [Part::Cut] Cut116
  Base = -> Extrude308
  Tool = -> Extrude309
FEATURE [Part::Fillet] Fillet026
  Base = -> Cut116
  Edges = 2 edges r=1.35: [Edge8,Edge11]
FEATURE [Part::MultiFuse] Fusion067
  Shapes = -> [Chamfer035]
FEATURE [Sketcher::SketchObject] Sketch257
  Placement = pos=(0,0,0) rot=(0,0.707107,0.707107;3.14159rad)
  Support = -> Fusion067 [Face7]
  sketch-geometry (4):
    g0: Circle CenterX=-1.27 CenterY=3.8 CenterZ=0 NormalX=0 NormalY=0 NormalZ=1 Radius=0.2
    g1: Circle CenterX=1.27 CenterY=3.8 CenterZ=0 NormalX=0 NormalY=0 NormalZ=1 Radius=0.2
    g2: Circle CenterX=-1.27 CenterY=-3.8 CenterZ=0 NormalX=0 NormalY=0 NormalZ=1 Radius=0.2
    g3: Circle CenterX=1.27 CenterY=-3.8 CenterZ=0 NormalX=0 NormalY=0 NormalZ=1 Radius=0.2
  constraints (9):
    c: Radius(g0) = 0.2
    c: Equal(g0,g1)
    c: Equal(g0,g3)
    c: Equal(g0,g2)
    c: Symmetric(g0,g1,g-2)
    c: Symmetric(g2,g3,g-2)
    c: Symmetric(g0,g2,g-1)
    c: DistanceX(g0,g1) = 2.54
    c: DistanceY(g1,g3) = -7.6
FEATURE [Part::Extrusion] Extrude310
  Base = -> Sketch257
  Dir = (0,7.8,0)
  Solid = true
FEATURE [Part::MultiFuse] Fusion068  label="Capteur_optique_011"
  Placement = pos=(-1430,-46,-20.7) rot=(0,0,1;0rad)
  Shapes = -> [Fusion067,Fillet026,Extrude310]
FEATURE [Sketcher::SketchObject] Sketch258
  Placement = pos=(0,0,0) rot=(1,0,0;1.5708rad)
  sketch-geometry (1):
    g0: Circle CenterX=0 CenterY=0 CenterZ=0 NormalX=0 NormalY=0 NormalZ=1 Radius=4
  constraints (2):
    c: Coincident(g0,g-1)
    c: Radius(g0) = 4
FEATURE [Part::Extrusion] Extrude311
  Base = -> Sketch258
  Dir = (0,50,0)
  Solid = true
FEATURE [Sketcher::SketchObject] Sketch259
  Placement = pos=(0,0,0) rot=(0.57735,0.57735,0.57735;2.0944rad)
  sketch-geometry (1):
    g0: Circle CenterX=6 CenterY=0 CenterZ=0 NormalX=0 NormalY=0 NormalZ=1 Radius=2
  constraints (3):
    c: DistanceX(g-1,g0) = 6
    c: Radius(g0) = 2
    c: PointOnObject(g0,g-1)
FEATURE [Part::Extrusion] Extrude312
  Base = -> Sketch259
  Dir = (4,0,0)
  Solid = true
FEATURE [Part::Extrusion] Extrude313
  Base = -> Sketch259
  Dir = (-4,0,0)
  Solid = true
FEATURE [Part::Cut] Cut117
  Base = -> Extrude311
  Tool = -> Extrude312
FEATURE [Part::Cut] Cut118  label="Axe_D8_011"
  Base = -> Cut117
  Placement = pos=(-1430,-86,0) rot=(0,0,1;0rad)
  Tool = -> Extrude313
FEATURE [Sketcher::SketchObject] Sketch260
  Placement = pos=(0,0,0) rot=(1,0,0;1.5708rad)
  sketch-geometry (1):
    g0: Circle CenterX=0 CenterY=0 CenterZ=0 NormalX=0 NormalY=0 NormalZ=1 Radius=2
  constraints (2):
    c: Coincident(g0,g-1)
    c: Radius(g0) = 2
FEATURE [Part::Extrusion] Extrude314  label="Axe_D4_011"
  Base = -> Sketch260
  Dir = (0,103.6,0)
  Placement = pos=(-1378.2,-80,0) rot=(0,0,1;1.5708rad)
  Solid = true
FEATURE [Sketcher::SketchObject] Sketch261
  Placement = pos=(0,0,0) rot=(1,0,0;1.5708rad)
  sketch-geometry (8):
    g0: LineSegment StartX=-50 StartY=0 StartZ=0 EndX=50 EndY=0 EndZ=0
    g1: LineSegment StartX=50 StartY=0 StartZ=0 EndX=50 EndY=-2 EndZ=0
    g2: LineSegment StartX=50 StartY=-2 StartZ=0 EndX=47 EndY=-2 EndZ=0
    g3: LineSegment StartX=47 StartY=-2 StartZ=0 EndX=44 EndY=-16 EndZ=0
    g4: LineSegment StartX=44 StartY=-16 StartZ=0 EndX=-44 EndY=-16 EndZ=0
    g5: LineSegment StartX=-44 StartY=-16 StartZ=0 EndX=-47 EndY=-2 EndZ=0
    g6: LineSegment StartX=-47 StartY=-2 StartZ=0 EndX=-50 EndY=-2 EndZ=0
    g7: LineSegment StartX=-50 StartY=-2 StartZ=0 EndX=-50 EndY=0 EndZ=0
  constraints (24):
    c: PointOnObject(g0,g-1)
    c: Horizontal(g0)
    c: Coincident(g0,g1)
    c: Vertical(g1)
    c: Coincident(g1,g2)
    c: Horizontal(g2)
    c: Coincident(g2,g3)
    c: Coincident(g3,g4)
    c: Horizontal(g4)
    c: Coincident(g4,g5)
    c: Coincident(g5,g6)
    c: Horizontal(g6)
    c: Coincident(g6,g7)
    c: Coincident(g7,g0)
    c: Vertical(g7)
    c: DistanceY(g0,g6) = -2
    c: DistanceX(g6,g5) = 3
    c: DistanceX(g0,g0) = 100
    c: Symmetric(g0,g0,g-2)
    c: Symmetric(g6,g1,g-2)
    c: Symmetric(g5,g2,g-2)
    c: Symmetric(g4,g3,g-2)
    c: DistanceX(g4,g3) = 88
    c: DistanceY(g0,g4) = -16
FEATURE [Part::Extrusion] Extrude315  label="Plaque_alveolaire_011"
  Base = -> Sketch261
  Dir = (0,2000,0)
  Placement = pos=(-1430,-62,22) rot=(0,0,1;3.14159rad)
  Solid = true
FEATURE [App::DocumentObjectGroup] Groupe016  label="Assemblage_miroir_002"
  Group = -> [Cut112,Fusion065,Extrude300,Part__Feature013,Extrude301,Fillet025,Fusion068,Cut118,Extrude314,Extrude315]
FEATURE [Sketcher::SketchObject] Sketch262
  Placement = pos=(0,0,0) rot=(1,0,0;1.5708rad)
  sketch-geometry (8):
    g0: LineSegment StartX=-21.15 StartY=16.15 StartZ=0 EndX=-16.15 EndY=21.15 EndZ=0
    g1: LineSegment StartX=-16.15 StartY=21.15 StartZ=0 EndX=16.15 EndY=21.15 EndZ=0
    g2: LineSegment StartX=16.15 StartY=21.15 StartZ=0 EndX=21.15 EndY=16.15 EndZ=0
    g3: LineSegment StartX=21.15 StartY=16.15 StartZ=0 EndX=21.15 EndY=-16.15 EndZ=0
    g4: LineSegment StartX=21.15 StartY=-16.15 StartZ=0 EndX=16.15 EndY=-21.15 EndZ=0
    g5: LineSegment StartX=16.15 StartY=-21.15 StartZ=0 EndX=-16.15 EndY=-21.15 EndZ=0
    g6: LineSegment StartX=-16.15 StartY=-21.15 StartZ=0 EndX=-21.15 EndY=-16.15 EndZ=0
    g7: LineSegment StartX=-21.15 StartY=-16.15 StartZ=0 EndX=-21.15 EndY=16.15 EndZ=0
  constraints (21):
    c: Coincident(g0,g1)
    c: Horizontal(g1)
    c: Coincident(g1,g2)
    c: Coincident(g2,g3)
    c: Vertical(g3)
    c: Coincident(g3,g4)
    c: Coincident(g4,g5)
    c: Horizontal(g5)
    c: Coincident(g5,g6)
    c: Coincident(g6,g7)
    c: Coincident(g7,g0)
    c: Angle(g7,g0) = 2.35619
    c: Distance(g0,g7) = 5
    c: Distance(g2,g7) = 42.3
    c: Distance(g5,g1) = 42.3
    c: Symmetric(g6,g3,g-2)
    c: Symmetric(g5,g4,g-2)
    c: Symmetric(g0,g2,g-2)
    c: Symmetric(g0,g1,g-2)
    c: Symmetric(g0,g6,g-1)
    c: Symmetric(g0,g5,g-1)
FEATURE [Part::Extrusion] Extrude316
  Base = -> Sketch262
  Dir = (0,48,0)
  Solid = true
FEATURE [Sketcher::SketchObject] Sketch263
  Placement = pos=(0,0,0) rot=(1,0,0;1.5708rad)
  Support = -> Extrude316 [Face9]
  sketch-geometry (1):
    g0: Circle CenterX=0 CenterY=0 CenterZ=0 NormalX=0 NormalY=0 NormalZ=1 Radius=11
  constraints (2):
    c: Coincident(g0,g-1)
    c: Radius(g0) = 11
FEATURE [Part::Extrusion] Extrude317
  Base = -> Sketch263
  Dir = (0,-2,0)
  Solid = true
FEATURE [Sketcher::SketchObject] Sketch264
  Placement = pos=(0,-2,0) rot=(1,0,0;1.5708rad)
  Support = -> Extrude317 [Face3]
  sketch-geometry (1):
    g0: Circle CenterX=0 CenterY=0 CenterZ=0 NormalX=0 NormalY=0 NormalZ=1 Radius=2.5
  constraints (2):
    c: Coincident(g0,g-1)
    c: Radius(g0) = 2.5
FEATURE [Part::Extrusion] Extrude318
  Base = -> Sketch264
  Dir = (0,-22,0)
  Solid = true
FEATURE [Part::Chamfer] Chamfer036
  Base = -> Extrude318
  Edges = 1 edges r=0.8: [Edge3]
FEATURE [Sketcher::SketchObject] Sketch265
  Placement = pos=(0,0,0) rot=(1,0,0;1.5708rad)
  Support = -> Extrude316 [Face9]
  sketch-geometry (4):
    g0: Circle CenterX=-15.5 CenterY=15.5 CenterZ=0 NormalX=0 NormalY=0 NormalZ=1 Radius=2
    g1: Circle CenterX=15.5 CenterY=15.5 CenterZ=0 NormalX=0 NormalY=0 NormalZ=1 Radius=2
    g2: Circle CenterX=-15.5 CenterY=-15.5 CenterZ=0 NormalX=0 NormalY=0 NormalZ=1 Radius=2
    g3: Circle CenterX=15.5 CenterY=-15.5 CenterZ=0 NormalX=0 NormalY=0 NormalZ=1 Radius=2
  constraints (9):
    c: Distance(g0,g1) = 31
    c: Distance(g0,g2) = 31
    c: Symmetric(g0,g2,g-1)
    c: Symmetric(g0,g1,g-2)
    c: Symmetric(g2,g3,g-2)
    c: Radius(g0) = 2
    c: Equal(g0,g1)
    c: Equal(g0,g2)
    c: Equal(g0,g3)
FEATURE [Part::Extrusion] Extrude319
  Base = -> Sketch265
  Dir = (0,4.5,0)
  Solid = true
FEATURE [Part::Cut] Cut119
  Base = -> Extrude316
  Tool = -> Extrude319
FEATURE [Sketcher::SketchObject] Sketch266
  Placement = pos=(0,0,0) rot=(1,0,0;1.5708rad)
  sketch-geometry (1):
    g0: Circle CenterX=0 CenterY=0 CenterZ=0 NormalX=0 NormalY=0 NormalZ=1 Radius=9
  constraints (2):
    c: Coincident(g0,g-1)
    c: Radius(g0) = 9
FEATURE [Part::Extrusion] Extrude320
  Base = -> Sketch266
  Dir = (0,25,0)
  Solid = true
FEATURE [Sketcher::SketchObject] Sketch267
  Placement = pos=(0,0,0) rot=(1,0,0;1.5708rad)
  sketch-geometry (1):
    g0: Circle CenterX=0 CenterY=0 CenterZ=0 NormalX=0 NormalY=0 NormalZ=1 Radius=2.5
  constraints (2):
    c: Coincident(g0,g-1)
    c: Radius(g0) = 2.5
FEATURE [Part::Extrusion] Extrude321
  Base = -> Sketch267
  Dir = (0,10,0)
  Solid = true
FEATURE [Part::Cut] Cut120
  Base = -> Extrude320
  Tool = -> Extrude321
FEATURE [Sketcher::SketchObject] Sketch268
  Placement = pos=(0,25,0) rot=(0,0.707107,0.707107;3.14159rad)
  Support = -> Cut120 [Face3]
  sketch-geometry (1):
    g0: Circle CenterX=0 CenterY=0 CenterZ=0 NormalX=0 NormalY=0 NormalZ=1 Radius=4
  constraints (2):
    c: Coincident(g0,g-1)
    c: Radius(g0) = 4
FEATURE [Part::Extrusion] Extrude322
  Base = -> Sketch268
  Dir = (0,-10,0)
  Solid = true
FEATURE [Part::Cut] Cut121  label="Accouplement_012"
  Base = -> Cut120
  Placement = pos=(-1573,-12,0) rot=(1,0,0;3.14159rad)
  Tool = -> Extrude322
FEATURE [Part::Fuse] Fusion069
  Base = -> Extrude317
  Tool = -> Cut119
FEATURE [Part::Fuse] Fusion070  label="Moteur_012"
  Base = -> Chamfer036
  Placement = pos=(-1573,0,0) rot=(0,0,1;0rad)
  Tool = -> Fusion069
FEATURE [Sketcher::SketchObject] Sketch269
  Placement = pos=(0,0,0) rot=(1,0,0;1.5708rad)
  sketch-geometry (4):
    g0: LineSegment StartX=-50 StartY=0 StartZ=0 EndX=-47 EndY=0 EndZ=0
    g1: LineSegment StartX=47 StartY=0 StartZ=0 EndX=50 EndY=0 EndZ=0
    g2: ArcOfCircle CenterX=0 CenterY=0 CenterZ=0 NormalX=0 NormalY=0 NormalZ=1 Radius=47 StartAngle=3.14159 EndAngle=6.28319
    g3: ArcOfCircle CenterX=0 CenterY=0 CenterZ=0 NormalX=0 NormalY=0 NormalZ=1 Radius=50 StartAngle=3.14159 EndAngle=6.28319
  constraints (13):
    c: Horizontal(g0)
    c: PointOnObject(g1,g-1)
    c: Horizontal(g1)
    c: Coincident(g2,g-1)
    c: PointOnObject(g2,g-1)
    c: Coincident(g3,g-1)
    c: Coincident(g3,g1)
    c: PointOnObject(g3,g-1)
    c: Coincident(g0,g3)
    c: Coincident(g0,g2)
    c: Distance(g0,g1) = 100
    c: Distance(g0,g0) = 3
    c: Coincident(g1,g2)
FEATURE [Part::Extrusion] Extrude323  label="Demi_tube_sous_miroir_012"
  Base = -> Sketch269
  Dir = (0,2000,0)
  Placement = pos=(-1573,-62,20) rot=(0,0,1;3.14159rad)
  Solid = true
FEATURE [Part::Feature] Part__Feature014  label="Coussinet_autolub_C2-151-8-128_012"
  Placement = pos=(-1573,-46,0) rot=(0,0,1;1.5708rad)
  shape: bbox 16 x 8 x 16 mm, 12 faces (baked)
FEATURE [Sketcher::SketchObject] Sketch270
  Placement = pos=(0,0,0) rot=(1,0,0;1.5708rad)
  sketch-geometry (21):
    g0: Circle CenterX=0 CenterY=0 CenterZ=0 NormalX=0 NormalY=0 NormalZ=1 Radius=6
    g1: LineSegment StartX=-20.5 StartY=15 StartZ=0 EndX=20.5 EndY=15 EndZ=0
    g2: ArcOfCircle CenterX=20.5 CenterY=13 CenterZ=0 NormalX=0 NormalY=0 NormalZ=1 Radius=2 StartAngle=6.28319 EndAngle=7.85398
    g3: LineSegment StartX=22.5 StartY=13 StartZ=0 EndX=22.5 EndY=-73 EndZ=0
    g4: LineSegment StartX=-22.5 StartY=13 StartZ=0 EndX=-22.5 EndY=-73 EndZ=0
    g5: ArcOfCircle CenterX=-20.5 CenterY=13 CenterZ=0 NormalX=0 NormalY=0 NormalZ=1 Radius=2 StartAngle=1.5708 EndAngle=3.14159
    g6: ArcOfCircle CenterX=-20.5 CenterY=-73 CenterZ=0 NormalX=0 NormalY=0 NormalZ=1 Radius=2 StartAngle=3.14159 EndAngle=4.71239
    g7: ArcOfCircle CenterX=20.5 CenterY=-73 CenterZ=0 NormalX=0 NormalY=0 NormalZ=1 Radius=2 StartAngle=4.71239 EndAngle=6.28319
    g8: LineSegment StartX=-20.5 StartY=-75 StartZ=0 EndX=20.5 EndY=-75 EndZ=0
    g9: ArcOfCircle CenterX=0 CenterY=-16.7 CenterZ=0 NormalX=0 NormalY=0 NormalZ=1 Radius=1.5 StartAngle=0 EndAngle=3.14159
    g10: ArcOfCircle CenterX=0 CenterY=-24.3 CenterZ=0 NormalX=0 NormalY=0 NormalZ=1 Radius=1.5 StartAngle=3.14159 EndAngle=6.28319
    g11: LineSegment StartX=-1.5 StartY=-16.7 StartZ=0 EndX=-1.5 EndY=-24.3 EndZ=0
    g12: LineSegment StartX=1.5 StartY=-16.7 StartZ=0 EndX=1.5 EndY=-24.3 EndZ=0
    g13: Circle CenterX=-12.5 CenterY=-45 CenterZ=0 NormalX=0 NormalY=0 NormalZ=1 Radius=3.5
    g14: Circle CenterX=12.5 CenterY=-45 CenterZ=0 NormalX=0 NormalY=0 NormalZ=1 Radius=3.5
    g15: Circle CenterX=-12.5 CenterY=-65 CenterZ=0 NormalX=0 NormalY=0 NormalZ=1 Radius=3.5
    g16: Circle CenterX=12.5 CenterY=-65 CenterZ=0 NormalX=0 NormalY=0 NormalZ=1 Radius=3.5
    g17: LineSegment [constr] StartX=-12.5 StartY=-45 StartZ=0 EndX=12.5 EndY=-45 EndZ=0
    g18: LineSegment [constr] StartX=-12.5 StartY=-45 StartZ=0 EndX=-12.5 EndY=-65 EndZ=0
    g19: LineSegment [constr] StartX=-12.5 StartY=-65 StartZ=0 EndX=12.5 EndY=-65 EndZ=0
    g20: LineSegment [constr] StartX=12.5 StartY=-45 StartZ=0 EndX=12.5 EndY=-65 EndZ=0
  constraints (59):
    c: Coincident(g0,g-1)
    c: Radius(g0) = 6
    c: Horizontal(g1)
    c: Coincident(g2,g1)
    c: Coincident(g3,g2)
    c: Vertical(g3)
    c: Vertical(g4)
    c: Coincident(g5,g1)
    c: Coincident(g5,g4)
    c: Coincident(g7,g3)
    c: Coincident(g8,g6)
    c: Coincident(g8,g7)
    c: Tangent(g8,g7)
    c: Tangent(g5,g4)
    c: Tangent(g5,g1)
    c: Tangent(g1,g2)
    c: Tangent(g2,g3)
    c: Coincident(g4,g6)
    c: Tangent(g6,g4)
    c: Tangent(g6,g8)
    c: Horizontal(g8)
    c: Tangent(g7,g3)
    c: Distance(g4,g2) = 45
    c: Symmetric(g4,g2,g-2)
    c: Distance(g1,g6) = 90
    c: DistanceY(g-1,g1) = 15
    c: Tangent(g9,g12) = 1.5708
    c: Tangent(g9,g11) = -1.5708
    c: Tangent(g11,g10) = -1.5708
    c: Tangent(g12,g10) = 1.5708
    c: Vertical(g11)
    c: Equal(g9,g10)
    c: PointOnObject(g9,g-2)
    c: Distance(g-1,g9) = 16.7
    c: Distance(g9,g10) = 7.6
    c: Radius(g9) = 1.5
    c: Radius(g13) = 3.5
    c: Equal(g13,g14)
    c: Equal(g13,g16)
    c: Equal(g13,g15)
    c: Radius(g5) = 2
    c: Equal(g5,g7)
    c: Equal(g5,g6)
    c: DistanceY(g-1,g13) = -45
    c: Coincident(g17,g13)
    c: Coincident(g17,g14)
    c: Horizontal(g17)
    c: Coincident(g18,g13)
    c: Coincident(g18,g15)
    c: Coincident(g19,g15)
    c: Coincident(g19,g16)
    c: Horizontal(g19)
    c: Coincident(g20,g14)
    c: Coincident(g20,g16)
    c: Vertical(g18)
    c: Vertical(g20)
    c: Distance(g13,g15) = 20
    c: Distance(g13,g14) = 25
    c: Symmetric(g13,g14,g-2)
FEATURE [Part::Extrusion] Extrude324  label="Plaque_support_012"
  Base = -> Sketch270
  Dir = (0,6,0)
  Placement = pos=(-1573,-46,0) rot=(0,0,1;0rad)
  Solid = true
FEATURE [Sketcher::SketchObject] Sketch271
  Placement = pos=(0,0,0) rot=(0.57735,0.57735,0.57735;2.0944rad)
  sketch-geometry (8):
    g0: LineSegment StartX=0 StartY=33 StartZ=0 EndX=-2 EndY=33 EndZ=0
    g1: LineSegment StartX=-2 StartY=33 StartZ=0 EndX=-2 EndY=-24 EndZ=0
    g2: ArcOfCircle CenterX=-4 CenterY=-24 CenterZ=0 NormalX=0 NormalY=0 NormalZ=1 Radius=2 StartAngle=4.71239 EndAngle=6.28319
    g3: LineSegment StartX=-4 StartY=-26 StartZ=0 EndX=-38 EndY=-26 EndZ=0
    g4: LineSegment StartX=-38 StartY=-26 StartZ=0 EndX=-38 EndY=-28 EndZ=0
    g5: LineSegment StartX=-38 StartY=-28 StartZ=0 EndX=-4 EndY=-28 EndZ=0
    g6: ArcOfCircle CenterX=-4 CenterY=-24 CenterZ=0 NormalX=0 NormalY=0 NormalZ=1 Radius=4 StartAngle=4.71239 EndAngle=6.28319
    g7: LineSegment StartX=0 StartY=-24 StartZ=0 EndX=0 EndY=33 EndZ=0
  constraints (22):
    c: PointOnObject(g0,g-2)
    c: Horizontal(g0)
    c: Coincident(g0,g1)
    c: Vertical(g1)
    c: Tangent(g1,g2) = 1.5708
    c: Tangent(g2,g3) = 1.5708
    c: Coincident(g3,g4)
    c: Vertical(g4)
    c: Coincident(g4,g5)
    c: Horizontal(g5)
    c: Tangent(g5,g6) = -1.5708
    c: PointOnObject(g6,g-2)
    c: Tangent(g6,g7) = -1.5708
    c: Coincident(g7,g0)
    c: Horizontal(g3)
    c: DistanceX(g0,g0) = 2
    c: Radius(g2) = 2
    c: Radius(g6) = 4
    c: DistanceY(g3,g4) = -2
    c: Distance(g-1,g0) = 33
    c: DistanceY(g-1,g5) = -28
    c: DistanceX(g6,g4) = -38
FEATURE [Part::Extrusion] Extrude325
  Base = -> Sketch271
  Dir = (-32.5,0,0)
  Solid = true
FEATURE [Part::Extrusion] Extrude326
  Base = -> Sketch271
  Dir = (32.5,0,0)
  Solid = true
FEATURE [Part::MultiFuse] Fusion071
  Shapes = -> [Extrude325,Extrude326]
FEATURE [Sketcher::SketchObject] Sketch272
  Placement = pos=(0,-2,0) rot=(1,0,0;1.5708rad)
  Support = -> Fusion071 [Face3]
  sketch-geometry (9):
    g0: ArcOfCircle CenterX=0 CenterY=0 CenterZ=0 NormalX=0 NormalY=0 NormalZ=1 Radius=32.5 StartAngle=0 EndAngle=3.14159
    g1: LineSegment StartX=-32.5 StartY=0 StartZ=0 EndX=-32.5 EndY=34 EndZ=0
    g2: LineSegment StartX=-32.5 StartY=34 StartZ=0 EndX=32.5 EndY=34 EndZ=0
    g3: LineSegment StartX=32.5 StartY=34 StartZ=0 EndX=32.5 EndY=0 EndZ=0
    g4: Circle CenterX=0 CenterY=0 CenterZ=0 NormalX=0 NormalY=0 NormalZ=1 Radius=11
    g5: Circle CenterX=-15.5 CenterY=15.5 CenterZ=0 NormalX=0 NormalY=0 NormalZ=1 Radius=2
    g6: Circle CenterX=15.5 CenterY=15.5 CenterZ=0 NormalX=0 NormalY=0 NormalZ=1 Radius=2
    g7: Circle CenterX=-15.5 CenterY=-15.5 CenterZ=0 NormalX=0 NormalY=0 NormalZ=1 Radius=2
    g8: Circle CenterX=15.5 CenterY=-15.5 CenterZ=0 NormalX=0 NormalY=0 NormalZ=1 Radius=2
  constraints (23):
    c: Coincident(g0,g-1)
    c: PointOnObject(g0,g-1)
    c: PointOnObject(g0,g-1)
    c: Coincident(g1,g0)
    c: Vertical(g1)
    c: Coincident(g1,g2)
    c: Horizontal(g2)
    c: Coincident(g2,g3)
    c: Coincident(g3,g0)
    c: Vertical(g3)
    c: DistanceY(g1,g0) = -34
    c: Coincident(g4,g-1)
    c: Radius(g4) = 11
    c: DistanceX(g1,g2) = 65
    c: Radius(g5) = 2
    c: Equal(g5,g6)
    c: Equal(g5,g8)
    c: Equal(g5,g7)
    c: Symmetric(g5,g6,g-2)
    c: Symmetric(g5,g7,g-1)
    c: Symmetric(g7,g8,g-2)
    c: DistanceX(g5,g6) = 31
    c: DistanceY(g5,g7) = -31
FEATURE [Part::Extrusion] Extrude327
  Base = -> Sketch272
  Dir = (0,2,0)
  Solid = true
FEATURE [Part::Cut] Cut122
  Base = -> Fusion071
  Tool = -> Extrude327
FEATURE [Sketcher::SketchObject] Sketch273
  ExternalGeometry = -> [Cut122]
  Placement = pos=(0,0,-26) rot=(0,0,1;0rad)
  Support = -> Cut122 [Face5]
  sketch-geometry (5):
    g0: Circle CenterX=-25 CenterY=-12 CenterZ=0 NormalX=0 NormalY=0 NormalZ=1 Radius=3.5
    g1: Circle CenterX=-25 CenterY=-30 CenterZ=0 NormalX=0 NormalY=0 NormalZ=1 Radius=3.5
    g2: Circle CenterX=25 CenterY=-12 CenterZ=0 NormalX=0 NormalY=0 NormalZ=1 Radius=3.5
    g3: Circle CenterX=25 CenterY=-30 CenterZ=0 NormalX=0 NormalY=0 NormalZ=1 Radius=3.5
    g4: LineSegment [constr] StartX=-25 StartY=-12 StartZ=0 EndX=-25 EndY=-30 EndZ=0
  constraints (12):
    c: Radius(g0) = 3.5
    c: Equal(g0,g2)
    c: Equal(g0,g3)
    c: Equal(g0,g1)
    c: Symmetric(g0,g2,g-2)
    c: Symmetric(g1,g3,g-2)
    c: Coincident(g4,g0)
    c: Coincident(g4,g1)
    c: Vertical(g4)
    c: DistanceY(g0,g1) = -18
    c: DistanceY(g-3,g1) = 8
    c: DistanceX(g0,g2) = 50
FEATURE [Part::Extrusion] Extrude328
  Base = -> Sketch273
  Dir = (0,0,-2)
  Solid = true
FEATURE [Part::Cut] Cut123
  Base = -> Cut122
  Tool = -> Extrude328
FEATURE [Part::Fillet] Fillet027  label="Plaque_moteur_012"
  Base = -> Cut123
  Edges = 2 edges r=4: [Edge5,Edge59]
  Placement = pos=(-1573,0,0) rot=(0,0,1;0rad)
FEATURE [Sketcher::SketchObject] Sketch274
  Placement = pos=(0,0,0) rot=(1,0,0;1.5708rad)
  sketch-geometry (4):
    g0: LineSegment StartX=-3.15 StartY=5.95 StartZ=0 EndX=3.15 EndY=5.95 EndZ=0
    g1: LineSegment StartX=3.15 StartY=5.95 StartZ=0 EndX=3.15 EndY=-5.95 EndZ=0
    g2: LineSegment StartX=3.15 StartY=-5.95 StartZ=0 EndX=-3.15 EndY=-5.95 EndZ=0
    g3: LineSegment StartX=-3.15 StartY=-5.95 StartZ=0 EndX=-3.15 EndY=5.95 EndZ=0
  constraints (12):
    c: Coincident(g0,g1)
    c: Coincident(g1,g2)
    c: Coincident(g2,g3)
    c: Coincident(g3,g0)
    c: Horizontal(g0)
    c: Horizontal(g2)
    c: Vertical(g1)
    c: Vertical(g3)
    c: DistanceX(g0,g0) = 6.3
    c: DistanceY(g0,g2) = -11.9
    c: Symmetric(g0,g0,g-2)
    c: Symmetric(g0,g1,g-1)
FEATURE [Part::Extrusion] Extrude329
  Base = -> Sketch274
  Dir = (0,-10.8,0)
  Solid = true
FEATURE [Sketcher::SketchObject] Sketch275
  ExternalGeometry = -> [Extrude329]
  Placement = pos=(0,-10.8,0) rot=(1,0,0;1.5708rad)
  Support = -> Extrude329 [Face6]
  sketch-geometry (4):
    g0: LineSegment StartX=-3.15 StartY=1.55 StartZ=0 EndX=3.15 EndY=1.55 EndZ=0
    g1: LineSegment StartX=3.15 StartY=1.55 StartZ=0 EndX=3.15 EndY=-1.55 EndZ=0
    g2: LineSegment StartX=3.15 StartY=-1.55 StartZ=0 EndX=-3.15 EndY=-1.55 EndZ=0
    g3: LineSegment StartX=-3.15 StartY=-1.55 StartZ=0 EndX=-3.15 EndY=1.55 EndZ=0
  constraints (12):
    c: Coincident(g0,g1)
    c: Coincident(g1,g2)
    c: Coincident(g2,g3)
    c: Coincident(g3,g0)
    c: Horizontal(g0)
    c: Horizontal(g2)
    c: Vertical(g1)
    c: Vertical(g3)
    c: PointOnObject(g0,g-4)
    c: PointOnObject(g0,g-3)
    c: DistanceY(g0,g2) = -3.1
    c: Symmetric(g0,g1,g-1)
FEATURE [Part::Extrusion] Extrude330
  Base = -> Sketch275
  Dir = (0,7.7,0)
  Solid = true
FEATURE [Part::Cut] Cut124
  Base = -> Extrude329
  Tool = -> Extrude330
FEATURE [Part::Chamfer] Chamfer037
  Base = -> Cut124
  Edges = 4 edges r=0.5: [Edge7,Edge9,Edge15,Edge17]
FEATURE [Part::Chamfer] Chamfer038
  Base = -> Chamfer037
  Edges = 1 edges r=1.2: [Edge13]
FEATURE [Sketcher::SketchObject] Sketch276
  ExternalGeometry = -> [Chamfer038]
  Placement = pos=(0,0,5.95) rot=(0,0,1;0rad)
  Support = -> Chamfer038 [Face5]
  sketch-geometry (4):
    g0: LineSegment StartX=-3 StartY=0 StartZ=0 EndX=3 EndY=0 EndZ=0
    g1: LineSegment StartX=3 StartY=0 StartZ=0 EndX=3 EndY=-3.1 EndZ=0
    g2: LineSegment StartX=3 StartY=-3.1 StartZ=0 EndX=-3 EndY=-3.1 EndZ=0
    g3: LineSegment StartX=-3 StartY=-3.1 StartZ=0 EndX=-3 EndY=0 EndZ=0
  constraints (12):
    c: Coincident(g0,g1)
    c: Coincident(g1,g2)
    c: Coincident(g2,g3)
    c: Coincident(g3,g0)
    c: Horizontal(g0)
    c: Horizontal(g2)
    c: Vertical(g1)
    c: Vertical(g3)
    c: PointOnObject(g0,g-1)
    c: DistanceX(g-3,g0) = 0.15
    c: Symmetric(g0,g0,g-2)
    c: DistanceY(g0,g1) = -3.1
FEATURE [Part::Extrusion] Extrude331
  Base = -> Sketch276
  Dir = (0,0,6.3)
  Solid = true
FEATURE [Sketcher::SketchObject] Sketch277
  ExternalGeometry = -> [Extrude331]
  Placement = pos=(0,-3.1,0) rot=(1,0,0;1.5708rad)
  Support = -> Extrude331 [Face3]
  sketch-geometry (1):
    g0: Circle CenterX=0 CenterY=9.5 CenterZ=0 NormalX=0 NormalY=0 NormalZ=1 Radius=1.65
  constraints (3):
    c: PointOnObject(g0,g-2)
    c: Radius(g0) = 1.65
    c: DistanceY(g0,g-3) = -3.55
FEATURE [Part::Extrusion] Extrude332
  Base = -> Sketch277
  Dir = (0,6,0)
  Solid = true
FEATURE [Part::Cut] Cut125
  Base = -> Extrude331
  Tool = -> Extrude332
FEATURE [Part::Fillet] Fillet028
  Base = -> Cut125
  Edges = 2 edges r=1.35: [Edge8,Edge11]
FEATURE [Part::MultiFuse] Fusion072
  Shapes = -> [Chamfer038]
FEATURE [Sketcher::SketchObject] Sketch278
  Placement = pos=(0,0,0) rot=(0,0.707107,0.707107;3.14159rad)
  Support = -> Fusion072 [Face7]
  sketch-geometry (4):
    g0: Circle CenterX=-1.27 CenterY=3.8 CenterZ=0 NormalX=0 NormalY=0 NormalZ=1 Radius=0.2
    g1: Circle CenterX=1.27 CenterY=3.8 CenterZ=0 NormalX=0 NormalY=0 NormalZ=1 Radius=0.2
    g2: Circle CenterX=-1.27 CenterY=-3.8 CenterZ=0 NormalX=0 NormalY=0 NormalZ=1 Radius=0.2
    g3: Circle CenterX=1.27 CenterY=-3.8 CenterZ=0 NormalX=0 NormalY=0 NormalZ=1 Radius=0.2
  constraints (9):
    c: Radius(g0) = 0.2
    c: Equal(g0,g1)
    c: Equal(g0,g3)
    c: Equal(g0,g2)
    c: Symmetric(g0,g1,g-2)
    c: Symmetric(g2,g3,g-2)
    c: Symmetric(g0,g2,g-1)
    c: DistanceX(g0,g1) = 2.54
    c: DistanceY(g1,g3) = -7.6
FEATURE [Part::Extrusion] Extrude333
  Base = -> Sketch278
  Dir = (0,7.8,0)
  Solid = true
FEATURE [Part::MultiFuse] Fusion073  label="Capteur_optique_012"
  Placement = pos=(-1573,-46,-20.7) rot=(0,0,1;0rad)
  Shapes = -> [Fusion072,Fillet028,Extrude333]
FEATURE [Sketcher::SketchObject] Sketch279
  Placement = pos=(0,0,0) rot=(1,0,0;1.5708rad)
  sketch-geometry (1):
    g0: Circle CenterX=0 CenterY=0 CenterZ=0 NormalX=0 NormalY=0 NormalZ=1 Radius=4
  constraints (2):
    c: Coincident(g0,g-1)
    c: Radius(g0) = 4
FEATURE [Part::Extrusion] Extrude334
  Base = -> Sketch279
  Dir = (0,50,0)
  Solid = true
FEATURE [Sketcher::SketchObject] Sketch280
  Placement = pos=(0,0,0) rot=(0.57735,0.57735,0.57735;2.0944rad)
  sketch-geometry (1):
    g0: Circle CenterX=6 CenterY=0 CenterZ=0 NormalX=0 NormalY=0 NormalZ=1 Radius=2
  constraints (3):
    c: DistanceX(g-1,g0) = 6
    c: Radius(g0) = 2
    c: PointOnObject(g0,g-1)
FEATURE [Part::Extrusion] Extrude335
  Base = -> Sketch280
  Dir = (4,0,0)
  Solid = true
FEATURE [Part::Extrusion] Extrude336
  Base = -> Sketch280
  Dir = (-4,0,0)
  Solid = true
FEATURE [Part::Cut] Cut126
  Base = -> Extrude334
  Tool = -> Extrude335
FEATURE [Part::Cut] Cut127  label="Axe_D8_012"
  Base = -> Cut126
  Placement = pos=(-1573,-86,0) rot=(0,0,1;0rad)
  Tool = -> Extrude336
FEATURE [Sketcher::SketchObject] Sketch281
  Placement = pos=(0,0,0) rot=(1,0,0;1.5708rad)
  sketch-geometry (1):
    g0: Circle CenterX=0 CenterY=0 CenterZ=0 NormalX=0 NormalY=0 NormalZ=1 Radius=2
  constraints (2):
    c: Coincident(g0,g-1)
    c: Radius(g0) = 2
FEATURE [Part::Extrusion] Extrude337  label="Axe_D4_012"
  Base = -> Sketch281
  Dir = (0,103.6,0)
  Placement = pos=(-1521.2,-80,0) rot=(0,0,1;1.5708rad)
  Solid = true
FEATURE [Sketcher::SketchObject] Sketch282
  Placement = pos=(0,0,0) rot=(1,0,0;1.5708rad)
  sketch-geometry (8):
    g0: LineSegment StartX=-50 StartY=0 StartZ=0 EndX=50 EndY=0 EndZ=0
    g1: LineSegment StartX=50 StartY=0 StartZ=0 EndX=50 EndY=-2 EndZ=0
    g2: LineSegment StartX=50 StartY=-2 StartZ=0 EndX=47 EndY=-2 EndZ=0
    g3: LineSegment StartX=47 StartY=-2 StartZ=0 EndX=44 EndY=-16 EndZ=0
    g4: LineSegment StartX=44 StartY=-16 StartZ=0 EndX=-44 EndY=-16 EndZ=0
    g5: LineSegment StartX=-44 StartY=-16 StartZ=0 EndX=-47 EndY=-2 EndZ=0
    g6: LineSegment StartX=-47 StartY=-2 StartZ=0 EndX=-50 EndY=-2 EndZ=0
    g7: LineSegment StartX=-50 StartY=-2 StartZ=0 EndX=-50 EndY=0 EndZ=0
  constraints (24):
    c: PointOnObject(g0,g-1)
    c: Horizontal(g0)
    c: Coincident(g0,g1)
    c: Vertical(g1)
    c: Coincident(g1,g2)
    c: Horizontal(g2)
    c: Coincident(g2,g3)
    c: Coincident(g3,g4)
    c: Horizontal(g4)
    c: Coincident(g4,g5)
    c: Coincident(g5,g6)
    c: Horizontal(g6)
    c: Coincident(g6,g7)
    c: Coincident(g7,g0)
    c: Vertical(g7)
    c: DistanceY(g0,g6) = -2
    c: DistanceX(g6,g5) = 3
    c: DistanceX(g0,g0) = 100
    c: Symmetric(g0,g0,g-2)
    c: Symmetric(g6,g1,g-2)
    c: Symmetric(g5,g2,g-2)
    c: Symmetric(g4,g3,g-2)
    c: DistanceX(g4,g3) = 88
    c: DistanceY(g0,g4) = -16
FEATURE [Part::Extrusion] Extrude338  label="Plaque_alveolaire_012"
  Base = -> Sketch282
  Dir = (0,2000,0)
  Placement = pos=(-1573,-62,22) rot=(0,0,1;3.14159rad)
  Solid = true
FEATURE [App::DocumentObjectGroup] Groupe017  label="Assemblage_miroir X=-143_002"
  Group = -> [Cut121,Fusion070,Extrude323,Part__Feature014,Extrude324,Fillet027,Fusion073,Cut127,Extrude337,Extrude338]
FEATURE [Sketcher::SketchObject] Sketch284
  Placement = pos=(0,0,0) rot=(1,0,0;1.5708rad)
  sketch-geometry (8):
    g0: LineSegment StartX=-21.15 StartY=16.15 StartZ=0 EndX=-16.15 EndY=21.15 EndZ=0
    g1: LineSegment StartX=-16.15 StartY=21.15 StartZ=0 EndX=16.15 EndY=21.15 EndZ=0
    g2: LineSegment StartX=16.15 StartY=21.15 StartZ=0 EndX=21.15 EndY=16.15 EndZ=0
    g3: LineSegment StartX=21.15 StartY=16.15 StartZ=0 EndX=21.15 EndY=-16.15 EndZ=0
    g4: LineSegment StartX=21.15 StartY=-16.15 StartZ=0 EndX=16.15 EndY=-21.15 EndZ=0
    g5: LineSegment StartX=16.15 StartY=-21.15 StartZ=0 EndX=-16.15 EndY=-21.15 EndZ=0
    g6: LineSegment StartX=-16.15 StartY=-21.15 StartZ=0 EndX=-21.15 EndY=-16.15 EndZ=0
    g7: LineSegment StartX=-21.15 StartY=-16.15 StartZ=0 EndX=-21.15 EndY=16.15 EndZ=0
  constraints (21):
    c: Coincident(g0,g1)
    c: Horizontal(g1)
    c: Coincident(g1,g2)
    c: Coincident(g2,g3)
    c: Vertical(g3)
    c: Coincident(g3,g4)
    c: Coincident(g4,g5)
    c: Horizontal(g5)
    c: Coincident(g5,g6)
    c: Coincident(g6,g7)
    c: Coincident(g7,g0)
    c: Angle(g7,g0) = 2.35619
    c: Distance(g0,g7) = 5
    c: Distance(g2,g7) = 42.3
    c: Distance(g5,g1) = 42.3
    c: Symmetric(g6,g3,g-2)
    c: Symmetric(g5,g4,g-2)
    c: Symmetric(g0,g2,g-2)
    c: Symmetric(g0,g1,g-2)
    c: Symmetric(g0,g6,g-1)
    c: Symmetric(g0,g5,g-1)
FEATURE [Part::Extrusion] Extrude340
  Base = -> Sketch284
  Dir = (0,48,0)
  Solid = true
FEATURE [Sketcher::SketchObject] Sketch285
  Placement = pos=(0,0,0) rot=(1,0,0;1.5708rad)
  Support = -> Extrude340 [Face9]
  sketch-geometry (1):
    g0: Circle CenterX=0 CenterY=0 CenterZ=0 NormalX=0 NormalY=0 NormalZ=1 Radius=11
  constraints (2):
    c: Coincident(g0,g-1)
    c: Radius(g0) = 11
FEATURE [Part::Extrusion] Extrude341
  Base = -> Sketch285
  Dir = (0,-2,0)
  Solid = true
FEATURE [Sketcher::SketchObject] Sketch286
  Placement = pos=(0,-2,0) rot=(1,0,0;1.5708rad)
  Support = -> Extrude341 [Face3]
  sketch-geometry (1):
    g0: Circle CenterX=0 CenterY=0 CenterZ=0 NormalX=0 NormalY=0 NormalZ=1 Radius=2.5
  constraints (2):
    c: Coincident(g0,g-1)
    c: Radius(g0) = 2.5
FEATURE [Part::Extrusion] Extrude342
  Base = -> Sketch286
  Dir = (0,-22,0)
  Solid = true
FEATURE [Part::Chamfer] Chamfer039
  Base = -> Extrude342
  Edges = 1 edges r=0.8: [Edge3]
FEATURE [Sketcher::SketchObject] Sketch287
  Placement = pos=(0,0,0) rot=(1,0,0;1.5708rad)
  Support = -> Extrude340 [Face9]
  sketch-geometry (4):
    g0: Circle CenterX=-15.5 CenterY=15.5 CenterZ=0 NormalX=0 NormalY=0 NormalZ=1 Radius=2
    g1: Circle CenterX=15.5 CenterY=15.5 CenterZ=0 NormalX=0 NormalY=0 NormalZ=1 Radius=2
    g2: Circle CenterX=-15.5 CenterY=-15.5 CenterZ=0 NormalX=0 NormalY=0 NormalZ=1 Radius=2
    g3: Circle CenterX=15.5 CenterY=-15.5 CenterZ=0 NormalX=0 NormalY=0 NormalZ=1 Radius=2
  constraints (9):
    c: Distance(g0,g1) = 31
    c: Distance(g0,g2) = 31
    c: Symmetric(g0,g2,g-1)
    c: Symmetric(g0,g1,g-2)
    c: Symmetric(g2,g3,g-2)
    c: Radius(g0) = 2
    c: Equal(g0,g1)
    c: Equal(g0,g2)
    c: Equal(g0,g3)
FEATURE [Part::Extrusion] Extrude343
  Base = -> Sketch287
  Dir = (0,4.5,0)
  Solid = true
FEATURE [Part::Cut] Cut128
  Base = -> Extrude340
  Tool = -> Extrude343
FEATURE [Sketcher::SketchObject] Sketch288
  Placement = pos=(0,0,0) rot=(1,0,0;1.5708rad)
  sketch-geometry (1):
    g0: Circle CenterX=0 CenterY=0 CenterZ=0 NormalX=0 NormalY=0 NormalZ=1 Radius=9
  constraints (2):
    c: Coincident(g0,g-1)
    c: Radius(g0) = 9
FEATURE [Part::Extrusion] Extrude344
  Base = -> Sketch288
  Dir = (0,25,0)
  Solid = true
FEATURE [Sketcher::SketchObject] Sketch289
  Placement = pos=(0,0,0) rot=(1,0,0;1.5708rad)
  sketch-geometry (1):
    g0: Circle CenterX=0 CenterY=0 CenterZ=0 NormalX=0 NormalY=0 NormalZ=1 Radius=2.5
  constraints (2):
    c: Coincident(g0,g-1)
    c: Radius(g0) = 2.5
FEATURE [Part::Extrusion] Extrude345
  Base = -> Sketch289
  Dir = (0,10,0)
  Solid = true
FEATURE [Part::Cut] Cut129
  Base = -> Extrude344
  Tool = -> Extrude345
FEATURE [Sketcher::SketchObject] Sketch290
  Placement = pos=(0,25,0) rot=(0,0.707107,0.707107;3.14159rad)
  Support = -> Cut129 [Face3]
  sketch-geometry (1):
    g0: Circle CenterX=0 CenterY=0 CenterZ=0 NormalX=0 NormalY=0 NormalZ=1 Radius=4
  constraints (2):
    c: Coincident(g0,g-1)
    c: Radius(g0) = 4
FEATURE [Part::Extrusion] Extrude346
  Base = -> Sketch290
  Dir = (0,-10,0)
  Solid = true
FEATURE [Part::Cut] Cut130  label="Accouplement_013"
  Base = -> Cut129
  Placement = pos=(-1716,-12,0) rot=(1,0,0;3.14159rad)
  Tool = -> Extrude346
FEATURE [Part::Fuse] Fusion074
  Base = -> Extrude341
  Tool = -> Cut128
FEATURE [Part::Fuse] Fusion075  label="Moteur_013"
  Base = -> Chamfer039
  Placement = pos=(-1716,0,0) rot=(0,0,1;0rad)
  Tool = -> Fusion074
FEATURE [Sketcher::SketchObject] Sketch291
  Placement = pos=(0,0,0) rot=(1,0,0;1.5708rad)
  sketch-geometry (4):
    g0: LineSegment StartX=-50 StartY=0 StartZ=0 EndX=-47 EndY=0 EndZ=0
    g1: LineSegment StartX=47 StartY=0 StartZ=0 EndX=50 EndY=0 EndZ=0
    g2: ArcOfCircle CenterX=0 CenterY=0 CenterZ=0 NormalX=0 NormalY=0 NormalZ=1 Radius=47 StartAngle=3.14159 EndAngle=6.28319
    g3: ArcOfCircle CenterX=0 CenterY=0 CenterZ=0 NormalX=0 NormalY=0 NormalZ=1 Radius=50 StartAngle=3.14159 EndAngle=6.28319
  constraints (13):
    c: Horizontal(g0)
    c: PointOnObject(g1,g-1)
    c: Horizontal(g1)
    c: Coincident(g2,g-1)
    c: PointOnObject(g2,g-1)
    c: Coincident(g3,g-1)
    c: Coincident(g3,g1)
    c: PointOnObject(g3,g-1)
    c: Coincident(g0,g3)
    c: Coincident(g0,g2)
    c: Distance(g0,g1) = 100
    c: Distance(g0,g0) = 3
    c: Coincident(g1,g2)
FEATURE [Part::Extrusion] Extrude347  label="Demi_tube_sous_miroir_013"
  Base = -> Sketch291
  Dir = (0,2000,0)
  Placement = pos=(-1716,-62,20) rot=(0,0,1;3.14159rad)
  Solid = true
FEATURE [Part::Feature] Part__Feature015  label="Coussinet_autolub_C2-151-8-128_013"
  Placement = pos=(-1716,-46,0) rot=(0,0,1;1.5708rad)
  shape: bbox 16 x 8 x 16 mm, 12 faces (baked)
FEATURE [Sketcher::SketchObject] Sketch292
  Placement = pos=(0,0,0) rot=(1,0,0;1.5708rad)
  sketch-geometry (21):
    g0: Circle CenterX=0 CenterY=0 CenterZ=0 NormalX=0 NormalY=0 NormalZ=1 Radius=6
    g1: LineSegment StartX=-20.5 StartY=15 StartZ=0 EndX=20.5 EndY=15 EndZ=0
    g2: ArcOfCircle CenterX=20.5 CenterY=13 CenterZ=0 NormalX=0 NormalY=0 NormalZ=1 Radius=2 StartAngle=6.28319 EndAngle=7.85398
    g3: LineSegment StartX=22.5 StartY=13 StartZ=0 EndX=22.5 EndY=-73 EndZ=0
    g4: LineSegment StartX=-22.5 StartY=13 StartZ=0 EndX=-22.5 EndY=-73 EndZ=0
    g5: ArcOfCircle CenterX=-20.5 CenterY=13 CenterZ=0 NormalX=0 NormalY=0 NormalZ=1 Radius=2 StartAngle=1.5708 EndAngle=3.14159
    g6: ArcOfCircle CenterX=-20.5 CenterY=-73 CenterZ=0 NormalX=0 NormalY=0 NormalZ=1 Radius=2 StartAngle=3.14159 EndAngle=4.71239
    g7: ArcOfCircle CenterX=20.5 CenterY=-73 CenterZ=0 NormalX=0 NormalY=0 NormalZ=1 Radius=2 StartAngle=4.71239 EndAngle=6.28319
    g8: LineSegment StartX=-20.5 StartY=-75 StartZ=0 EndX=20.5 EndY=-75 EndZ=0
    g9: ArcOfCircle CenterX=0 CenterY=-16.7 CenterZ=0 NormalX=0 NormalY=0 NormalZ=1 Radius=1.5 StartAngle=0 EndAngle=3.14159
    g10: ArcOfCircle CenterX=0 CenterY=-24.3 CenterZ=0 NormalX=0 NormalY=0 NormalZ=1 Radius=1.5 StartAngle=3.14159 EndAngle=6.28319
    g11: LineSegment StartX=-1.5 StartY=-16.7 StartZ=0 EndX=-1.5 EndY=-24.3 EndZ=0
    g12: LineSegment StartX=1.5 StartY=-16.7 StartZ=0 EndX=1.5 EndY=-24.3 EndZ=0
    g13: Circle CenterX=-12.5 CenterY=-45 CenterZ=0 NormalX=0 NormalY=0 NormalZ=1 Radius=3.5
    g14: Circle CenterX=12.5 CenterY=-45 CenterZ=0 NormalX=0 NormalY=0 NormalZ=1 Radius=3.5
    g15: Circle CenterX=-12.5 CenterY=-65 CenterZ=0 NormalX=0 NormalY=0 NormalZ=1 Radius=3.5
    g16: Circle CenterX=12.5 CenterY=-65 CenterZ=0 NormalX=0 NormalY=0 NormalZ=1 Radius=3.5
    g17: LineSegment [constr] StartX=-12.5 StartY=-45 StartZ=0 EndX=12.5 EndY=-45 EndZ=0
    g18: LineSegment [constr] StartX=-12.5 StartY=-45 StartZ=0 EndX=-12.5 EndY=-65 EndZ=0
    g19: LineSegment [constr] StartX=-12.5 StartY=-65 StartZ=0 EndX=12.5 EndY=-65 EndZ=0
    g20: LineSegment [constr] StartX=12.5 StartY=-45 StartZ=0 EndX=12.5 EndY=-65 EndZ=0
  constraints (59):
    c: Coincident(g0,g-1)
    c: Radius(g0) = 6
    c: Horizontal(g1)
    c: Coincident(g2,g1)
    c: Coincident(g3,g2)
    c: Vertical(g3)
    c: Vertical(g4)
    c: Coincident(g5,g1)
    c: Coincident(g5,g4)
    c: Coincident(g7,g3)
    c: Coincident(g8,g6)
    c: Coincident(g8,g7)
    c: Tangent(g8,g7)
    c: Tangent(g5,g4)
    c: Tangent(g5,g1)
    c: Tangent(g1,g2)
    c: Tangent(g2,g3)
    c: Coincident(g4,g6)
    c: Tangent(g6,g4)
    c: Tangent(g6,g8)
    c: Horizontal(g8)
    c: Tangent(g7,g3)
    c: Distance(g4,g2) = 45
    c: Symmetric(g4,g2,g-2)
    c: Distance(g1,g6) = 90
    c: DistanceY(g-1,g1) = 15
    c: Tangent(g9,g12) = 1.5708
    c: Tangent(g9,g11) = -1.5708
    c: Tangent(g11,g10) = -1.5708
    c: Tangent(g12,g10) = 1.5708
    c: Vertical(g11)
    c: Equal(g9,g10)
    c: PointOnObject(g9,g-2)
    c: Distance(g-1,g9) = 16.7
    c: Distance(g9,g10) = 7.6
    c: Radius(g9) = 1.5
    c: Radius(g13) = 3.5
    c: Equal(g13,g14)
    c: Equal(g13,g16)
    c: Equal(g13,g15)
    c: Radius(g5) = 2
    c: Equal(g5,g7)
    c: Equal(g5,g6)
    c: DistanceY(g-1,g13) = -45
    c: Coincident(g17,g13)
    c: Coincident(g17,g14)
    c: Horizontal(g17)
    c: Coincident(g18,g13)
    c: Coincident(g18,g15)
    c: Coincident(g19,g15)
    c: Coincident(g19,g16)
    c: Horizontal(g19)
    c: Coincident(g20,g14)
    c: Coincident(g20,g16)
    c: Vertical(g18)
    c: Vertical(g20)
    c: Distance(g13,g15) = 20
    c: Distance(g13,g14) = 25
    c: Symmetric(g13,g14,g-2)
FEATURE [Part::Extrusion] Extrude348  label="Plaque_support_013"
  Base = -> Sketch292
  Dir = (0,6,0)
  Placement = pos=(-1716,-46,0) rot=(0,0,1;0rad)
  Solid = true
FEATURE [Sketcher::SketchObject] Sketch293
  Placement = pos=(0,0,0) rot=(0.57735,0.57735,0.57735;2.0944rad)
  sketch-geometry (8):
    g0: LineSegment StartX=0 StartY=33 StartZ=0 EndX=-2 EndY=33 EndZ=0
    g1: LineSegment StartX=-2 StartY=33 StartZ=0 EndX=-2 EndY=-24 EndZ=0
    g2: ArcOfCircle CenterX=-4 CenterY=-24 CenterZ=0 NormalX=0 NormalY=0 NormalZ=1 Radius=2 StartAngle=4.71239 EndAngle=6.28319
    g3: LineSegment StartX=-4 StartY=-26 StartZ=0 EndX=-38 EndY=-26 EndZ=0
    g4: LineSegment StartX=-38 StartY=-26 StartZ=0 EndX=-38 EndY=-28 EndZ=0
    g5: LineSegment StartX=-38 StartY=-28 StartZ=0 EndX=-4 EndY=-28 EndZ=0
    g6: ArcOfCircle CenterX=-4 CenterY=-24 CenterZ=0 NormalX=0 NormalY=0 NormalZ=1 Radius=4 StartAngle=4.71239 EndAngle=6.28319
    g7: LineSegment StartX=0 StartY=-24 StartZ=0 EndX=0 EndY=33 EndZ=0
  constraints (22):
    c: PointOnObject(g0,g-2)
    c: Horizontal(g0)
    c: Coincident(g0,g1)
    c: Vertical(g1)
    c: Tangent(g1,g2) = 1.5708
    c: Tangent(g2,g3) = 1.5708
    c: Coincident(g3,g4)
    c: Vertical(g4)
    c: Coincident(g4,g5)
    c: Horizontal(g5)
    c: Tangent(g5,g6) = -1.5708
    c: PointOnObject(g6,g-2)
    c: Tangent(g6,g7) = -1.5708
    c: Coincident(g7,g0)
    c: Horizontal(g3)
    c: DistanceX(g0,g0) = 2
    c: Radius(g2) = 2
    c: Radius(g6) = 4
    c: DistanceY(g3,g4) = -2
    c: Distance(g-1,g0) = 33
    c: DistanceY(g-1,g5) = -28
    c: DistanceX(g6,g4) = -38
FEATURE [Part::Extrusion] Extrude349
  Base = -> Sketch293
  Dir = (-32.5,0,0)
  Solid = true
FEATURE [Part::Extrusion] Extrude350
  Base = -> Sketch293
  Dir = (32.5,0,0)
  Solid = true
FEATURE [Part::MultiFuse] Fusion076
  Shapes = -> [Extrude349,Extrude350]
FEATURE [Sketcher::SketchObject] Sketch294
  Placement = pos=(0,-2,0) rot=(1,0,0;1.5708rad)
  Support = -> Fusion076 [Face3]
  sketch-geometry (9):
    g0: ArcOfCircle CenterX=0 CenterY=0 CenterZ=0 NormalX=0 NormalY=0 NormalZ=1 Radius=32.5 StartAngle=0 EndAngle=3.14159
    g1: LineSegment StartX=-32.5 StartY=0 StartZ=0 EndX=-32.5 EndY=34 EndZ=0
    g2: LineSegment StartX=-32.5 StartY=34 StartZ=0 EndX=32.5 EndY=34 EndZ=0
    g3: LineSegment StartX=32.5 StartY=34 StartZ=0 EndX=32.5 EndY=0 EndZ=0
    g4: Circle CenterX=0 CenterY=0 CenterZ=0 NormalX=0 NormalY=0 NormalZ=1 Radius=11
    g5: Circle CenterX=-15.5 CenterY=15.5 CenterZ=0 NormalX=0 NormalY=0 NormalZ=1 Radius=2
    g6: Circle CenterX=15.5 CenterY=15.5 CenterZ=0 NormalX=0 NormalY=0 NormalZ=1 Radius=2
    g7: Circle CenterX=-15.5 CenterY=-15.5 CenterZ=0 NormalX=0 NormalY=0 NormalZ=1 Radius=2
    g8: Circle CenterX=15.5 CenterY=-15.5 CenterZ=0 NormalX=0 NormalY=0 NormalZ=1 Radius=2
  constraints (23):
    c: Coincident(g0,g-1)
    c: PointOnObject(g0,g-1)
    c: PointOnObject(g0,g-1)
    c: Coincident(g1,g0)
    c: Vertical(g1)
    c: Coincident(g1,g2)
    c: Horizontal(g2)
    c: Coincident(g2,g3)
    c: Coincident(g3,g0)
    c: Vertical(g3)
    c: DistanceY(g1,g0) = -34
    c: Coincident(g4,g-1)
    c: Radius(g4) = 11
    c: DistanceX(g1,g2) = 65
    c: Radius(g5) = 2
    c: Equal(g5,g6)
    c: Equal(g5,g8)
    c: Equal(g5,g7)
    c: Symmetric(g5,g6,g-2)
    c: Symmetric(g5,g7,g-1)
    c: Symmetric(g7,g8,g-2)
    c: DistanceX(g5,g6) = 31
    c: DistanceY(g5,g7) = -31
FEATURE [Part::Extrusion] Extrude351
  Base = -> Sketch294
  Dir = (0,2,0)
  Solid = true
FEATURE [Part::Cut] Cut131
  Base = -> Fusion076
  Tool = -> Extrude351
FEATURE [Sketcher::SketchObject] Sketch295
  ExternalGeometry = -> [Cut131]
  Placement = pos=(0,0,-26) rot=(0,0,1;0rad)
  Support = -> Cut131 [Face5]
  sketch-geometry (5):
    g0: Circle CenterX=-25 CenterY=-12 CenterZ=0 NormalX=0 NormalY=0 NormalZ=1 Radius=3.5
    g1: Circle CenterX=-25 CenterY=-30 CenterZ=0 NormalX=0 NormalY=0 NormalZ=1 Radius=3.5
    g2: Circle CenterX=25 CenterY=-12 CenterZ=0 NormalX=0 NormalY=0 NormalZ=1 Radius=3.5
    g3: Circle CenterX=25 CenterY=-30 CenterZ=0 NormalX=0 NormalY=0 NormalZ=1 Radius=3.5
    g4: LineSegment [constr] StartX=-25 StartY=-12 StartZ=0 EndX=-25 EndY=-30 EndZ=0
  constraints (12):
    c: Radius(g0) = 3.5
    c: Equal(g0,g2)
    c: Equal(g0,g3)
    c: Equal(g0,g1)
    c: Symmetric(g0,g2,g-2)
    c: Symmetric(g1,g3,g-2)
    c: Coincident(g4,g0)
    c: Coincident(g4,g1)
    c: Vertical(g4)
    c: DistanceY(g0,g1) = -18
    c: DistanceY(g-3,g1) = 8
    c: DistanceX(g0,g2) = 50
FEATURE [Part::Extrusion] Extrude352
  Base = -> Sketch295
  Dir = (0,0,-2)
  Solid = true
FEATURE [Part::Cut] Cut132
  Base = -> Cut131
  Tool = -> Extrude352
FEATURE [Part::Fillet] Fillet029  label="Plaque_moteur_013"
  Base = -> Cut132
  Edges = 2 edges r=4: [Edge5,Edge59]
  Placement = pos=(-1716,0,0) rot=(0,0,1;0rad)
FEATURE [Sketcher::SketchObject] Sketch296
  Placement = pos=(0,0,0) rot=(1,0,0;1.5708rad)
  sketch-geometry (4):
    g0: LineSegment StartX=-3.15 StartY=5.95 StartZ=0 EndX=3.15 EndY=5.95 EndZ=0
    g1: LineSegment StartX=3.15 StartY=5.95 StartZ=0 EndX=3.15 EndY=-5.95 EndZ=0
    g2: LineSegment StartX=3.15 StartY=-5.95 StartZ=0 EndX=-3.15 EndY=-5.95 EndZ=0
    g3: LineSegment StartX=-3.15 StartY=-5.95 StartZ=0 EndX=-3.15 EndY=5.95 EndZ=0
  constraints (12):
    c: Coincident(g0,g1)
    c: Coincident(g1,g2)
    c: Coincident(g2,g3)
    c: Coincident(g3,g0)
    c: Horizontal(g0)
    c: Horizontal(g2)
    c: Vertical(g1)
    c: Vertical(g3)
    c: DistanceX(g0,g0) = 6.3
    c: DistanceY(g0,g2) = -11.9
    c: Symmetric(g0,g0,g-2)
    c: Symmetric(g0,g1,g-1)
FEATURE [Part::Extrusion] Extrude353
  Base = -> Sketch296
  Dir = (0,-10.8,0)
  Solid = true
FEATURE [Sketcher::SketchObject] Sketch297
  ExternalGeometry = -> [Extrude353]
  Placement = pos=(0,-10.8,0) rot=(1,0,0;1.5708rad)
  Support = -> Extrude353 [Face6]
  sketch-geometry (4):
    g0: LineSegment StartX=-3.15 StartY=1.55 StartZ=0 EndX=3.15 EndY=1.55 EndZ=0
    g1: LineSegment StartX=3.15 StartY=1.55 StartZ=0 EndX=3.15 EndY=-1.55 EndZ=0
    g2: LineSegment StartX=3.15 StartY=-1.55 StartZ=0 EndX=-3.15 EndY=-1.55 EndZ=0
    g3: LineSegment StartX=-3.15 StartY=-1.55 StartZ=0 EndX=-3.15 EndY=1.55 EndZ=0
  constraints (12):
    c: Coincident(g0,g1)
    c: Coincident(g1,g2)
    c: Coincident(g2,g3)
    c: Coincident(g3,g0)
    c: Horizontal(g0)
    c: Horizontal(g2)
    c: Vertical(g1)
    c: Vertical(g3)
    c: PointOnObject(g0,g-4)
    c: PointOnObject(g0,g-3)
    c: DistanceY(g0,g2) = -3.1
    c: Symmetric(g0,g1,g-1)
FEATURE [Part::Extrusion] Extrude354
  Base = -> Sketch297
  Dir = (0,7.7,0)
  Solid = true
FEATURE [Part::Cut] Cut133
  Base = -> Extrude353
  Tool = -> Extrude354
FEATURE [Part::Chamfer] Chamfer040
  Base = -> Cut133
  Edges = 4 edges r=0.5: [Edge7,Edge9,Edge15,Edge17]
FEATURE [Part::Chamfer] Chamfer041
  Base = -> Chamfer040
  Edges = 1 edges r=1.2: [Edge13]
FEATURE [Sketcher::SketchObject] Sketch298
  ExternalGeometry = -> [Chamfer041]
  Placement = pos=(0,0,5.95) rot=(0,0,1;0rad)
  Support = -> Chamfer041 [Face5]
  sketch-geometry (4):
    g0: LineSegment StartX=-3 StartY=0 StartZ=0 EndX=3 EndY=0 EndZ=0
    g1: LineSegment StartX=3 StartY=0 StartZ=0 EndX=3 EndY=-3.1 EndZ=0
    g2: LineSegment StartX=3 StartY=-3.1 StartZ=0 EndX=-3 EndY=-3.1 EndZ=0
    g3: LineSegment StartX=-3 StartY=-3.1 StartZ=0 EndX=-3 EndY=0 EndZ=0
  constraints (12):
    c: Coincident(g0,g1)
    c: Coincident(g1,g2)
    c: Coincident(g2,g3)
    c: Coincident(g3,g0)
    c: Horizontal(g0)
    c: Horizontal(g2)
    c: Vertical(g1)
    c: Vertical(g3)
    c: PointOnObject(g0,g-1)
    c: DistanceX(g-3,g0) = 0.15
    c: Symmetric(g0,g0,g-2)
    c: DistanceY(g0,g1) = -3.1
FEATURE [Part::Extrusion] Extrude355
  Base = -> Sketch298
  Dir = (0,0,6.3)
  Solid = true
FEATURE [Sketcher::SketchObject] Sketch299
  ExternalGeometry = -> [Extrude355]
  Placement = pos=(0,-3.1,0) rot=(1,0,0;1.5708rad)
  Support = -> Extrude355 [Face3]
  sketch-geometry (1):
    g0: Circle CenterX=0 CenterY=9.5 CenterZ=0 NormalX=0 NormalY=0 NormalZ=1 Radius=1.65
  constraints (3):
    c: PointOnObject(g0,g-2)
    c: Radius(g0) = 1.65
    c: DistanceY(g0,g-3) = -3.55
FEATURE [Part::Extrusion] Extrude356
  Base = -> Sketch299
  Dir = (0,6,0)
  Solid = true
FEATURE [Part::Cut] Cut134
  Base = -> Extrude355
  Tool = -> Extrude356
FEATURE [Part::Fillet] Fillet030
  Base = -> Cut134
  Edges = 2 edges r=1.35: [Edge8,Edge11]
FEATURE [Part::MultiFuse] Fusion077
  Shapes = -> [Chamfer041]
FEATURE [Sketcher::SketchObject] Sketch300
  Placement = pos=(0,0,0) rot=(0,0.707107,0.707107;3.14159rad)
  Support = -> Fusion077 [Face7]
  sketch-geometry (4):
    g0: Circle CenterX=-1.27 CenterY=3.8 CenterZ=0 NormalX=0 NormalY=0 NormalZ=1 Radius=0.2
    g1: Circle CenterX=1.27 CenterY=3.8 CenterZ=0 NormalX=0 NormalY=0 NormalZ=1 Radius=0.2
    g2: Circle CenterX=-1.27 CenterY=-3.8 CenterZ=0 NormalX=0 NormalY=0 NormalZ=1 Radius=0.2
    g3: Circle CenterX=1.27 CenterY=-3.8 CenterZ=0 NormalX=0 NormalY=0 NormalZ=1 Radius=0.2
  constraints (9):
    c: Radius(g0) = 0.2
    c: Equal(g0,g1)
    c: Equal(g0,g3)
    c: Equal(g0,g2)
    c: Symmetric(g0,g1,g-2)
    c: Symmetric(g2,g3,g-2)
    c: Symmetric(g0,g2,g-1)
    c: DistanceX(g0,g1) = 2.54
    c: DistanceY(g1,g3) = -7.6
FEATURE [Part::Extrusion] Extrude357
  Base = -> Sketch300
  Dir = (0,7.8,0)
  Solid = true
FEATURE [Part::MultiFuse] Fusion078  label="Capteur_optique_013"
  Placement = pos=(-1716,-46,-20.7) rot=(0,0,1;0rad)
  Shapes = -> [Fusion077,Fillet030,Extrude357]
FEATURE [Sketcher::SketchObject] Sketch301
  Placement = pos=(0,0,0) rot=(1,0,0;1.5708rad)
  sketch-geometry (1):
    g0: Circle CenterX=0 CenterY=0 CenterZ=0 NormalX=0 NormalY=0 NormalZ=1 Radius=4
  constraints (2):
    c: Coincident(g0,g-1)
    c: Radius(g0) = 4
FEATURE [Part::Extrusion] Extrude358
  Base = -> Sketch301
  Dir = (0,50,0)
  Solid = true
FEATURE [Sketcher::SketchObject] Sketch302
  Placement = pos=(0,0,0) rot=(0.57735,0.57735,0.57735;2.0944rad)
  sketch-geometry (1):
    g0: Circle CenterX=6 CenterY=0 CenterZ=0 NormalX=0 NormalY=0 NormalZ=1 Radius=2
  constraints (3):
    c: DistanceX(g-1,g0) = 6
    c: Radius(g0) = 2
    c: PointOnObject(g0,g-1)
FEATURE [Part::Extrusion] Extrude359
  Base = -> Sketch302
  Dir = (4,0,0)
  Solid = true
FEATURE [Part::Extrusion] Extrude360
  Base = -> Sketch302
  Dir = (-4,0,0)
  Solid = true
FEATURE [Part::Cut] Cut135
  Base = -> Extrude358
  Tool = -> Extrude359
FEATURE [Part::Cut] Cut136  label="Axe_D8_013"
  Base = -> Cut135
  Placement = pos=(-1716,-86,0) rot=(0,0,1;0rad)
  Tool = -> Extrude360
FEATURE [Sketcher::SketchObject] Sketch303
  Placement = pos=(0,0,0) rot=(1,0,0;1.5708rad)
  sketch-geometry (1):
    g0: Circle CenterX=0 CenterY=0 CenterZ=0 NormalX=0 NormalY=0 NormalZ=1 Radius=2
  constraints (2):
    c: Coincident(g0,g-1)
    c: Radius(g0) = 2
FEATURE [Part::Extrusion] Extrude361  label="Axe_D4_013"
  Base = -> Sketch303
  Dir = (0,103.6,0)
  Placement = pos=(-1664.2,-80,0) rot=(0,0,1;1.5708rad)
  Solid = true
FEATURE [Sketcher::SketchObject] Sketch304
  Placement = pos=(0,0,0) rot=(1,0,0;1.5708rad)
  sketch-geometry (8):
    g0: LineSegment StartX=-50 StartY=0 StartZ=0 EndX=50 EndY=0 EndZ=0
    g1: LineSegment StartX=50 StartY=0 StartZ=0 EndX=50 EndY=-2 EndZ=0
    g2: LineSegment StartX=50 StartY=-2 StartZ=0 EndX=47 EndY=-2 EndZ=0
    g3: LineSegment StartX=47 StartY=-2 StartZ=0 EndX=44 EndY=-16 EndZ=0
    g4: LineSegment StartX=44 StartY=-16 StartZ=0 EndX=-44 EndY=-16 EndZ=0
    g5: LineSegment StartX=-44 StartY=-16 StartZ=0 EndX=-47 EndY=-2 EndZ=0
    g6: LineSegment StartX=-47 StartY=-2 StartZ=0 EndX=-50 EndY=-2 EndZ=0
    g7: LineSegment StartX=-50 StartY=-2 StartZ=0 EndX=-50 EndY=0 EndZ=0
  constraints (24):
    c: PointOnObject(g0,g-1)
    c: Horizontal(g0)
    c: Coincident(g0,g1)
    c: Vertical(g1)
    c: Coincident(g1,g2)
    c: Horizontal(g2)
    c: Coincident(g2,g3)
    c: Coincident(g3,g4)
    c: Horizontal(g4)
    c: Coincident(g4,g5)
    c: Coincident(g5,g6)
    c: Horizontal(g6)
    c: Coincident(g6,g7)
    c: Coincident(g7,g0)
    c: Vertical(g7)
    c: DistanceY(g0,g6) = -2
    c: DistanceX(g6,g5) = 3
    c: DistanceX(g0,g0) = 100
    c: Symmetric(g0,g0,g-2)
    c: Symmetric(g6,g1,g-2)
    c: Symmetric(g5,g2,g-2)
    c: Symmetric(g4,g3,g-2)
    c: DistanceX(g4,g3) = 88
    c: DistanceY(g0,g4) = -16
FEATURE [Part::Extrusion] Extrude362  label="Plaque_alveolaire_013"
  Base = -> Sketch304
  Dir = (0,2000,0)
  Placement = pos=(-1716,-62,22) rot=(0,0,1;3.14159rad)
  Solid = true
FEATURE [App::DocumentObjectGroup] Groupe018  label="Assemblage_miroir X=-286_002"
  Group = -> [Cut130,Fusion075,Extrude347,Part__Feature015,Extrude348,Fillet029,Fusion078,Cut136,Extrude361,Extrude362]
FEATURE [Sketcher::SketchObject] Sketch306
  Placement = pos=(0,0,0) rot=(1,0,0;1.5708rad)
  sketch-geometry (8):
    g0: LineSegment StartX=-21.15 StartY=16.15 StartZ=0 EndX=-16.15 EndY=21.15 EndZ=0
    g1: LineSegment StartX=-16.15 StartY=21.15 StartZ=0 EndX=16.15 EndY=21.15 EndZ=0
    g2: LineSegment StartX=16.15 StartY=21.15 StartZ=0 EndX=21.15 EndY=16.15 EndZ=0
    g3: LineSegment StartX=21.15 StartY=16.15 StartZ=0 EndX=21.15 EndY=-16.15 EndZ=0
    g4: LineSegment StartX=21.15 StartY=-16.15 StartZ=0 EndX=16.15 EndY=-21.15 EndZ=0
    g5: LineSegment StartX=16.15 StartY=-21.15 StartZ=0 EndX=-16.15 EndY=-21.15 EndZ=0
    g6: LineSegment StartX=-16.15 StartY=-21.15 StartZ=0 EndX=-21.15 EndY=-16.15 EndZ=0
    g7: LineSegment StartX=-21.15 StartY=-16.15 StartZ=0 EndX=-21.15 EndY=16.15 EndZ=0
  constraints (21):
    c: Coincident(g0,g1)
    c: Horizontal(g1)
    c: Coincident(g1,g2)
    c: Coincident(g2,g3)
    c: Vertical(g3)
    c: Coincident(g3,g4)
    c: Coincident(g4,g5)
    c: Horizontal(g5)
    c: Coincident(g5,g6)
    c: Coincident(g6,g7)
    c: Coincident(g7,g0)
    c: Angle(g7,g0) = 2.35619
    c: Distance(g0,g7) = 5
    c: Distance(g2,g7) = 42.3
    c: Distance(g5,g1) = 42.3
    c: Symmetric(g6,g3,g-2)
    c: Symmetric(g5,g4,g-2)
    c: Symmetric(g0,g2,g-2)
    c: Symmetric(g0,g1,g-2)
    c: Symmetric(g0,g6,g-1)
    c: Symmetric(g0,g5,g-1)
FEATURE [Part::Extrusion] Extrude364
  Base = -> Sketch306
  Dir = (0,48,0)
  Solid = true
FEATURE [Sketcher::SketchObject] Sketch307
  Placement = pos=(0,0,0) rot=(1,0,0;1.5708rad)
  Support = -> Extrude364 [Face9]
  sketch-geometry (1):
    g0: Circle CenterX=0 CenterY=0 CenterZ=0 NormalX=0 NormalY=0 NormalZ=1 Radius=11
  constraints (2):
    c: Coincident(g0,g-1)
    c: Radius(g0) = 11
FEATURE [Part::Extrusion] Extrude365
  Base = -> Sketch307
  Dir = (0,-2,0)
  Solid = true
FEATURE [Sketcher::SketchObject] Sketch308
  Placement = pos=(0,-2,0) rot=(1,0,0;1.5708rad)
  Support = -> Extrude365 [Face3]
  sketch-geometry (1):
    g0: Circle CenterX=0 CenterY=0 CenterZ=0 NormalX=0 NormalY=0 NormalZ=1 Radius=2.5
  constraints (2):
    c: Coincident(g0,g-1)
    c: Radius(g0) = 2.5
FEATURE [Part::Extrusion] Extrude366
  Base = -> Sketch308
  Dir = (0,-22,0)
  Solid = true
FEATURE [Part::Chamfer] Chamfer042
  Base = -> Extrude366
  Edges = 1 edges r=0.8: [Edge3]
FEATURE [Sketcher::SketchObject] Sketch309
  Placement = pos=(0,0,0) rot=(1,0,0;1.5708rad)
  Support = -> Extrude364 [Face9]
  sketch-geometry (4):
    g0: Circle CenterX=-15.5 CenterY=15.5 CenterZ=0 NormalX=0 NormalY=0 NormalZ=1 Radius=2
    g1: Circle CenterX=15.5 CenterY=15.5 CenterZ=0 NormalX=0 NormalY=0 NormalZ=1 Radius=2
    g2: Circle CenterX=-15.5 CenterY=-15.5 CenterZ=0 NormalX=0 NormalY=0 NormalZ=1 Radius=2
    g3: Circle CenterX=15.5 CenterY=-15.5 CenterZ=0 NormalX=0 NormalY=0 NormalZ=1 Radius=2
  constraints (9):
    c: Distance(g0,g1) = 31
    c: Distance(g0,g2) = 31
    c: Symmetric(g0,g2,g-1)
    c: Symmetric(g0,g1,g-2)
    c: Symmetric(g2,g3,g-2)
    c: Radius(g0) = 2
    c: Equal(g0,g1)
    c: Equal(g0,g2)
    c: Equal(g0,g3)
FEATURE [Part::Extrusion] Extrude367
  Base = -> Sketch309
  Dir = (0,4.5,0)
  Solid = true
FEATURE [Part::Cut] Cut137
  Base = -> Extrude364
  Tool = -> Extrude367
FEATURE [Sketcher::SketchObject] Sketch310
  Placement = pos=(0,0,0) rot=(1,0,0;1.5708rad)
  sketch-geometry (1):
    g0: Circle CenterX=0 CenterY=0 CenterZ=0 NormalX=0 NormalY=0 NormalZ=1 Radius=9
  constraints (2):
    c: Coincident(g0,g-1)
    c: Radius(g0) = 9
FEATURE [Part::Extrusion] Extrude368
  Base = -> Sketch310
  Dir = (0,25,0)
  Solid = true
FEATURE [Sketcher::SketchObject] Sketch311
  Placement = pos=(0,0,0) rot=(1,0,0;1.5708rad)
  sketch-geometry (1):
    g0: Circle CenterX=0 CenterY=0 CenterZ=0 NormalX=0 NormalY=0 NormalZ=1 Radius=2.5
  constraints (2):
    c: Coincident(g0,g-1)
    c: Radius(g0) = 2.5
FEATURE [Part::Extrusion] Extrude369
  Base = -> Sketch311
  Dir = (0,10,0)
  Solid = true
FEATURE [Part::Cut] Cut138
  Base = -> Extrude368
  Tool = -> Extrude369
FEATURE [Sketcher::SketchObject] Sketch312
  Placement = pos=(0,25,0) rot=(0,0.707107,0.707107;3.14159rad)
  Support = -> Cut138 [Face3]
  sketch-geometry (1):
    g0: Circle CenterX=0 CenterY=0 CenterZ=0 NormalX=0 NormalY=0 NormalZ=1 Radius=4
  constraints (2):
    c: Coincident(g0,g-1)
    c: Radius(g0) = 4
FEATURE [Part::Extrusion] Extrude370
  Base = -> Sketch312
  Dir = (0,-10,0)
  Solid = true
FEATURE [Part::Cut] Cut139  label="Accouplement_014"
  Base = -> Cut138
  Placement = pos=(-1859,-12,0) rot=(1,0,0;3.14159rad)
  Tool = -> Extrude370
FEATURE [Part::Fuse] Fusion079
  Base = -> Extrude365
  Tool = -> Cut137
FEATURE [Part::Fuse] Fusion080  label="Moteur_014"
  Base = -> Chamfer042
  Placement = pos=(-1859,0,0) rot=(0,0,1;0rad)
  Tool = -> Fusion079
FEATURE [Sketcher::SketchObject] Sketch313
  Placement = pos=(0,0,0) rot=(1,0,0;1.5708rad)
  sketch-geometry (4):
    g0: LineSegment StartX=-50 StartY=0 StartZ=0 EndX=-47 EndY=0 EndZ=0
    g1: LineSegment StartX=47 StartY=0 StartZ=0 EndX=50 EndY=0 EndZ=0
    g2: ArcOfCircle CenterX=0 CenterY=0 CenterZ=0 NormalX=0 NormalY=0 NormalZ=1 Radius=47 StartAngle=3.14159 EndAngle=6.28319
    g3: ArcOfCircle CenterX=0 CenterY=0 CenterZ=0 NormalX=0 NormalY=0 NormalZ=1 Radius=50 StartAngle=3.14159 EndAngle=6.28319
  constraints (13):
    c: Horizontal(g0)
    c: PointOnObject(g1,g-1)
    c: Horizontal(g1)
    c: Coincident(g2,g-1)
    c: PointOnObject(g2,g-1)
    c: Coincident(g3,g-1)
    c: Coincident(g3,g1)
    c: PointOnObject(g3,g-1)
    c: Coincident(g0,g3)
    c: Coincident(g0,g2)
    c: Distance(g0,g1) = 100
    c: Distance(g0,g0) = 3
    c: Coincident(g1,g2)
FEATURE [Part::Extrusion] Extrude371  label="Demi_tube_sous_miroir_014"
  Base = -> Sketch313
  Dir = (0,2000,0)
  Placement = pos=(-1859,-62,20) rot=(0,0,1;3.14159rad)
  Solid = true
FEATURE [Part::Feature] Part__Feature016  label="Coussinet_autolub_C2-151-8-128_014"
  Placement = pos=(-1859,-46,0) rot=(0,0,1;1.5708rad)
  shape: bbox 16 x 8 x 16 mm, 12 faces (baked)
FEATURE [Sketcher::SketchObject] Sketch314
  Placement = pos=(0,0,0) rot=(1,0,0;1.5708rad)
  sketch-geometry (21):
    g0: Circle CenterX=0 CenterY=0 CenterZ=0 NormalX=0 NormalY=0 NormalZ=1 Radius=6
    g1: LineSegment StartX=-20.5 StartY=15 StartZ=0 EndX=20.5 EndY=15 EndZ=0
    g2: ArcOfCircle CenterX=20.5 CenterY=13 CenterZ=0 NormalX=0 NormalY=0 NormalZ=1 Radius=2 StartAngle=6.28319 EndAngle=7.85398
    g3: LineSegment StartX=22.5 StartY=13 StartZ=0 EndX=22.5 EndY=-73 EndZ=0
    g4: LineSegment StartX=-22.5 StartY=13 StartZ=0 EndX=-22.5 EndY=-73 EndZ=0
    g5: ArcOfCircle CenterX=-20.5 CenterY=13 CenterZ=0 NormalX=0 NormalY=0 NormalZ=1 Radius=2 StartAngle=1.5708 EndAngle=3.14159
    g6: ArcOfCircle CenterX=-20.5 CenterY=-73 CenterZ=0 NormalX=0 NormalY=0 NormalZ=1 Radius=2 StartAngle=3.14159 EndAngle=4.71239
    g7: ArcOfCircle CenterX=20.5 CenterY=-73 CenterZ=0 NormalX=0 NormalY=0 NormalZ=1 Radius=2 StartAngle=4.71239 EndAngle=6.28319
    g8: LineSegment StartX=-20.5 StartY=-75 StartZ=0 EndX=20.5 EndY=-75 EndZ=0
    g9: ArcOfCircle CenterX=0 CenterY=-16.7 CenterZ=0 NormalX=0 NormalY=0 NormalZ=1 Radius=1.5 StartAngle=0 EndAngle=3.14159
    g10: ArcOfCircle CenterX=0 CenterY=-24.3 CenterZ=0 NormalX=0 NormalY=0 NormalZ=1 Radius=1.5 StartAngle=3.14159 EndAngle=6.28319
    g11: LineSegment StartX=-1.5 StartY=-16.7 StartZ=0 EndX=-1.5 EndY=-24.3 EndZ=0
    g12: LineSegment StartX=1.5 StartY=-16.7 StartZ=0 EndX=1.5 EndY=-24.3 EndZ=0
    g13: Circle CenterX=-12.5 CenterY=-45 CenterZ=0 NormalX=0 NormalY=0 NormalZ=1 Radius=3.5
    g14: Circle CenterX=12.5 CenterY=-45 CenterZ=0 NormalX=0 NormalY=0 NormalZ=1 Radius=3.5
    g15: Circle CenterX=-12.5 CenterY=-65 CenterZ=0 NormalX=0 NormalY=0 NormalZ=1 Radius=3.5
    g16: Circle CenterX=12.5 CenterY=-65 CenterZ=0 NormalX=0 NormalY=0 NormalZ=1 Radius=3.5
    g17: LineSegment [constr] StartX=-12.5 StartY=-45 StartZ=0 EndX=12.5 EndY=-45 EndZ=0
    g18: LineSegment [constr] StartX=-12.5 StartY=-45 StartZ=0 EndX=-12.5 EndY=-65 EndZ=0
    g19: LineSegment [constr] StartX=-12.5 StartY=-65 StartZ=0 EndX=12.5 EndY=-65 EndZ=0
    g20: LineSegment [constr] StartX=12.5 StartY=-45 StartZ=0 EndX=12.5 EndY=-65 EndZ=0
  constraints (59):
    c: Coincident(g0,g-1)
    c: Radius(g0) = 6
    c: Horizontal(g1)
    c: Coincident(g2,g1)
    c: Coincident(g3,g2)
    c: Vertical(g3)
    c: Vertical(g4)
    c: Coincident(g5,g1)
    c: Coincident(g5,g4)
    c: Coincident(g7,g3)
    c: Coincident(g8,g6)
    c: Coincident(g8,g7)
    c: Tangent(g8,g7)
    c: Tangent(g5,g4)
    c: Tangent(g5,g1)
    c: Tangent(g1,g2)
    c: Tangent(g2,g3)
    c: Coincident(g4,g6)
    c: Tangent(g6,g4)
    c: Tangent(g6,g8)
    c: Horizontal(g8)
    c: Tangent(g7,g3)
    c: Distance(g4,g2) = 45
    c: Symmetric(g4,g2,g-2)
    c: Distance(g1,g6) = 90
    c: DistanceY(g-1,g1) = 15
    c: Tangent(g9,g12) = 1.5708
    c: Tangent(g9,g11) = -1.5708
    c: Tangent(g11,g10) = -1.5708
    c: Tangent(g12,g10) = 1.5708
    c: Vertical(g11)
    c: Equal(g9,g10)
    c: PointOnObject(g9,g-2)
    c: Distance(g-1,g9) = 16.7
    c: Distance(g9,g10) = 7.6
    c: Radius(g9) = 1.5
    c: Radius(g13) = 3.5
    c: Equal(g13,g14)
    c: Equal(g13,g16)
    c: Equal(g13,g15)
    c: Radius(g5) = 2
    c: Equal(g5,g7)
    c: Equal(g5,g6)
    c: DistanceY(g-1,g13) = -45
    c: Coincident(g17,g13)
    c: Coincident(g17,g14)
    c: Horizontal(g17)
    c: Coincident(g18,g13)
    c: Coincident(g18,g15)
    c: Coincident(g19,g15)
    c: Coincident(g19,g16)
    c: Horizontal(g19)
    c: Coincident(g20,g14)
    c: Coincident(g20,g16)
    c: Vertical(g18)
    c: Vertical(g20)
    c: Distance(g13,g15) = 20
    c: Distance(g13,g14) = 25
    c: Symmetric(g13,g14,g-2)
FEATURE [Part::Extrusion] Extrude372  label="Plaque_support_014"
  Base = -> Sketch314
  Dir = (0,6,0)
  Placement = pos=(-1859,-46,0) rot=(0,0,1;0rad)
  Solid = true
FEATURE [Sketcher::SketchObject] Sketch315
  Placement = pos=(0,0,0) rot=(0.57735,0.57735,0.57735;2.0944rad)
  sketch-geometry (8):
    g0: LineSegment StartX=0 StartY=33 StartZ=0 EndX=-2 EndY=33 EndZ=0
    g1: LineSegment StartX=-2 StartY=33 StartZ=0 EndX=-2 EndY=-24 EndZ=0
    g2: ArcOfCircle CenterX=-4 CenterY=-24 CenterZ=0 NormalX=0 NormalY=0 NormalZ=1 Radius=2 StartAngle=4.71239 EndAngle=6.28319
    g3: LineSegment StartX=-4 StartY=-26 StartZ=0 EndX=-38 EndY=-26 EndZ=0
    g4: LineSegment StartX=-38 StartY=-26 StartZ=0 EndX=-38 EndY=-28 EndZ=0
    g5: LineSegment StartX=-38 StartY=-28 StartZ=0 EndX=-4 EndY=-28 EndZ=0
    g6: ArcOfCircle CenterX=-4 CenterY=-24 CenterZ=0 NormalX=0 NormalY=0 NormalZ=1 Radius=4 StartAngle=4.71239 EndAngle=6.28319
    g7: LineSegment StartX=0 StartY=-24 StartZ=0 EndX=0 EndY=33 EndZ=0
  constraints (22):
    c: PointOnObject(g0,g-2)
    c: Horizontal(g0)
    c: Coincident(g0,g1)
    c: Vertical(g1)
    c: Tangent(g1,g2) = 1.5708
    c: Tangent(g2,g3) = 1.5708
    c: Coincident(g3,g4)
    c: Vertical(g4)
    c: Coincident(g4,g5)
    c: Horizontal(g5)
    c: Tangent(g5,g6) = -1.5708
    c: PointOnObject(g6,g-2)
    c: Tangent(g6,g7) = -1.5708
    c: Coincident(g7,g0)
    c: Horizontal(g3)
    c: DistanceX(g0,g0) = 2
    c: Radius(g2) = 2
    c: Radius(g6) = 4
    c: DistanceY(g3,g4) = -2
    c: Distance(g-1,g0) = 33
    c: DistanceY(g-1,g5) = -28
    c: DistanceX(g6,g4) = -38
FEATURE [Part::Extrusion] Extrude373
  Base = -> Sketch315
  Dir = (-32.5,0,0)
  Solid = true
FEATURE [Part::Extrusion] Extrude374
  Base = -> Sketch315
  Dir = (32.5,0,0)
  Solid = true
FEATURE [Part::MultiFuse] Fusion081
  Shapes = -> [Extrude373,Extrude374]
FEATURE [Sketcher::SketchObject] Sketch316
  Placement = pos=(0,-2,0) rot=(1,0,0;1.5708rad)
  Support = -> Fusion081 [Face3]
  sketch-geometry (9):
    g0: ArcOfCircle CenterX=0 CenterY=0 CenterZ=0 NormalX=0 NormalY=0 NormalZ=1 Radius=32.5 StartAngle=0 EndAngle=3.14159
    g1: LineSegment StartX=-32.5 StartY=0 StartZ=0 EndX=-32.5 EndY=34 EndZ=0
    g2: LineSegment StartX=-32.5 StartY=34 StartZ=0 EndX=32.5 EndY=34 EndZ=0
    g3: LineSegment StartX=32.5 StartY=34 StartZ=0 EndX=32.5 EndY=0 EndZ=0
    g4: Circle CenterX=0 CenterY=0 CenterZ=0 NormalX=0 NormalY=0 NormalZ=1 Radius=11
    g5: Circle CenterX=-15.5 CenterY=15.5 CenterZ=0 NormalX=0 NormalY=0 NormalZ=1 Radius=2
    g6: Circle CenterX=15.5 CenterY=15.5 CenterZ=0 NormalX=0 NormalY=0 NormalZ=1 Radius=2
    g7: Circle CenterX=-15.5 CenterY=-15.5 CenterZ=0 NormalX=0 NormalY=0 NormalZ=1 Radius=2
    g8: Circle CenterX=15.5 CenterY=-15.5 CenterZ=0 NormalX=0 NormalY=0 NormalZ=1 Radius=2
  constraints (23):
    c: Coincident(g0,g-1)
    c: PointOnObject(g0,g-1)
    c: PointOnObject(g0,g-1)
    c: Coincident(g1,g0)
    c: Vertical(g1)
    c: Coincident(g1,g2)
    c: Horizontal(g2)
    c: Coincident(g2,g3)
    c: Coincident(g3,g0)
    c: Vertical(g3)
    c: DistanceY(g1,g0) = -34
    c: Coincident(g4,g-1)
    c: Radius(g4) = 11
    c: DistanceX(g1,g2) = 65
    c: Radius(g5) = 2
    c: Equal(g5,g6)
    c: Equal(g5,g8)
    c: Equal(g5,g7)
    c: Symmetric(g5,g6,g-2)
    c: Symmetric(g5,g7,g-1)
    c: Symmetric(g7,g8,g-2)
    c: DistanceX(g5,g6) = 31
    c: DistanceY(g5,g7) = -31
FEATURE [Part::Extrusion] Extrude375
  Base = -> Sketch316
  Dir = (0,2,0)
  Solid = true
FEATURE [Part::Cut] Cut140
  Base = -> Fusion081
  Tool = -> Extrude375
FEATURE [Sketcher::SketchObject] Sketch317
  ExternalGeometry = -> [Cut140]
  Placement = pos=(0,0,-26) rot=(0,0,1;0rad)
  Support = -> Cut140 [Face5]
  sketch-geometry (5):
    g0: Circle CenterX=-25 CenterY=-12 CenterZ=0 NormalX=0 NormalY=0 NormalZ=1 Radius=3.5
    g1: Circle CenterX=-25 CenterY=-30 CenterZ=0 NormalX=0 NormalY=0 NormalZ=1 Radius=3.5
    g2: Circle CenterX=25 CenterY=-12 CenterZ=0 NormalX=0 NormalY=0 NormalZ=1 Radius=3.5
    g3: Circle CenterX=25 CenterY=-30 CenterZ=0 NormalX=0 NormalY=0 NormalZ=1 Radius=3.5
    g4: LineSegment [constr] StartX=-25 StartY=-12 StartZ=0 EndX=-25 EndY=-30 EndZ=0
  constraints (12):
    c: Radius(g0) = 3.5
    c: Equal(g0,g2)
    c: Equal(g0,g3)
    c: Equal(g0,g1)
    c: Symmetric(g0,g2,g-2)
    c: Symmetric(g1,g3,g-2)
    c: Coincident(g4,g0)
    c: Coincident(g4,g1)
    c: Vertical(g4)
    c: DistanceY(g0,g1) = -18
    c: DistanceY(g-3,g1) = 8
    c: DistanceX(g0,g2) = 50
FEATURE [Part::Extrusion] Extrude376
  Base = -> Sketch317
  Dir = (0,0,-2)
  Solid = true
FEATURE [Part::Cut] Cut141
  Base = -> Cut140
  Tool = -> Extrude376
FEATURE [Part::Fillet] Fillet031  label="Plaque_moteur_014"
  Base = -> Cut141
  Edges = 2 edges r=4: [Edge5,Edge59]
  Placement = pos=(-1859,0,0) rot=(0,0,1;0rad)
FEATURE [Sketcher::SketchObject] Sketch318
  Placement = pos=(0,0,0) rot=(1,0,0;1.5708rad)
  sketch-geometry (4):
    g0: LineSegment StartX=-3.15 StartY=5.95 StartZ=0 EndX=3.15 EndY=5.95 EndZ=0
    g1: LineSegment StartX=3.15 StartY=5.95 StartZ=0 EndX=3.15 EndY=-5.95 EndZ=0
    g2: LineSegment StartX=3.15 StartY=-5.95 StartZ=0 EndX=-3.15 EndY=-5.95 EndZ=0
    g3: LineSegment StartX=-3.15 StartY=-5.95 StartZ=0 EndX=-3.15 EndY=5.95 EndZ=0
  constraints (12):
    c: Coincident(g0,g1)
    c: Coincident(g1,g2)
    c: Coincident(g2,g3)
    c: Coincident(g3,g0)
    c: Horizontal(g0)
    c: Horizontal(g2)
    c: Vertical(g1)
    c: Vertical(g3)
    c: DistanceX(g0,g0) = 6.3
    c: DistanceY(g0,g2) = -11.9
    c: Symmetric(g0,g0,g-2)
    c: Symmetric(g0,g1,g-1)
FEATURE [Part::Extrusion] Extrude377
  Base = -> Sketch318
  Dir = (0,-10.8,0)
  Solid = true
FEATURE [Sketcher::SketchObject] Sketch319
  ExternalGeometry = -> [Extrude377]
  Placement = pos=(0,-10.8,0) rot=(1,0,0;1.5708rad)
  Support = -> Extrude377 [Face6]
  sketch-geometry (4):
    g0: LineSegment StartX=-3.15 StartY=1.55 StartZ=0 EndX=3.15 EndY=1.55 EndZ=0
    g1: LineSegment StartX=3.15 StartY=1.55 StartZ=0 EndX=3.15 EndY=-1.55 EndZ=0
    g2: LineSegment StartX=3.15 StartY=-1.55 StartZ=0 EndX=-3.15 EndY=-1.55 EndZ=0
    g3: LineSegment StartX=-3.15 StartY=-1.55 StartZ=0 EndX=-3.15 EndY=1.55 EndZ=0
  constraints (12):
    c: Coincident(g0,g1)
    c: Coincident(g1,g2)
    c: Coincident(g2,g3)
    c: Coincident(g3,g0)
    c: Horizontal(g0)
    c: Horizontal(g2)
    c: Vertical(g1)
    c: Vertical(g3)
    c: PointOnObject(g0,g-4)
    c: PointOnObject(g0,g-3)
    c: DistanceY(g0,g2) = -3.1
    c: Symmetric(g0,g1,g-1)
FEATURE [Part::Extrusion] Extrude378
  Base = -> Sketch319
  Dir = (0,7.7,0)
  Solid = true
FEATURE [Part::Cut] Cut142
  Base = -> Extrude377
  Tool = -> Extrude378
FEATURE [Part::Chamfer] Chamfer043
  Base = -> Cut142
  Edges = 4 edges r=0.5: [Edge7,Edge9,Edge15,Edge17]
FEATURE [Part::Chamfer] Chamfer044
  Base = -> Chamfer043
  Edges = 1 edges r=1.2: [Edge13]
FEATURE [Sketcher::SketchObject] Sketch320
  ExternalGeometry = -> [Chamfer044]
  Placement = pos=(0,0,5.95) rot=(0,0,1;0rad)
  Support = -> Chamfer044 [Face5]
  sketch-geometry (4):
    g0: LineSegment StartX=-3 StartY=0 StartZ=0 EndX=3 EndY=0 EndZ=0
    g1: LineSegment StartX=3 StartY=0 StartZ=0 EndX=3 EndY=-3.1 EndZ=0
    g2: LineSegment StartX=3 StartY=-3.1 StartZ=0 EndX=-3 EndY=-3.1 EndZ=0
    g3: LineSegment StartX=-3 StartY=-3.1 StartZ=0 EndX=-3 EndY=0 EndZ=0
  constraints (12):
    c: Coincident(g0,g1)
    c: Coincident(g1,g2)
    c: Coincident(g2,g3)
    c: Coincident(g3,g0)
    c: Horizontal(g0)
    c: Horizontal(g2)
    c: Vertical(g1)
    c: Vertical(g3)
    c: PointOnObject(g0,g-1)
    c: DistanceX(g-3,g0) = 0.15
    c: Symmetric(g0,g0,g-2)
    c: DistanceY(g0,g1) = -3.1
FEATURE [Part::Extrusion] Extrude379
  Base = -> Sketch320
  Dir = (0,0,6.3)
  Solid = true
FEATURE [Sketcher::SketchObject] Sketch321
  ExternalGeometry = -> [Extrude379]
  Placement = pos=(0,-3.1,0) rot=(1,0,0;1.5708rad)
  Support = -> Extrude379 [Face3]
  sketch-geometry (1):
    g0: Circle CenterX=0 CenterY=9.5 CenterZ=0 NormalX=0 NormalY=0 NormalZ=1 Radius=1.65
  constraints (3):
    c: PointOnObject(g0,g-2)
    c: Radius(g0) = 1.65
    c: DistanceY(g0,g-3) = -3.55
FEATURE [Part::Extrusion] Extrude380
  Base = -> Sketch321
  Dir = (0,6,0)
  Solid = true
FEATURE [Part::Cut] Cut143
  Base = -> Extrude379
  Tool = -> Extrude380
FEATURE [Part::Fillet] Fillet032
  Base = -> Cut143
  Edges = 2 edges r=1.35: [Edge8,Edge11]
FEATURE [Part::MultiFuse] Fusion082
  Shapes = -> [Chamfer044]
FEATURE [Sketcher::SketchObject] Sketch322
  Placement = pos=(0,0,0) rot=(0,0.707107,0.707107;3.14159rad)
  Support = -> Fusion082 [Face7]
  sketch-geometry (4):
    g0: Circle CenterX=-1.27 CenterY=3.8 CenterZ=0 NormalX=0 NormalY=0 NormalZ=1 Radius=0.2
    g1: Circle CenterX=1.27 CenterY=3.8 CenterZ=0 NormalX=0 NormalY=0 NormalZ=1 Radius=0.2
    g2: Circle CenterX=-1.27 CenterY=-3.8 CenterZ=0 NormalX=0 NormalY=0 NormalZ=1 Radius=0.2
    g3: Circle CenterX=1.27 CenterY=-3.8 CenterZ=0 NormalX=0 NormalY=0 NormalZ=1 Radius=0.2
  constraints (9):
    c: Radius(g0) = 0.2
    c: Equal(g0,g1)
    c: Equal(g0,g3)
    c: Equal(g0,g2)
    c: Symmetric(g0,g1,g-2)
    c: Symmetric(g2,g3,g-2)
    c: Symmetric(g0,g2,g-1)
    c: DistanceX(g0,g1) = 2.54
    c: DistanceY(g1,g3) = -7.6
FEATURE [Part::Extrusion] Extrude381
  Base = -> Sketch322
  Dir = (0,7.8,0)
  Solid = true
FEATURE [Part::MultiFuse] Fusion083  label="Capteur_optique_014"
  Placement = pos=(-1859,-46,-20.7) rot=(0,0,1;0rad)
  Shapes = -> [Fusion082,Fillet032,Extrude381]
FEATURE [Sketcher::SketchObject] Sketch323
  Placement = pos=(0,0,0) rot=(1,0,0;1.5708rad)
  sketch-geometry (1):
    g0: Circle CenterX=0 CenterY=0 CenterZ=0 NormalX=0 NormalY=0 NormalZ=1 Radius=4
  constraints (2):
    c: Coincident(g0,g-1)
    c: Radius(g0) = 4
FEATURE [Part::Extrusion] Extrude382
  Base = -> Sketch323
  Dir = (0,50,0)
  Solid = true
FEATURE [Sketcher::SketchObject] Sketch324
  Placement = pos=(0,0,0) rot=(0.57735,0.57735,0.57735;2.0944rad)
  sketch-geometry (1):
    g0: Circle CenterX=6 CenterY=0 CenterZ=0 NormalX=0 NormalY=0 NormalZ=1 Radius=2
  constraints (3):
    c: DistanceX(g-1,g0) = 6
    c: Radius(g0) = 2
    c: PointOnObject(g0,g-1)
FEATURE [Part::Extrusion] Extrude383
  Base = -> Sketch324
  Dir = (4,0,0)
  Solid = true
FEATURE [Part::Extrusion] Extrude384
  Base = -> Sketch324
  Dir = (-4,0,0)
  Solid = true
FEATURE [Part::Cut] Cut144
  Base = -> Extrude382
  Tool = -> Extrude383
FEATURE [Part::Cut] Cut145  label="Axe_D8_014"
  Base = -> Cut144
  Placement = pos=(-1859,-86,0) rot=(0,0,1;0rad)
  Tool = -> Extrude384
FEATURE [Sketcher::SketchObject] Sketch325
  Placement = pos=(0,0,0) rot=(1,0,0;1.5708rad)
  sketch-geometry (1):
    g0: Circle CenterX=0 CenterY=0 CenterZ=0 NormalX=0 NormalY=0 NormalZ=1 Radius=2
  constraints (2):
    c: Coincident(g0,g-1)
    c: Radius(g0) = 2
FEATURE [Part::Extrusion] Extrude385  label="Axe_D4_014"
  Base = -> Sketch325
  Dir = (0,103.6,0)
  Placement = pos=(-1807.2,-80,0) rot=(0,0,1;1.5708rad)
  Solid = true
FEATURE [Sketcher::SketchObject] Sketch326
  Placement = pos=(0,0,0) rot=(1,0,0;1.5708rad)
  sketch-geometry (8):
    g0: LineSegment StartX=-50 StartY=0 StartZ=0 EndX=50 EndY=0 EndZ=0
    g1: LineSegment StartX=50 StartY=0 StartZ=0 EndX=50 EndY=-2 EndZ=0
    g2: LineSegment StartX=50 StartY=-2 StartZ=0 EndX=47 EndY=-2 EndZ=0
    g3: LineSegment StartX=47 StartY=-2 StartZ=0 EndX=44 EndY=-16 EndZ=0
    g4: LineSegment StartX=44 StartY=-16 StartZ=0 EndX=-44 EndY=-16 EndZ=0
    g5: LineSegment StartX=-44 StartY=-16 StartZ=0 EndX=-47 EndY=-2 EndZ=0
    g6: LineSegment StartX=-47 StartY=-2 StartZ=0 EndX=-50 EndY=-2 EndZ=0
    g7: LineSegment StartX=-50 StartY=-2 StartZ=0 EndX=-50 EndY=0 EndZ=0
  constraints (24):
    c: PointOnObject(g0,g-1)
    c: Horizontal(g0)
    c: Coincident(g0,g1)
    c: Vertical(g1)
    c: Coincident(g1,g2)
    c: Horizontal(g2)
    c: Coincident(g2,g3)
    c: Coincident(g3,g4)
    c: Horizontal(g4)
    c: Coincident(g4,g5)
    c: Coincident(g5,g6)
    c: Horizontal(g6)
    c: Coincident(g6,g7)
    c: Coincident(g7,g0)
    c: Vertical(g7)
    c: DistanceY(g0,g6) = -2
    c: DistanceX(g6,g5) = 3
    c: DistanceX(g0,g0) = 100
    c: Symmetric(g0,g0,g-2)
    c: Symmetric(g6,g1,g-2)
    c: Symmetric(g5,g2,g-2)
    c: Symmetric(g4,g3,g-2)
    c: DistanceX(g4,g3) = 88
    c: DistanceY(g0,g4) = -16
FEATURE [Part::Extrusion] Extrude386  label="Plaque_alveolaire_014"
  Base = -> Sketch326
  Dir = (0,2000,0)
  Placement = pos=(-1859,-62,22) rot=(0,0,1;3.14159rad)
  Solid = true
FEATURE [App::DocumentObjectGroup] Groupe019  label="Assemblage_miroir X=-429_002"
  Group = -> [Cut139,Fusion080,Extrude371,Part__Feature016,Extrude372,Fillet031,Fusion083,Cut145,Extrude385,Extrude386]
FEATURE [Sketcher::SketchObject] Sketch327
  Placement = pos=(0,0,0) rot=(1,0,0;1.5708rad)
  sketch-geometry (8):
    g0: LineSegment StartX=-21.15 StartY=16.15 StartZ=0 EndX=-16.15 EndY=21.15 EndZ=0
    g1: LineSegment StartX=-16.15 StartY=21.15 StartZ=0 EndX=16.15 EndY=21.15 EndZ=0
    g2: LineSegment StartX=16.15 StartY=21.15 StartZ=0 EndX=21.15 EndY=16.15 EndZ=0
    g3: LineSegment StartX=21.15 StartY=16.15 StartZ=0 EndX=21.15 EndY=-16.15 EndZ=0
    g4: LineSegment StartX=21.15 StartY=-16.15 StartZ=0 EndX=16.15 EndY=-21.15 EndZ=0
    g5: LineSegment StartX=16.15 StartY=-21.15 StartZ=0 EndX=-16.15 EndY=-21.15 EndZ=0
    g6: LineSegment StartX=-16.15 StartY=-21.15 StartZ=0 EndX=-21.15 EndY=-16.15 EndZ=0
    g7: LineSegment StartX=-21.15 StartY=-16.15 StartZ=0 EndX=-21.15 EndY=16.15 EndZ=0
  constraints (21):
    c: Coincident(g0,g1)
    c: Horizontal(g1)
    c: Coincident(g1,g2)
    c: Coincident(g2,g3)
    c: Vertical(g3)
    c: Coincident(g3,g4)
    c: Coincident(g4,g5)
    c: Horizontal(g5)
    c: Coincident(g5,g6)
    c: Coincident(g6,g7)
    c: Coincident(g7,g0)
    c: Angle(g7,g0) = 2.35619
    c: Distance(g0,g7) = 5
    c: Distance(g2,g7) = 42.3
    c: Distance(g5,g1) = 42.3
    c: Symmetric(g6,g3,g-2)
    c: Symmetric(g5,g4,g-2)
    c: Symmetric(g0,g2,g-2)
    c: Symmetric(g0,g1,g-2)
    c: Symmetric(g0,g6,g-1)
    c: Symmetric(g0,g5,g-1)
FEATURE [Part::Extrusion] Extrude387
  Base = -> Sketch327
  Dir = (0,48,0)
  Solid = true
FEATURE [Sketcher::SketchObject] Sketch328
  Placement = pos=(0,0,0) rot=(1,0,0;1.5708rad)
  Support = -> Extrude387 [Face9]
  sketch-geometry (1):
    g0: Circle CenterX=0 CenterY=0 CenterZ=0 NormalX=0 NormalY=0 NormalZ=1 Radius=11
  constraints (2):
    c: Coincident(g0,g-1)
    c: Radius(g0) = 11
FEATURE [Part::Extrusion] Extrude388
  Base = -> Sketch328
  Dir = (0,-2,0)
  Solid = true
FEATURE [Sketcher::SketchObject] Sketch329
  Placement = pos=(0,-2,0) rot=(1,0,0;1.5708rad)
  Support = -> Extrude388 [Face3]
  sketch-geometry (1):
    g0: Circle CenterX=0 CenterY=0 CenterZ=0 NormalX=0 NormalY=0 NormalZ=1 Radius=2.5
  constraints (2):
    c: Coincident(g0,g-1)
    c: Radius(g0) = 2.5
FEATURE [Part::Extrusion] Extrude389
  Base = -> Sketch329
  Dir = (0,-22,0)
  Solid = true
FEATURE [Part::Chamfer] Chamfer045
  Base = -> Extrude389
  Edges = 1 edges r=0.8: [Edge3]
FEATURE [Sketcher::SketchObject] Sketch330
  Placement = pos=(0,0,0) rot=(1,0,0;1.5708rad)
  Support = -> Extrude387 [Face9]
  sketch-geometry (4):
    g0: Circle CenterX=-15.5 CenterY=15.5 CenterZ=0 NormalX=0 NormalY=0 NormalZ=1 Radius=2
    g1: Circle CenterX=15.5 CenterY=15.5 CenterZ=0 NormalX=0 NormalY=0 NormalZ=1 Radius=2
    g2: Circle CenterX=-15.5 CenterY=-15.5 CenterZ=0 NormalX=0 NormalY=0 NormalZ=1 Radius=2
    g3: Circle CenterX=15.5 CenterY=-15.5 CenterZ=0 NormalX=0 NormalY=0 NormalZ=1 Radius=2
  constraints (9):
    c: Distance(g0,g1) = 31
    c: Distance(g0,g2) = 31
    c: Symmetric(g0,g2,g-1)
    c: Symmetric(g0,g1,g-2)
    c: Symmetric(g2,g3,g-2)
    c: Radius(g0) = 2
    c: Equal(g0,g1)
    c: Equal(g0,g2)
    c: Equal(g0,g3)
FEATURE [Part::Extrusion] Extrude390
  Base = -> Sketch330
  Dir = (0,4.5,0)
  Solid = true
FEATURE [Part::Cut] Cut146
  Base = -> Extrude387
  Tool = -> Extrude390
FEATURE [Sketcher::SketchObject] Sketch331
  Placement = pos=(0,0,0) rot=(1,0,0;1.5708rad)
  sketch-geometry (1):
    g0: Circle CenterX=0 CenterY=0 CenterZ=0 NormalX=0 NormalY=0 NormalZ=1 Radius=9
  constraints (2):
    c: Coincident(g0,g-1)
    c: Radius(g0) = 9
FEATURE [Part::Extrusion] Extrude391
  Base = -> Sketch331
  Dir = (0,25,0)
  Solid = true
FEATURE [Sketcher::SketchObject] Sketch332
  Placement = pos=(0,0,0) rot=(1,0,0;1.5708rad)
  sketch-geometry (1):
    g0: Circle CenterX=0 CenterY=0 CenterZ=0 NormalX=0 NormalY=0 NormalZ=1 Radius=2.5
  constraints (2):
    c: Coincident(g0,g-1)
    c: Radius(g0) = 2.5
FEATURE [Part::Extrusion] Extrude392
  Base = -> Sketch332
  Dir = (0,10,0)
  Solid = true
FEATURE [Part::Cut] Cut147
  Base = -> Extrude391
  Tool = -> Extrude392
FEATURE [Sketcher::SketchObject] Sketch333
  Placement = pos=(0,25,0) rot=(0,0.707107,0.707107;3.14159rad)
  Support = -> Cut147 [Face3]
  sketch-geometry (1):
    g0: Circle CenterX=0 CenterY=0 CenterZ=0 NormalX=0 NormalY=0 NormalZ=1 Radius=4
  constraints (2):
    c: Coincident(g0,g-1)
    c: Radius(g0) = 4
FEATURE [Part::Extrusion] Extrude393
  Base = -> Sketch333
  Dir = (0,-10,0)
  Solid = true
FEATURE [Part::Cut] Cut148  label="Accouplement_015"
  Base = -> Cut147
  Placement = pos=(-2002,-12,0) rot=(1,0,0;3.14159rad)
  Tool = -> Extrude393
FEATURE [Part::Fuse] Fusion084
  Base = -> Extrude388
  Tool = -> Cut146
FEATURE [Part::Fuse] Fusion085  label="Moteur_015"
  Base = -> Chamfer045
  Placement = pos=(-2002,0,0) rot=(0,0,1;0rad)
  Tool = -> Fusion084
FEATURE [Sketcher::SketchObject] Sketch334
  Placement = pos=(0,0,0) rot=(1,0,0;1.5708rad)
  sketch-geometry (4):
    g0: LineSegment StartX=-50 StartY=0 StartZ=0 EndX=-47 EndY=0 EndZ=0
    g1: LineSegment StartX=47 StartY=0 StartZ=0 EndX=50 EndY=0 EndZ=0
    g2: ArcOfCircle CenterX=0 CenterY=0 CenterZ=0 NormalX=0 NormalY=0 NormalZ=1 Radius=47 StartAngle=3.14159 EndAngle=6.28319
    g3: ArcOfCircle CenterX=0 CenterY=0 CenterZ=0 NormalX=0 NormalY=0 NormalZ=1 Radius=50 StartAngle=3.14159 EndAngle=6.28319
  constraints (13):
    c: Horizontal(g0)
    c: PointOnObject(g1,g-1)
    c: Horizontal(g1)
    c: Coincident(g2,g-1)
    c: PointOnObject(g2,g-1)
    c: Coincident(g3,g-1)
    c: Coincident(g3,g1)
    c: PointOnObject(g3,g-1)
    c: Coincident(g0,g3)
    c: Coincident(g0,g2)
    c: Distance(g0,g1) = 100
    c: Distance(g0,g0) = 3
    c: Coincident(g1,g2)
FEATURE [Part::Extrusion] Extrude394  label="Demi_tube_sous_miroir_015"
  Base = -> Sketch334
  Dir = (0,2000,0)
  Placement = pos=(-2002,-62,20) rot=(0,0,1;3.14159rad)
  Solid = true
FEATURE [Part::Feature] Part__Feature017  label="Coussinet_autolub_C2-151-8-128_015"
  Placement = pos=(-2002,-46,0) rot=(0,0,1;1.5708rad)
  shape: bbox 16 x 8 x 16 mm, 12 faces (baked)
FEATURE [Sketcher::SketchObject] Sketch335
  Placement = pos=(0,0,0) rot=(1,0,0;1.5708rad)
  sketch-geometry (21):
    g0: Circle CenterX=0 CenterY=0 CenterZ=0 NormalX=0 NormalY=0 NormalZ=1 Radius=6
    g1: LineSegment StartX=-20.5 StartY=15 StartZ=0 EndX=20.5 EndY=15 EndZ=0
    g2: ArcOfCircle CenterX=20.5 CenterY=13 CenterZ=0 NormalX=0 NormalY=0 NormalZ=1 Radius=2 StartAngle=6.28319 EndAngle=7.85398
    g3: LineSegment StartX=22.5 StartY=13 StartZ=0 EndX=22.5 EndY=-73 EndZ=0
    g4: LineSegment StartX=-22.5 StartY=13 StartZ=0 EndX=-22.5 EndY=-73 EndZ=0
    g5: ArcOfCircle CenterX=-20.5 CenterY=13 CenterZ=0 NormalX=0 NormalY=0 NormalZ=1 Radius=2 StartAngle=1.5708 EndAngle=3.14159
    g6: ArcOfCircle CenterX=-20.5 CenterY=-73 CenterZ=0 NormalX=0 NormalY=0 NormalZ=1 Radius=2 StartAngle=3.14159 EndAngle=4.71239
    g7: ArcOfCircle CenterX=20.5 CenterY=-73 CenterZ=0 NormalX=0 NormalY=0 NormalZ=1 Radius=2 StartAngle=4.71239 EndAngle=6.28319
    g8: LineSegment StartX=-20.5 StartY=-75 StartZ=0 EndX=20.5 EndY=-75 EndZ=0
    g9: ArcOfCircle CenterX=0 CenterY=-16.7 CenterZ=0 NormalX=0 NormalY=0 NormalZ=1 Radius=1.5 StartAngle=0 EndAngle=3.14159
    g10: ArcOfCircle CenterX=0 CenterY=-24.3 CenterZ=0 NormalX=0 NormalY=0 NormalZ=1 Radius=1.5 StartAngle=3.14159 EndAngle=6.28319
    g11: LineSegment StartX=-1.5 StartY=-16.7 StartZ=0 EndX=-1.5 EndY=-24.3 EndZ=0
    g12: LineSegment StartX=1.5 StartY=-16.7 StartZ=0 EndX=1.5 EndY=-24.3 EndZ=0
    g13: Circle CenterX=-12.5 CenterY=-45 CenterZ=0 NormalX=0 NormalY=0 NormalZ=1 Radius=3.5
    g14: Circle CenterX=12.5 CenterY=-45 CenterZ=0 NormalX=0 NormalY=0 NormalZ=1 Radius=3.5
    g15: Circle CenterX=-12.5 CenterY=-65 CenterZ=0 NormalX=0 NormalY=0 NormalZ=1 Radius=3.5
    g16: Circle CenterX=12.5 CenterY=-65 CenterZ=0 NormalX=0 NormalY=0 NormalZ=1 Radius=3.5
    g17: LineSegment [constr] StartX=-12.5 StartY=-45 StartZ=0 EndX=12.5 EndY=-45 EndZ=0
    g18: LineSegment [constr] StartX=-12.5 StartY=-45 StartZ=0 EndX=-12.5 EndY=-65 EndZ=0
    g19: LineSegment [constr] StartX=-12.5 StartY=-65 StartZ=0 EndX=12.5 EndY=-65 EndZ=0
    g20: LineSegment [constr] StartX=12.5 StartY=-45 StartZ=0 EndX=12.5 EndY=-65 EndZ=0
  constraints (59):
    c: Coincident(g0,g-1)
    c: Radius(g0) = 6
    c: Horizontal(g1)
    c: Coincident(g2,g1)
    c: Coincident(g3,g2)
    c: Vertical(g3)
    c: Vertical(g4)
    c: Coincident(g5,g1)
    c: Coincident(g5,g4)
    c: Coincident(g7,g3)
    c: Coincident(g8,g6)
    c: Coincident(g8,g7)
    c: Tangent(g8,g7)
    c: Tangent(g5,g4)
    c: Tangent(g5,g1)
    c: Tangent(g1,g2)
    c: Tangent(g2,g3)
    c: Coincident(g4,g6)
    c: Tangent(g6,g4)
    c: Tangent(g6,g8)
    c: Horizontal(g8)
    c: Tangent(g7,g3)
    c: Distance(g4,g2) = 45
    c: Symmetric(g4,g2,g-2)
    c: Distance(g1,g6) = 90
    c: DistanceY(g-1,g1) = 15
    c: Tangent(g9,g12) = 1.5708
    c: Tangent(g9,g11) = -1.5708
    c: Tangent(g11,g10) = -1.5708
    c: Tangent(g12,g10) = 1.5708
    c: Vertical(g11)
    c: Equal(g9,g10)
    c: PointOnObject(g9,g-2)
    c: Distance(g-1,g9) = 16.7
    c: Distance(g9,g10) = 7.6
    c: Radius(g9) = 1.5
    c: Radius(g13) = 3.5
    c: Equal(g13,g14)
    c: Equal(g13,g16)
    c: Equal(g13,g15)
    c: Radius(g5) = 2
    c: Equal(g5,g7)
    c: Equal(g5,g6)
    c: DistanceY(g-1,g13) = -45
    c: Coincident(g17,g13)
    c: Coincident(g17,g14)
    c: Horizontal(g17)
    c: Coincident(g18,g13)
    c: Coincident(g18,g15)
    c: Coincident(g19,g15)
    c: Coincident(g19,g16)
    c: Horizontal(g19)
    c: Coincident(g20,g14)
    c: Coincident(g20,g16)
    c: Vertical(g18)
    c: Vertical(g20)
    c: Distance(g13,g15) = 20
    c: Distance(g13,g14) = 25
    c: Symmetric(g13,g14,g-2)
FEATURE [Part::Extrusion] Extrude395  label="Plaque_support_015"
  Base = -> Sketch335
  Dir = (0,6,0)
  Placement = pos=(-2002,-46,0) rot=(0,0,1;0rad)
  Solid = true
FEATURE [Sketcher::SketchObject] Sketch336
  Placement = pos=(0,0,0) rot=(0.57735,0.57735,0.57735;2.0944rad)
  sketch-geometry (8):
    g0: LineSegment StartX=0 StartY=33 StartZ=0 EndX=-2 EndY=33 EndZ=0
    g1: LineSegment StartX=-2 StartY=33 StartZ=0 EndX=-2 EndY=-24 EndZ=0
    g2: ArcOfCircle CenterX=-4 CenterY=-24 CenterZ=0 NormalX=0 NormalY=0 NormalZ=1 Radius=2 StartAngle=4.71239 EndAngle=6.28319
    g3: LineSegment StartX=-4 StartY=-26 StartZ=0 EndX=-38 EndY=-26 EndZ=0
    g4: LineSegment StartX=-38 StartY=-26 StartZ=0 EndX=-38 EndY=-28 EndZ=0
    g5: LineSegment StartX=-38 StartY=-28 StartZ=0 EndX=-4 EndY=-28 EndZ=0
    g6: ArcOfCircle CenterX=-4 CenterY=-24 CenterZ=0 NormalX=0 NormalY=0 NormalZ=1 Radius=4 StartAngle=4.71239 EndAngle=6.28319
    g7: LineSegment StartX=0 StartY=-24 StartZ=0 EndX=0 EndY=33 EndZ=0
  constraints (22):
    c: PointOnObject(g0,g-2)
    c: Horizontal(g0)
    c: Coincident(g0,g1)
    c: Vertical(g1)
    c: Tangent(g1,g2) = 1.5708
    c: Tangent(g2,g3) = 1.5708
    c: Coincident(g3,g4)
    c: Vertical(g4)
    c: Coincident(g4,g5)
    c: Horizontal(g5)
    c: Tangent(g5,g6) = -1.5708
    c: PointOnObject(g6,g-2)
    c: Tangent(g6,g7) = -1.5708
    c: Coincident(g7,g0)
    c: Horizontal(g3)
    c: DistanceX(g0,g0) = 2
    c: Radius(g2) = 2
    c: Radius(g6) = 4
    c: DistanceY(g3,g4) = -2
    c: Distance(g-1,g0) = 33
    c: DistanceY(g-1,g5) = -28
    c: DistanceX(g6,g4) = -38
FEATURE [Part::Extrusion] Extrude396
  Base = -> Sketch336
  Dir = (-32.5,0,0)
  Solid = true
FEATURE [Part::Extrusion] Extrude397
  Base = -> Sketch336
  Dir = (32.5,0,0)
  Solid = true
FEATURE [Part::MultiFuse] Fusion086
  Shapes = -> [Extrude396,Extrude397]
FEATURE [Sketcher::SketchObject] Sketch337
  Placement = pos=(0,-2,0) rot=(1,0,0;1.5708rad)
  Support = -> Fusion086 [Face3]
  sketch-geometry (9):
    g0: ArcOfCircle CenterX=0 CenterY=0 CenterZ=0 NormalX=0 NormalY=0 NormalZ=1 Radius=32.5 StartAngle=0 EndAngle=3.14159
    g1: LineSegment StartX=-32.5 StartY=0 StartZ=0 EndX=-32.5 EndY=34 EndZ=0
    g2: LineSegment StartX=-32.5 StartY=34 StartZ=0 EndX=32.5 EndY=34 EndZ=0
    g3: LineSegment StartX=32.5 StartY=34 StartZ=0 EndX=32.5 EndY=0 EndZ=0
    g4: Circle CenterX=0 CenterY=0 CenterZ=0 NormalX=0 NormalY=0 NormalZ=1 Radius=11
    g5: Circle CenterX=-15.5 CenterY=15.5 CenterZ=0 NormalX=0 NormalY=0 NormalZ=1 Radius=2
    g6: Circle CenterX=15.5 CenterY=15.5 CenterZ=0 NormalX=0 NormalY=0 NormalZ=1 Radius=2
    g7: Circle CenterX=-15.5 CenterY=-15.5 CenterZ=0 NormalX=0 NormalY=0 NormalZ=1 Radius=2
    g8: Circle CenterX=15.5 CenterY=-15.5 CenterZ=0 NormalX=0 NormalY=0 NormalZ=1 Radius=2
  constraints (23):
    c: Coincident(g0,g-1)
    c: PointOnObject(g0,g-1)
    c: PointOnObject(g0,g-1)
    c: Coincident(g1,g0)
    c: Vertical(g1)
    c: Coincident(g1,g2)
    c: Horizontal(g2)
    c: Coincident(g2,g3)
    c: Coincident(g3,g0)
    c: Vertical(g3)
    c: DistanceY(g1,g0) = -34
    c: Coincident(g4,g-1)
    c: Radius(g4) = 11
    c: DistanceX(g1,g2) = 65
    c: Radius(g5) = 2
    c: Equal(g5,g6)
    c: Equal(g5,g8)
    c: Equal(g5,g7)
    c: Symmetric(g5,g6,g-2)
    c: Symmetric(g5,g7,g-1)
    c: Symmetric(g7,g8,g-2)
    c: DistanceX(g5,g6) = 31
    c: DistanceY(g5,g7) = -31
FEATURE [Part::Extrusion] Extrude398
  Base = -> Sketch337
  Dir = (0,2,0)
  Solid = true
FEATURE [Part::Cut] Cut149
  Base = -> Fusion086
  Tool = -> Extrude398
FEATURE [Sketcher::SketchObject] Sketch338
  ExternalGeometry = -> [Cut149]
  Placement = pos=(0,0,-26) rot=(0,0,1;0rad)
  Support = -> Cut149 [Face5]
  sketch-geometry (5):
    g0: Circle CenterX=-25 CenterY=-12 CenterZ=0 NormalX=0 NormalY=0 NormalZ=1 Radius=3.5
    g1: Circle CenterX=-25 CenterY=-30 CenterZ=0 NormalX=0 NormalY=0 NormalZ=1 Radius=3.5
    g2: Circle CenterX=25 CenterY=-12 CenterZ=0 NormalX=0 NormalY=0 NormalZ=1 Radius=3.5
    g3: Circle CenterX=25 CenterY=-30 CenterZ=0 NormalX=0 NormalY=0 NormalZ=1 Radius=3.5
    g4: LineSegment [constr] StartX=-25 StartY=-12 StartZ=0 EndX=-25 EndY=-30 EndZ=0
  constraints (12):
    c: Radius(g0) = 3.5
    c: Equal(g0,g2)
    c: Equal(g0,g3)
    c: Equal(g0,g1)
    c: Symmetric(g0,g2,g-2)
    c: Symmetric(g1,g3,g-2)
    c: Coincident(g4,g0)
    c: Coincident(g4,g1)
    c: Vertical(g4)
    c: DistanceY(g0,g1) = -18
    c: DistanceY(g-3,g1) = 8
    c: DistanceX(g0,g2) = 50
FEATURE [Part::Extrusion] Extrude399
  Base = -> Sketch338
  Dir = (0,0,-2)
  Solid = true
FEATURE [Part::Cut] Cut150
  Base = -> Cut149
  Tool = -> Extrude399
FEATURE [Part::Fillet] Fillet033  label="Plaque_moteur_015"
  Base = -> Cut150
  Edges = 2 edges r=4: [Edge5,Edge59]
  Placement = pos=(-2002,0,0) rot=(0,0,1;0rad)
FEATURE [Sketcher::SketchObject] Sketch339
  Placement = pos=(0,0,0) rot=(1,0,0;1.5708rad)
  sketch-geometry (4):
    g0: LineSegment StartX=-3.15 StartY=5.95 StartZ=0 EndX=3.15 EndY=5.95 EndZ=0
    g1: LineSegment StartX=3.15 StartY=5.95 StartZ=0 EndX=3.15 EndY=-5.95 EndZ=0
    g2: LineSegment StartX=3.15 StartY=-5.95 StartZ=0 EndX=-3.15 EndY=-5.95 EndZ=0
    g3: LineSegment StartX=-3.15 StartY=-5.95 StartZ=0 EndX=-3.15 EndY=5.95 EndZ=0
  constraints (12):
    c: Coincident(g0,g1)
    c: Coincident(g1,g2)
    c: Coincident(g2,g3)
    c: Coincident(g3,g0)
    c: Horizontal(g0)
    c: Horizontal(g2)
    c: Vertical(g1)
    c: Vertical(g3)
    c: DistanceX(g0,g0) = 6.3
    c: DistanceY(g0,g2) = -11.9
    c: Symmetric(g0,g0,g-2)
    c: Symmetric(g0,g1,g-1)
FEATURE [Part::Extrusion] Extrude400
  Base = -> Sketch339
  Dir = (0,-10.8,0)
  Solid = true
FEATURE [Sketcher::SketchObject] Sketch340
  ExternalGeometry = -> [Extrude400]
  Placement = pos=(0,-10.8,0) rot=(1,0,0;1.5708rad)
  Support = -> Extrude400 [Face6]
  sketch-geometry (4):
    g0: LineSegment StartX=-3.15 StartY=1.55 StartZ=0 EndX=3.15 EndY=1.55 EndZ=0
    g1: LineSegment StartX=3.15 StartY=1.55 StartZ=0 EndX=3.15 EndY=-1.55 EndZ=0
    g2: LineSegment StartX=3.15 StartY=-1.55 StartZ=0 EndX=-3.15 EndY=-1.55 EndZ=0
    g3: LineSegment StartX=-3.15 StartY=-1.55 StartZ=0 EndX=-3.15 EndY=1.55 EndZ=0
  constraints (12):
    c: Coincident(g0,g1)
    c: Coincident(g1,g2)
    c: Coincident(g2,g3)
    c: Coincident(g3,g0)
    c: Horizontal(g0)
    c: Horizontal(g2)
    c: Vertical(g1)
    c: Vertical(g3)
    c: PointOnObject(g0,g-4)
    c: PointOnObject(g0,g-3)
    c: DistanceY(g0,g2) = -3.1
    c: Symmetric(g0,g1,g-1)
FEATURE [Part::Extrusion] Extrude401
  Base = -> Sketch340
  Dir = (0,7.7,0)
  Solid = true
FEATURE [Part::Cut] Cut151
  Base = -> Extrude400
  Tool = -> Extrude401
FEATURE [Part::Chamfer] Chamfer046
  Base = -> Cut151
  Edges = 4 edges r=0.5: [Edge7,Edge9,Edge15,Edge17]
FEATURE [Part::Chamfer] Chamfer047
  Base = -> Chamfer046
  Edges = 1 edges r=1.2: [Edge13]
FEATURE [Sketcher::SketchObject] Sketch341
  ExternalGeometry = -> [Chamfer047]
  Placement = pos=(0,0,5.95) rot=(0,0,1;0rad)
  Support = -> Chamfer047 [Face5]
  sketch-geometry (4):
    g0: LineSegment StartX=-3 StartY=0 StartZ=0 EndX=3 EndY=0 EndZ=0
    g1: LineSegment StartX=3 StartY=0 StartZ=0 EndX=3 EndY=-3.1 EndZ=0
    g2: LineSegment StartX=3 StartY=-3.1 StartZ=0 EndX=-3 EndY=-3.1 EndZ=0
    g3: LineSegment StartX=-3 StartY=-3.1 StartZ=0 EndX=-3 EndY=0 EndZ=0
  constraints (12):
    c: Coincident(g0,g1)
    c: Coincident(g1,g2)
    c: Coincident(g2,g3)
    c: Coincident(g3,g0)
    c: Horizontal(g0)
    c: Horizontal(g2)
    c: Vertical(g1)
    c: Vertical(g3)
    c: PointOnObject(g0,g-1)
    c: DistanceX(g-3,g0) = 0.15
    c: Symmetric(g0,g0,g-2)
    c: DistanceY(g0,g1) = -3.1
FEATURE [Part::Extrusion] Extrude402
  Base = -> Sketch341
  Dir = (0,0,6.3)
  Solid = true
FEATURE [Sketcher::SketchObject] Sketch342
  ExternalGeometry = -> [Extrude402]
  Placement = pos=(0,-3.1,0) rot=(1,0,0;1.5708rad)
  Support = -> Extrude402 [Face3]
  sketch-geometry (1):
    g0: Circle CenterX=0 CenterY=9.5 CenterZ=0 NormalX=0 NormalY=0 NormalZ=1 Radius=1.65
  constraints (3):
    c: PointOnObject(g0,g-2)
    c: Radius(g0) = 1.65
    c: DistanceY(g0,g-3) = -3.55
FEATURE [Part::Extrusion] Extrude403
  Base = -> Sketch342
  Dir = (0,6,0)
  Solid = true
FEATURE [Part::Cut] Cut152
  Base = -> Extrude402
  Tool = -> Extrude403
FEATURE [Part::Fillet] Fillet034
  Base = -> Cut152
  Edges = 2 edges r=1.35: [Edge8,Edge11]
FEATURE [Part::MultiFuse] Fusion087
  Shapes = -> [Chamfer047]
FEATURE [Sketcher::SketchObject] Sketch343
  Placement = pos=(0,0,0) rot=(0,0.707107,0.707107;3.14159rad)
  Support = -> Fusion087 [Face7]
  sketch-geometry (4):
    g0: Circle CenterX=-1.27 CenterY=3.8 CenterZ=0 NormalX=0 NormalY=0 NormalZ=1 Radius=0.2
    g1: Circle CenterX=1.27 CenterY=3.8 CenterZ=0 NormalX=0 NormalY=0 NormalZ=1 Radius=0.2
    g2: Circle CenterX=-1.27 CenterY=-3.8 CenterZ=0 NormalX=0 NormalY=0 NormalZ=1 Radius=0.2
    g3: Circle CenterX=1.27 CenterY=-3.8 CenterZ=0 NormalX=0 NormalY=0 NormalZ=1 Radius=0.2
  constraints (9):
    c: Radius(g0) = 0.2
    c: Equal(g0,g1)
    c: Equal(g0,g3)
    c: Equal(g0,g2)
    c: Symmetric(g0,g1,g-2)
    c: Symmetric(g2,g3,g-2)
    c: Symmetric(g0,g2,g-1)
    c: DistanceX(g0,g1) = 2.54
    c: DistanceY(g1,g3) = -7.6
FEATURE [Part::Extrusion] Extrude404
  Base = -> Sketch343
  Dir = (0,7.8,0)
  Solid = true
FEATURE [Part::MultiFuse] Fusion088  label="Capteur_optique_015"
  Placement = pos=(-2002,-46,-20.7) rot=(0,0,1;0rad)
  Shapes = -> [Fusion087,Fillet034,Extrude404]
FEATURE [Sketcher::SketchObject] Sketch344
  Placement = pos=(0,0,0) rot=(1,0,0;1.5708rad)
  sketch-geometry (1):
    g0: Circle CenterX=0 CenterY=0 CenterZ=0 NormalX=0 NormalY=0 NormalZ=1 Radius=4
  constraints (2):
    c: Coincident(g0,g-1)
    c: Radius(g0) = 4
FEATURE [Part::Extrusion] Extrude405
  Base = -> Sketch344
  Dir = (0,50,0)
  Solid = true
FEATURE [Sketcher::SketchObject] Sketch345
  Placement = pos=(0,0,0) rot=(0.57735,0.57735,0.57735;2.0944rad)
  sketch-geometry (1):
    g0: Circle CenterX=6 CenterY=0 CenterZ=0 NormalX=0 NormalY=0 NormalZ=1 Radius=2
  constraints (3):
    c: DistanceX(g-1,g0) = 6
    c: Radius(g0) = 2
    c: PointOnObject(g0,g-1)
FEATURE [Part::Extrusion] Extrude406
  Base = -> Sketch345
  Dir = (4,0,0)
  Solid = true
FEATURE [Part::Extrusion] Extrude407
  Base = -> Sketch345
  Dir = (-4,0,0)
  Solid = true
FEATURE [Part::Cut] Cut153
  Base = -> Extrude405
  Tool = -> Extrude406
FEATURE [Part::Cut] Cut154  label="Axe_D8_015"
  Base = -> Cut153
  Placement = pos=(-2002,-86,0) rot=(0,0,1;0rad)
  Tool = -> Extrude407
FEATURE [Sketcher::SketchObject] Sketch346
  Placement = pos=(0,0,0) rot=(1,0,0;1.5708rad)
  sketch-geometry (1):
    g0: Circle CenterX=0 CenterY=0 CenterZ=0 NormalX=0 NormalY=0 NormalZ=1 Radius=2
  constraints (2):
    c: Coincident(g0,g-1)
    c: Radius(g0) = 2
FEATURE [Part::Extrusion] Extrude408  label="Axe_D4_015"
  Base = -> Sketch346
  Dir = (0,103.6,0)
  Placement = pos=(-1950.2,-80,0) rot=(0,0,1;1.5708rad)
  Solid = true
FEATURE [Sketcher::SketchObject] Sketch347
  Placement = pos=(0,0,0) rot=(1,0,0;1.5708rad)
  sketch-geometry (8):
    g0: LineSegment StartX=-50 StartY=0 StartZ=0 EndX=50 EndY=0 EndZ=0
    g1: LineSegment StartX=50 StartY=0 StartZ=0 EndX=50 EndY=-2 EndZ=0
    g2: LineSegment StartX=50 StartY=-2 StartZ=0 EndX=47 EndY=-2 EndZ=0
    g3: LineSegment StartX=47 StartY=-2 StartZ=0 EndX=44 EndY=-16 EndZ=0
    g4: LineSegment StartX=44 StartY=-16 StartZ=0 EndX=-44 EndY=-16 EndZ=0
    g5: LineSegment StartX=-44 StartY=-16 StartZ=0 EndX=-47 EndY=-2 EndZ=0
    g6: LineSegment StartX=-47 StartY=-2 StartZ=0 EndX=-50 EndY=-2 EndZ=0
    g7: LineSegment StartX=-50 StartY=-2 StartZ=0 EndX=-50 EndY=0 EndZ=0
  constraints (24):
    c: PointOnObject(g0,g-1)
    c: Horizontal(g0)
    c: Coincident(g0,g1)
    c: Vertical(g1)
    c: Coincident(g1,g2)
    c: Horizontal(g2)
    c: Coincident(g2,g3)
    c: Coincident(g3,g4)
    c: Horizontal(g4)
    c: Coincident(g4,g5)
    c: Coincident(g5,g6)
    c: Horizontal(g6)
    c: Coincident(g6,g7)
    c: Coincident(g7,g0)
    c: Vertical(g7)
    c: DistanceY(g0,g6) = -2
    c: DistanceX(g6,g5) = 3
    c: DistanceX(g0,g0) = 100
    c: Symmetric(g0,g0,g-2)
    c: Symmetric(g6,g1,g-2)
    c: Symmetric(g5,g2,g-2)
    c: Symmetric(g4,g3,g-2)
    c: DistanceX(g4,g3) = 88
    c: DistanceY(g0,g4) = -16
FEATURE [Part::Extrusion] Extrude409  label="Plaque_alveolaire_015"
  Base = -> Sketch347
  Dir = (0,2000,0)
  Placement = pos=(-2002,-62,22) rot=(0,0,1;3.14159rad)
  Solid = true
FEATURE [App::DocumentObjectGroup] Groupe020  label="Assemblage_miroir X=-572_002"
  Group = -> [Cut148,Fusion085,Extrude394,Part__Feature017,Extrude395,Fillet033,Fusion088,Cut154,Extrude408,Extrude409]
FEATURE [Sketcher::SketchObject] Sketch348
  Placement = pos=(0,0,0) rot=(1,0,0;1.5708rad)
  sketch-geometry (8):
    g0: LineSegment StartX=-21.15 StartY=16.15 StartZ=0 EndX=-16.15 EndY=21.15 EndZ=0
    g1: LineSegment StartX=-16.15 StartY=21.15 StartZ=0 EndX=16.15 EndY=21.15 EndZ=0
    g2: LineSegment StartX=16.15 StartY=21.15 StartZ=0 EndX=21.15 EndY=16.15 EndZ=0
    g3: LineSegment StartX=21.15 StartY=16.15 StartZ=0 EndX=21.15 EndY=-16.15 EndZ=0
    g4: LineSegment StartX=21.15 StartY=-16.15 StartZ=0 EndX=16.15 EndY=-21.15 EndZ=0
    g5: LineSegment StartX=16.15 StartY=-21.15 StartZ=0 EndX=-16.15 EndY=-21.15 EndZ=0
    g6: LineSegment StartX=-16.15 StartY=-21.15 StartZ=0 EndX=-21.15 EndY=-16.15 EndZ=0
    g7: LineSegment StartX=-21.15 StartY=-16.15 StartZ=0 EndX=-21.15 EndY=16.15 EndZ=0
  constraints (21):
    c: Coincident(g0,g1)
    c: Horizontal(g1)
    c: Coincident(g1,g2)
    c: Coincident(g2,g3)
    c: Vertical(g3)
    c: Coincident(g3,g4)
    c: Coincident(g4,g5)
    c: Horizontal(g5)
    c: Coincident(g5,g6)
    c: Coincident(g6,g7)
    c: Coincident(g7,g0)
    c: Angle(g7,g0) = 2.35619
    c: Distance(g0,g7) = 5
    c: Distance(g2,g7) = 42.3
    c: Distance(g5,g1) = 42.3
    c: Symmetric(g6,g3,g-2)
    c: Symmetric(g5,g4,g-2)
    c: Symmetric(g0,g2,g-2)
    c: Symmetric(g0,g1,g-2)
    c: Symmetric(g0,g6,g-1)
    c: Symmetric(g0,g5,g-1)
FEATURE [Part::Extrusion] Extrude410
  Base = -> Sketch348
  Dir = (0,48,0)
  Solid = true
FEATURE [Sketcher::SketchObject] Sketch349
  Placement = pos=(0,0,0) rot=(1,0,0;1.5708rad)
  Support = -> Extrude410 [Face9]
  sketch-geometry (1):
    g0: Circle CenterX=0 CenterY=0 CenterZ=0 NormalX=0 NormalY=0 NormalZ=1 Radius=11
  constraints (2):
    c: Coincident(g0,g-1)
    c: Radius(g0) = 11
FEATURE [Part::Extrusion] Extrude411
  Base = -> Sketch349
  Dir = (0,-2,0)
  Solid = true
FEATURE [Sketcher::SketchObject] Sketch350
  Placement = pos=(0,-2,0) rot=(1,0,0;1.5708rad)
  Support = -> Extrude411 [Face3]
  sketch-geometry (1):
    g0: Circle CenterX=0 CenterY=0 CenterZ=0 NormalX=0 NormalY=0 NormalZ=1 Radius=2.5
  constraints (2):
    c: Coincident(g0,g-1)
    c: Radius(g0) = 2.5
FEATURE [Part::Extrusion] Extrude412
  Base = -> Sketch350
  Dir = (0,-22,0)
  Solid = true
FEATURE [Part::Chamfer] Chamfer048
  Base = -> Extrude412
  Edges = 1 edges r=0.8: [Edge3]
FEATURE [Sketcher::SketchObject] Sketch351
  Placement = pos=(0,0,0) rot=(1,0,0;1.5708rad)
  Support = -> Extrude410 [Face9]
  sketch-geometry (4):
    g0: Circle CenterX=-15.5 CenterY=15.5 CenterZ=0 NormalX=0 NormalY=0 NormalZ=1 Radius=2
    g1: Circle CenterX=15.5 CenterY=15.5 CenterZ=0 NormalX=0 NormalY=0 NormalZ=1 Radius=2
    g2: Circle CenterX=-15.5 CenterY=-15.5 CenterZ=0 NormalX=0 NormalY=0 NormalZ=1 Radius=2
    g3: Circle CenterX=15.5 CenterY=-15.5 CenterZ=0 NormalX=0 NormalY=0 NormalZ=1 Radius=2
  constraints (9):
    c: Distance(g0,g1) = 31
    c: Distance(g0,g2) = 31
    c: Symmetric(g0,g2,g-1)
    c: Symmetric(g0,g1,g-2)
    c: Symmetric(g2,g3,g-2)
    c: Radius(g0) = 2
    c: Equal(g0,g1)
    c: Equal(g0,g2)
    c: Equal(g0,g3)
FEATURE [Part::Extrusion] Extrude413
  Base = -> Sketch351
  Dir = (0,4.5,0)
  Solid = true
FEATURE [Part::Cut] Cut155
  Base = -> Extrude410
  Tool = -> Extrude413
FEATURE [Sketcher::SketchObject] Sketch352
  Placement = pos=(0,0,0) rot=(1,0,0;1.5708rad)
  sketch-geometry (1):
    g0: Circle CenterX=0 CenterY=0 CenterZ=0 NormalX=0 NormalY=0 NormalZ=1 Radius=9
  constraints (2):
    c: Coincident(g0,g-1)
    c: Radius(g0) = 9
FEATURE [Part::Extrusion] Extrude414
  Base = -> Sketch352
  Dir = (0,25,0)
  Solid = true
FEATURE [Sketcher::SketchObject] Sketch353
  Placement = pos=(0,0,0) rot=(1,0,0;1.5708rad)
  sketch-geometry (1):
    g0: Circle CenterX=0 CenterY=0 CenterZ=0 NormalX=0 NormalY=0 NormalZ=1 Radius=2.5
  constraints (2):
    c: Coincident(g0,g-1)
    c: Radius(g0) = 2.5
FEATURE [Part::Extrusion] Extrude415
  Base = -> Sketch353
  Dir = (0,10,0)
  Solid = true
FEATURE [Part::Cut] Cut156
  Base = -> Extrude414
  Tool = -> Extrude415
FEATURE [Sketcher::SketchObject] Sketch354
  Placement = pos=(0,25,0) rot=(0,0.707107,0.707107;3.14159rad)
  Support = -> Cut156 [Face3]
  sketch-geometry (1):
    g0: Circle CenterX=0 CenterY=0 CenterZ=0 NormalX=0 NormalY=0 NormalZ=1 Radius=4
  constraints (2):
    c: Coincident(g0,g-1)
    c: Radius(g0) = 4
FEATURE [Part::Extrusion] Extrude416
  Base = -> Sketch354
  Dir = (0,-10,0)
  Solid = true
FEATURE [Part::Cut] Cut157  label="Accouplement_016"
  Base = -> Cut156
  Placement = pos=(-2145,-12,0) rot=(1,0,0;3.14159rad)
  Tool = -> Extrude416
FEATURE [Part::Fuse] Fusion089
  Base = -> Extrude411
  Tool = -> Cut155
FEATURE [Part::Fuse] Fusion090  label="Moteur_016"
  Base = -> Chamfer048
  Placement = pos=(-2145,0,0) rot=(0,0,1;0rad)
  Tool = -> Fusion089
FEATURE [Sketcher::SketchObject] Sketch355
  Placement = pos=(0,0,0) rot=(1,0,0;1.5708rad)
  sketch-geometry (4):
    g0: LineSegment StartX=-50 StartY=0 StartZ=0 EndX=-47 EndY=0 EndZ=0
    g1: LineSegment StartX=47 StartY=0 StartZ=0 EndX=50 EndY=0 EndZ=0
    g2: ArcOfCircle CenterX=0 CenterY=0 CenterZ=0 NormalX=0 NormalY=0 NormalZ=1 Radius=47 StartAngle=3.14159 EndAngle=6.28319
    g3: ArcOfCircle CenterX=0 CenterY=0 CenterZ=0 NormalX=0 NormalY=0 NormalZ=1 Radius=50 StartAngle=3.14159 EndAngle=6.28319
  constraints (13):
    c: Horizontal(g0)
    c: PointOnObject(g1,g-1)
    c: Horizontal(g1)
    c: Coincident(g2,g-1)
    c: PointOnObject(g2,g-1)
    c: Coincident(g3,g-1)
    c: Coincident(g3,g1)
    c: PointOnObject(g3,g-1)
    c: Coincident(g0,g3)
    c: Coincident(g0,g2)
    c: Distance(g0,g1) = 100
    c: Distance(g0,g0) = 3
    c: Coincident(g1,g2)
FEATURE [Part::Extrusion] Extrude417  label="Demi_tube_sous_miroir_016"
  Base = -> Sketch355
  Dir = (0,2000,0)
  Placement = pos=(-2145,-62,20) rot=(0,0,1;3.14159rad)
  Solid = true
FEATURE [Part::Feature] Part__Feature018  label="Coussinet_autolub_C2-151-8-128_016"
  Placement = pos=(-2145,-46,0) rot=(0,0,1;1.5708rad)
  shape: bbox 16 x 8 x 16 mm, 12 faces (baked)
FEATURE [Sketcher::SketchObject] Sketch356
  Placement = pos=(0,0,0) rot=(1,0,0;1.5708rad)
  sketch-geometry (21):
    g0: Circle CenterX=0 CenterY=0 CenterZ=0 NormalX=0 NormalY=0 NormalZ=1 Radius=6
    g1: LineSegment StartX=-20.5 StartY=15 StartZ=0 EndX=20.5 EndY=15 EndZ=0
    g2: ArcOfCircle CenterX=20.5 CenterY=13 CenterZ=0 NormalX=0 NormalY=0 NormalZ=1 Radius=2 StartAngle=6.28319 EndAngle=7.85398
    g3: LineSegment StartX=22.5 StartY=13 StartZ=0 EndX=22.5 EndY=-73 EndZ=0
    g4: LineSegment StartX=-22.5 StartY=13 StartZ=0 EndX=-22.5 EndY=-73 EndZ=0
    g5: ArcOfCircle CenterX=-20.5 CenterY=13 CenterZ=0 NormalX=0 NormalY=0 NormalZ=1 Radius=2 StartAngle=1.5708 EndAngle=3.14159
    g6: ArcOfCircle CenterX=-20.5 CenterY=-73 CenterZ=0 NormalX=0 NormalY=0 NormalZ=1 Radius=2 StartAngle=3.14159 EndAngle=4.71239
    g7: ArcOfCircle CenterX=20.5 CenterY=-73 CenterZ=0 NormalX=0 NormalY=0 NormalZ=1 Radius=2 StartAngle=4.71239 EndAngle=6.28319
    g8: LineSegment StartX=-20.5 StartY=-75 StartZ=0 EndX=20.5 EndY=-75 EndZ=0
    g9: ArcOfCircle CenterX=0 CenterY=-16.7 CenterZ=0 NormalX=0 NormalY=0 NormalZ=1 Radius=1.5 StartAngle=0 EndAngle=3.14159
    g10: ArcOfCircle CenterX=0 CenterY=-24.3 CenterZ=0 NormalX=0 NormalY=0 NormalZ=1 Radius=1.5 StartAngle=3.14159 EndAngle=6.28319
    g11: LineSegment StartX=-1.5 StartY=-16.7 StartZ=0 EndX=-1.5 EndY=-24.3 EndZ=0
    g12: LineSegment StartX=1.5 StartY=-16.7 StartZ=0 EndX=1.5 EndY=-24.3 EndZ=0
    g13: Circle CenterX=-12.5 CenterY=-45 CenterZ=0 NormalX=0 NormalY=0 NormalZ=1 Radius=3.5
    g14: Circle CenterX=12.5 CenterY=-45 CenterZ=0 NormalX=0 NormalY=0 NormalZ=1 Radius=3.5
    g15: Circle CenterX=-12.5 CenterY=-65 CenterZ=0 NormalX=0 NormalY=0 NormalZ=1 Radius=3.5
    g16: Circle CenterX=12.5 CenterY=-65 CenterZ=0 NormalX=0 NormalY=0 NormalZ=1 Radius=3.5
    g17: LineSegment [constr] StartX=-12.5 StartY=-45 StartZ=0 EndX=12.5 EndY=-45 EndZ=0
    g18: LineSegment [constr] StartX=-12.5 StartY=-45 StartZ=0 EndX=-12.5 EndY=-65 EndZ=0
    g19: LineSegment [constr] StartX=-12.5 StartY=-65 StartZ=0 EndX=12.5 EndY=-65 EndZ=0
    g20: LineSegment [constr] StartX=12.5 StartY=-45 StartZ=0 EndX=12.5 EndY=-65 EndZ=0
  constraints (59):
    c: Coincident(g0,g-1)
    c: Radius(g0) = 6
    c: Horizontal(g1)
    c: Coincident(g2,g1)
    c: Coincident(g3,g2)
    c: Vertical(g3)
    c: Vertical(g4)
    c: Coincident(g5,g1)
    c: Coincident(g5,g4)
    c: Coincident(g7,g3)
    c: Coincident(g8,g6)
    c: Coincident(g8,g7)
    c: Tangent(g8,g7)
    c: Tangent(g5,g4)
    c: Tangent(g5,g1)
    c: Tangent(g1,g2)
    c: Tangent(g2,g3)
    c: Coincident(g4,g6)
    c: Tangent(g6,g4)
    c: Tangent(g6,g8)
    c: Horizontal(g8)
    c: Tangent(g7,g3)
    c: Distance(g4,g2) = 45
    c: Symmetric(g4,g2,g-2)
    c: Distance(g1,g6) = 90
    c: DistanceY(g-1,g1) = 15
    c: Tangent(g9,g12) = 1.5708
    c: Tangent(g9,g11) = -1.5708
    c: Tangent(g11,g10) = -1.5708
    c: Tangent(g12,g10) = 1.5708
    c: Vertical(g11)
    c: Equal(g9,g10)
    c: PointOnObject(g9,g-2)
    c: Distance(g-1,g9) = 16.7
    c: Distance(g9,g10) = 7.6
    c: Radius(g9) = 1.5
    c: Radius(g13) = 3.5
    c: Equal(g13,g14)
    c: Equal(g13,g16)
    c: Equal(g13,g15)
    c: Radius(g5) = 2
    c: Equal(g5,g7)
    c: Equal(g5,g6)
    c: DistanceY(g-1,g13) = -45
    c: Coincident(g17,g13)
    c: Coincident(g17,g14)
    c: Horizontal(g17)
    c: Coincident(g18,g13)
    c: Coincident(g18,g15)
    c: Coincident(g19,g15)
    c: Coincident(g19,g16)
    c: Horizontal(g19)
    c: Coincident(g20,g14)
    c: Coincident(g20,g16)
    c: Vertical(g18)
    c: Vertical(g20)
    c: Distance(g13,g15) = 20
    c: Distance(g13,g14) = 25
    c: Symmetric(g13,g14,g-2)
FEATURE [Part::Extrusion] Extrude418  label="Plaque_support_016"
  Base = -> Sketch356
  Dir = (0,6,0)
  Placement = pos=(-2145,-46,0) rot=(0,0,1;0rad)
  Solid = true
FEATURE [Sketcher::SketchObject] Sketch357
  Placement = pos=(0,0,0) rot=(0.57735,0.57735,0.57735;2.0944rad)
  sketch-geometry (8):
    g0: LineSegment StartX=0 StartY=33 StartZ=0 EndX=-2 EndY=33 EndZ=0
    g1: LineSegment StartX=-2 StartY=33 StartZ=0 EndX=-2 EndY=-24 EndZ=0
    g2: ArcOfCircle CenterX=-4 CenterY=-24 CenterZ=0 NormalX=0 NormalY=0 NormalZ=1 Radius=2 StartAngle=4.71239 EndAngle=6.28319
    g3: LineSegment StartX=-4 StartY=-26 StartZ=0 EndX=-38 EndY=-26 EndZ=0
    g4: LineSegment StartX=-38 StartY=-26 StartZ=0 EndX=-38 EndY=-28 EndZ=0
    g5: LineSegment StartX=-38 StartY=-28 StartZ=0 EndX=-4 EndY=-28 EndZ=0
    g6: ArcOfCircle CenterX=-4 CenterY=-24 CenterZ=0 NormalX=0 NormalY=0 NormalZ=1 Radius=4 StartAngle=4.71239 EndAngle=6.28319
    g7: LineSegment StartX=0 StartY=-24 StartZ=0 EndX=0 EndY=33 EndZ=0
  constraints (22):
    c: PointOnObject(g0,g-2)
    c: Horizontal(g0)
    c: Coincident(g0,g1)
    c: Vertical(g1)
    c: Tangent(g1,g2) = 1.5708
    c: Tangent(g2,g3) = 1.5708
    c: Coincident(g3,g4)
    c: Vertical(g4)
    c: Coincident(g4,g5)
    c: Horizontal(g5)
    c: Tangent(g5,g6) = -1.5708
    c: PointOnObject(g6,g-2)
    c: Tangent(g6,g7) = -1.5708
    c: Coincident(g7,g0)
    c: Horizontal(g3)
    c: DistanceX(g0,g0) = 2
    c: Radius(g2) = 2
    c: Radius(g6) = 4
    c: DistanceY(g3,g4) = -2
    c: Distance(g-1,g0) = 33
    c: DistanceY(g-1,g5) = -28
    c: DistanceX(g6,g4) = -38
FEATURE [Part::Extrusion] Extrude419
  Base = -> Sketch357
  Dir = (-32.5,0,0)
  Solid = true
FEATURE [Part::Extrusion] Extrude420
  Base = -> Sketch357
  Dir = (32.5,0,0)
  Solid = true
FEATURE [Part::MultiFuse] Fusion091
  Shapes = -> [Extrude419,Extrude420]
FEATURE [Sketcher::SketchObject] Sketch358
  Placement = pos=(0,-2,0) rot=(1,0,0;1.5708rad)
  Support = -> Fusion091 [Face3]
  sketch-geometry (9):
    g0: ArcOfCircle CenterX=0 CenterY=0 CenterZ=0 NormalX=0 NormalY=0 NormalZ=1 Radius=32.5 StartAngle=0 EndAngle=3.14159
    g1: LineSegment StartX=-32.5 StartY=0 StartZ=0 EndX=-32.5 EndY=34 EndZ=0
    g2: LineSegment StartX=-32.5 StartY=34 StartZ=0 EndX=32.5 EndY=34 EndZ=0
    g3: LineSegment StartX=32.5 StartY=34 StartZ=0 EndX=32.5 EndY=0 EndZ=0
    g4: Circle CenterX=0 CenterY=0 CenterZ=0 NormalX=0 NormalY=0 NormalZ=1 Radius=11
    g5: Circle CenterX=-15.5 CenterY=15.5 CenterZ=0 NormalX=0 NormalY=0 NormalZ=1 Radius=2
    g6: Circle CenterX=15.5 CenterY=15.5 CenterZ=0 NormalX=0 NormalY=0 NormalZ=1 Radius=2
    g7: Circle CenterX=-15.5 CenterY=-15.5 CenterZ=0 NormalX=0 NormalY=0 NormalZ=1 Radius=2
    g8: Circle CenterX=15.5 CenterY=-15.5 CenterZ=0 NormalX=0 NormalY=0 NormalZ=1 Radius=2
  constraints (23):
    c: Coincident(g0,g-1)
    c: PointOnObject(g0,g-1)
    c: PointOnObject(g0,g-1)
    c: Coincident(g1,g0)
    c: Vertical(g1)
    c: Coincident(g1,g2)
    c: Horizontal(g2)
    c: Coincident(g2,g3)
    c: Coincident(g3,g0)
    c: Vertical(g3)
    c: DistanceY(g1,g0) = -34
    c: Coincident(g4,g-1)
    c: Radius(g4) = 11
    c: DistanceX(g1,g2) = 65
    c: Radius(g5) = 2
    c: Equal(g5,g6)
    c: Equal(g5,g8)
    c: Equal(g5,g7)
    c: Symmetric(g5,g6,g-2)
    c: Symmetric(g5,g7,g-1)
    c: Symmetric(g7,g8,g-2)
    c: DistanceX(g5,g6) = 31
    c: DistanceY(g5,g7) = -31
FEATURE [Part::Extrusion] Extrude421
  Base = -> Sketch358
  Dir = (0,2,0)
  Solid = true
FEATURE [Part::Cut] Cut158
  Base = -> Fusion091
  Tool = -> Extrude421
FEATURE [Sketcher::SketchObject] Sketch359
  ExternalGeometry = -> [Cut158]
  Placement = pos=(0,0,-26) rot=(0,0,1;0rad)
  Support = -> Cut158 [Face5]
  sketch-geometry (5):
    g0: Circle CenterX=-25 CenterY=-12 CenterZ=0 NormalX=0 NormalY=0 NormalZ=1 Radius=3.5
    g1: Circle CenterX=-25 CenterY=-30 CenterZ=0 NormalX=0 NormalY=0 NormalZ=1 Radius=3.5
    g2: Circle CenterX=25 CenterY=-12 CenterZ=0 NormalX=0 NormalY=0 NormalZ=1 Radius=3.5
    g3: Circle CenterX=25 CenterY=-30 CenterZ=0 NormalX=0 NormalY=0 NormalZ=1 Radius=3.5
    g4: LineSegment [constr] StartX=-25 StartY=-12 StartZ=0 EndX=-25 EndY=-30 EndZ=0
  constraints (12):
    c: Radius(g0) = 3.5
    c: Equal(g0,g2)
    c: Equal(g0,g3)
    c: Equal(g0,g1)
    c: Symmetric(g0,g2,g-2)
    c: Symmetric(g1,g3,g-2)
    c: Coincident(g4,g0)
    c: Coincident(g4,g1)
    c: Vertical(g4)
    c: DistanceY(g0,g1) = -18
    c: DistanceY(g-3,g1) = 8
    c: DistanceX(g0,g2) = 50
FEATURE [Part::Extrusion] Extrude422
  Base = -> Sketch359
  Dir = (0,0,-2)
  Solid = true
FEATURE [Part::Cut] Cut159
  Base = -> Cut158
  Tool = -> Extrude422
FEATURE [Part::Fillet] Fillet035  label="Plaque_moteur_016"
  Base = -> Cut159
  Edges = 2 edges r=4: [Edge5,Edge59]
  Placement = pos=(-2145,0,0) rot=(0,0,1;0rad)
FEATURE [Sketcher::SketchObject] Sketch360
  Placement = pos=(0,0,0) rot=(1,0,0;1.5708rad)
  sketch-geometry (4):
    g0: LineSegment StartX=-3.15 StartY=5.95 StartZ=0 EndX=3.15 EndY=5.95 EndZ=0
    g1: LineSegment StartX=3.15 StartY=5.95 StartZ=0 EndX=3.15 EndY=-5.95 EndZ=0
    g2: LineSegment StartX=3.15 StartY=-5.95 StartZ=0 EndX=-3.15 EndY=-5.95 EndZ=0
    g3: LineSegment StartX=-3.15 StartY=-5.95 StartZ=0 EndX=-3.15 EndY=5.95 EndZ=0
  constraints (12):
    c: Coincident(g0,g1)
    c: Coincident(g1,g2)
    c: Coincident(g2,g3)
    c: Coincident(g3,g0)
    c: Horizontal(g0)
    c: Horizontal(g2)
    c: Vertical(g1)
    c: Vertical(g3)
    c: DistanceX(g0,g0) = 6.3
    c: DistanceY(g0,g2) = -11.9
    c: Symmetric(g0,g0,g-2)
    c: Symmetric(g0,g1,g-1)
FEATURE [Part::Extrusion] Extrude423
  Base = -> Sketch360
  Dir = (0,-10.8,0)
  Solid = true
FEATURE [Sketcher::SketchObject] Sketch361
  ExternalGeometry = -> [Extrude423]
  Placement = pos=(0,-10.8,0) rot=(1,0,0;1.5708rad)
  Support = -> Extrude423 [Face6]
  sketch-geometry (4):
    g0: LineSegment StartX=-3.15 StartY=1.55 StartZ=0 EndX=3.15 EndY=1.55 EndZ=0
    g1: LineSegment StartX=3.15 StartY=1.55 StartZ=0 EndX=3.15 EndY=-1.55 EndZ=0
    g2: LineSegment StartX=3.15 StartY=-1.55 StartZ=0 EndX=-3.15 EndY=-1.55 EndZ=0
    g3: LineSegment StartX=-3.15 StartY=-1.55 StartZ=0 EndX=-3.15 EndY=1.55 EndZ=0
  constraints (12):
    c: Coincident(g0,g1)
    c: Coincident(g1,g2)
    c: Coincident(g2,g3)
    c: Coincident(g3,g0)
    c: Horizontal(g0)
    c: Horizontal(g2)
    c: Vertical(g1)
    c: Vertical(g3)
    c: PointOnObject(g0,g-4)
    c: PointOnObject(g0,g-3)
    c: DistanceY(g0,g2) = -3.1
    c: Symmetric(g0,g1,g-1)
FEATURE [Part::Extrusion] Extrude424
  Base = -> Sketch361
  Dir = (0,7.7,0)
  Solid = true
FEATURE [Part::Cut] Cut160
  Base = -> Extrude423
  Tool = -> Extrude424
FEATURE [Part::Chamfer] Chamfer049
  Base = -> Cut160
  Edges = 4 edges r=0.5: [Edge7,Edge9,Edge15,Edge17]
FEATURE [Part::Chamfer] Chamfer050
  Base = -> Chamfer049
  Edges = 1 edges r=1.2: [Edge13]
FEATURE [Sketcher::SketchObject] Sketch362
  ExternalGeometry = -> [Chamfer050]
  Placement = pos=(0,0,5.95) rot=(0,0,1;0rad)
  Support = -> Chamfer050 [Face5]
  sketch-geometry (4):
    g0: LineSegment StartX=-3 StartY=0 StartZ=0 EndX=3 EndY=0 EndZ=0
    g1: LineSegment StartX=3 StartY=0 StartZ=0 EndX=3 EndY=-3.1 EndZ=0
    g2: LineSegment StartX=3 StartY=-3.1 StartZ=0 EndX=-3 EndY=-3.1 EndZ=0
    g3: LineSegment StartX=-3 StartY=-3.1 StartZ=0 EndX=-3 EndY=0 EndZ=0
  constraints (12):
    c: Coincident(g0,g1)
    c: Coincident(g1,g2)
    c: Coincident(g2,g3)
    c: Coincident(g3,g0)
    c: Horizontal(g0)
    c: Horizontal(g2)
    c: Vertical(g1)
    c: Vertical(g3)
    c: PointOnObject(g0,g-1)
    c: DistanceX(g-3,g0) = 0.15
    c: Symmetric(g0,g0,g-2)
    c: DistanceY(g0,g1) = -3.1
FEATURE [Part::Extrusion] Extrude425
  Base = -> Sketch362
  Dir = (0,0,6.3)
  Solid = true
FEATURE [Sketcher::SketchObject] Sketch363
  ExternalGeometry = -> [Extrude425]
  Placement = pos=(0,-3.1,0) rot=(1,0,0;1.5708rad)
  Support = -> Extrude425 [Face3]
  sketch-geometry (1):
    g0: Circle CenterX=0 CenterY=9.5 CenterZ=0 NormalX=0 NormalY=0 NormalZ=1 Radius=1.65
  constraints (3):
    c: PointOnObject(g0,g-2)
    c: Radius(g0) = 1.65
    c: DistanceY(g0,g-3) = -3.55
FEATURE [Part::Extrusion] Extrude426
  Base = -> Sketch363
  Dir = (0,6,0)
  Solid = true
FEATURE [Part::Cut] Cut161
  Base = -> Extrude425
  Tool = -> Extrude426
FEATURE [Part::Fillet] Fillet036
  Base = -> Cut161
  Edges = 2 edges r=1.35: [Edge8,Edge11]
FEATURE [Part::MultiFuse] Fusion092
  Shapes = -> [Chamfer050]
FEATURE [Sketcher::SketchObject] Sketch364
  Placement = pos=(0,0,0) rot=(0,0.707107,0.707107;3.14159rad)
  Support = -> Fusion092 [Face7]
  sketch-geometry (4):
    g0: Circle CenterX=-1.27 CenterY=3.8 CenterZ=0 NormalX=0 NormalY=0 NormalZ=1 Radius=0.2
    g1: Circle CenterX=1.27 CenterY=3.8 CenterZ=0 NormalX=0 NormalY=0 NormalZ=1 Radius=0.2
    g2: Circle CenterX=-1.27 CenterY=-3.8 CenterZ=0 NormalX=0 NormalY=0 NormalZ=1 Radius=0.2
    g3: Circle CenterX=1.27 CenterY=-3.8 CenterZ=0 NormalX=0 NormalY=0 NormalZ=1 Radius=0.2
  constraints (9):
    c: Radius(g0) = 0.2
    c: Equal(g0,g1)
    c: Equal(g0,g3)
    c: Equal(g0,g2)
    c: Symmetric(g0,g1,g-2)
    c: Symmetric(g2,g3,g-2)
    c: Symmetric(g0,g2,g-1)
    c: DistanceX(g0,g1) = 2.54
    c: DistanceY(g1,g3) = -7.6
FEATURE [Part::Extrusion] Extrude427
  Base = -> Sketch364
  Dir = (0,7.8,0)
  Solid = true
FEATURE [Part::MultiFuse] Fusion093  label="Capteur_optique_016"
  Placement = pos=(-2145,-46,-20.7) rot=(0,0,1;0rad)
  Shapes = -> [Fusion092,Fillet036,Extrude427]
FEATURE [Sketcher::SketchObject] Sketch365
  Placement = pos=(0,0,0) rot=(1,0,0;1.5708rad)
  sketch-geometry (1):
    g0: Circle CenterX=0 CenterY=0 CenterZ=0 NormalX=0 NormalY=0 NormalZ=1 Radius=4
  constraints (2):
    c: Coincident(g0,g-1)
    c: Radius(g0) = 4
FEATURE [Part::Extrusion] Extrude428
  Base = -> Sketch365
  Dir = (0,50,0)
  Solid = true
FEATURE [Sketcher::SketchObject] Sketch366
  Placement = pos=(0,0,0) rot=(0.57735,0.57735,0.57735;2.0944rad)
  sketch-geometry (1):
    g0: Circle CenterX=6 CenterY=0 CenterZ=0 NormalX=0 NormalY=0 NormalZ=1 Radius=2
  constraints (3):
    c: DistanceX(g-1,g0) = 6
    c: Radius(g0) = 2
    c: PointOnObject(g0,g-1)
FEATURE [Part::Extrusion] Extrude429
  Base = -> Sketch366
  Dir = (4,0,0)
  Solid = true
FEATURE [Part::Extrusion] Extrude430
  Base = -> Sketch366
  Dir = (-4,0,0)
  Solid = true
FEATURE [Part::Cut] Cut162
  Base = -> Extrude428
  Tool = -> Extrude429
FEATURE [Part::Cut] Cut163  label="Axe_D8_016"
  Base = -> Cut162
  Placement = pos=(-2145,-86,0) rot=(0,0,1;0rad)
  Tool = -> Extrude430
FEATURE [Sketcher::SketchObject] Sketch367
  Placement = pos=(0,0,0) rot=(1,0,0;1.5708rad)
  sketch-geometry (1):
    g0: Circle CenterX=0 CenterY=0 CenterZ=0 NormalX=0 NormalY=0 NormalZ=1 Radius=2
  constraints (2):
    c: Coincident(g0,g-1)
    c: Radius(g0) = 2
FEATURE [Part::Extrusion] Extrude431  label="Axe_D4_016"
  Base = -> Sketch367
  Dir = (0,103.6,0)
  Placement = pos=(-2093.2,-80,0) rot=(0,0,1;1.5708rad)
  Solid = true
FEATURE [Sketcher::SketchObject] Sketch368
  Placement = pos=(0,0,0) rot=(1,0,0;1.5708rad)
  sketch-geometry (8):
    g0: LineSegment StartX=-50 StartY=0 StartZ=0 EndX=50 EndY=0 EndZ=0
    g1: LineSegment StartX=50 StartY=0 StartZ=0 EndX=50 EndY=-2 EndZ=0
    g2: LineSegment StartX=50 StartY=-2 StartZ=0 EndX=47 EndY=-2 EndZ=0
    g3: LineSegment StartX=47 StartY=-2 StartZ=0 EndX=44 EndY=-16 EndZ=0
    g4: LineSegment StartX=44 StartY=-16 StartZ=0 EndX=-44 EndY=-16 EndZ=0
    g5: LineSegment StartX=-44 StartY=-16 StartZ=0 EndX=-47 EndY=-2 EndZ=0
    g6: LineSegment StartX=-47 StartY=-2 StartZ=0 EndX=-50 EndY=-2 EndZ=0
    g7: LineSegment StartX=-50 StartY=-2 StartZ=0 EndX=-50 EndY=0 EndZ=0
  constraints (24):
    c: PointOnObject(g0,g-1)
    c: Horizontal(g0)
    c: Coincident(g0,g1)
    c: Vertical(g1)
    c: Coincident(g1,g2)
    c: Horizontal(g2)
    c: Coincident(g2,g3)
    c: Coincident(g3,g4)
    c: Horizontal(g4)
    c: Coincident(g4,g5)
    c: Coincident(g5,g6)
    c: Horizontal(g6)
    c: Coincident(g6,g7)
    c: Coincident(g7,g0)
    c: Vertical(g7)
    c: DistanceY(g0,g6) = -2
    c: DistanceX(g6,g5) = 3
    c: DistanceX(g0,g0) = 100
    c: Symmetric(g0,g0,g-2)
    c: Symmetric(g6,g1,g-2)
    c: Symmetric(g5,g2,g-2)
    c: Symmetric(g4,g3,g-2)
    c: DistanceX(g4,g3) = 88
    c: DistanceY(g0,g4) = -16
FEATURE [Part::Extrusion] Extrude432  label="Plaque_alveolaire_016"
  Base = -> Sketch368
  Dir = (0,2000,0)
  Placement = pos=(-2145,-62,22) rot=(0,0,1;3.14159rad)
  Solid = true
FEATURE [App::DocumentObjectGroup] Groupe021  label="Assemblage_miroir X=-715_002"
  Group = -> [Cut157,Fusion090,Extrude417,Part__Feature018,Extrude418,Fillet035,Fusion093,Cut163,Extrude431,Extrude432]
FEATURE [Sketcher::SketchObject] Sketch369
  Placement = pos=(0,0,0) rot=(1,0,0;1.5708rad)
  sketch-geometry (8):
    g0: LineSegment StartX=-21.15 StartY=16.15 StartZ=0 EndX=-16.15 EndY=21.15 EndZ=0
    g1: LineSegment StartX=-16.15 StartY=21.15 StartZ=0 EndX=16.15 EndY=21.15 EndZ=0
    g2: LineSegment StartX=16.15 StartY=21.15 StartZ=0 EndX=21.15 EndY=16.15 EndZ=0
    g3: LineSegment StartX=21.15 StartY=16.15 StartZ=0 EndX=21.15 EndY=-16.15 EndZ=0
    g4: LineSegment StartX=21.15 StartY=-16.15 StartZ=0 EndX=16.15 EndY=-21.15 EndZ=0
    g5: LineSegment StartX=16.15 StartY=-21.15 StartZ=0 EndX=-16.15 EndY=-21.15 EndZ=0
    g6: LineSegment StartX=-16.15 StartY=-21.15 StartZ=0 EndX=-21.15 EndY=-16.15 EndZ=0
    g7: LineSegment StartX=-21.15 StartY=-16.15 StartZ=0 EndX=-21.15 EndY=16.15 EndZ=0
  constraints (21):
    c: Coincident(g0,g1)
    c: Horizontal(g1)
    c: Coincident(g1,g2)
    c: Coincident(g2,g3)
    c: Vertical(g3)
    c: Coincident(g3,g4)
    c: Coincident(g4,g5)
    c: Horizontal(g5)
    c: Coincident(g5,g6)
    c: Coincident(g6,g7)
    c: Coincident(g7,g0)
    c: Angle(g7,g0) = 2.35619
    c: Distance(g0,g7) = 5
    c: Distance(g2,g7) = 42.3
    c: Distance(g5,g1) = 42.3
    c: Symmetric(g6,g3,g-2)
    c: Symmetric(g5,g4,g-2)
    c: Symmetric(g0,g2,g-2)
    c: Symmetric(g0,g1,g-2)
    c: Symmetric(g0,g6,g-1)
    c: Symmetric(g0,g5,g-1)
FEATURE [Part::Extrusion] Extrude433
  Base = -> Sketch369
  Dir = (0,48,0)
  Solid = true
FEATURE [Sketcher::SketchObject] Sketch370
  Placement = pos=(0,0,0) rot=(1,0,0;1.5708rad)
  Support = -> Extrude433 [Face9]
  sketch-geometry (1):
    g0: Circle CenterX=0 CenterY=0 CenterZ=0 NormalX=0 NormalY=0 NormalZ=1 Radius=11
  constraints (2):
    c: Coincident(g0,g-1)
    c: Radius(g0) = 11
FEATURE [Part::Extrusion] Extrude434
  Base = -> Sketch370
  Dir = (0,-2,0)
  Solid = true
FEATURE [Sketcher::SketchObject] Sketch371
  Placement = pos=(0,-2,0) rot=(1,0,0;1.5708rad)
  Support = -> Extrude434 [Face3]
  sketch-geometry (1):
    g0: Circle CenterX=0 CenterY=0 CenterZ=0 NormalX=0 NormalY=0 NormalZ=1 Radius=2.5
  constraints (2):
    c: Coincident(g0,g-1)
    c: Radius(g0) = 2.5
FEATURE [Part::Extrusion] Extrude435
  Base = -> Sketch371
  Dir = (0,-22,0)
  Solid = true
FEATURE [Part::Chamfer] Chamfer051
  Base = -> Extrude435
  Edges = 1 edges r=0.8: [Edge3]
FEATURE [Sketcher::SketchObject] Sketch372
  Placement = pos=(0,0,0) rot=(1,0,0;1.5708rad)
  Support = -> Extrude433 [Face9]
  sketch-geometry (4):
    g0: Circle CenterX=-15.5 CenterY=15.5 CenterZ=0 NormalX=0 NormalY=0 NormalZ=1 Radius=2
    g1: Circle CenterX=15.5 CenterY=15.5 CenterZ=0 NormalX=0 NormalY=0 NormalZ=1 Radius=2
    g2: Circle CenterX=-15.5 CenterY=-15.5 CenterZ=0 NormalX=0 NormalY=0 NormalZ=1 Radius=2
    g3: Circle CenterX=15.5 CenterY=-15.5 CenterZ=0 NormalX=0 NormalY=0 NormalZ=1 Radius=2
  constraints (9):
    c: Distance(g0,g1) = 31
    c: Distance(g0,g2) = 31
    c: Symmetric(g0,g2,g-1)
    c: Symmetric(g0,g1,g-2)
    c: Symmetric(g2,g3,g-2)
    c: Radius(g0) = 2
    c: Equal(g0,g1)
    c: Equal(g0,g2)
    c: Equal(g0,g3)
FEATURE [Part::Extrusion] Extrude436
  Base = -> Sketch372
  Dir = (0,4.5,0)
  Solid = true
FEATURE [Part::Cut] Cut164
  Base = -> Extrude433
  Tool = -> Extrude436
FEATURE [Sketcher::SketchObject] Sketch373
  Placement = pos=(0,0,0) rot=(1,0,0;1.5708rad)
  sketch-geometry (1):
    g0: Circle CenterX=0 CenterY=0 CenterZ=0 NormalX=0 NormalY=0 NormalZ=1 Radius=9
  constraints (2):
    c: Coincident(g0,g-1)
    c: Radius(g0) = 9
FEATURE [Part::Extrusion] Extrude437
  Base = -> Sketch373
  Dir = (0,25,0)
  Solid = true
FEATURE [Sketcher::SketchObject] Sketch374
  Placement = pos=(0,0,0) rot=(1,0,0;1.5708rad)
  sketch-geometry (1):
    g0: Circle CenterX=0 CenterY=0 CenterZ=0 NormalX=0 NormalY=0 NormalZ=1 Radius=2.5
  constraints (2):
    c: Coincident(g0,g-1)
    c: Radius(g0) = 2.5
FEATURE [Part::Extrusion] Extrude438
  Base = -> Sketch374
  Dir = (0,10,0)
  Solid = true
FEATURE [Part::Cut] Cut165
  Base = -> Extrude437
  Tool = -> Extrude438
FEATURE [Sketcher::SketchObject] Sketch375
  Placement = pos=(0,25,0) rot=(0,0.707107,0.707107;3.14159rad)
  Support = -> Cut165 [Face3]
  sketch-geometry (1):
    g0: Circle CenterX=0 CenterY=0 CenterZ=0 NormalX=0 NormalY=0 NormalZ=1 Radius=4
  constraints (2):
    c: Coincident(g0,g-1)
    c: Radius(g0) = 4
FEATURE [Part::Extrusion] Extrude439
  Base = -> Sketch375
  Dir = (0,-10,0)
  Solid = true
FEATURE [Part::Cut] Cut166  label="Accouplement_017"
  Base = -> Cut165
  Placement = pos=(-2288,-12,0) rot=(1,0,0;3.14159rad)
  Tool = -> Extrude439
FEATURE [Part::Fuse] Fusion094
  Base = -> Extrude434
  Tool = -> Cut164
FEATURE [Part::Fuse] Fusion095  label="Moteur_017"
  Base = -> Chamfer051
  Placement = pos=(-2288,0,0) rot=(0,0,1;0rad)
  Tool = -> Fusion094
FEATURE [Sketcher::SketchObject] Sketch376
  Placement = pos=(0,0,0) rot=(1,0,0;1.5708rad)
  sketch-geometry (4):
    g0: LineSegment StartX=-50 StartY=0 StartZ=0 EndX=-47 EndY=0 EndZ=0
    g1: LineSegment StartX=47 StartY=0 StartZ=0 EndX=50 EndY=0 EndZ=0
    g2: ArcOfCircle CenterX=0 CenterY=0 CenterZ=0 NormalX=0 NormalY=0 NormalZ=1 Radius=47 StartAngle=3.14159 EndAngle=6.28319
    g3: ArcOfCircle CenterX=0 CenterY=0 CenterZ=0 NormalX=0 NormalY=0 NormalZ=1 Radius=50 StartAngle=3.14159 EndAngle=6.28319
  constraints (13):
    c: Horizontal(g0)
    c: PointOnObject(g1,g-1)
    c: Horizontal(g1)
    c: Coincident(g2,g-1)
    c: PointOnObject(g2,g-1)
    c: Coincident(g3,g-1)
    c: Coincident(g3,g1)
    c: PointOnObject(g3,g-1)
    c: Coincident(g0,g3)
    c: Coincident(g0,g2)
    c: Distance(g0,g1) = 100
    c: Distance(g0,g0) = 3
    c: Coincident(g1,g2)
FEATURE [Part::Extrusion] Extrude440  label="Demi_tube_sous_miroir_017"
  Base = -> Sketch376
  Dir = (0,2000,0)
  Placement = pos=(-2288,-62,20) rot=(0,0,1;3.14159rad)
  Solid = true
FEATURE [Part::Feature] Part__Feature019  label="Coussinet_autolub_C2-151-8-128_017"
  Placement = pos=(-2288,-46,0) rot=(0,0,1;1.5708rad)
  shape: bbox 16 x 8 x 16 mm, 12 faces (baked)
FEATURE [Sketcher::SketchObject] Sketch377
  Placement = pos=(0,0,0) rot=(1,0,0;1.5708rad)
  sketch-geometry (21):
    g0: Circle CenterX=0 CenterY=0 CenterZ=0 NormalX=0 NormalY=0 NormalZ=1 Radius=6
    g1: LineSegment StartX=-20.5 StartY=15 StartZ=0 EndX=20.5 EndY=15 EndZ=0
    g2: ArcOfCircle CenterX=20.5 CenterY=13 CenterZ=0 NormalX=0 NormalY=0 NormalZ=1 Radius=2 StartAngle=6.28319 EndAngle=7.85398
    g3: LineSegment StartX=22.5 StartY=13 StartZ=0 EndX=22.5 EndY=-73 EndZ=0
    g4: LineSegment StartX=-22.5 StartY=13 StartZ=0 EndX=-22.5 EndY=-73 EndZ=0
    g5: ArcOfCircle CenterX=-20.5 CenterY=13 CenterZ=0 NormalX=0 NormalY=0 NormalZ=1 Radius=2 StartAngle=1.5708 EndAngle=3.14159
    g6: ArcOfCircle CenterX=-20.5 CenterY=-73 CenterZ=0 NormalX=0 NormalY=0 NormalZ=1 Radius=2 StartAngle=3.14159 EndAngle=4.71239
    g7: ArcOfCircle CenterX=20.5 CenterY=-73 CenterZ=0 NormalX=0 NormalY=0 NormalZ=1 Radius=2 StartAngle=4.71239 EndAngle=6.28319
    g8: LineSegment StartX=-20.5 StartY=-75 StartZ=0 EndX=20.5 EndY=-75 EndZ=0
    g9: ArcOfCircle CenterX=0 CenterY=-16.7 CenterZ=0 NormalX=0 NormalY=0 NormalZ=1 Radius=1.5 StartAngle=0 EndAngle=3.14159
    g10: ArcOfCircle CenterX=0 CenterY=-24.3 CenterZ=0 NormalX=0 NormalY=0 NormalZ=1 Radius=1.5 StartAngle=3.14159 EndAngle=6.28319
    g11: LineSegment StartX=-1.5 StartY=-16.7 StartZ=0 EndX=-1.5 EndY=-24.3 EndZ=0
    g12: LineSegment StartX=1.5 StartY=-16.7 StartZ=0 EndX=1.5 EndY=-24.3 EndZ=0
    g13: Circle CenterX=-12.5 CenterY=-45 CenterZ=0 NormalX=0 NormalY=0 NormalZ=1 Radius=3.5
    g14: Circle CenterX=12.5 CenterY=-45 CenterZ=0 NormalX=0 NormalY=0 NormalZ=1 Radius=3.5
    g15: Circle CenterX=-12.5 CenterY=-65 CenterZ=0 NormalX=0 NormalY=0 NormalZ=1 Radius=3.5
    g16: Circle CenterX=12.5 CenterY=-65 CenterZ=0 NormalX=0 NormalY=0 NormalZ=1 Radius=3.5
    g17: LineSegment [constr] StartX=-12.5 StartY=-45 StartZ=0 EndX=12.5 EndY=-45 EndZ=0
    g18: LineSegment [constr] StartX=-12.5 StartY=-45 StartZ=0 EndX=-12.5 EndY=-65 EndZ=0
    g19: LineSegment [constr] StartX=-12.5 StartY=-65 StartZ=0 EndX=12.5 EndY=-65 EndZ=0
    g20: LineSegment [constr] StartX=12.5 StartY=-45 StartZ=0 EndX=12.5 EndY=-65 EndZ=0
  constraints (59):
    c: Coincident(g0,g-1)
    c: Radius(g0) = 6
    c: Horizontal(g1)
    c: Coincident(g2,g1)
    c: Coincident(g3,g2)
    c: Vertical(g3)
    c: Vertical(g4)
    c: Coincident(g5,g1)
    c: Coincident(g5,g4)
    c: Coincident(g7,g3)
    c: Coincident(g8,g6)
    c: Coincident(g8,g7)
    c: Tangent(g8,g7)
    c: Tangent(g5,g4)
    c: Tangent(g5,g1)
    c: Tangent(g1,g2)
    c: Tangent(g2,g3)
    c: Coincident(g4,g6)
    c: Tangent(g6,g4)
    c: Tangent(g6,g8)
    c: Horizontal(g8)
    c: Tangent(g7,g3)
    c: Distance(g4,g2) = 45
    c: Symmetric(g4,g2,g-2)
    c: Distance(g1,g6) = 90
    c: DistanceY(g-1,g1) = 15
    c: Tangent(g9,g12) = 1.5708
    c: Tangent(g9,g11) = -1.5708
    c: Tangent(g11,g10) = -1.5708
    c: Tangent(g12,g10) = 1.5708
    c: Vertical(g11)
    c: Equal(g9,g10)
    c: PointOnObject(g9,g-2)
    c: Distance(g-1,g9) = 16.7
    c: Distance(g9,g10) = 7.6
    c: Radius(g9) = 1.5
    c: Radius(g13) = 3.5
    c: Equal(g13,g14)
    c: Equal(g13,g16)
    c: Equal(g13,g15)
    c: Radius(g5) = 2
    c: Equal(g5,g7)
    c: Equal(g5,g6)
    c: DistanceY(g-1,g13) = -45
    c: Coincident(g17,g13)
    c: Coincident(g17,g14)
    c: Horizontal(g17)
    c: Coincident(g18,g13)
    c: Coincident(g18,g15)
    c: Coincident(g19,g15)
    c: Coincident(g19,g16)
    c: Horizontal(g19)
    c: Coincident(g20,g14)
    c: Coincident(g20,g16)
    c: Vertical(g18)
    c: Vertical(g20)
    c: Distance(g13,g15) = 20
    c: Distance(g13,g14) = 25
    c: Symmetric(g13,g14,g-2)
FEATURE [Part::Extrusion] Extrude441  label="Plaque_support_017"
  Base = -> Sketch377
  Dir = (0,6,0)
  Placement = pos=(-2288,-46,0) rot=(0,0,1;0rad)
  Solid = true
FEATURE [Sketcher::SketchObject] Sketch378
  Placement = pos=(0,0,0) rot=(0.57735,0.57735,0.57735;2.0944rad)
  sketch-geometry (8):
    g0: LineSegment StartX=0 StartY=33 StartZ=0 EndX=-2 EndY=33 EndZ=0
    g1: LineSegment StartX=-2 StartY=33 StartZ=0 EndX=-2 EndY=-24 EndZ=0
    g2: ArcOfCircle CenterX=-4 CenterY=-24 CenterZ=0 NormalX=0 NormalY=0 NormalZ=1 Radius=2 StartAngle=4.71239 EndAngle=6.28319
    g3: LineSegment StartX=-4 StartY=-26 StartZ=0 EndX=-38 EndY=-26 EndZ=0
    g4: LineSegment StartX=-38 StartY=-26 StartZ=0 EndX=-38 EndY=-28 EndZ=0
    g5: LineSegment StartX=-38 StartY=-28 StartZ=0 EndX=-4 EndY=-28 EndZ=0
    g6: ArcOfCircle CenterX=-4 CenterY=-24 CenterZ=0 NormalX=0 NormalY=0 NormalZ=1 Radius=4 StartAngle=4.71239 EndAngle=6.28319
    g7: LineSegment StartX=0 StartY=-24 StartZ=0 EndX=0 EndY=33 EndZ=0
  constraints (22):
    c: PointOnObject(g0,g-2)
    c: Horizontal(g0)
    c: Coincident(g0,g1)
    c: Vertical(g1)
    c: Tangent(g1,g2) = 1.5708
    c: Tangent(g2,g3) = 1.5708
    c: Coincident(g3,g4)
    c: Vertical(g4)
    c: Coincident(g4,g5)
    c: Horizontal(g5)
    c: Tangent(g5,g6) = -1.5708
    c: PointOnObject(g6,g-2)
    c: Tangent(g6,g7) = -1.5708
    c: Coincident(g7,g0)
    c: Horizontal(g3)
    c: DistanceX(g0,g0) = 2
    c: Radius(g2) = 2
    c: Radius(g6) = 4
    c: DistanceY(g3,g4) = -2
    c: Distance(g-1,g0) = 33
    c: DistanceY(g-1,g5) = -28
    c: DistanceX(g6,g4) = -38
FEATURE [Part::Extrusion] Extrude442
  Base = -> Sketch378
  Dir = (-32.5,0,0)
  Solid = true
FEATURE [Part::Extrusion] Extrude443
  Base = -> Sketch378
  Dir = (32.5,0,0)
  Solid = true
FEATURE [Part::MultiFuse] Fusion096
  Shapes = -> [Extrude442,Extrude443]
FEATURE [Sketcher::SketchObject] Sketch379
  Placement = pos=(0,-2,0) rot=(1,0,0;1.5708rad)
  Support = -> Fusion096 [Face3]
  sketch-geometry (9):
    g0: ArcOfCircle CenterX=0 CenterY=0 CenterZ=0 NormalX=0 NormalY=0 NormalZ=1 Radius=32.5 StartAngle=0 EndAngle=3.14159
    g1: LineSegment StartX=-32.5 StartY=0 StartZ=0 EndX=-32.5 EndY=34 EndZ=0
    g2: LineSegment StartX=-32.5 StartY=34 StartZ=0 EndX=32.5 EndY=34 EndZ=0
    g3: LineSegment StartX=32.5 StartY=34 StartZ=0 EndX=32.5 EndY=0 EndZ=0
    g4: Circle CenterX=0 CenterY=0 CenterZ=0 NormalX=0 NormalY=0 NormalZ=1 Radius=11
    g5: Circle CenterX=-15.5 CenterY=15.5 CenterZ=0 NormalX=0 NormalY=0 NormalZ=1 Radius=2
    g6: Circle CenterX=15.5 CenterY=15.5 CenterZ=0 NormalX=0 NormalY=0 NormalZ=1 Radius=2
    g7: Circle CenterX=-15.5 CenterY=-15.5 CenterZ=0 NormalX=0 NormalY=0 NormalZ=1 Radius=2
    g8: Circle CenterX=15.5 CenterY=-15.5 CenterZ=0 NormalX=0 NormalY=0 NormalZ=1 Radius=2
  constraints (23):
    c: Coincident(g0,g-1)
    c: PointOnObject(g0,g-1)
    c: PointOnObject(g0,g-1)
    c: Coincident(g1,g0)
    c: Vertical(g1)
    c: Coincident(g1,g2)
    c: Horizontal(g2)
    c: Coincident(g2,g3)
    c: Coincident(g3,g0)
    c: Vertical(g3)
    c: DistanceY(g1,g0) = -34
    c: Coincident(g4,g-1)
    c: Radius(g4) = 11
    c: DistanceX(g1,g2) = 65
    c: Radius(g5) = 2
    c: Equal(g5,g6)
    c: Equal(g5,g8)
    c: Equal(g5,g7)
    c: Symmetric(g5,g6,g-2)
    c: Symmetric(g5,g7,g-1)
    c: Symmetric(g7,g8,g-2)
    c: DistanceX(g5,g6) = 31
    c: DistanceY(g5,g7) = -31
FEATURE [Part::Extrusion] Extrude444
  Base = -> Sketch379
  Dir = (0,2,0)
  Solid = true
FEATURE [Part::Cut] Cut167
  Base = -> Fusion096
  Tool = -> Extrude444
FEATURE [Sketcher::SketchObject] Sketch380
  ExternalGeometry = -> [Cut167]
  Placement = pos=(0,0,-26) rot=(0,0,1;0rad)
  Support = -> Cut167 [Face5]
  sketch-geometry (5):
    g0: Circle CenterX=-25 CenterY=-12 CenterZ=0 NormalX=0 NormalY=0 NormalZ=1 Radius=3.5
    g1: Circle CenterX=-25 CenterY=-30 CenterZ=0 NormalX=0 NormalY=0 NormalZ=1 Radius=3.5
    g2: Circle CenterX=25 CenterY=-12 CenterZ=0 NormalX=0 NormalY=0 NormalZ=1 Radius=3.5
    g3: Circle CenterX=25 CenterY=-30 CenterZ=0 NormalX=0 NormalY=0 NormalZ=1 Radius=3.5
    g4: LineSegment [constr] StartX=-25 StartY=-12 StartZ=0 EndX=-25 EndY=-30 EndZ=0
  constraints (12):
    c: Radius(g0) = 3.5
    c: Equal(g0,g2)
    c: Equal(g0,g3)
    c: Equal(g0,g1)
    c: Symmetric(g0,g2,g-2)
    c: Symmetric(g1,g3,g-2)
    c: Coincident(g4,g0)
    c: Coincident(g4,g1)
    c: Vertical(g4)
    c: DistanceY(g0,g1) = -18
    c: DistanceY(g-3,g1) = 8
    c: DistanceX(g0,g2) = 50
FEATURE [Part::Extrusion] Extrude445
  Base = -> Sketch380
  Dir = (0,0,-2)
  Solid = true
FEATURE [Part::Cut] Cut168
  Base = -> Cut167
  Tool = -> Extrude445
FEATURE [Part::Fillet] Fillet037  label="Plaque_moteur_017"
  Base = -> Cut168
  Edges = 2 edges r=4: [Edge5,Edge59]
  Placement = pos=(-2288,0,0) rot=(0,0,1;0rad)
FEATURE [Sketcher::SketchObject] Sketch381
  Placement = pos=(0,0,0) rot=(1,0,0;1.5708rad)
  sketch-geometry (4):
    g0: LineSegment StartX=-3.15 StartY=5.95 StartZ=0 EndX=3.15 EndY=5.95 EndZ=0
    g1: LineSegment StartX=3.15 StartY=5.95 StartZ=0 EndX=3.15 EndY=-5.95 EndZ=0
    g2: LineSegment StartX=3.15 StartY=-5.95 StartZ=0 EndX=-3.15 EndY=-5.95 EndZ=0
    g3: LineSegment StartX=-3.15 StartY=-5.95 StartZ=0 EndX=-3.15 EndY=5.95 EndZ=0
  constraints (12):
    c: Coincident(g0,g1)
    c: Coincident(g1,g2)
    c: Coincident(g2,g3)
    c: Coincident(g3,g0)
    c: Horizontal(g0)
    c: Horizontal(g2)
    c: Vertical(g1)
    c: Vertical(g3)
    c: DistanceX(g0,g0) = 6.3
    c: DistanceY(g0,g2) = -11.9
    c: Symmetric(g0,g0,g-2)
    c: Symmetric(g0,g1,g-1)
FEATURE [Part::Extrusion] Extrude446
  Base = -> Sketch381
  Dir = (0,-10.8,0)
  Solid = true
FEATURE [Sketcher::SketchObject] Sketch382
  ExternalGeometry = -> [Extrude446]
  Placement = pos=(0,-10.8,0) rot=(1,0,0;1.5708rad)
  Support = -> Extrude446 [Face6]
  sketch-geometry (4):
    g0: LineSegment StartX=-3.15 StartY=1.55 StartZ=0 EndX=3.15 EndY=1.55 EndZ=0
    g1: LineSegment StartX=3.15 StartY=1.55 StartZ=0 EndX=3.15 EndY=-1.55 EndZ=0
    g2: LineSegment StartX=3.15 StartY=-1.55 StartZ=0 EndX=-3.15 EndY=-1.55 EndZ=0
    g3: LineSegment StartX=-3.15 StartY=-1.55 StartZ=0 EndX=-3.15 EndY=1.55 EndZ=0
  constraints (12):
    c: Coincident(g0,g1)
    c: Coincident(g1,g2)
    c: Coincident(g2,g3)
    c: Coincident(g3,g0)
    c: Horizontal(g0)
    c: Horizontal(g2)
    c: Vertical(g1)
    c: Vertical(g3)
    c: PointOnObject(g0,g-4)
    c: PointOnObject(g0,g-3)
    c: DistanceY(g0,g2) = -3.1
    c: Symmetric(g0,g1,g-1)
FEATURE [Part::Extrusion] Extrude447
  Base = -> Sketch382
  Dir = (0,7.7,0)
  Solid = true
FEATURE [Part::Cut] Cut169
  Base = -> Extrude446
  Tool = -> Extrude447
FEATURE [Part::Chamfer] Chamfer052
  Base = -> Cut169
  Edges = 4 edges r=0.5: [Edge7,Edge9,Edge15,Edge17]
FEATURE [Part::Chamfer] Chamfer053
  Base = -> Chamfer052
  Edges = 1 edges r=1.2: [Edge13]
FEATURE [Sketcher::SketchObject] Sketch383
  ExternalGeometry = -> [Chamfer053]
  Placement = pos=(0,0,5.95) rot=(0,0,1;0rad)
  Support = -> Chamfer053 [Face5]
  sketch-geometry (4):
    g0: LineSegment StartX=-3 StartY=0 StartZ=0 EndX=3 EndY=0 EndZ=0
    g1: LineSegment StartX=3 StartY=0 StartZ=0 EndX=3 EndY=-3.1 EndZ=0
    g2: LineSegment StartX=3 StartY=-3.1 StartZ=0 EndX=-3 EndY=-3.1 EndZ=0
    g3: LineSegment StartX=-3 StartY=-3.1 StartZ=0 EndX=-3 EndY=0 EndZ=0
  constraints (12):
    c: Coincident(g0,g1)
    c: Coincident(g1,g2)
    c: Coincident(g2,g3)
    c: Coincident(g3,g0)
    c: Horizontal(g0)
    c: Horizontal(g2)
    c: Vertical(g1)
    c: Vertical(g3)
    c: PointOnObject(g0,g-1)
    c: DistanceX(g-3,g0) = 0.15
    c: Symmetric(g0,g0,g-2)
    c: DistanceY(g0,g1) = -3.1
FEATURE [Part::Extrusion] Extrude448
  Base = -> Sketch383
  Dir = (0,0,6.3)
  Solid = true
FEATURE [Sketcher::SketchObject] Sketch384
  ExternalGeometry = -> [Extrude448]
  Placement = pos=(0,-3.1,0) rot=(1,0,0;1.5708rad)
  Support = -> Extrude448 [Face3]
  sketch-geometry (1):
    g0: Circle CenterX=0 CenterY=9.5 CenterZ=0 NormalX=0 NormalY=0 NormalZ=1 Radius=1.65
  constraints (3):
    c: PointOnObject(g0,g-2)
    c: Radius(g0) = 1.65
    c: DistanceY(g0,g-3) = -3.55
FEATURE [Part::Extrusion] Extrude449
  Base = -> Sketch384
  Dir = (0,6,0)
  Solid = true
FEATURE [Part::Cut] Cut170
  Base = -> Extrude448
  Tool = -> Extrude449
FEATURE [Part::Fillet] Fillet038
  Base = -> Cut170
  Edges = 2 edges r=1.35: [Edge8,Edge11]
FEATURE [Part::MultiFuse] Fusion097
  Shapes = -> [Chamfer053]
FEATURE [Sketcher::SketchObject] Sketch385
  Placement = pos=(0,0,0) rot=(0,0.707107,0.707107;3.14159rad)
  Support = -> Fusion097 [Face7]
  sketch-geometry (4):
    g0: Circle CenterX=-1.27 CenterY=3.8 CenterZ=0 NormalX=0 NormalY=0 NormalZ=1 Radius=0.2
    g1: Circle CenterX=1.27 CenterY=3.8 CenterZ=0 NormalX=0 NormalY=0 NormalZ=1 Radius=0.2
    g2: Circle CenterX=-1.27 CenterY=-3.8 CenterZ=0 NormalX=0 NormalY=0 NormalZ=1 Radius=0.2
    g3: Circle CenterX=1.27 CenterY=-3.8 CenterZ=0 NormalX=0 NormalY=0 NormalZ=1 Radius=0.2
  constraints (9):
    c: Radius(g0) = 0.2
    c: Equal(g0,g1)
    c: Equal(g0,g3)
    c: Equal(g0,g2)
    c: Symmetric(g0,g1,g-2)
    c: Symmetric(g2,g3,g-2)
    c: Symmetric(g0,g2,g-1)
    c: DistanceX(g0,g1) = 2.54
    c: DistanceY(g1,g3) = -7.6
FEATURE [Part::Extrusion] Extrude450
  Base = -> Sketch385
  Dir = (0,7.8,0)
  Solid = true
FEATURE [Part::MultiFuse] Fusion098  label="Capteur_optique_017"
  Placement = pos=(-2288,-46,-20.7) rot=(0,0,1;0rad)
  Shapes = -> [Fusion097,Fillet038,Extrude450]
FEATURE [Sketcher::SketchObject] Sketch386
  Placement = pos=(0,0,0) rot=(1,0,0;1.5708rad)
  sketch-geometry (1):
    g0: Circle CenterX=0 CenterY=0 CenterZ=0 NormalX=0 NormalY=0 NormalZ=1 Radius=4
  constraints (2):
    c: Coincident(g0,g-1)
    c: Radius(g0) = 4
FEATURE [Part::Extrusion] Extrude451
  Base = -> Sketch386
  Dir = (0,50,0)
  Solid = true
FEATURE [Sketcher::SketchObject] Sketch387
  Placement = pos=(0,0,0) rot=(0.57735,0.57735,0.57735;2.0944rad)
  sketch-geometry (1):
    g0: Circle CenterX=6 CenterY=0 CenterZ=0 NormalX=0 NormalY=0 NormalZ=1 Radius=2
  constraints (3):
    c: DistanceX(g-1,g0) = 6
    c: Radius(g0) = 2
    c: PointOnObject(g0,g-1)
FEATURE [Part::Extrusion] Extrude452
  Base = -> Sketch387
  Dir = (4,0,0)
  Solid = true
FEATURE [Part::Extrusion] Extrude453
  Base = -> Sketch387
  Dir = (-4,0,0)
  Solid = true
FEATURE [Part::Cut] Cut171
  Base = -> Extrude451
  Tool = -> Extrude452
FEATURE [Part::Cut] Cut172  label="Axe_D8_017"
  Base = -> Cut171
  Placement = pos=(-2288,-86,0) rot=(0,0,1;0rad)
  Tool = -> Extrude453
FEATURE [Sketcher::SketchObject] Sketch388
  Placement = pos=(0,0,0) rot=(1,0,0;1.5708rad)
  sketch-geometry (1):
    g0: Circle CenterX=0 CenterY=0 CenterZ=0 NormalX=0 NormalY=0 NormalZ=1 Radius=2
  constraints (2):
    c: Coincident(g0,g-1)
    c: Radius(g0) = 2
FEATURE [Part::Extrusion] Extrude454  label="Axe_D4_017"
  Base = -> Sketch388
  Dir = (0,103.6,0)
  Placement = pos=(-2236.2,-80,0) rot=(0,0,1;1.5708rad)
  Solid = true
FEATURE [Sketcher::SketchObject] Sketch389
  Placement = pos=(0,0,0) rot=(1,0,0;1.5708rad)
  sketch-geometry (8):
    g0: LineSegment StartX=-50 StartY=0 StartZ=0 EndX=50 EndY=0 EndZ=0
    g1: LineSegment StartX=50 StartY=0 StartZ=0 EndX=50 EndY=-2 EndZ=0
    g2: LineSegment StartX=50 StartY=-2 StartZ=0 EndX=47 EndY=-2 EndZ=0
    g3: LineSegment StartX=47 StartY=-2 StartZ=0 EndX=44 EndY=-16 EndZ=0
    g4: LineSegment StartX=44 StartY=-16 StartZ=0 EndX=-44 EndY=-16 EndZ=0
    g5: LineSegment StartX=-44 StartY=-16 StartZ=0 EndX=-47 EndY=-2 EndZ=0
    g6: LineSegment StartX=-47 StartY=-2 StartZ=0 EndX=-50 EndY=-2 EndZ=0
    g7: LineSegment StartX=-50 StartY=-2 StartZ=0 EndX=-50 EndY=0 EndZ=0
  constraints (24):
    c: PointOnObject(g0,g-1)
    c: Horizontal(g0)
    c: Coincident(g0,g1)
    c: Vertical(g1)
    c: Coincident(g1,g2)
    c: Horizontal(g2)
    c: Coincident(g2,g3)
    c: Coincident(g3,g4)
    c: Horizontal(g4)
    c: Coincident(g4,g5)
    c: Coincident(g5,g6)
    c: Horizontal(g6)
    c: Coincident(g6,g7)
    c: Coincident(g7,g0)
    c: Vertical(g7)
    c: DistanceY(g0,g6) = -2
    c: DistanceX(g6,g5) = 3
    c: DistanceX(g0,g0) = 100
    c: Symmetric(g0,g0,g-2)
    c: Symmetric(g6,g1,g-2)
    c: Symmetric(g5,g2,g-2)
    c: Symmetric(g4,g3,g-2)
    c: DistanceX(g4,g3) = 88
    c: DistanceY(g0,g4) = -16
FEATURE [Part::Extrusion] Extrude455  label="Plaque_alveolaire_017"
  Base = -> Sketch389
  Dir = (0,2000,0)
  Placement = pos=(-2288,-62,22) rot=(0,0,1;3.14159rad)
  Solid = true
FEATURE [App::DocumentObjectGroup] Groupe022  label="Assemblage_miroir X=-858_002"
  Group = -> [Cut166,Fusion095,Extrude440,Part__Feature019,Extrude441,Fillet037,Fusion098,Cut172,Extrude454,Extrude455]
FEATURE [Sketcher::SketchObject] Sketch390
  Placement = pos=(0,0,0) rot=(1,0,0;1.5708rad)
  sketch-geometry (8):
    g0: LineSegment StartX=-21.15 StartY=16.15 StartZ=0 EndX=-16.15 EndY=21.15 EndZ=0
    g1: LineSegment StartX=-16.15 StartY=21.15 StartZ=0 EndX=16.15 EndY=21.15 EndZ=0
    g2: LineSegment StartX=16.15 StartY=21.15 StartZ=0 EndX=21.15 EndY=16.15 EndZ=0
    g3: LineSegment StartX=21.15 StartY=16.15 StartZ=0 EndX=21.15 EndY=-16.15 EndZ=0
    g4: LineSegment StartX=21.15 StartY=-16.15 StartZ=0 EndX=16.15 EndY=-21.15 EndZ=0
    g5: LineSegment StartX=16.15 StartY=-21.15 StartZ=0 EndX=-16.15 EndY=-21.15 EndZ=0
    g6: LineSegment StartX=-16.15 StartY=-21.15 StartZ=0 EndX=-21.15 EndY=-16.15 EndZ=0
    g7: LineSegment StartX=-21.15 StartY=-16.15 StartZ=0 EndX=-21.15 EndY=16.15 EndZ=0
  constraints (21):
    c: Coincident(g0,g1)
    c: Horizontal(g1)
    c: Coincident(g1,g2)
    c: Coincident(g2,g3)
    c: Vertical(g3)
    c: Coincident(g3,g4)
    c: Coincident(g4,g5)
    c: Horizontal(g5)
    c: Coincident(g5,g6)
    c: Coincident(g6,g7)
    c: Coincident(g7,g0)
    c: Angle(g7,g0) = 2.35619
    c: Distance(g0,g7) = 5
    c: Distance(g2,g7) = 42.3
    c: Distance(g5,g1) = 42.3
    c: Symmetric(g6,g3,g-2)
    c: Symmetric(g5,g4,g-2)
    c: Symmetric(g0,g2,g-2)
    c: Symmetric(g0,g1,g-2)
    c: Symmetric(g0,g6,g-1)
    c: Symmetric(g0,g5,g-1)
FEATURE [Part::Extrusion] Extrude456
  Base = -> Sketch390
  Dir = (0,48,0)
  Solid = true
FEATURE [Sketcher::SketchObject] Sketch391
  Placement = pos=(0,0,0) rot=(1,0,0;1.5708rad)
  Support = -> Extrude456 [Face9]
  sketch-geometry (1):
    g0: Circle CenterX=0 CenterY=0 CenterZ=0 NormalX=0 NormalY=0 NormalZ=1 Radius=11
  constraints (2):
    c: Coincident(g0,g-1)
    c: Radius(g0) = 11
FEATURE [Part::Extrusion] Extrude457
  Base = -> Sketch391
  Dir = (0,-2,0)
  Solid = true
FEATURE [Sketcher::SketchObject] Sketch392
  Placement = pos=(0,-2,0) rot=(1,0,0;1.5708rad)
  Support = -> Extrude457 [Face3]
  sketch-geometry (1):
    g0: Circle CenterX=0 CenterY=0 CenterZ=0 NormalX=0 NormalY=0 NormalZ=1 Radius=2.5
  constraints (2):
    c: Coincident(g0,g-1)
    c: Radius(g0) = 2.5
FEATURE [Part::Extrusion] Extrude458
  Base = -> Sketch392
  Dir = (0,-22,0)
  Solid = true
FEATURE [Part::Chamfer] Chamfer054
  Base = -> Extrude458
  Edges = 1 edges r=0.8: [Edge3]
FEATURE [Sketcher::SketchObject] Sketch393
  Placement = pos=(0,0,0) rot=(1,0,0;1.5708rad)
  Support = -> Extrude456 [Face9]
  sketch-geometry (4):
    g0: Circle CenterX=-15.5 CenterY=15.5 CenterZ=0 NormalX=0 NormalY=0 NormalZ=1 Radius=2
    g1: Circle CenterX=15.5 CenterY=15.5 CenterZ=0 NormalX=0 NormalY=0 NormalZ=1 Radius=2
    g2: Circle CenterX=-15.5 CenterY=-15.5 CenterZ=0 NormalX=0 NormalY=0 NormalZ=1 Radius=2
    g3: Circle CenterX=15.5 CenterY=-15.5 CenterZ=0 NormalX=0 NormalY=0 NormalZ=1 Radius=2
  constraints (9):
    c: Distance(g0,g1) = 31
    c: Distance(g0,g2) = 31
    c: Symmetric(g0,g2,g-1)
    c: Symmetric(g0,g1,g-2)
    c: Symmetric(g2,g3,g-2)
    c: Radius(g0) = 2
    c: Equal(g0,g1)
    c: Equal(g0,g2)
    c: Equal(g0,g3)
FEATURE [Part::Extrusion] Extrude459
  Base = -> Sketch393
  Dir = (0,4.5,0)
  Solid = true
FEATURE [Part::Cut] Cut173
  Base = -> Extrude456
  Tool = -> Extrude459
FEATURE [Sketcher::SketchObject] Sketch394
  Placement = pos=(0,0,0) rot=(1,0,0;1.5708rad)
  sketch-geometry (1):
    g0: Circle CenterX=0 CenterY=0 CenterZ=0 NormalX=0 NormalY=0 NormalZ=1 Radius=9
  constraints (2):
    c: Coincident(g0,g-1)
    c: Radius(g0) = 9
FEATURE [Part::Extrusion] Extrude460
  Base = -> Sketch394
  Dir = (0,25,0)
  Solid = true
FEATURE [Sketcher::SketchObject] Sketch395
  Placement = pos=(0,0,0) rot=(1,0,0;1.5708rad)
  sketch-geometry (1):
    g0: Circle CenterX=0 CenterY=0 CenterZ=0 NormalX=0 NormalY=0 NormalZ=1 Radius=2.5
  constraints (2):
    c: Coincident(g0,g-1)
    c: Radius(g0) = 2.5
FEATURE [Part::Extrusion] Extrude461
  Base = -> Sketch395
  Dir = (0,10,0)
  Solid = true
FEATURE [Part::Cut] Cut174
  Base = -> Extrude460
  Tool = -> Extrude461
FEATURE [Sketcher::SketchObject] Sketch396
  Placement = pos=(0,25,0) rot=(0,0.707107,0.707107;3.14159rad)
  Support = -> Cut174 [Face3]
  sketch-geometry (1):
    g0: Circle CenterX=0 CenterY=0 CenterZ=0 NormalX=0 NormalY=0 NormalZ=1 Radius=4
  constraints (2):
    c: Coincident(g0,g-1)
    c: Radius(g0) = 4
FEATURE [Part::Extrusion] Extrude462
  Base = -> Sketch396
  Dir = (0,-10,0)
  Solid = true
FEATURE [Part::Cut] Cut175  label="Accouplement_018"
  Base = -> Cut174
  Placement = pos=(-2431,-12,0) rot=(1,0,0;3.14159rad)
  Tool = -> Extrude462
FEATURE [Part::Fuse] Fusion099
  Base = -> Extrude457
  Tool = -> Cut173
FEATURE [Part::Fuse] Fusion100  label="Moteur_018"
  Base = -> Chamfer054
  Placement = pos=(-2431,0,0) rot=(0,0,1;0rad)
  Tool = -> Fusion099
FEATURE [Sketcher::SketchObject] Sketch397
  Placement = pos=(0,0,0) rot=(1,0,0;1.5708rad)
  sketch-geometry (4):
    g0: LineSegment StartX=-50 StartY=0 StartZ=0 EndX=-47 EndY=0 EndZ=0
    g1: LineSegment StartX=47 StartY=0 StartZ=0 EndX=50 EndY=0 EndZ=0
    g2: ArcOfCircle CenterX=0 CenterY=0 CenterZ=0 NormalX=0 NormalY=0 NormalZ=1 Radius=47 StartAngle=3.14159 EndAngle=6.28319
    g3: ArcOfCircle CenterX=0 CenterY=0 CenterZ=0 NormalX=0 NormalY=0 NormalZ=1 Radius=50 StartAngle=3.14159 EndAngle=6.28319
  constraints (13):
    c: Horizontal(g0)
    c: PointOnObject(g1,g-1)
    c: Horizontal(g1)
    c: Coincident(g2,g-1)
    c: PointOnObject(g2,g-1)
    c: Coincident(g3,g-1)
    c: Coincident(g3,g1)
    c: PointOnObject(g3,g-1)
    c: Coincident(g0,g3)
    c: Coincident(g0,g2)
    c: Distance(g0,g1) = 100
    c: Distance(g0,g0) = 3
    c: Coincident(g1,g2)
FEATURE [Part::Extrusion] Extrude463  label="Demi_tube_sous_miroir_018"
  Base = -> Sketch397
  Dir = (0,2000,0)
  Placement = pos=(-2431,-62,20) rot=(0,0,1;3.14159rad)
  Solid = true
FEATURE [Part::Feature] Part__Feature020  label="Coussinet_autolub_C2-151-8-128_018"
  Placement = pos=(-2431,-46,0) rot=(0,0,1;1.5708rad)
  shape: bbox 16 x 8 x 16 mm, 12 faces (baked)
FEATURE [Sketcher::SketchObject] Sketch398
  Placement = pos=(0,0,0) rot=(1,0,0;1.5708rad)
  sketch-geometry (21):
    g0: Circle CenterX=0 CenterY=0 CenterZ=0 NormalX=0 NormalY=0 NormalZ=1 Radius=6
    g1: LineSegment StartX=-20.5 StartY=15 StartZ=0 EndX=20.5 EndY=15 EndZ=0
    g2: ArcOfCircle CenterX=20.5 CenterY=13 CenterZ=0 NormalX=0 NormalY=0 NormalZ=1 Radius=2 StartAngle=6.28319 EndAngle=7.85398
    g3: LineSegment StartX=22.5 StartY=13 StartZ=0 EndX=22.5 EndY=-73 EndZ=0
    g4: LineSegment StartX=-22.5 StartY=13 StartZ=0 EndX=-22.5 EndY=-73 EndZ=0
    g5: ArcOfCircle CenterX=-20.5 CenterY=13 CenterZ=0 NormalX=0 NormalY=0 NormalZ=1 Radius=2 StartAngle=1.5708 EndAngle=3.14159
    g6: ArcOfCircle CenterX=-20.5 CenterY=-73 CenterZ=0 NormalX=0 NormalY=0 NormalZ=1 Radius=2 StartAngle=3.14159 EndAngle=4.71239
    g7: ArcOfCircle CenterX=20.5 CenterY=-73 CenterZ=0 NormalX=0 NormalY=0 NormalZ=1 Radius=2 StartAngle=4.71239 EndAngle=6.28319
    g8: LineSegment StartX=-20.5 StartY=-75 StartZ=0 EndX=20.5 EndY=-75 EndZ=0
    g9: ArcOfCircle CenterX=0 CenterY=-16.7 CenterZ=0 NormalX=0 NormalY=0 NormalZ=1 Radius=1.5 StartAngle=0 EndAngle=3.14159
    g10: ArcOfCircle CenterX=0 CenterY=-24.3 CenterZ=0 NormalX=0 NormalY=0 NormalZ=1 Radius=1.5 StartAngle=3.14159 EndAngle=6.28319
    g11: LineSegment StartX=-1.5 StartY=-16.7 StartZ=0 EndX=-1.5 EndY=-24.3 EndZ=0
    g12: LineSegment StartX=1.5 StartY=-16.7 StartZ=0 EndX=1.5 EndY=-24.3 EndZ=0
    g13: Circle CenterX=-12.5 CenterY=-45 CenterZ=0 NormalX=0 NormalY=0 NormalZ=1 Radius=3.5
    g14: Circle CenterX=12.5 CenterY=-45 CenterZ=0 NormalX=0 NormalY=0 NormalZ=1 Radius=3.5
    g15: Circle CenterX=-12.5 CenterY=-65 CenterZ=0 NormalX=0 NormalY=0 NormalZ=1 Radius=3.5
    g16: Circle CenterX=12.5 CenterY=-65 CenterZ=0 NormalX=0 NormalY=0 NormalZ=1 Radius=3.5
    g17: LineSegment [constr] StartX=-12.5 StartY=-45 StartZ=0 EndX=12.5 EndY=-45 EndZ=0
    g18: LineSegment [constr] StartX=-12.5 StartY=-45 StartZ=0 EndX=-12.5 EndY=-65 EndZ=0
    g19: LineSegment [constr] StartX=-12.5 StartY=-65 StartZ=0 EndX=12.5 EndY=-65 EndZ=0
    g20: LineSegment [constr] StartX=12.5 StartY=-45 StartZ=0 EndX=12.5 EndY=-65 EndZ=0
  constraints (59):
    c: Coincident(g0,g-1)
    c: Radius(g0) = 6
    c: Horizontal(g1)
    c: Coincident(g2,g1)
    c: Coincident(g3,g2)
    c: Vertical(g3)
    c: Vertical(g4)
    c: Coincident(g5,g1)
    c: Coincident(g5,g4)
    c: Coincident(g7,g3)
    c: Coincident(g8,g6)
    c: Coincident(g8,g7)
    c: Tangent(g8,g7)
    c: Tangent(g5,g4)
    c: Tangent(g5,g1)
    c: Tangent(g1,g2)
    c: Tangent(g2,g3)
    c: Coincident(g4,g6)
    c: Tangent(g6,g4)
    c: Tangent(g6,g8)
    c: Horizontal(g8)
    c: Tangent(g7,g3)
    c: Distance(g4,g2) = 45
    c: Symmetric(g4,g2,g-2)
    c: Distance(g1,g6) = 90
    c: DistanceY(g-1,g1) = 15
    c: Tangent(g9,g12) = 1.5708
    c: Tangent(g9,g11) = -1.5708
    c: Tangent(g11,g10) = -1.5708
    c: Tangent(g12,g10) = 1.5708
    c: Vertical(g11)
    c: Equal(g9,g10)
    c: PointOnObject(g9,g-2)
    c: Distance(g-1,g9) = 16.7
    c: Distance(g9,g10) = 7.6
    c: Radius(g9) = 1.5
    c: Radius(g13) = 3.5
    c: Equal(g13,g14)
    c: Equal(g13,g16)
    c: Equal(g13,g15)
    c: Radius(g5) = 2
    c: Equal(g5,g7)
    c: Equal(g5,g6)
    c: DistanceY(g-1,g13) = -45
    c: Coincident(g17,g13)
    c: Coincident(g17,g14)
    c: Horizontal(g17)
    c: Coincident(g18,g13)
    c: Coincident(g18,g15)
    c: Coincident(g19,g15)
    c: Coincident(g19,g16)
    c: Horizontal(g19)
    c: Coincident(g20,g14)
    c: Coincident(g20,g16)
    c: Vertical(g18)
    c: Vertical(g20)
    c: Distance(g13,g15) = 20
    c: Distance(g13,g14) = 25
    c: Symmetric(g13,g14,g-2)
FEATURE [Part::Extrusion] Extrude464  label="Plaque_support_018"
  Base = -> Sketch398
  Dir = (0,6,0)
  Placement = pos=(-2431,-46,0) rot=(0,0,1;0rad)
  Solid = true
FEATURE [Sketcher::SketchObject] Sketch399
  Placement = pos=(0,0,0) rot=(0.57735,0.57735,0.57735;2.0944rad)
  sketch-geometry (8):
    g0: LineSegment StartX=0 StartY=33 StartZ=0 EndX=-2 EndY=33 EndZ=0
    g1: LineSegment StartX=-2 StartY=33 StartZ=0 EndX=-2 EndY=-24 EndZ=0
    g2: ArcOfCircle CenterX=-4 CenterY=-24 CenterZ=0 NormalX=0 NormalY=0 NormalZ=1 Radius=2 StartAngle=4.71239 EndAngle=6.28319
    g3: LineSegment StartX=-4 StartY=-26 StartZ=0 EndX=-38 EndY=-26 EndZ=0
    g4: LineSegment StartX=-38 StartY=-26 StartZ=0 EndX=-38 EndY=-28 EndZ=0
    g5: LineSegment StartX=-38 StartY=-28 StartZ=0 EndX=-4 EndY=-28 EndZ=0
    g6: ArcOfCircle CenterX=-4 CenterY=-24 CenterZ=0 NormalX=0 NormalY=0 NormalZ=1 Radius=4 StartAngle=4.71239 EndAngle=6.28319
    g7: LineSegment StartX=0 StartY=-24 StartZ=0 EndX=0 EndY=33 EndZ=0
  constraints (22):
    c: PointOnObject(g0,g-2)
    c: Horizontal(g0)
    c: Coincident(g0,g1)
    c: Vertical(g1)
    c: Tangent(g1,g2) = 1.5708
    c: Tangent(g2,g3) = 1.5708
    c: Coincident(g3,g4)
    c: Vertical(g4)
    c: Coincident(g4,g5)
    c: Horizontal(g5)
    c: Tangent(g5,g6) = -1.5708
    c: PointOnObject(g6,g-2)
    c: Tangent(g6,g7) = -1.5708
    c: Coincident(g7,g0)
    c: Horizontal(g3)
    c: DistanceX(g0,g0) = 2
    c: Radius(g2) = 2
    c: Radius(g6) = 4
    c: DistanceY(g3,g4) = -2
    c: Distance(g-1,g0) = 33
    c: DistanceY(g-1,g5) = -28
    c: DistanceX(g6,g4) = -38
FEATURE [Part::Extrusion] Extrude465
  Base = -> Sketch399
  Dir = (-32.5,0,0)
  Solid = true
FEATURE [Part::Extrusion] Extrude466
  Base = -> Sketch399
  Dir = (32.5,0,0)
  Solid = true
FEATURE [Part::MultiFuse] Fusion101
  Shapes = -> [Extrude465,Extrude466]
FEATURE [Sketcher::SketchObject] Sketch400
  Placement = pos=(0,-2,0) rot=(1,0,0;1.5708rad)
  Support = -> Fusion101 [Face3]
  sketch-geometry (9):
    g0: ArcOfCircle CenterX=0 CenterY=0 CenterZ=0 NormalX=0 NormalY=0 NormalZ=1 Radius=32.5 StartAngle=0 EndAngle=3.14159
    g1: LineSegment StartX=-32.5 StartY=0 StartZ=0 EndX=-32.5 EndY=34 EndZ=0
    g2: LineSegment StartX=-32.5 StartY=34 StartZ=0 EndX=32.5 EndY=34 EndZ=0
    g3: LineSegment StartX=32.5 StartY=34 StartZ=0 EndX=32.5 EndY=0 EndZ=0
    g4: Circle CenterX=0 CenterY=0 CenterZ=0 NormalX=0 NormalY=0 NormalZ=1 Radius=11
    g5: Circle CenterX=-15.5 CenterY=15.5 CenterZ=0 NormalX=0 NormalY=0 NormalZ=1 Radius=2
    g6: Circle CenterX=15.5 CenterY=15.5 CenterZ=0 NormalX=0 NormalY=0 NormalZ=1 Radius=2
    g7: Circle CenterX=-15.5 CenterY=-15.5 CenterZ=0 NormalX=0 NormalY=0 NormalZ=1 Radius=2
    g8: Circle CenterX=15.5 CenterY=-15.5 CenterZ=0 NormalX=0 NormalY=0 NormalZ=1 Radius=2
  constraints (23):
    c: Coincident(g0,g-1)
    c: PointOnObject(g0,g-1)
    c: PointOnObject(g0,g-1)
    c: Coincident(g1,g0)
    c: Vertical(g1)
    c: Coincident(g1,g2)
    c: Horizontal(g2)
    c: Coincident(g2,g3)
    c: Coincident(g3,g0)
    c: Vertical(g3)
    c: DistanceY(g1,g0) = -34
    c: Coincident(g4,g-1)
    c: Radius(g4) = 11
    c: DistanceX(g1,g2) = 65
    c: Radius(g5) = 2
    c: Equal(g5,g6)
    c: Equal(g5,g8)
    c: Equal(g5,g7)
    c: Symmetric(g5,g6,g-2)
    c: Symmetric(g5,g7,g-1)
    c: Symmetric(g7,g8,g-2)
    c: DistanceX(g5,g6) = 31
    c: DistanceY(g5,g7) = -31
FEATURE [Part::Extrusion] Extrude467
  Base = -> Sketch400
  Dir = (0,2,0)
  Solid = true
FEATURE [Part::Cut] Cut176
  Base = -> Fusion101
  Tool = -> Extrude467
FEATURE [Sketcher::SketchObject] Sketch401
  ExternalGeometry = -> [Cut176]
  Placement = pos=(0,0,-26) rot=(0,0,1;0rad)
  Support = -> Cut176 [Face5]
  sketch-geometry (5):
    g0: Circle CenterX=-25 CenterY=-12 CenterZ=0 NormalX=0 NormalY=0 NormalZ=1 Radius=3.5
    g1: Circle CenterX=-25 CenterY=-30 CenterZ=0 NormalX=0 NormalY=0 NormalZ=1 Radius=3.5
    g2: Circle CenterX=25 CenterY=-12 CenterZ=0 NormalX=0 NormalY=0 NormalZ=1 Radius=3.5
    g3: Circle CenterX=25 CenterY=-30 CenterZ=0 NormalX=0 NormalY=0 NormalZ=1 Radius=3.5
    g4: LineSegment [constr] StartX=-25 StartY=-12 StartZ=0 EndX=-25 EndY=-30 EndZ=0
  constraints (12):
    c: Radius(g0) = 3.5
    c: Equal(g0,g2)
    c: Equal(g0,g3)
    c: Equal(g0,g1)
    c: Symmetric(g0,g2,g-2)
    c: Symmetric(g1,g3,g-2)
    c: Coincident(g4,g0)
    c: Coincident(g4,g1)
    c: Vertical(g4)
    c: DistanceY(g0,g1) = -18
    c: DistanceY(g-3,g1) = 8
    c: DistanceX(g0,g2) = 50
FEATURE [Part::Extrusion] Extrude468
  Base = -> Sketch401
  Dir = (0,0,-2)
  Solid = true
FEATURE [Part::Cut] Cut177
  Base = -> Cut176
  Tool = -> Extrude468
FEATURE [Part::Fillet] Fillet039  label="Plaque_moteur_018"
  Base = -> Cut177
  Edges = 2 edges r=4: [Edge5,Edge59]
  Placement = pos=(-2431,0,0) rot=(0,0,1;0rad)
FEATURE [Sketcher::SketchObject] Sketch402
  Placement = pos=(0,0,0) rot=(1,0,0;1.5708rad)
  sketch-geometry (4):
    g0: LineSegment StartX=-3.15 StartY=5.95 StartZ=0 EndX=3.15 EndY=5.95 EndZ=0
    g1: LineSegment StartX=3.15 StartY=5.95 StartZ=0 EndX=3.15 EndY=-5.95 EndZ=0
    g2: LineSegment StartX=3.15 StartY=-5.95 StartZ=0 EndX=-3.15 EndY=-5.95 EndZ=0
    g3: LineSegment StartX=-3.15 StartY=-5.95 StartZ=0 EndX=-3.15 EndY=5.95 EndZ=0
  constraints (12):
    c: Coincident(g0,g1)
    c: Coincident(g1,g2)
    c: Coincident(g2,g3)
    c: Coincident(g3,g0)
    c: Horizontal(g0)
    c: Horizontal(g2)
    c: Vertical(g1)
    c: Vertical(g3)
    c: DistanceX(g0,g0) = 6.3
    c: DistanceY(g0,g2) = -11.9
    c: Symmetric(g0,g0,g-2)
    c: Symmetric(g0,g1,g-1)
FEATURE [Part::Extrusion] Extrude469
  Base = -> Sketch402
  Dir = (0,-10.8,0)
  Solid = true
FEATURE [Sketcher::SketchObject] Sketch403
  ExternalGeometry = -> [Extrude469]
  Placement = pos=(0,-10.8,0) rot=(1,0,0;1.5708rad)
  Support = -> Extrude469 [Face6]
  sketch-geometry (4):
    g0: LineSegment StartX=-3.15 StartY=1.55 StartZ=0 EndX=3.15 EndY=1.55 EndZ=0
    g1: LineSegment StartX=3.15 StartY=1.55 StartZ=0 EndX=3.15 EndY=-1.55 EndZ=0
    g2: LineSegment StartX=3.15 StartY=-1.55 StartZ=0 EndX=-3.15 EndY=-1.55 EndZ=0
    g3: LineSegment StartX=-3.15 StartY=-1.55 StartZ=0 EndX=-3.15 EndY=1.55 EndZ=0
  constraints (12):
    c: Coincident(g0,g1)
    c: Coincident(g1,g2)
    c: Coincident(g2,g3)
    c: Coincident(g3,g0)
    c: Horizontal(g0)
    c: Horizontal(g2)
    c: Vertical(g1)
    c: Vertical(g3)
    c: PointOnObject(g0,g-4)
    c: PointOnObject(g0,g-3)
    c: DistanceY(g0,g2) = -3.1
    c: Symmetric(g0,g1,g-1)
FEATURE [Part::Extrusion] Extrude470
  Base = -> Sketch403
  Dir = (0,7.7,0)
  Solid = true
FEATURE [Part::Cut] Cut178
  Base = -> Extrude469
  Tool = -> Extrude470
FEATURE [Part::Chamfer] Chamfer055
  Base = -> Cut178
  Edges = 4 edges r=0.5: [Edge7,Edge9,Edge15,Edge17]
FEATURE [Part::Chamfer] Chamfer056
  Base = -> Chamfer055
  Edges = 1 edges r=1.2: [Edge13]
FEATURE [Sketcher::SketchObject] Sketch404
  ExternalGeometry = -> [Chamfer056]
  Placement = pos=(0,0,5.95) rot=(0,0,1;0rad)
  Support = -> Chamfer056 [Face5]
  sketch-geometry (4):
    g0: LineSegment StartX=-3 StartY=0 StartZ=0 EndX=3 EndY=0 EndZ=0
    g1: LineSegment StartX=3 StartY=0 StartZ=0 EndX=3 EndY=-3.1 EndZ=0
    g2: LineSegment StartX=3 StartY=-3.1 StartZ=0 EndX=-3 EndY=-3.1 EndZ=0
    g3: LineSegment StartX=-3 StartY=-3.1 StartZ=0 EndX=-3 EndY=0 EndZ=0
  constraints (12):
    c: Coincident(g0,g1)
    c: Coincident(g1,g2)
    c: Coincident(g2,g3)
    c: Coincident(g3,g0)
    c: Horizontal(g0)
    c: Horizontal(g2)
    c: Vertical(g1)
    c: Vertical(g3)
    c: PointOnObject(g0,g-1)
    c: DistanceX(g-3,g0) = 0.15
    c: Symmetric(g0,g0,g-2)
    c: DistanceY(g0,g1) = -3.1
FEATURE [Part::Extrusion] Extrude471
  Base = -> Sketch404
  Dir = (0,0,6.3)
  Solid = true
FEATURE [Sketcher::SketchObject] Sketch405
  ExternalGeometry = -> [Extrude471]
  Placement = pos=(0,-3.1,0) rot=(1,0,0;1.5708rad)
  Support = -> Extrude471 [Face3]
  sketch-geometry (1):
    g0: Circle CenterX=0 CenterY=9.5 CenterZ=0 NormalX=0 NormalY=0 NormalZ=1 Radius=1.65
  constraints (3):
    c: PointOnObject(g0,g-2)
    c: Radius(g0) = 1.65
    c: DistanceY(g0,g-3) = -3.55
FEATURE [Part::Extrusion] Extrude472
  Base = -> Sketch405
  Dir = (0,6,0)
  Solid = true
FEATURE [Part::Cut] Cut179
  Base = -> Extrude471
  Tool = -> Extrude472
FEATURE [Part::Fillet] Fillet040
  Base = -> Cut179
  Edges = 2 edges r=1.35: [Edge8,Edge11]
FEATURE [Part::MultiFuse] Fusion102
  Shapes = -> [Chamfer056]
FEATURE [Sketcher::SketchObject] Sketch406
  Placement = pos=(0,0,0) rot=(0,0.707107,0.707107;3.14159rad)
  Support = -> Fusion102 [Face7]
  sketch-geometry (4):
    g0: Circle CenterX=-1.27 CenterY=3.8 CenterZ=0 NormalX=0 NormalY=0 NormalZ=1 Radius=0.2
    g1: Circle CenterX=1.27 CenterY=3.8 CenterZ=0 NormalX=0 NormalY=0 NormalZ=1 Radius=0.2
    g2: Circle CenterX=-1.27 CenterY=-3.8 CenterZ=0 NormalX=0 NormalY=0 NormalZ=1 Radius=0.2
    g3: Circle CenterX=1.27 CenterY=-3.8 CenterZ=0 NormalX=0 NormalY=0 NormalZ=1 Radius=0.2
  constraints (9):
    c: Radius(g0) = 0.2
    c: Equal(g0,g1)
    c: Equal(g0,g3)
    c: Equal(g0,g2)
    c: Symmetric(g0,g1,g-2)
    c: Symmetric(g2,g3,g-2)
    c: Symmetric(g0,g2,g-1)
    c: DistanceX(g0,g1) = 2.54
    c: DistanceY(g1,g3) = -7.6
FEATURE [Part::Extrusion] Extrude473
  Base = -> Sketch406
  Dir = (0,7.8,0)
  Solid = true
FEATURE [Part::MultiFuse] Fusion103  label="Capteur_optique_018"
  Placement = pos=(-2431,-46,-20.7) rot=(0,0,1;0rad)
  Shapes = -> [Fusion102,Fillet040,Extrude473]
FEATURE [Sketcher::SketchObject] Sketch407
  Placement = pos=(0,0,0) rot=(1,0,0;1.5708rad)
  sketch-geometry (1):
    g0: Circle CenterX=0 CenterY=0 CenterZ=0 NormalX=0 NormalY=0 NormalZ=1 Radius=4
  constraints (2):
    c: Coincident(g0,g-1)
    c: Radius(g0) = 4
FEATURE [Part::Extrusion] Extrude474
  Base = -> Sketch407
  Dir = (0,50,0)
  Solid = true
FEATURE [Sketcher::SketchObject] Sketch408
  Placement = pos=(0,0,0) rot=(0.57735,0.57735,0.57735;2.0944rad)
  sketch-geometry (1):
    g0: Circle CenterX=6 CenterY=0 CenterZ=0 NormalX=0 NormalY=0 NormalZ=1 Radius=2
  constraints (3):
    c: DistanceX(g-1,g0) = 6
    c: Radius(g0) = 2
    c: PointOnObject(g0,g-1)
FEATURE [Part::Extrusion] Extrude475
  Base = -> Sketch408
  Dir = (4,0,0)
  Solid = true
FEATURE [Part::Extrusion] Extrude476
  Base = -> Sketch408
  Dir = (-4,0,0)
  Solid = true
FEATURE [Part::Cut] Cut180
  Base = -> Extrude474
  Tool = -> Extrude475
FEATURE [Part::Cut] Cut181  label="Axe_D8_018"
  Base = -> Cut180
  Placement = pos=(-2431,-86,0) rot=(0,0,1;0rad)
  Tool = -> Extrude476
FEATURE [Sketcher::SketchObject] Sketch409
  Placement = pos=(0,0,0) rot=(1,0,0;1.5708rad)
  sketch-geometry (1):
    g0: Circle CenterX=0 CenterY=0 CenterZ=0 NormalX=0 NormalY=0 NormalZ=1 Radius=2
  constraints (2):
    c: Coincident(g0,g-1)
    c: Radius(g0) = 2
FEATURE [Part::Extrusion] Extrude477  label="Axe_D4_018"
  Base = -> Sketch409
  Dir = (0,103.6,0)
  Placement = pos=(-2379.2,-80,0) rot=(0,0,1;1.5708rad)
  Solid = true
FEATURE [Sketcher::SketchObject] Sketch410
  Placement = pos=(0,0,0) rot=(1,0,0;1.5708rad)
  sketch-geometry (8):
    g0: LineSegment StartX=-50 StartY=0 StartZ=0 EndX=50 EndY=0 EndZ=0
    g1: LineSegment StartX=50 StartY=0 StartZ=0 EndX=50 EndY=-2 EndZ=0
    g2: LineSegment StartX=50 StartY=-2 StartZ=0 EndX=47 EndY=-2 EndZ=0
    g3: LineSegment StartX=47 StartY=-2 StartZ=0 EndX=44 EndY=-16 EndZ=0
    g4: LineSegment StartX=44 StartY=-16 StartZ=0 EndX=-44 EndY=-16 EndZ=0
    g5: LineSegment StartX=-44 StartY=-16 StartZ=0 EndX=-47 EndY=-2 EndZ=0
    g6: LineSegment StartX=-47 StartY=-2 StartZ=0 EndX=-50 EndY=-2 EndZ=0
    g7: LineSegment StartX=-50 StartY=-2 StartZ=0 EndX=-50 EndY=0 EndZ=0
  constraints (24):
    c: PointOnObject(g0,g-1)
    c: Horizontal(g0)
    c: Coincident(g0,g1)
    c: Vertical(g1)
    c: Coincident(g1,g2)
    c: Horizontal(g2)
    c: Coincident(g2,g3)
    c: Coincident(g3,g4)
    c: Horizontal(g4)
    c: Coincident(g4,g5)
    c: Coincident(g5,g6)
    c: Horizontal(g6)
    c: Coincident(g6,g7)
    c: Coincident(g7,g0)
    c: Vertical(g7)
    c: DistanceY(g0,g6) = -2
    c: DistanceX(g6,g5) = 3
    c: DistanceX(g0,g0) = 100
    c: Symmetric(g0,g0,g-2)
    c: Symmetric(g6,g1,g-2)
    c: Symmetric(g5,g2,g-2)
    c: Symmetric(g4,g3,g-2)
    c: DistanceX(g4,g3) = 88
    c: DistanceY(g0,g4) = -16
FEATURE [Part::Extrusion] Extrude478  label="Plaque_alveolaire_018"
  Base = -> Sketch410
  Dir = (0,2000,0)
  Placement = pos=(-2431,-62,22) rot=(0,0,1;3.14159rad)
  Solid = true
FEATURE [App::DocumentObjectGroup] Groupe023  label="Assemblage_miroir X=-1001_002"
  Group = -> [Cut175,Fusion100,Extrude463,Part__Feature020,Extrude464,Fillet039,Fusion103,Cut181,Extrude477,Extrude478]
FEATURE [Sketcher::SketchObject] Sketch411
  Placement = pos=(0,0,0) rot=(1,0,0;1.5708rad)
  sketch-geometry (8):
    g0: LineSegment StartX=-21.15 StartY=16.15 StartZ=0 EndX=-16.15 EndY=21.15 EndZ=0
    g1: LineSegment StartX=-16.15 StartY=21.15 StartZ=0 EndX=16.15 EndY=21.15 EndZ=0
    g2: LineSegment StartX=16.15 StartY=21.15 StartZ=0 EndX=21.15 EndY=16.15 EndZ=0
    g3: LineSegment StartX=21.15 StartY=16.15 StartZ=0 EndX=21.15 EndY=-16.15 EndZ=0
    g4: LineSegment StartX=21.15 StartY=-16.15 StartZ=0 EndX=16.15 EndY=-21.15 EndZ=0
    g5: LineSegment StartX=16.15 StartY=-21.15 StartZ=0 EndX=-16.15 EndY=-21.15 EndZ=0
    g6: LineSegment StartX=-16.15 StartY=-21.15 StartZ=0 EndX=-21.15 EndY=-16.15 EndZ=0
    g7: LineSegment StartX=-21.15 StartY=-16.15 StartZ=0 EndX=-21.15 EndY=16.15 EndZ=0
  constraints (21):
    c: Coincident(g0,g1)
    c: Horizontal(g1)
    c: Coincident(g1,g2)
    c: Coincident(g2,g3)
    c: Vertical(g3)
    c: Coincident(g3,g4)
    c: Coincident(g4,g5)
    c: Horizontal(g5)
    c: Coincident(g5,g6)
    c: Coincident(g6,g7)
    c: Coincident(g7,g0)
    c: Angle(g7,g0) = 2.35619
    c: Distance(g0,g7) = 5
    c: Distance(g2,g7) = 42.3
    c: Distance(g5,g1) = 42.3
    c: Symmetric(g6,g3,g-2)
    c: Symmetric(g5,g4,g-2)
    c: Symmetric(g0,g2,g-2)
    c: Symmetric(g0,g1,g-2)
    c: Symmetric(g0,g6,g-1)
    c: Symmetric(g0,g5,g-1)
FEATURE [Part::Extrusion] Extrude479
  Base = -> Sketch411
  Dir = (0,48,0)
  Solid = true
FEATURE [Sketcher::SketchObject] Sketch412
  Placement = pos=(0,0,0) rot=(1,0,0;1.5708rad)
  Support = -> Extrude479 [Face9]
  sketch-geometry (1):
    g0: Circle CenterX=0 CenterY=0 CenterZ=0 NormalX=0 NormalY=0 NormalZ=1 Radius=11
  constraints (2):
    c: Coincident(g0,g-1)
    c: Radius(g0) = 11
FEATURE [Part::Extrusion] Extrude480
  Base = -> Sketch412
  Dir = (0,-2,0)
  Solid = true
FEATURE [Sketcher::SketchObject] Sketch413
  Placement = pos=(0,-2,0) rot=(1,0,0;1.5708rad)
  Support = -> Extrude480 [Face3]
  sketch-geometry (1):
    g0: Circle CenterX=0 CenterY=0 CenterZ=0 NormalX=0 NormalY=0 NormalZ=1 Radius=2.5
  constraints (2):
    c: Coincident(g0,g-1)
    c: Radius(g0) = 2.5
FEATURE [Part::Extrusion] Extrude481
  Base = -> Sketch413
  Dir = (0,-22,0)
  Solid = true
FEATURE [Part::Chamfer] Chamfer057
  Base = -> Extrude481
  Edges = 1 edges r=0.8: [Edge3]
FEATURE [Sketcher::SketchObject] Sketch414
  Placement = pos=(0,0,0) rot=(1,0,0;1.5708rad)
  Support = -> Extrude479 [Face9]
  sketch-geometry (4):
    g0: Circle CenterX=-15.5 CenterY=15.5 CenterZ=0 NormalX=0 NormalY=0 NormalZ=1 Radius=2
    g1: Circle CenterX=15.5 CenterY=15.5 CenterZ=0 NormalX=0 NormalY=0 NormalZ=1 Radius=2
    g2: Circle CenterX=-15.5 CenterY=-15.5 CenterZ=0 NormalX=0 NormalY=0 NormalZ=1 Radius=2
    g3: Circle CenterX=15.5 CenterY=-15.5 CenterZ=0 NormalX=0 NormalY=0 NormalZ=1 Radius=2
  constraints (9):
    c: Distance(g0,g1) = 31
    c: Distance(g0,g2) = 31
    c: Symmetric(g0,g2,g-1)
    c: Symmetric(g0,g1,g-2)
    c: Symmetric(g2,g3,g-2)
    c: Radius(g0) = 2
    c: Equal(g0,g1)
    c: Equal(g0,g2)
    c: Equal(g0,g3)
FEATURE [Part::Extrusion] Extrude482
  Base = -> Sketch414
  Dir = (0,4.5,0)
  Solid = true
FEATURE [Part::Cut] Cut182
  Base = -> Extrude479
  Tool = -> Extrude482
FEATURE [Sketcher::SketchObject] Sketch415
  Placement = pos=(0,0,0) rot=(1,0,0;1.5708rad)
  sketch-geometry (1):
    g0: Circle CenterX=0 CenterY=0 CenterZ=0 NormalX=0 NormalY=0 NormalZ=1 Radius=9
  constraints (2):
    c: Coincident(g0,g-1)
    c: Radius(g0) = 9
FEATURE [Part::Extrusion] Extrude483
  Base = -> Sketch415
  Dir = (0,25,0)
  Solid = true
FEATURE [Sketcher::SketchObject] Sketch416
  Placement = pos=(0,0,0) rot=(1,0,0;1.5708rad)
  sketch-geometry (1):
    g0: Circle CenterX=0 CenterY=0 CenterZ=0 NormalX=0 NormalY=0 NormalZ=1 Radius=2.5
  constraints (2):
    c: Coincident(g0,g-1)
    c: Radius(g0) = 2.5
FEATURE [Part::Extrusion] Extrude484
  Base = -> Sketch416
  Dir = (0,10,0)
  Solid = true
FEATURE [Part::Cut] Cut183
  Base = -> Extrude483
  Tool = -> Extrude484
FEATURE [Sketcher::SketchObject] Sketch417
  Placement = pos=(0,25,0) rot=(0,0.707107,0.707107;3.14159rad)
  Support = -> Cut183 [Face3]
  sketch-geometry (1):
    g0: Circle CenterX=0 CenterY=0 CenterZ=0 NormalX=0 NormalY=0 NormalZ=1 Radius=4
  constraints (2):
    c: Coincident(g0,g-1)
    c: Radius(g0) = 4
FEATURE [Part::Extrusion] Extrude485
  Base = -> Sketch417
  Dir = (0,-10,0)
  Solid = true
FEATURE [Part::Cut] Cut184  label="Accouplement_019"
  Base = -> Cut183
  Placement = pos=(-2574,-12,0) rot=(1,0,0;3.14159rad)
  Tool = -> Extrude485
FEATURE [Part::Fuse] Fusion104
  Base = -> Extrude480
  Tool = -> Cut182
FEATURE [Part::Fuse] Fusion105  label="Moteur_019"
  Base = -> Chamfer057
  Placement = pos=(-2574,0,0) rot=(0,0,1;0rad)
  Tool = -> Fusion104
FEATURE [Sketcher::SketchObject] Sketch418
  Placement = pos=(0,0,0) rot=(1,0,0;1.5708rad)
  sketch-geometry (4):
    g0: LineSegment StartX=-50 StartY=0 StartZ=0 EndX=-47 EndY=0 EndZ=0
    g1: LineSegment StartX=47 StartY=0 StartZ=0 EndX=50 EndY=0 EndZ=0
    g2: ArcOfCircle CenterX=0 CenterY=0 CenterZ=0 NormalX=0 NormalY=0 NormalZ=1 Radius=47 StartAngle=3.14159 EndAngle=6.28319
    g3: ArcOfCircle CenterX=0 CenterY=0 CenterZ=0 NormalX=0 NormalY=0 NormalZ=1 Radius=50 StartAngle=3.14159 EndAngle=6.28319
  constraints (13):
    c: Horizontal(g0)
    c: PointOnObject(g1,g-1)
    c: Horizontal(g1)
    c: Coincident(g2,g-1)
    c: PointOnObject(g2,g-1)
    c: Coincident(g3,g-1)
    c: Coincident(g3,g1)
    c: PointOnObject(g3,g-1)
    c: Coincident(g0,g3)
    c: Coincident(g0,g2)
    c: Distance(g0,g1) = 100
    c: Distance(g0,g0) = 3
    c: Coincident(g1,g2)
FEATURE [Part::Extrusion] Extrude486  label="Demi_tube_sous_miroir_019"
  Base = -> Sketch418
  Dir = (0,2000,0)
  Placement = pos=(-2574,-62,20) rot=(0,0,1;3.14159rad)
  Solid = true
FEATURE [Part::Feature] Part__Feature021  label="Coussinet_autolub_C2-151-8-128_019"
  Placement = pos=(-2574,-46,0) rot=(0,0,1;1.5708rad)
  shape: bbox 16 x 8 x 16 mm, 12 faces (baked)
FEATURE [Sketcher::SketchObject] Sketch419
  Placement = pos=(0,0,0) rot=(1,0,0;1.5708rad)
  sketch-geometry (21):
    g0: Circle CenterX=0 CenterY=0 CenterZ=0 NormalX=0 NormalY=0 NormalZ=1 Radius=6
    g1: LineSegment StartX=-20.5 StartY=15 StartZ=0 EndX=20.5 EndY=15 EndZ=0
    g2: ArcOfCircle CenterX=20.5 CenterY=13 CenterZ=0 NormalX=0 NormalY=0 NormalZ=1 Radius=2 StartAngle=6.28319 EndAngle=7.85398
    g3: LineSegment StartX=22.5 StartY=13 StartZ=0 EndX=22.5 EndY=-73 EndZ=0
    g4: LineSegment StartX=-22.5 StartY=13 StartZ=0 EndX=-22.5 EndY=-73 EndZ=0
    g5: ArcOfCircle CenterX=-20.5 CenterY=13 CenterZ=0 NormalX=0 NormalY=0 NormalZ=1 Radius=2 StartAngle=1.5708 EndAngle=3.14159
    g6: ArcOfCircle CenterX=-20.5 CenterY=-73 CenterZ=0 NormalX=0 NormalY=0 NormalZ=1 Radius=2 StartAngle=3.14159 EndAngle=4.71239
    g7: ArcOfCircle CenterX=20.5 CenterY=-73 CenterZ=0 NormalX=0 NormalY=0 NormalZ=1 Radius=2 StartAngle=4.71239 EndAngle=6.28319
    g8: LineSegment StartX=-20.5 StartY=-75 StartZ=0 EndX=20.5 EndY=-75 EndZ=0
    g9: ArcOfCircle CenterX=0 CenterY=-16.7 CenterZ=0 NormalX=0 NormalY=0 NormalZ=1 Radius=1.5 StartAngle=0 EndAngle=3.14159
    g10: ArcOfCircle CenterX=0 CenterY=-24.3 CenterZ=0 NormalX=0 NormalY=0 NormalZ=1 Radius=1.5 StartAngle=3.14159 EndAngle=6.28319
    g11: LineSegment StartX=-1.5 StartY=-16.7 StartZ=0 EndX=-1.5 EndY=-24.3 EndZ=0
    g12: LineSegment StartX=1.5 StartY=-16.7 StartZ=0 EndX=1.5 EndY=-24.3 EndZ=0
    g13: Circle CenterX=-12.5 CenterY=-45 CenterZ=0 NormalX=0 NormalY=0 NormalZ=1 Radius=3.5
    g14: Circle CenterX=12.5 CenterY=-45 CenterZ=0 NormalX=0 NormalY=0 NormalZ=1 Radius=3.5
    g15: Circle CenterX=-12.5 CenterY=-65 CenterZ=0 NormalX=0 NormalY=0 NormalZ=1 Radius=3.5
    g16: Circle CenterX=12.5 CenterY=-65 CenterZ=0 NormalX=0 NormalY=0 NormalZ=1 Radius=3.5
    g17: LineSegment [constr] StartX=-12.5 StartY=-45 StartZ=0 EndX=12.5 EndY=-45 EndZ=0
    g18: LineSegment [constr] StartX=-12.5 StartY=-45 StartZ=0 EndX=-12.5 EndY=-65 EndZ=0
    g19: LineSegment [constr] StartX=-12.5 StartY=-65 StartZ=0 EndX=12.5 EndY=-65 EndZ=0
    g20: LineSegment [constr] StartX=12.5 StartY=-45 StartZ=0 EndX=12.5 EndY=-65 EndZ=0
  constraints (59):
    c: Coincident(g0,g-1)
    c: Radius(g0) = 6
    c: Horizontal(g1)
    c: Coincident(g2,g1)
    c: Coincident(g3,g2)
    c: Vertical(g3)
    c: Vertical(g4)
    c: Coincident(g5,g1)
    c: Coincident(g5,g4)
    c: Coincident(g7,g3)
    c: Coincident(g8,g6)
    c: Coincident(g8,g7)
    c: Tangent(g8,g7)
    c: Tangent(g5,g4)
    c: Tangent(g5,g1)
    c: Tangent(g1,g2)
    c: Tangent(g2,g3)
    c: Coincident(g4,g6)
    c: Tangent(g6,g4)
    c: Tangent(g6,g8)
    c: Horizontal(g8)
    c: Tangent(g7,g3)
    c: Distance(g4,g2) = 45
    c: Symmetric(g4,g2,g-2)
    c: Distance(g1,g6) = 90
    c: DistanceY(g-1,g1) = 15
    c: Tangent(g9,g12) = 1.5708
    c: Tangent(g9,g11) = -1.5708
    c: Tangent(g11,g10) = -1.5708
    c: Tangent(g12,g10) = 1.5708
    c: Vertical(g11)
    c: Equal(g9,g10)
    c: PointOnObject(g9,g-2)
    c: Distance(g-1,g9) = 16.7
    c: Distance(g9,g10) = 7.6
    c: Radius(g9) = 1.5
    c: Radius(g13) = 3.5
    c: Equal(g13,g14)
    c: Equal(g13,g16)
    c: Equal(g13,g15)
    c: Radius(g5) = 2
    c: Equal(g5,g7)
    c: Equal(g5,g6)
    c: DistanceY(g-1,g13) = -45
    c: Coincident(g17,g13)
    c: Coincident(g17,g14)
    c: Horizontal(g17)
    c: Coincident(g18,g13)
    c: Coincident(g18,g15)
    c: Coincident(g19,g15)
    c: Coincident(g19,g16)
    c: Horizontal(g19)
    c: Coincident(g20,g14)
    c: Coincident(g20,g16)
    c: Vertical(g18)
    c: Vertical(g20)
    c: Distance(g13,g15) = 20
    c: Distance(g13,g14) = 25
    c: Symmetric(g13,g14,g-2)
FEATURE [Part::Extrusion] Extrude487  label="Plaque_support_019"
  Base = -> Sketch419
  Dir = (0,6,0)
  Placement = pos=(-2574,-46,0) rot=(0,0,1;0rad)
  Solid = true
FEATURE [Sketcher::SketchObject] Sketch420
  Placement = pos=(0,0,0) rot=(0.57735,0.57735,0.57735;2.0944rad)
  sketch-geometry (8):
    g0: LineSegment StartX=0 StartY=33 StartZ=0 EndX=-2 EndY=33 EndZ=0
    g1: LineSegment StartX=-2 StartY=33 StartZ=0 EndX=-2 EndY=-24 EndZ=0
    g2: ArcOfCircle CenterX=-4 CenterY=-24 CenterZ=0 NormalX=0 NormalY=0 NormalZ=1 Radius=2 StartAngle=4.71239 EndAngle=6.28319
    g3: LineSegment StartX=-4 StartY=-26 StartZ=0 EndX=-38 EndY=-26 EndZ=0
    g4: LineSegment StartX=-38 StartY=-26 StartZ=0 EndX=-38 EndY=-28 EndZ=0
    g5: LineSegment StartX=-38 StartY=-28 StartZ=0 EndX=-4 EndY=-28 EndZ=0
    g6: ArcOfCircle CenterX=-4 CenterY=-24 CenterZ=0 NormalX=0 NormalY=0 NormalZ=1 Radius=4 StartAngle=4.71239 EndAngle=6.28319
    g7: LineSegment StartX=0 StartY=-24 StartZ=0 EndX=0 EndY=33 EndZ=0
  constraints (22):
    c: PointOnObject(g0,g-2)
    c: Horizontal(g0)
    c: Coincident(g0,g1)
    c: Vertical(g1)
    c: Tangent(g1,g2) = 1.5708
    c: Tangent(g2,g3) = 1.5708
    c: Coincident(g3,g4)
    c: Vertical(g4)
    c: Coincident(g4,g5)
    c: Horizontal(g5)
    c: Tangent(g5,g6) = -1.5708
    c: PointOnObject(g6,g-2)
    c: Tangent(g6,g7) = -1.5708
    c: Coincident(g7,g0)
    c: Horizontal(g3)
    c: DistanceX(g0,g0) = 2
    c: Radius(g2) = 2
    c: Radius(g6) = 4
    c: DistanceY(g3,g4) = -2
    c: Distance(g-1,g0) = 33
    c: DistanceY(g-1,g5) = -28
    c: DistanceX(g6,g4) = -38
FEATURE [Part::Extrusion] Extrude488
  Base = -> Sketch420
  Dir = (-32.5,0,0)
  Solid = true
FEATURE [Part::Extrusion] Extrude489
  Base = -> Sketch420
  Dir = (32.5,0,0)
  Solid = true
FEATURE [Part::MultiFuse] Fusion106
  Shapes = -> [Extrude488,Extrude489]
FEATURE [Sketcher::SketchObject] Sketch421
  Placement = pos=(0,-2,0) rot=(1,0,0;1.5708rad)
  Support = -> Fusion106 [Face3]
  sketch-geometry (9):
    g0: ArcOfCircle CenterX=0 CenterY=0 CenterZ=0 NormalX=0 NormalY=0 NormalZ=1 Radius=32.5 StartAngle=0 EndAngle=3.14159
    g1: LineSegment StartX=-32.5 StartY=0 StartZ=0 EndX=-32.5 EndY=34 EndZ=0
    g2: LineSegment StartX=-32.5 StartY=34 StartZ=0 EndX=32.5 EndY=34 EndZ=0
    g3: LineSegment StartX=32.5 StartY=34 StartZ=0 EndX=32.5 EndY=0 EndZ=0
    g4: Circle CenterX=0 CenterY=0 CenterZ=0 NormalX=0 NormalY=0 NormalZ=1 Radius=11
    g5: Circle CenterX=-15.5 CenterY=15.5 CenterZ=0 NormalX=0 NormalY=0 NormalZ=1 Radius=2
    g6: Circle CenterX=15.5 CenterY=15.5 CenterZ=0 NormalX=0 NormalY=0 NormalZ=1 Radius=2
    g7: Circle CenterX=-15.5 CenterY=-15.5 CenterZ=0 NormalX=0 NormalY=0 NormalZ=1 Radius=2
    g8: Circle CenterX=15.5 CenterY=-15.5 CenterZ=0 NormalX=0 NormalY=0 NormalZ=1 Radius=2
  constraints (23):
    c: Coincident(g0,g-1)
    c: PointOnObject(g0,g-1)
    c: PointOnObject(g0,g-1)
    c: Coincident(g1,g0)
    c: Vertical(g1)
    c: Coincident(g1,g2)
    c: Horizontal(g2)
    c: Coincident(g2,g3)
    c: Coincident(g3,g0)
    c: Vertical(g3)
    c: DistanceY(g1,g0) = -34
    c: Coincident(g4,g-1)
    c: Radius(g4) = 11
    c: DistanceX(g1,g2) = 65
    c: Radius(g5) = 2
    c: Equal(g5,g6)
    c: Equal(g5,g8)
    c: Equal(g5,g7)
    c: Symmetric(g5,g6,g-2)
    c: Symmetric(g5,g7,g-1)
    c: Symmetric(g7,g8,g-2)
    c: DistanceX(g5,g6) = 31
    c: DistanceY(g5,g7) = -31
FEATURE [Part::Extrusion] Extrude490
  Base = -> Sketch421
  Dir = (0,2,0)
  Solid = true
FEATURE [Part::Cut] Cut185
  Base = -> Fusion106
  Tool = -> Extrude490
FEATURE [Sketcher::SketchObject] Sketch422
  ExternalGeometry = -> [Cut185]
  Placement = pos=(0,0,-26) rot=(0,0,1;0rad)
  Support = -> Cut185 [Face5]
  sketch-geometry (5):
    g0: Circle CenterX=-25 CenterY=-12 CenterZ=0 NormalX=0 NormalY=0 NormalZ=1 Radius=3.5
    g1: Circle CenterX=-25 CenterY=-30 CenterZ=0 NormalX=0 NormalY=0 NormalZ=1 Radius=3.5
    g2: Circle CenterX=25 CenterY=-12 CenterZ=0 NormalX=0 NormalY=0 NormalZ=1 Radius=3.5
    g3: Circle CenterX=25 CenterY=-30 CenterZ=0 NormalX=0 NormalY=0 NormalZ=1 Radius=3.5
    g4: LineSegment [constr] StartX=-25 StartY=-12 StartZ=0 EndX=-25 EndY=-30 EndZ=0
  constraints (12):
    c: Radius(g0) = 3.5
    c: Equal(g0,g2)
    c: Equal(g0,g3)
    c: Equal(g0,g1)
    c: Symmetric(g0,g2,g-2)
    c: Symmetric(g1,g3,g-2)
    c: Coincident(g4,g0)
    c: Coincident(g4,g1)
    c: Vertical(g4)
    c: DistanceY(g0,g1) = -18
    c: DistanceY(g-3,g1) = 8
    c: DistanceX(g0,g2) = 50
FEATURE [Part::Extrusion] Extrude491
  Base = -> Sketch422
  Dir = (0,0,-2)
  Solid = true
FEATURE [Part::Cut] Cut186
  Base = -> Cut185
  Tool = -> Extrude491
FEATURE [Part::Fillet] Fillet041  label="Plaque_moteur_019"
  Base = -> Cut186
  Edges = 2 edges r=4: [Edge5,Edge59]
  Placement = pos=(-2574,0,0) rot=(0,0,1;0rad)
FEATURE [Sketcher::SketchObject] Sketch423
  Placement = pos=(0,0,0) rot=(1,0,0;1.5708rad)
  sketch-geometry (4):
    g0: LineSegment StartX=-3.15 StartY=5.95 StartZ=0 EndX=3.15 EndY=5.95 EndZ=0
    g1: LineSegment StartX=3.15 StartY=5.95 StartZ=0 EndX=3.15 EndY=-5.95 EndZ=0
    g2: LineSegment StartX=3.15 StartY=-5.95 StartZ=0 EndX=-3.15 EndY=-5.95 EndZ=0
    g3: LineSegment StartX=-3.15 StartY=-5.95 StartZ=0 EndX=-3.15 EndY=5.95 EndZ=0
  constraints (12):
    c: Coincident(g0,g1)
    c: Coincident(g1,g2)
    c: Coincident(g2,g3)
    c: Coincident(g3,g0)
    c: Horizontal(g0)
    c: Horizontal(g2)
    c: Vertical(g1)
    c: Vertical(g3)
    c: DistanceX(g0,g0) = 6.3
    c: DistanceY(g0,g2) = -11.9
    c: Symmetric(g0,g0,g-2)
    c: Symmetric(g0,g1,g-1)
FEATURE [Part::Extrusion] Extrude492
  Base = -> Sketch423
  Dir = (0,-10.8,0)
  Solid = true
FEATURE [Sketcher::SketchObject] Sketch424
  ExternalGeometry = -> [Extrude492]
  Placement = pos=(0,-10.8,0) rot=(1,0,0;1.5708rad)
  Support = -> Extrude492 [Face6]
  sketch-geometry (4):
    g0: LineSegment StartX=-3.15 StartY=1.55 StartZ=0 EndX=3.15 EndY=1.55 EndZ=0
    g1: LineSegment StartX=3.15 StartY=1.55 StartZ=0 EndX=3.15 EndY=-1.55 EndZ=0
    g2: LineSegment StartX=3.15 StartY=-1.55 StartZ=0 EndX=-3.15 EndY=-1.55 EndZ=0
    g3: LineSegment StartX=-3.15 StartY=-1.55 StartZ=0 EndX=-3.15 EndY=1.55 EndZ=0
  constraints (12):
    c: Coincident(g0,g1)
    c: Coincident(g1,g2)
    c: Coincident(g2,g3)
    c: Coincident(g3,g0)
    c: Horizontal(g0)
    c: Horizontal(g2)
    c: Vertical(g1)
    c: Vertical(g3)
    c: PointOnObject(g0,g-4)
    c: PointOnObject(g0,g-3)
    c: DistanceY(g0,g2) = -3.1
    c: Symmetric(g0,g1,g-1)
FEATURE [Part::Extrusion] Extrude493
  Base = -> Sketch424
  Dir = (0,7.7,0)
  Solid = true
FEATURE [Part::Cut] Cut187
  Base = -> Extrude492
  Tool = -> Extrude493
FEATURE [Part::Chamfer] Chamfer058
  Base = -> Cut187
  Edges = 4 edges r=0.5: [Edge7,Edge9,Edge15,Edge17]
FEATURE [Part::Chamfer] Chamfer059
  Base = -> Chamfer058
  Edges = 1 edges r=1.2: [Edge13]
FEATURE [Sketcher::SketchObject] Sketch425
  ExternalGeometry = -> [Chamfer059]
  Placement = pos=(0,0,5.95) rot=(0,0,1;0rad)
  Support = -> Chamfer059 [Face5]
  sketch-geometry (4):
    g0: LineSegment StartX=-3 StartY=0 StartZ=0 EndX=3 EndY=0 EndZ=0
    g1: LineSegment StartX=3 StartY=0 StartZ=0 EndX=3 EndY=-3.1 EndZ=0
    g2: LineSegment StartX=3 StartY=-3.1 StartZ=0 EndX=-3 EndY=-3.1 EndZ=0
    g3: LineSegment StartX=-3 StartY=-3.1 StartZ=0 EndX=-3 EndY=0 EndZ=0
  constraints (12):
    c: Coincident(g0,g1)
    c: Coincident(g1,g2)
    c: Coincident(g2,g3)
    c: Coincident(g3,g0)
    c: Horizontal(g0)
    c: Horizontal(g2)
    c: Vertical(g1)
    c: Vertical(g3)
    c: PointOnObject(g0,g-1)
    c: DistanceX(g-3,g0) = 0.15
    c: Symmetric(g0,g0,g-2)
    c: DistanceY(g0,g1) = -3.1
FEATURE [Part::Extrusion] Extrude494
  Base = -> Sketch425
  Dir = (0,0,6.3)
  Solid = true
FEATURE [Sketcher::SketchObject] Sketch426
  ExternalGeometry = -> [Extrude494]
  Placement = pos=(0,-3.1,0) rot=(1,0,0;1.5708rad)
  Support = -> Extrude494 [Face3]
  sketch-geometry (1):
    g0: Circle CenterX=0 CenterY=9.5 CenterZ=0 NormalX=0 NormalY=0 NormalZ=1 Radius=1.65
  constraints (3):
    c: PointOnObject(g0,g-2)
    c: Radius(g0) = 1.65
    c: DistanceY(g0,g-3) = -3.55
FEATURE [Part::Extrusion] Extrude495
  Base = -> Sketch426
  Dir = (0,6,0)
  Solid = true
FEATURE [Part::Cut] Cut188
  Base = -> Extrude494
  Tool = -> Extrude495
FEATURE [Part::Fillet] Fillet042
  Base = -> Cut188
  Edges = 2 edges r=1.35: [Edge8,Edge11]
FEATURE [Part::MultiFuse] Fusion107
  Shapes = -> [Chamfer059]
FEATURE [Sketcher::SketchObject] Sketch427
  Placement = pos=(0,0,0) rot=(0,0.707107,0.707107;3.14159rad)
  Support = -> Fusion107 [Face7]
  sketch-geometry (4):
    g0: Circle CenterX=-1.27 CenterY=3.8 CenterZ=0 NormalX=0 NormalY=0 NormalZ=1 Radius=0.2
    g1: Circle CenterX=1.27 CenterY=3.8 CenterZ=0 NormalX=0 NormalY=0 NormalZ=1 Radius=0.2
    g2: Circle CenterX=-1.27 CenterY=-3.8 CenterZ=0 NormalX=0 NormalY=0 NormalZ=1 Radius=0.2
    g3: Circle CenterX=1.27 CenterY=-3.8 CenterZ=0 NormalX=0 NormalY=0 NormalZ=1 Radius=0.2
  constraints (9):
    c: Radius(g0) = 0.2
    c: Equal(g0,g1)
    c: Equal(g0,g3)
    c: Equal(g0,g2)
    c: Symmetric(g0,g1,g-2)
    c: Symmetric(g2,g3,g-2)
    c: Symmetric(g0,g2,g-1)
    c: DistanceX(g0,g1) = 2.54
    c: DistanceY(g1,g3) = -7.6
FEATURE [Part::Extrusion] Extrude496
  Base = -> Sketch427
  Dir = (0,7.8,0)
  Solid = true
FEATURE [Part::MultiFuse] Fusion108  label="Capteur_optique_019"
  Placement = pos=(-2574,-46,-20.7) rot=(0,0,1;0rad)
  Shapes = -> [Fusion107,Fillet042,Extrude496]
FEATURE [Sketcher::SketchObject] Sketch428
  Placement = pos=(0,0,0) rot=(1,0,0;1.5708rad)
  sketch-geometry (1):
    g0: Circle CenterX=0 CenterY=0 CenterZ=0 NormalX=0 NormalY=0 NormalZ=1 Radius=4
  constraints (2):
    c: Coincident(g0,g-1)
    c: Radius(g0) = 4
FEATURE [Part::Extrusion] Extrude497
  Base = -> Sketch428
  Dir = (0,50,0)
  Solid = true
FEATURE [Sketcher::SketchObject] Sketch429
  Placement = pos=(0,0,0) rot=(0.57735,0.57735,0.57735;2.0944rad)
  sketch-geometry (1):
    g0: Circle CenterX=6 CenterY=0 CenterZ=0 NormalX=0 NormalY=0 NormalZ=1 Radius=2
  constraints (3):
    c: DistanceX(g-1,g0) = 6
    c: Radius(g0) = 2
    c: PointOnObject(g0,g-1)
FEATURE [Part::Extrusion] Extrude498
  Base = -> Sketch429
  Dir = (4,0,0)
  Solid = true
FEATURE [Part::Extrusion] Extrude499
  Base = -> Sketch429
  Dir = (-4,0,0)
  Solid = true
FEATURE [Part::Cut] Cut189
  Base = -> Extrude497
  Tool = -> Extrude498
FEATURE [Part::Cut] Cut190  label="Axe_D8_019"
  Base = -> Cut189
  Placement = pos=(-2574,-86,0) rot=(0,0,1;0rad)
  Tool = -> Extrude499
FEATURE [Sketcher::SketchObject] Sketch430
  Placement = pos=(0,0,0) rot=(1,0,0;1.5708rad)
  sketch-geometry (1):
    g0: Circle CenterX=0 CenterY=0 CenterZ=0 NormalX=0 NormalY=0 NormalZ=1 Radius=2
  constraints (2):
    c: Coincident(g0,g-1)
    c: Radius(g0) = 2
FEATURE [Part::Extrusion] Extrude500  label="Axe_D4_019"
  Base = -> Sketch430
  Dir = (0,103.6,0)
  Placement = pos=(-2522.2,-80,0) rot=(0,0,1;1.5708rad)
  Solid = true
FEATURE [Sketcher::SketchObject] Sketch431
  Placement = pos=(0,0,0) rot=(1,0,0;1.5708rad)
  sketch-geometry (8):
    g0: LineSegment StartX=-50 StartY=0 StartZ=0 EndX=50 EndY=0 EndZ=0
    g1: LineSegment StartX=50 StartY=0 StartZ=0 EndX=50 EndY=-2 EndZ=0
    g2: LineSegment StartX=50 StartY=-2 StartZ=0 EndX=47 EndY=-2 EndZ=0
    g3: LineSegment StartX=47 StartY=-2 StartZ=0 EndX=44 EndY=-16 EndZ=0
    g4: LineSegment StartX=44 StartY=-16 StartZ=0 EndX=-44 EndY=-16 EndZ=0
    g5: LineSegment StartX=-44 StartY=-16 StartZ=0 EndX=-47 EndY=-2 EndZ=0
    g6: LineSegment StartX=-47 StartY=-2 StartZ=0 EndX=-50 EndY=-2 EndZ=0
    g7: LineSegment StartX=-50 StartY=-2 StartZ=0 EndX=-50 EndY=0 EndZ=0
  constraints (24):
    c: PointOnObject(g0,g-1)
    c: Horizontal(g0)
    c: Coincident(g0,g1)
    c: Vertical(g1)
    c: Coincident(g1,g2)
    c: Horizontal(g2)
    c: Coincident(g2,g3)
    c: Coincident(g3,g4)
    c: Horizontal(g4)
    c: Coincident(g4,g5)
    c: Coincident(g5,g6)
    c: Horizontal(g6)
    c: Coincident(g6,g7)
    c: Coincident(g7,g0)
    c: Vertical(g7)
    c: DistanceY(g0,g6) = -2
    c: DistanceX(g6,g5) = 3
    c: DistanceX(g0,g0) = 100
    c: Symmetric(g0,g0,g-2)
    c: Symmetric(g6,g1,g-2)
    c: Symmetric(g5,g2,g-2)
    c: Symmetric(g4,g3,g-2)
    c: DistanceX(g4,g3) = 88
    c: DistanceY(g0,g4) = -16
FEATURE [Part::Extrusion] Extrude501  label="Plaque_alveolaire_019"
  Base = -> Sketch431
  Dir = (0,2000,0)
  Placement = pos=(-2574,-62,22) rot=(0,0,1;3.14159rad)
  Solid = true
FEATURE [App::DocumentObjectGroup] Groupe024  label="Assemblage_miroir X=-1144_002"
  Group = -> [Cut184,Fusion105,Extrude486,Part__Feature021,Extrude487,Fillet041,Fusion108,Cut190,Extrude500,Extrude501]
FEATURE [Sketcher::SketchObject] Sketch432
  Placement = pos=(0,0,0) rot=(1,0,0;1.5708rad)
  sketch-geometry (8):
    g0: LineSegment StartX=-21.15 StartY=16.15 StartZ=0 EndX=-16.15 EndY=21.15 EndZ=0
    g1: LineSegment StartX=-16.15 StartY=21.15 StartZ=0 EndX=16.15 EndY=21.15 EndZ=0
    g2: LineSegment StartX=16.15 StartY=21.15 StartZ=0 EndX=21.15 EndY=16.15 EndZ=0
    g3: LineSegment StartX=21.15 StartY=16.15 StartZ=0 EndX=21.15 EndY=-16.15 EndZ=0
    g4: LineSegment StartX=21.15 StartY=-16.15 StartZ=0 EndX=16.15 EndY=-21.15 EndZ=0
    g5: LineSegment StartX=16.15 StartY=-21.15 StartZ=0 EndX=-16.15 EndY=-21.15 EndZ=0
    g6: LineSegment StartX=-16.15 StartY=-21.15 StartZ=0 EndX=-21.15 EndY=-16.15 EndZ=0
    g7: LineSegment StartX=-21.15 StartY=-16.15 StartZ=0 EndX=-21.15 EndY=16.15 EndZ=0
  constraints (21):
    c: Coincident(g0,g1)
    c: Horizontal(g1)
    c: Coincident(g1,g2)
    c: Coincident(g2,g3)
    c: Vertical(g3)
    c: Coincident(g3,g4)
    c: Coincident(g4,g5)
    c: Horizontal(g5)
    c: Coincident(g5,g6)
    c: Coincident(g6,g7)
    c: Coincident(g7,g0)
    c: Angle(g7,g0) = 2.35619
    c: Distance(g0,g7) = 5
    c: Distance(g2,g7) = 42.3
    c: Distance(g5,g1) = 42.3
    c: Symmetric(g6,g3,g-2)
    c: Symmetric(g5,g4,g-2)
    c: Symmetric(g0,g2,g-2)
    c: Symmetric(g0,g1,g-2)
    c: Symmetric(g0,g6,g-1)
    c: Symmetric(g0,g5,g-1)
FEATURE [Part::Extrusion] Extrude502
  Base = -> Sketch432
  Dir = (0,48,0)
  Solid = true
FEATURE [Sketcher::SketchObject] Sketch433
  Placement = pos=(0,0,0) rot=(1,0,0;1.5708rad)
  Support = -> Extrude502 [Face9]
  sketch-geometry (1):
    g0: Circle CenterX=0 CenterY=0 CenterZ=0 NormalX=0 NormalY=0 NormalZ=1 Radius=11
  constraints (2):
    c: Coincident(g0,g-1)
    c: Radius(g0) = 11
FEATURE [Part::Extrusion] Extrude503
  Base = -> Sketch433
  Dir = (0,-2,0)
  Solid = true
FEATURE [Sketcher::SketchObject] Sketch434
  Placement = pos=(0,-2,0) rot=(1,0,0;1.5708rad)
  Support = -> Extrude503 [Face3]
  sketch-geometry (1):
    g0: Circle CenterX=0 CenterY=0 CenterZ=0 NormalX=0 NormalY=0 NormalZ=1 Radius=2.5
  constraints (2):
    c: Coincident(g0,g-1)
    c: Radius(g0) = 2.5
FEATURE [Part::Extrusion] Extrude504
  Base = -> Sketch434
  Dir = (0,-22,0)
  Solid = true
FEATURE [Part::Chamfer] Chamfer060
  Base = -> Extrude504
  Edges = 1 edges r=0.8: [Edge3]
FEATURE [Sketcher::SketchObject] Sketch435
  Placement = pos=(0,0,0) rot=(1,0,0;1.5708rad)
  Support = -> Extrude502 [Face9]
  sketch-geometry (4):
    g0: Circle CenterX=-15.5 CenterY=15.5 CenterZ=0 NormalX=0 NormalY=0 NormalZ=1 Radius=2
    g1: Circle CenterX=15.5 CenterY=15.5 CenterZ=0 NormalX=0 NormalY=0 NormalZ=1 Radius=2
    g2: Circle CenterX=-15.5 CenterY=-15.5 CenterZ=0 NormalX=0 NormalY=0 NormalZ=1 Radius=2
    g3: Circle CenterX=15.5 CenterY=-15.5 CenterZ=0 NormalX=0 NormalY=0 NormalZ=1 Radius=2
  constraints (9):
    c: Distance(g0,g1) = 31
    c: Distance(g0,g2) = 31
    c: Symmetric(g0,g2,g-1)
    c: Symmetric(g0,g1,g-2)
    c: Symmetric(g2,g3,g-2)
    c: Radius(g0) = 2
    c: Equal(g0,g1)
    c: Equal(g0,g2)
    c: Equal(g0,g3)
FEATURE [Part::Extrusion] Extrude505
  Base = -> Sketch435
  Dir = (0,4.5,0)
  Solid = true
FEATURE [Part::Cut] Cut191
  Base = -> Extrude502
  Tool = -> Extrude505
FEATURE [Sketcher::SketchObject] Sketch436
  Placement = pos=(0,0,0) rot=(1,0,0;1.5708rad)
  sketch-geometry (1):
    g0: Circle CenterX=0 CenterY=0 CenterZ=0 NormalX=0 NormalY=0 NormalZ=1 Radius=9
  constraints (2):
    c: Coincident(g0,g-1)
    c: Radius(g0) = 9
FEATURE [Part::Extrusion] Extrude506
  Base = -> Sketch436
  Dir = (0,25,0)
  Solid = true
FEATURE [Sketcher::SketchObject] Sketch437
  Placement = pos=(0,0,0) rot=(1,0,0;1.5708rad)
  sketch-geometry (1):
    g0: Circle CenterX=0 CenterY=0 CenterZ=0 NormalX=0 NormalY=0 NormalZ=1 Radius=2.5
  constraints (2):
    c: Coincident(g0,g-1)
    c: Radius(g0) = 2.5
FEATURE [Part::Extrusion] Extrude507
  Base = -> Sketch437
  Dir = (0,10,0)
  Solid = true
FEATURE [Part::Cut] Cut192
  Base = -> Extrude506
  Tool = -> Extrude507
FEATURE [Sketcher::SketchObject] Sketch438
  Placement = pos=(0,25,0) rot=(0,0.707107,0.707107;3.14159rad)
  Support = -> Cut192 [Face3]
  sketch-geometry (1):
    g0: Circle CenterX=0 CenterY=0 CenterZ=0 NormalX=0 NormalY=0 NormalZ=1 Radius=4
  constraints (2):
    c: Coincident(g0,g-1)
    c: Radius(g0) = 4
FEATURE [Part::Extrusion] Extrude508
  Base = -> Sketch438
  Dir = (0,-10,0)
  Solid = true
FEATURE [Part::Cut] Cut193  label="Accouplement_020"
  Base = -> Cut192
  Placement = pos=(-2717,-12,0) rot=(1,0,0;3.14159rad)
  Tool = -> Extrude508
FEATURE [Part::Fuse] Fusion109
  Base = -> Extrude503
  Tool = -> Cut191
FEATURE [Part::Fuse] Fusion110  label="Moteur_020"
  Base = -> Chamfer060
  Placement = pos=(-2717,0,0) rot=(0,0,1;0rad)
  Tool = -> Fusion109
FEATURE [Sketcher::SketchObject] Sketch439
  Placement = pos=(0,0,0) rot=(1,0,0;1.5708rad)
  sketch-geometry (4):
    g0: LineSegment StartX=-50 StartY=0 StartZ=0 EndX=-47 EndY=0 EndZ=0
    g1: LineSegment StartX=47 StartY=0 StartZ=0 EndX=50 EndY=0 EndZ=0
    g2: ArcOfCircle CenterX=0 CenterY=0 CenterZ=0 NormalX=0 NormalY=0 NormalZ=1 Radius=47 StartAngle=3.14159 EndAngle=6.28319
    g3: ArcOfCircle CenterX=0 CenterY=0 CenterZ=0 NormalX=0 NormalY=0 NormalZ=1 Radius=50 StartAngle=3.14159 EndAngle=6.28319
  constraints (13):
    c: Horizontal(g0)
    c: PointOnObject(g1,g-1)
    c: Horizontal(g1)
    c: Coincident(g2,g-1)
    c: PointOnObject(g2,g-1)
    c: Coincident(g3,g-1)
    c: Coincident(g3,g1)
    c: PointOnObject(g3,g-1)
    c: Coincident(g0,g3)
    c: Coincident(g0,g2)
    c: Distance(g0,g1) = 100
    c: Distance(g0,g0) = 3
    c: Coincident(g1,g2)
FEATURE [Part::Extrusion] Extrude509  label="Demi_tube_sous_miroir_020"
  Base = -> Sketch439
  Dir = (0,2000,0)
  Placement = pos=(-2717,-62,20) rot=(0,0,1;3.14159rad)
  Solid = true
FEATURE [Part::Feature] Part__Feature022  label="Coussinet_autolub_C2-151-8-128_020"
  Placement = pos=(-2717,-46,0) rot=(0,0,1;1.5708rad)
  shape: bbox 16 x 8 x 16 mm, 12 faces (baked)
FEATURE [Sketcher::SketchObject] Sketch440
  Placement = pos=(0,0,0) rot=(1,0,0;1.5708rad)
  sketch-geometry (21):
    g0: Circle CenterX=0 CenterY=0 CenterZ=0 NormalX=0 NormalY=0 NormalZ=1 Radius=6
    g1: LineSegment StartX=-20.5 StartY=15 StartZ=0 EndX=20.5 EndY=15 EndZ=0
    g2: ArcOfCircle CenterX=20.5 CenterY=13 CenterZ=0 NormalX=0 NormalY=0 NormalZ=1 Radius=2 StartAngle=6.28319 EndAngle=7.85398
    g3: LineSegment StartX=22.5 StartY=13 StartZ=0 EndX=22.5 EndY=-73 EndZ=0
    g4: LineSegment StartX=-22.5 StartY=13 StartZ=0 EndX=-22.5 EndY=-73 EndZ=0
    g5: ArcOfCircle CenterX=-20.5 CenterY=13 CenterZ=0 NormalX=0 NormalY=0 NormalZ=1 Radius=2 StartAngle=1.5708 EndAngle=3.14159
    g6: ArcOfCircle CenterX=-20.5 CenterY=-73 CenterZ=0 NormalX=0 NormalY=0 NormalZ=1 Radius=2 StartAngle=3.14159 EndAngle=4.71239
    g7: ArcOfCircle CenterX=20.5 CenterY=-73 CenterZ=0 NormalX=0 NormalY=0 NormalZ=1 Radius=2 StartAngle=4.71239 EndAngle=6.28319
    g8: LineSegment StartX=-20.5 StartY=-75 StartZ=0 EndX=20.5 EndY=-75 EndZ=0
    g9: ArcOfCircle CenterX=0 CenterY=-16.7 CenterZ=0 NormalX=0 NormalY=0 NormalZ=1 Radius=1.5 StartAngle=0 EndAngle=3.14159
    g10: ArcOfCircle CenterX=0 CenterY=-24.3 CenterZ=0 NormalX=0 NormalY=0 NormalZ=1 Radius=1.5 StartAngle=3.14159 EndAngle=6.28319
    g11: LineSegment StartX=-1.5 StartY=-16.7 StartZ=0 EndX=-1.5 EndY=-24.3 EndZ=0
    g12: LineSegment StartX=1.5 StartY=-16.7 StartZ=0 EndX=1.5 EndY=-24.3 EndZ=0
    g13: Circle CenterX=-12.5 CenterY=-45 CenterZ=0 NormalX=0 NormalY=0 NormalZ=1 Radius=3.5
    g14: Circle CenterX=12.5 CenterY=-45 CenterZ=0 NormalX=0 NormalY=0 NormalZ=1 Radius=3.5
    g15: Circle CenterX=-12.5 CenterY=-65 CenterZ=0 NormalX=0 NormalY=0 NormalZ=1 Radius=3.5
    g16: Circle CenterX=12.5 CenterY=-65 CenterZ=0 NormalX=0 NormalY=0 NormalZ=1 Radius=3.5
    g17: LineSegment [constr] StartX=-12.5 StartY=-45 StartZ=0 EndX=12.5 EndY=-45 EndZ=0
    g18: LineSegment [constr] StartX=-12.5 StartY=-45 StartZ=0 EndX=-12.5 EndY=-65 EndZ=0
    g19: LineSegment [constr] StartX=-12.5 StartY=-65 StartZ=0 EndX=12.5 EndY=-65 EndZ=0
    g20: LineSegment [constr] StartX=12.5 StartY=-45 StartZ=0 EndX=12.5 EndY=-65 EndZ=0
  constraints (59):
    c: Coincident(g0,g-1)
    c: Radius(g0) = 6
    c: Horizontal(g1)
    c: Coincident(g2,g1)
    c: Coincident(g3,g2)
    c: Vertical(g3)
    c: Vertical(g4)
    c: Coincident(g5,g1)
    c: Coincident(g5,g4)
    c: Coincident(g7,g3)
    c: Coincident(g8,g6)
    c: Coincident(g8,g7)
    c: Tangent(g8,g7)
    c: Tangent(g5,g4)
    c: Tangent(g5,g1)
    c: Tangent(g1,g2)
    c: Tangent(g2,g3)
    c: Coincident(g4,g6)
    c: Tangent(g6,g4)
    c: Tangent(g6,g8)
    c: Horizontal(g8)
    c: Tangent(g7,g3)
    c: Distance(g4,g2) = 45
    c: Symmetric(g4,g2,g-2)
    c: Distance(g1,g6) = 90
    c: DistanceY(g-1,g1) = 15
    c: Tangent(g9,g12) = 1.5708
    c: Tangent(g9,g11) = -1.5708
    c: Tangent(g11,g10) = -1.5708
    c: Tangent(g12,g10) = 1.5708
    c: Vertical(g11)
    c: Equal(g9,g10)
    c: PointOnObject(g9,g-2)
    c: Distance(g-1,g9) = 16.7
    c: Distance(g9,g10) = 7.6
    c: Radius(g9) = 1.5
    c: Radius(g13) = 3.5
    c: Equal(g13,g14)
    c: Equal(g13,g16)
    c: Equal(g13,g15)
    c: Radius(g5) = 2
    c: Equal(g5,g7)
    c: Equal(g5,g6)
    c: DistanceY(g-1,g13) = -45
    c: Coincident(g17,g13)
    c: Coincident(g17,g14)
    c: Horizontal(g17)
    c: Coincident(g18,g13)
    c: Coincident(g18,g15)
    c: Coincident(g19,g15)
    c: Coincident(g19,g16)
    c: Horizontal(g19)
    c: Coincident(g20,g14)
    c: Coincident(g20,g16)
    c: Vertical(g18)
    c: Vertical(g20)
    c: Distance(g13,g15) = 20
    c: Distance(g13,g14) = 25
    c: Symmetric(g13,g14,g-2)
FEATURE [Part::Extrusion] Extrude510  label="Plaque_support_020"
  Base = -> Sketch440
  Dir = (0,6,0)
  Placement = pos=(-2717,-46,0) rot=(0,0,1;0rad)
  Solid = true
FEATURE [Sketcher::SketchObject] Sketch441
  Placement = pos=(0,0,0) rot=(0.57735,0.57735,0.57735;2.0944rad)
  sketch-geometry (8):
    g0: LineSegment StartX=0 StartY=33 StartZ=0 EndX=-2 EndY=33 EndZ=0
    g1: LineSegment StartX=-2 StartY=33 StartZ=0 EndX=-2 EndY=-24 EndZ=0
    g2: ArcOfCircle CenterX=-4 CenterY=-24 CenterZ=0 NormalX=0 NormalY=0 NormalZ=1 Radius=2 StartAngle=4.71239 EndAngle=6.28319
    g3: LineSegment StartX=-4 StartY=-26 StartZ=0 EndX=-38 EndY=-26 EndZ=0
    g4: LineSegment StartX=-38 StartY=-26 StartZ=0 EndX=-38 EndY=-28 EndZ=0
    g5: LineSegment StartX=-38 StartY=-28 StartZ=0 EndX=-4 EndY=-28 EndZ=0
    g6: ArcOfCircle CenterX=-4 CenterY=-24 CenterZ=0 NormalX=0 NormalY=0 NormalZ=1 Radius=4 StartAngle=4.71239 EndAngle=6.28319
    g7: LineSegment StartX=0 StartY=-24 StartZ=0 EndX=0 EndY=33 EndZ=0
  constraints (22):
    c: PointOnObject(g0,g-2)
    c: Horizontal(g0)
    c: Coincident(g0,g1)
    c: Vertical(g1)
    c: Tangent(g1,g2) = 1.5708
    c: Tangent(g2,g3) = 1.5708
    c: Coincident(g3,g4)
    c: Vertical(g4)
    c: Coincident(g4,g5)
    c: Horizontal(g5)
    c: Tangent(g5,g6) = -1.5708
    c: PointOnObject(g6,g-2)
    c: Tangent(g6,g7) = -1.5708
    c: Coincident(g7,g0)
    c: Horizontal(g3)
    c: DistanceX(g0,g0) = 2
    c: Radius(g2) = 2
    c: Radius(g6) = 4
    c: DistanceY(g3,g4) = -2
    c: Distance(g-1,g0) = 33
    c: DistanceY(g-1,g5) = -28
    c: DistanceX(g6,g4) = -38
FEATURE [Part::Extrusion] Extrude511
  Base = -> Sketch441
  Dir = (-32.5,0,0)
  Solid = true
FEATURE [Part::Extrusion] Extrude512
  Base = -> Sketch441
  Dir = (32.5,0,0)
  Solid = true
FEATURE [Part::MultiFuse] Fusion111
  Shapes = -> [Extrude511,Extrude512]
FEATURE [Sketcher::SketchObject] Sketch442
  Placement = pos=(0,-2,0) rot=(1,0,0;1.5708rad)
  Support = -> Fusion111 [Face3]
  sketch-geometry (9):
    g0: ArcOfCircle CenterX=0 CenterY=0 CenterZ=0 NormalX=0 NormalY=0 NormalZ=1 Radius=32.5 StartAngle=0 EndAngle=3.14159
    g1: LineSegment StartX=-32.5 StartY=0 StartZ=0 EndX=-32.5 EndY=34 EndZ=0
    g2: LineSegment StartX=-32.5 StartY=34 StartZ=0 EndX=32.5 EndY=34 EndZ=0
    g3: LineSegment StartX=32.5 StartY=34 StartZ=0 EndX=32.5 EndY=0 EndZ=0
    g4: Circle CenterX=0 CenterY=0 CenterZ=0 NormalX=0 NormalY=0 NormalZ=1 Radius=11
    g5: Circle CenterX=-15.5 CenterY=15.5 CenterZ=0 NormalX=0 NormalY=0 NormalZ=1 Radius=2
    g6: Circle CenterX=15.5 CenterY=15.5 CenterZ=0 NormalX=0 NormalY=0 NormalZ=1 Radius=2
    g7: Circle CenterX=-15.5 CenterY=-15.5 CenterZ=0 NormalX=0 NormalY=0 NormalZ=1 Radius=2
    g8: Circle CenterX=15.5 CenterY=-15.5 CenterZ=0 NormalX=0 NormalY=0 NormalZ=1 Radius=2
  constraints (23):
    c: Coincident(g0,g-1)
    c: PointOnObject(g0,g-1)
    c: PointOnObject(g0,g-1)
    c: Coincident(g1,g0)
    c: Vertical(g1)
    c: Coincident(g1,g2)
    c: Horizontal(g2)
    c: Coincident(g2,g3)
    c: Coincident(g3,g0)
    c: Vertical(g3)
    c: DistanceY(g1,g0) = -34
    c: Coincident(g4,g-1)
    c: Radius(g4) = 11
    c: DistanceX(g1,g2) = 65
    c: Radius(g5) = 2
    c: Equal(g5,g6)
    c: Equal(g5,g8)
    c: Equal(g5,g7)
    c: Symmetric(g5,g6,g-2)
    c: Symmetric(g5,g7,g-1)
    c: Symmetric(g7,g8,g-2)
    c: DistanceX(g5,g6) = 31
    c: DistanceY(g5,g7) = -31
FEATURE [Part::Extrusion] Extrude513
  Base = -> Sketch442
  Dir = (0,2,0)
  Solid = true
FEATURE [Part::Cut] Cut194
  Base = -> Fusion111
  Tool = -> Extrude513
FEATURE [Sketcher::SketchObject] Sketch443
  ExternalGeometry = -> [Cut194]
  Placement = pos=(0,0,-26) rot=(0,0,1;0rad)
  Support = -> Cut194 [Face5]
  sketch-geometry (5):
    g0: Circle CenterX=-25 CenterY=-12 CenterZ=0 NormalX=0 NormalY=0 NormalZ=1 Radius=3.5
    g1: Circle CenterX=-25 CenterY=-30 CenterZ=0 NormalX=0 NormalY=0 NormalZ=1 Radius=3.5
    g2: Circle CenterX=25 CenterY=-12 CenterZ=0 NormalX=0 NormalY=0 NormalZ=1 Radius=3.5
    g3: Circle CenterX=25 CenterY=-30 CenterZ=0 NormalX=0 NormalY=0 NormalZ=1 Radius=3.5
    g4: LineSegment [constr] StartX=-25 StartY=-12 StartZ=0 EndX=-25 EndY=-30 EndZ=0
  constraints (12):
    c: Radius(g0) = 3.5
    c: Equal(g0,g2)
    c: Equal(g0,g3)
    c: Equal(g0,g1)
    c: Symmetric(g0,g2,g-2)
    c: Symmetric(g1,g3,g-2)
    c: Coincident(g4,g0)
    c: Coincident(g4,g1)
    c: Vertical(g4)
    c: DistanceY(g0,g1) = -18
    c: DistanceY(g-3,g1) = 8
    c: DistanceX(g0,g2) = 50
FEATURE [Part::Extrusion] Extrude514
  Base = -> Sketch443
  Dir = (0,0,-2)
  Solid = true
FEATURE [Part::Cut] Cut195
  Base = -> Cut194
  Tool = -> Extrude514
FEATURE [Part::Fillet] Fillet043  label="Plaque_moteur_020"
  Base = -> Cut195
  Edges = 2 edges r=4: [Edge5,Edge59]
  Placement = pos=(-2717,0,0) rot=(0,0,1;0rad)
FEATURE [Sketcher::SketchObject] Sketch444
  Placement = pos=(0,0,0) rot=(1,0,0;1.5708rad)
  sketch-geometry (4):
    g0: LineSegment StartX=-3.15 StartY=5.95 StartZ=0 EndX=3.15 EndY=5.95 EndZ=0
    g1: LineSegment StartX=3.15 StartY=5.95 StartZ=0 EndX=3.15 EndY=-5.95 EndZ=0
    g2: LineSegment StartX=3.15 StartY=-5.95 StartZ=0 EndX=-3.15 EndY=-5.95 EndZ=0
    g3: LineSegment StartX=-3.15 StartY=-5.95 StartZ=0 EndX=-3.15 EndY=5.95 EndZ=0
  constraints (12):
    c: Coincident(g0,g1)
    c: Coincident(g1,g2)
    c: Coincident(g2,g3)
    c: Coincident(g3,g0)
    c: Horizontal(g0)
    c: Horizontal(g2)
    c: Vertical(g1)
    c: Vertical(g3)
    c: DistanceX(g0,g0) = 6.3
    c: DistanceY(g0,g2) = -11.9
    c: Symmetric(g0,g0,g-2)
    c: Symmetric(g0,g1,g-1)
FEATURE [Part::Extrusion] Extrude515
  Base = -> Sketch444
  Dir = (0,-10.8,0)
  Solid = true
FEATURE [Sketcher::SketchObject] Sketch445
  ExternalGeometry = -> [Extrude515]
  Placement = pos=(0,-10.8,0) rot=(1,0,0;1.5708rad)
  Support = -> Extrude515 [Face6]
  sketch-geometry (4):
    g0: LineSegment StartX=-3.15 StartY=1.55 StartZ=0 EndX=3.15 EndY=1.55 EndZ=0
    g1: LineSegment StartX=3.15 StartY=1.55 StartZ=0 EndX=3.15 EndY=-1.55 EndZ=0
    g2: LineSegment StartX=3.15 StartY=-1.55 StartZ=0 EndX=-3.15 EndY=-1.55 EndZ=0
    g3: LineSegment StartX=-3.15 StartY=-1.55 StartZ=0 EndX=-3.15 EndY=1.55 EndZ=0
  constraints (12):
    c: Coincident(g0,g1)
    c: Coincident(g1,g2)
    c: Coincident(g2,g3)
    c: Coincident(g3,g0)
    c: Horizontal(g0)
    c: Horizontal(g2)
    c: Vertical(g1)
    c: Vertical(g3)
    c: PointOnObject(g0,g-4)
    c: PointOnObject(g0,g-3)
    c: DistanceY(g0,g2) = -3.1
    c: Symmetric(g0,g1,g-1)
FEATURE [Part::Extrusion] Extrude516
  Base = -> Sketch445
  Dir = (0,7.7,0)
  Solid = true
FEATURE [Part::Cut] Cut196
  Base = -> Extrude515
  Tool = -> Extrude516
FEATURE [Part::Chamfer] Chamfer061
  Base = -> Cut196
  Edges = 4 edges r=0.5: [Edge7,Edge9,Edge15,Edge17]
FEATURE [Part::Chamfer] Chamfer062
  Base = -> Chamfer061
  Edges = 1 edges r=1.2: [Edge13]
FEATURE [Sketcher::SketchObject] Sketch446
  ExternalGeometry = -> [Chamfer062]
  Placement = pos=(0,0,5.95) rot=(0,0,1;0rad)
  Support = -> Chamfer062 [Face5]
  sketch-geometry (4):
    g0: LineSegment StartX=-3 StartY=0 StartZ=0 EndX=3 EndY=0 EndZ=0
    g1: LineSegment StartX=3 StartY=0 StartZ=0 EndX=3 EndY=-3.1 EndZ=0
    g2: LineSegment StartX=3 StartY=-3.1 StartZ=0 EndX=-3 EndY=-3.1 EndZ=0
    g3: LineSegment StartX=-3 StartY=-3.1 StartZ=0 EndX=-3 EndY=0 EndZ=0
  constraints (12):
    c: Coincident(g0,g1)
    c: Coincident(g1,g2)
    c: Coincident(g2,g3)
    c: Coincident(g3,g0)
    c: Horizontal(g0)
    c: Horizontal(g2)
    c: Vertical(g1)
    c: Vertical(g3)
    c: PointOnObject(g0,g-1)
    c: DistanceX(g-3,g0) = 0.15
    c: Symmetric(g0,g0,g-2)
    c: DistanceY(g0,g1) = -3.1
FEATURE [Part::Extrusion] Extrude517
  Base = -> Sketch446
  Dir = (0,0,6.3)
  Solid = true
FEATURE [Sketcher::SketchObject] Sketch447
  ExternalGeometry = -> [Extrude517]
  Placement = pos=(0,-3.1,0) rot=(1,0,0;1.5708rad)
  Support = -> Extrude517 [Face3]
  sketch-geometry (1):
    g0: Circle CenterX=0 CenterY=9.5 CenterZ=0 NormalX=0 NormalY=0 NormalZ=1 Radius=1.65
  constraints (3):
    c: PointOnObject(g0,g-2)
    c: Radius(g0) = 1.65
    c: DistanceY(g0,g-3) = -3.55
FEATURE [Part::Extrusion] Extrude518
  Base = -> Sketch447
  Dir = (0,6,0)
  Solid = true
FEATURE [Part::Cut] Cut197
  Base = -> Extrude517
  Tool = -> Extrude518
FEATURE [Part::Fillet] Fillet044
  Base = -> Cut197
  Edges = 2 edges r=1.35: [Edge8,Edge11]
FEATURE [Part::MultiFuse] Fusion112
  Shapes = -> [Chamfer062]
FEATURE [Sketcher::SketchObject] Sketch448
  Placement = pos=(0,0,0) rot=(0,0.707107,0.707107;3.14159rad)
  Support = -> Fusion112 [Face7]
  sketch-geometry (4):
    g0: Circle CenterX=-1.27 CenterY=3.8 CenterZ=0 NormalX=0 NormalY=0 NormalZ=1 Radius=0.2
    g1: Circle CenterX=1.27 CenterY=3.8 CenterZ=0 NormalX=0 NormalY=0 NormalZ=1 Radius=0.2
    g2: Circle CenterX=-1.27 CenterY=-3.8 CenterZ=0 NormalX=0 NormalY=0 NormalZ=1 Radius=0.2
    g3: Circle CenterX=1.27 CenterY=-3.8 CenterZ=0 NormalX=0 NormalY=0 NormalZ=1 Radius=0.2
  constraints (9):
    c: Radius(g0) = 0.2
    c: Equal(g0,g1)
    c: Equal(g0,g3)
    c: Equal(g0,g2)
    c: Symmetric(g0,g1,g-2)
    c: Symmetric(g2,g3,g-2)
    c: Symmetric(g0,g2,g-1)
    c: DistanceX(g0,g1) = 2.54
    c: DistanceY(g1,g3) = -7.6
FEATURE [Part::Extrusion] Extrude519
  Base = -> Sketch448
  Dir = (0,7.8,0)
  Solid = true
FEATURE [Part::MultiFuse] Fusion113  label="Capteur_optique_020"
  Placement = pos=(-2717,-46,-20.7) rot=(0,0,1;0rad)
  Shapes = -> [Fusion112,Fillet044,Extrude519]
FEATURE [Sketcher::SketchObject] Sketch449
  Placement = pos=(0,0,0) rot=(1,0,0;1.5708rad)
  sketch-geometry (1):
    g0: Circle CenterX=0 CenterY=0 CenterZ=0 NormalX=0 NormalY=0 NormalZ=1 Radius=4
  constraints (2):
    c: Coincident(g0,g-1)
    c: Radius(g0) = 4
FEATURE [Part::Extrusion] Extrude520
  Base = -> Sketch449
  Dir = (0,50,0)
  Solid = true
FEATURE [Sketcher::SketchObject] Sketch450
  Placement = pos=(0,0,0) rot=(0.57735,0.57735,0.57735;2.0944rad)
  sketch-geometry (1):
    g0: Circle CenterX=6 CenterY=0 CenterZ=0 NormalX=0 NormalY=0 NormalZ=1 Radius=2
  constraints (3):
    c: DistanceX(g-1,g0) = 6
    c: Radius(g0) = 2
    c: PointOnObject(g0,g-1)
FEATURE [Part::Extrusion] Extrude521
  Base = -> Sketch450
  Dir = (4,0,0)
  Solid = true
FEATURE [Part::Extrusion] Extrude522
  Base = -> Sketch450
  Dir = (-4,0,0)
  Solid = true
FEATURE [Part::Cut] Cut198
  Base = -> Extrude520
  Tool = -> Extrude521
FEATURE [Part::Cut] Cut199  label="Axe_D8_020"
  Base = -> Cut198
  Placement = pos=(-2717,-86,0) rot=(0,0,1;0rad)
  Tool = -> Extrude522
FEATURE [Sketcher::SketchObject] Sketch451
  Placement = pos=(0,0,0) rot=(1,0,0;1.5708rad)
  sketch-geometry (1):
    g0: Circle CenterX=0 CenterY=0 CenterZ=0 NormalX=0 NormalY=0 NormalZ=1 Radius=2
  constraints (2):
    c: Coincident(g0,g-1)
    c: Radius(g0) = 2
FEATURE [Part::Extrusion] Extrude523  label="Axe_D4_020"
  Base = -> Sketch451
  Dir = (0,103.6,0)
  Placement = pos=(-2665.2,-80,0) rot=(0,0,1;1.5708rad)
  Solid = true
FEATURE [Sketcher::SketchObject] Sketch452
  Placement = pos=(0,0,0) rot=(1,0,0;1.5708rad)
  sketch-geometry (8):
    g0: LineSegment StartX=-50 StartY=0 StartZ=0 EndX=50 EndY=0 EndZ=0
    g1: LineSegment StartX=50 StartY=0 StartZ=0 EndX=50 EndY=-2 EndZ=0
    g2: LineSegment StartX=50 StartY=-2 StartZ=0 EndX=47 EndY=-2 EndZ=0
    g3: LineSegment StartX=47 StartY=-2 StartZ=0 EndX=44 EndY=-16 EndZ=0
    g4: LineSegment StartX=44 StartY=-16 StartZ=0 EndX=-44 EndY=-16 EndZ=0
    g5: LineSegment StartX=-44 StartY=-16 StartZ=0 EndX=-47 EndY=-2 EndZ=0
    g6: LineSegment StartX=-47 StartY=-2 StartZ=0 EndX=-50 EndY=-2 EndZ=0
    g7: LineSegment StartX=-50 StartY=-2 StartZ=0 EndX=-50 EndY=0 EndZ=0
  constraints (24):
    c: PointOnObject(g0,g-1)
    c: Horizontal(g0)
    c: Coincident(g0,g1)
    c: Vertical(g1)
    c: Coincident(g1,g2)
    c: Horizontal(g2)
    c: Coincident(g2,g3)
    c: Coincident(g3,g4)
    c: Horizontal(g4)
    c: Coincident(g4,g5)
    c: Coincident(g5,g6)
    c: Horizontal(g6)
    c: Coincident(g6,g7)
    c: Coincident(g7,g0)
    c: Vertical(g7)
    c: DistanceY(g0,g6) = -2
    c: DistanceX(g6,g5) = 3
    c: DistanceX(g0,g0) = 100
    c: Symmetric(g0,g0,g-2)
    c: Symmetric(g6,g1,g-2)
    c: Symmetric(g5,g2,g-2)
    c: Symmetric(g4,g3,g-2)
    c: DistanceX(g4,g3) = 88
    c: DistanceY(g0,g4) = -16
FEATURE [Part::Extrusion] Extrude524  label="Plaque_alveolaire_020"
  Base = -> Sketch452
  Dir = (0,2000,0)
  Placement = pos=(-2717,-62,22) rot=(0,0,1;3.14159rad)
  Solid = true
FEATURE [App::DocumentObjectGroup] Groupe025  label="Assemblage_miroir X=-1287_002"
  Group = -> [Cut193,Fusion110,Extrude509,Part__Feature022,Extrude510,Fillet043,Fusion113,Cut199,Extrude523,Extrude524]
FEATURE [Sketcher::SketchObject] Sketch457
  Placement = pos=(0,0,0) rot=(1,0,0;1.5708rad)
  sketch-geometry (8):
    g0: LineSegment StartX=-20 StartY=25 StartZ=0 EndX=20 EndY=25 EndZ=0
    g1: LineSegment StartX=20 StartY=25 StartZ=0 EndX=20 EndY=-25 EndZ=0
    g2: LineSegment StartX=20 StartY=-25 StartZ=0 EndX=-20 EndY=-25 EndZ=0
    g3: LineSegment StartX=-20 StartY=-25 StartZ=0 EndX=-20 EndY=25 EndZ=0
    g4: LineSegment StartX=-18 StartY=23 StartZ=0 EndX=18 EndY=23 EndZ=0
    g5: LineSegment StartX=18 StartY=23 StartZ=0 EndX=18 EndY=-23 EndZ=0
    g6: LineSegment StartX=18 StartY=-23 StartZ=0 EndX=-18 EndY=-23 EndZ=0
    g7: LineSegment StartX=-18 StartY=-23 StartZ=0 EndX=-18 EndY=23 EndZ=0
  constraints (24):
    c: Coincident(g0,g1)
    c: Coincident(g1,g2)
    c: Coincident(g2,g3)
    c: Coincident(g3,g0)
    c: Horizontal(g0)
    c: Horizontal(g2)
    c: Vertical(g1)
    c: Vertical(g3)
    c: Distance(g0,g2) = 50
    c: DistanceX(g0,g0) = -40
    c: Symmetric(g0,g0,g-2)
    c: Symmetric(g0,g2,g-1)
    c: Coincident(g4,g5)
    c: Coincident(g5,g6)
    c: Coincident(g6,g7)
    c: Coincident(g7,g4)
    c: Horizontal(g4)
    c: Horizontal(g6)
    c: Vertical(g5)
    c: Vertical(g7)
    c: DistanceY(g0,g4) = -2
    c: DistanceX(g4,g0) = -2
    c: DistanceX(g5,g1) = 2
    c: DistanceY(g5,g1) = -2
FEATURE [Part::Extrusion] Extrude528
  Base = -> Sketch457
  Dir = (0,1430,0)
  Placement = pos=(71.5,-20,-53) rot=(0,0,1;1.5708rad)
  Solid = true
FEATURE [Sketcher::SketchObject] Sketch458
  ExternalGeometry = -> [Extrude528]
  Placement = pos=(71.5,-40,-53) rot=(1,0,0;1.5708rad)
  Support = -> Extrude528 [Face4]
  sketch-geometry (8):
    g0: Circle CenterX=-84 CenterY=8 CenterZ=0 NormalX=0 NormalY=0 NormalZ=1 Radius=3.5
    g1: Circle CenterX=-59 CenterY=8 CenterZ=0 NormalX=0 NormalY=0 NormalZ=1 Radius=3.5
    g2: Circle CenterX=-84 CenterY=-12 CenterZ=0 NormalX=0 NormalY=0 NormalZ=1 Radius=3.5
    g3: Circle CenterX=-59 CenterY=-12 CenterZ=0 NormalX=0 NormalY=0 NormalZ=1 Radius=3.5
    g4: LineSegment [constr] StartX=-84 StartY=8 StartZ=0 EndX=-59 EndY=8 EndZ=0
    g5: LineSegment [constr] StartX=-59 StartY=8 StartZ=0 EndX=-59 EndY=-12 EndZ=0
    g6: LineSegment [constr] StartX=-59 StartY=-12 StartZ=0 EndX=-84 EndY=-12 EndZ=0
    g7: LineSegment [constr] StartX=-84 StartY=-12 StartZ=0 EndX=-84 EndY=8 EndZ=0
  constraints (20):
    c: Radius(g0) = 3.5
    c: Equal(g0,g1)
    c: Equal(g0,g3)
    c: Equal(g0,g2)
    c: Coincident(g4,g0)
    c: Coincident(g4,g1)
    c: Coincident(g4,g5)
    c: Coincident(g5,g3)
    c: Vertical(g5)
    c: Coincident(g5,g6)
    c: Coincident(g6,g2)
    c: Horizontal(g6)
    c: Coincident(g6,g7)
    c: Coincident(g7,g4)
    c: Vertical(g7)
    c: Horizontal(g4)
    c: DistanceX(g0,g1) = 25
    c: DistanceY(g0,g2) = -20
    c: DistanceX(g3,g-3) = 59
    c: DistanceY(g3,g-3) = -13
FEATURE [PartDesign::Pocket] Pocket001
  Length = 5
  Placement = pos=(71.5,-20,-53) rot=(0,0,1;1.5708rad)
  Sketch = -> Sketch458
  Type = 1
FEATURE [PartDesign::LinearPattern] LinearPattern001
  Direction = -> Pocket001 [Edge1]
  Length = 1287
  Occurrences = 10
  Originals = -> [Pocket001]
  Placement = pos=(71.5,-20,-53) rot=(0,0,1;1.5708rad)
FEATURE [Sketcher::SketchObject] Sketch459
  ExternalGeometry = -> [LinearPattern001]
  Placement = pos=(71.5,-20,-28) rot=(0,0,1;1.5708rad)
  Support = -> LinearPattern001 [Face1]
  sketch-geometry (8):
    g0: LineSegment [constr] StartX=-10 StartY=96.5 StartZ=0 EndX=8 EndY=96.5 EndZ=0
    g1: LineSegment [constr] StartX=8 StartY=96.5 StartZ=0 EndX=8 EndY=46.5 EndZ=0
    g2: LineSegment [constr] StartX=8 StartY=46.5 StartZ=0 EndX=-10 EndY=46.5 EndZ=0
    g3: LineSegment [constr] StartX=-10 StartY=46.5 StartZ=0 EndX=-10 EndY=96.5 EndZ=0
    g4: Circle CenterX=-10 CenterY=96.5 CenterZ=0 NormalX=0 NormalY=0 NormalZ=1 Radius=3.5
    g5: Circle CenterX=8 CenterY=96.5 CenterZ=0 NormalX=0 NormalY=0 NormalZ=1 Radius=3.5
    g6: Circle CenterX=-10 CenterY=46.5 CenterZ=0 NormalX=0 NormalY=0 NormalZ=1 Radius=3.5
    g7: Circle CenterX=8 CenterY=46.5 CenterZ=0 NormalX=0 NormalY=0 NormalZ=1 Radius=3.5
  constraints (20):
    c: Coincident(g0,g1)
    c: Coincident(g1,g2)
    c: Coincident(g2,g3)
    c: Coincident(g3,g0)
    c: Horizontal(g0)
    c: Horizontal(g2)
    c: Vertical(g1)
    c: Vertical(g3)
    c: Coincident(g4,g0)
    c: Coincident(g5,g0)
    c: Coincident(g6,g2)
    c: Coincident(g7,g1)
    c: Radius(g4) = 3.5
    c: Equal(g4,g5)
    c: Equal(g4,g7)
    c: Equal(g4,g6)
    c: DistanceY(g0,g2) = -50
    c: DistanceX(g0,g0) = 18
    c: DistanceY(g2,g-3) = -46.5
    c: DistanceX(g-3,g2) = 10
FEATURE [PartDesign::Pocket] Pocket002
  Length = 5
  Placement = pos=(71.5,-20,-53) rot=(0,0,1;1.5708rad)
  Sketch = -> Sketch459
  Type = 1
FEATURE [PartDesign::LinearPattern] LinearPattern002
  Direction = -> Pocket002 [Edge1]
  Length = 1287
  Occurrences = 10
  Originals = -> [Pocket002]
  Placement = pos=(71.5,-20,-53) rot=(0,0,1;1.5708rad)
FEATURE [Sketcher::SketchObject] Sketch460
  ExternalGeometry = -> [LinearPattern002]
  Placement = pos=(71.5,-20,-78) rot=(0.707107,0.707107,0;3.14159rad)
  Support = -> LinearPattern002 [Face46]
  sketch-geometry (5):
    g0: Circle CenterX=-9 CenterY=-12.5 CenterZ=0 NormalX=0 NormalY=0 NormalZ=1 Radius=3.5
    g1: Circle CenterX=9 CenterY=-12.5 CenterZ=0 NormalX=0 NormalY=0 NormalZ=1 Radius=3.5
    g2: Circle CenterX=-9 CenterY=-1417.5 CenterZ=0 NormalX=0 NormalY=0 NormalZ=1 Radius=3.5
    g3: Circle CenterX=9 CenterY=-1417.5 CenterZ=0 NormalX=0 NormalY=0 NormalZ=1 Radius=3.5
    g4: LineSegment [constr] StartX=-9 StartY=-12.5 StartZ=0 EndX=-9 EndY=-1417.5 EndZ=0
  constraints (12):
    c: Coincident(g4,g0)
    c: Coincident(g4,g2)
    c: Vertical(g4)
    c: Radius(g0) = 3.5
    c: Equal(g0,g1)
    c: Equal(g0,g3)
    c: Equal(g0,g2)
    c: Symmetric(g0,g1,g-2)
    c: Symmetric(g2,g3,g-2)
    c: DistanceX(g1,g0) = -18
    c: DistanceY(g-1,g0) = -12.5
    c: DistanceY(g2,g-3) = -12.5
FEATURE [PartDesign::Pocket] Pocket003
  Length = 2
  Placement = pos=(71.5,-20,-53) rot=(0,0,1;1.5708rad)
  Sketch = -> Sketch460
  Type = 1
FEATURE [App::DocumentObjectGroup] Groupe028  label="Tube_50x40x2_L1430_D_001"
  Group = -> [Extrude528,LinearPattern001,LinearPattern002,Pocket001,Pocket002,Pocket003]
FEATURE [Sketcher::SketchObject] Sketch461
  Placement = pos=(0,0,0) rot=(1,0,0;1.5708rad)
  sketch-geometry (8):
    g0: LineSegment StartX=-20 StartY=25 StartZ=0 EndX=20 EndY=25 EndZ=0
    g1: LineSegment StartX=20 StartY=25 StartZ=0 EndX=20 EndY=-25 EndZ=0
    g2: LineSegment StartX=20 StartY=-25 StartZ=0 EndX=-20 EndY=-25 EndZ=0
    g3: LineSegment StartX=-20 StartY=-25 StartZ=0 EndX=-20 EndY=25 EndZ=0
    g4: LineSegment StartX=-18 StartY=23 StartZ=0 EndX=18 EndY=23 EndZ=0
    g5: LineSegment StartX=18 StartY=23 StartZ=0 EndX=18 EndY=-23 EndZ=0
    g6: LineSegment StartX=18 StartY=-23 StartZ=0 EndX=-18 EndY=-23 EndZ=0
    g7: LineSegment StartX=-18 StartY=-23 StartZ=0 EndX=-18 EndY=23 EndZ=0
  constraints (24):
    c: Coincident(g0,g1)
    c: Coincident(g1,g2)
    c: Coincident(g2,g3)
    c: Coincident(g3,g0)
    c: Horizontal(g0)
    c: Horizontal(g2)
    c: Vertical(g1)
    c: Vertical(g3)
    c: Distance(g0,g2) = 50
    c: DistanceX(g0,g0) = -40
    c: Symmetric(g0,g0,g-2)
    c: Symmetric(g0,g2,g-1)
    c: Coincident(g4,g5)
    c: Coincident(g5,g6)
    c: Coincident(g6,g7)
    c: Coincident(g7,g4)
    c: Horizontal(g4)
    c: Horizontal(g6)
    c: Vertical(g5)
    c: Vertical(g7)
    c: DistanceY(g0,g4) = -2
    c: DistanceX(g4,g0) = -2
    c: DistanceX(g5,g1) = 2
    c: DistanceY(g5,g1) = -2
FEATURE [Part::Extrusion] Extrude529
  Base = -> Sketch461
  Dir = (0,1430,0)
  Placement = pos=(-1358.5,-20,-53) rot=(0,0,1;1.5708rad)
  Solid = true
FEATURE [Sketcher::SketchObject] Sketch462
  ExternalGeometry = -> [Extrude529]
  Placement = pos=(-1358.5,-40,-53) rot=(1,0,0;1.5708rad)
  Support = -> Extrude529 [Face4]
  sketch-geometry (8):
    g0: Circle CenterX=-84 CenterY=8 CenterZ=0 NormalX=0 NormalY=0 NormalZ=1 Radius=3.5
    g1: Circle CenterX=-59 CenterY=8 CenterZ=0 NormalX=0 NormalY=0 NormalZ=1 Radius=3.5
    g2: Circle CenterX=-84 CenterY=-12 CenterZ=0 NormalX=0 NormalY=0 NormalZ=1 Radius=3.5
    g3: Circle CenterX=-59 CenterY=-12 CenterZ=0 NormalX=0 NormalY=0 NormalZ=1 Radius=3.5
    g4: LineSegment [constr] StartX=-84 StartY=8 StartZ=0 EndX=-59 EndY=8 EndZ=0
    g5: LineSegment [constr] StartX=-59 StartY=8 StartZ=0 EndX=-59 EndY=-12 EndZ=0
    g6: LineSegment [constr] StartX=-59 StartY=-12 StartZ=0 EndX=-84 EndY=-12 EndZ=0
    g7: LineSegment [constr] StartX=-84 StartY=-12 StartZ=0 EndX=-84 EndY=8 EndZ=0
  constraints (20):
    c: Radius(g0) = 3.5
    c: Equal(g0,g1)
    c: Equal(g0,g3)
    c: Equal(g0,g2)
    c: Coincident(g4,g0)
    c: Coincident(g4,g1)
    c: Coincident(g4,g5)
    c: Coincident(g5,g3)
    c: Vertical(g5)
    c: Coincident(g5,g6)
    c: Coincident(g6,g2)
    c: Horizontal(g6)
    c: Coincident(g6,g7)
    c: Coincident(g7,g4)
    c: Vertical(g7)
    c: Horizontal(g4)
    c: DistanceX(g0,g1) = 25
    c: DistanceY(g0,g2) = -20
    c: DistanceX(g3,g-3) = 59
    c: DistanceY(g3,g-3) = -13
FEATURE [PartDesign::Pocket] Pocket
  Length = 5
  Placement = pos=(-1358.5,-20,-53) rot=(0,0,1;1.5708rad)
  Sketch = -> Sketch462
  Type = 1
FEATURE [PartDesign::LinearPattern] LinearPattern
  Direction = -> Pocket [Edge1]
  Length = 1287
  Occurrences = 10
  Originals = -> [Pocket]
  Placement = pos=(-1358.5,-20,-53) rot=(0,0,1;1.5708rad)
FEATURE [Sketcher::SketchObject] Sketch463
  ExternalGeometry = -> [LinearPattern]
  Placement = pos=(-1358.5,-20,-28) rot=(0,0,1;1.5708rad)
  Support = -> LinearPattern [Face1]
  sketch-geometry (8):
    g0: LineSegment [constr] StartX=-10 StartY=96.5 StartZ=0 EndX=8 EndY=96.5 EndZ=0
    g1: LineSegment [constr] StartX=8 StartY=96.5 StartZ=0 EndX=8 EndY=46.5 EndZ=0
    g2: LineSegment [constr] StartX=8 StartY=46.5 StartZ=0 EndX=-10 EndY=46.5 EndZ=0
    g3: LineSegment [constr] StartX=-10 StartY=46.5 StartZ=0 EndX=-10 EndY=96.5 EndZ=0
    g4: Circle CenterX=-10 CenterY=96.5 CenterZ=0 NormalX=0 NormalY=0 NormalZ=1 Radius=3.5
    g5: Circle CenterX=8 CenterY=96.5 CenterZ=0 NormalX=0 NormalY=0 NormalZ=1 Radius=3.5
    g6: Circle CenterX=-10 CenterY=46.5 CenterZ=0 NormalX=0 NormalY=0 NormalZ=1 Radius=3.5
    g7: Circle CenterX=8 CenterY=46.5 CenterZ=0 NormalX=0 NormalY=0 NormalZ=1 Radius=3.5
  constraints (20):
    c: Coincident(g0,g1)
    c: Coincident(g1,g2)
    c: Coincident(g2,g3)
    c: Coincident(g3,g0)
    c: Horizontal(g0)
    c: Horizontal(g2)
    c: Vertical(g1)
    c: Vertical(g3)
    c: Coincident(g4,g0)
    c: Coincident(g5,g0)
    c: Coincident(g6,g2)
    c: Coincident(g7,g1)
    c: Radius(g4) = 3.5
    c: Equal(g4,g5)
    c: Equal(g4,g7)
    c: Equal(g4,g6)
    c: DistanceY(g0,g2) = -50
    c: DistanceX(g0,g0) = 18
    c: DistanceY(g2,g-3) = -46.5
    c: DistanceX(g-3,g2) = 10
FEATURE [PartDesign::Pocket] Pocket004
  Length = 5
  Placement = pos=(-1358.5,-20,-53) rot=(0,0,1;1.5708rad)
  Sketch = -> Sketch463
  Type = 1
FEATURE [PartDesign::LinearPattern] LinearPattern003
  Direction = -> Pocket004 [Edge1]
  Length = 1287
  Occurrences = 10
  Originals = -> [Pocket004]
  Placement = pos=(-1358.5,-20,-53) rot=(0,0,1;1.5708rad)
FEATURE [Sketcher::SketchObject] Sketch464
  ExternalGeometry = -> [LinearPattern003]
  Placement = pos=(-1358.5,-20,-78) rot=(0.707107,0.707107,0;3.14159rad)
  Support = -> LinearPattern003 [Face46]
  sketch-geometry (5):
    g0: Circle CenterX=-9 CenterY=-12.5 CenterZ=0 NormalX=0 NormalY=0 NormalZ=1 Radius=3.5
    g1: Circle CenterX=9 CenterY=-12.5 CenterZ=0 NormalX=0 NormalY=0 NormalZ=1 Radius=3.5
    g2: Circle CenterX=-9 CenterY=-1417.5 CenterZ=0 NormalX=0 NormalY=0 NormalZ=1 Radius=3.5
    g3: Circle CenterX=9 CenterY=-1417.5 CenterZ=0 NormalX=0 NormalY=0 NormalZ=1 Radius=3.5
    g4: LineSegment [constr] StartX=-9 StartY=-12.5 StartZ=0 EndX=-9 EndY=-1417.5 EndZ=0
  constraints (12):
    c: Coincident(g4,g0)
    c: Coincident(g4,g2)
    c: Vertical(g4)
    c: Radius(g0) = 3.5
    c: Equal(g0,g1)
    c: Equal(g0,g3)
    c: Equal(g0,g2)
    c: Symmetric(g0,g1,g-2)
    c: Symmetric(g2,g3,g-2)
    c: DistanceX(g1,g0) = -18
    c: DistanceY(g-1,g0) = -12.5
    c: DistanceY(g2,g-3) = -12.5
FEATURE [PartDesign::Pocket] Pocket005
  Length = 2
  Placement = pos=(-1358.5,-20,-53) rot=(0,0,1;1.5708rad)
  Sketch = -> Sketch464
  Type = 1
FEATURE [App::DocumentObjectGroup] Groupe029  label="Tube_50x40x2_L1430_D_002"
  Group = -> [Extrude529,LinearPattern,LinearPattern003,Pocket,Pocket004,Pocket005]
FEATURE [Sketcher::SketchObject] Sketch465
  Placement = pos=(0,0,0) rot=(1,0,0;1.5708rad)
  sketch-geometry (8):
    g0: LineSegment StartX=-20 StartY=25 StartZ=0 EndX=20 EndY=25 EndZ=0
    g1: LineSegment StartX=20 StartY=25 StartZ=0 EndX=20 EndY=-25 EndZ=0
    g2: LineSegment StartX=20 StartY=-25 StartZ=0 EndX=-20 EndY=-25 EndZ=0
    g3: LineSegment StartX=-20 StartY=-25 StartZ=0 EndX=-20 EndY=25 EndZ=0
    g4: LineSegment StartX=-18 StartY=23 StartZ=0 EndX=18 EndY=23 EndZ=0
    g5: LineSegment StartX=18 StartY=23 StartZ=0 EndX=18 EndY=-23 EndZ=0
    g6: LineSegment StartX=18 StartY=-23 StartZ=0 EndX=-18 EndY=-23 EndZ=0
    g7: LineSegment StartX=-18 StartY=-23 StartZ=0 EndX=-18 EndY=23 EndZ=0
  constraints (24):
    c: Coincident(g0,g1)
    c: Coincident(g1,g2)
    c: Coincident(g2,g3)
    c: Coincident(g3,g0)
    c: Horizontal(g0)
    c: Horizontal(g2)
    c: Vertical(g1)
    c: Vertical(g3)
    c: Distance(g0,g2) = 50
    c: DistanceX(g0,g0) = -40
    c: Symmetric(g0,g0,g-2)
    c: Symmetric(g0,g2,g-1)
    c: Coincident(g4,g5)
    c: Coincident(g5,g6)
    c: Coincident(g6,g7)
    c: Coincident(g7,g4)
    c: Horizontal(g4)
    c: Horizontal(g6)
    c: Vertical(g5)
    c: Vertical(g7)
    c: DistanceY(g0,g4) = -2
    c: DistanceX(g4,g0) = -2
    c: DistanceX(g5,g1) = 2
    c: DistanceY(g5,g1) = -2
FEATURE [Part::Extrusion] Extrude530
  Base = -> Sketch465
  Dir = (0,1430,0)
  Placement = pos=(71.5,-2120,-53) rot=(0,0,1;1.5708rad)
  Solid = true
FEATURE [Sketcher::SketchObject] Sketch466
  ExternalGeometry = -> [Extrude530]
  Placement = pos=(71.5,-2140,-53) rot=(1,0,0;1.5708rad)
  Support = -> Extrude530 [Face4]
  sketch-geometry (8):
    g0: Circle CenterX=-84 CenterY=8 CenterZ=0 NormalX=0 NormalY=0 NormalZ=1 Radius=3.5
    g1: Circle CenterX=-59 CenterY=8 CenterZ=0 NormalX=0 NormalY=0 NormalZ=1 Radius=3.5
    g2: Circle CenterX=-84 CenterY=-12 CenterZ=0 NormalX=0 NormalY=0 NormalZ=1 Radius=3.5
    g3: Circle CenterX=-59 CenterY=-12 CenterZ=0 NormalX=0 NormalY=0 NormalZ=1 Radius=3.5
    g4: LineSegment [constr] StartX=-84 StartY=8 StartZ=0 EndX=-59 EndY=8 EndZ=0
    g5: LineSegment [constr] StartX=-59 StartY=8 StartZ=0 EndX=-59 EndY=-12 EndZ=0
    g6: LineSegment [constr] StartX=-59 StartY=-12 StartZ=0 EndX=-84 EndY=-12 EndZ=0
    g7: LineSegment [constr] StartX=-84 StartY=-12 StartZ=0 EndX=-84 EndY=8 EndZ=0
  constraints (20):
    c: Radius(g0) = 3.5
    c: Equal(g0,g1)
    c: Equal(g0,g3)
    c: Equal(g0,g2)
    c: Coincident(g4,g0)
    c: Coincident(g4,g1)
    c: Coincident(g4,g5)
    c: Coincident(g5,g3)
    c: Vertical(g5)
    c: Coincident(g5,g6)
    c: Coincident(g6,g2)
    c: Horizontal(g6)
    c: Coincident(g6,g7)
    c: Coincident(g7,g4)
    c: Vertical(g7)
    c: Horizontal(g4)
    c: DistanceX(g0,g1) = 25
    c: DistanceY(g0,g2) = -20
    c: DistanceX(g3,g-3) = 59
    c: DistanceY(g3,g-3) = -13
FEATURE [PartDesign::Pocket] Pocket006
  Length = 5
  Placement = pos=(71.5,-2120,-53) rot=(0,0,1;1.5708rad)
  Sketch = -> Sketch466
  Type = 1
FEATURE [PartDesign::LinearPattern] LinearPattern004
  Direction = -> Pocket006 [Edge1]
  Length = 1287
  Occurrences = 10
  Originals = -> [Pocket006]
  Placement = pos=(71.5,-2120,-53) rot=(0,0,1;1.5708rad)
FEATURE [Sketcher::SketchObject] Sketch467
  ExternalGeometry = -> [LinearPattern004]
  Placement = pos=(71.5,-2120,-78) rot=(0.707107,0.707107,0;3.14159rad)
  Support = -> LinearPattern004 [Face6]
  sketch-geometry (5):
    g0: Circle CenterX=-9 CenterY=-12.5 CenterZ=0 NormalX=0 NormalY=0 NormalZ=1 Radius=3.5
    g1: Circle CenterX=9 CenterY=-12.5 CenterZ=0 NormalX=0 NormalY=0 NormalZ=1 Radius=3.5
    g2: Circle CenterX=-9 CenterY=-1417.5 CenterZ=0 NormalX=0 NormalY=0 NormalZ=1 Radius=3.5
    g3: Circle CenterX=9 CenterY=-1417.5 CenterZ=0 NormalX=0 NormalY=0 NormalZ=1 Radius=3.5
    g4: LineSegment [constr] StartX=-9 StartY=-1417.5 StartZ=0 EndX=-9 EndY=-12.5 EndZ=0
  constraints (12):
    c: Radius(g0) = 3.5
    c: Equal(g0,g1)
    c: Symmetric(g0,g1,g-2)
    c: DistanceY(g-1,g0) = -12.5
    c: DistanceX(g0,g1) = 18
    c: Equal(g2,g3)
    c: Equal(g3,g0)
    c: Symmetric(g2,g3,g-2)
    c: Coincident(g4,g2)
    c: Coincident(g4,g0)
    c: Vertical(g4)
    c: DistanceY(g-3,g2) = 12.5
FEATURE [PartDesign::Pocket] Pocket007
  Length = 2
  Placement = pos=(71.5,-2120,-53) rot=(0,0,1;1.5708rad)
  Sketch = -> Sketch467
  Type = 1
FEATURE [App::DocumentObjectGroup] Groupe030  label="Tube_50x40x2_L1430_G_001"
  Group = -> [Extrude530,Pocket007,Pocket006,LinearPattern004]
FEATURE [Sketcher::SketchObject] Sketch468
  Placement = pos=(0,0,0) rot=(1,0,0;1.5708rad)
  sketch-geometry (8):
    g0: LineSegment StartX=-20 StartY=25 StartZ=0 EndX=20 EndY=25 EndZ=0
    g1: LineSegment StartX=20 StartY=25 StartZ=0 EndX=20 EndY=-25 EndZ=0
    g2: LineSegment StartX=20 StartY=-25 StartZ=0 EndX=-20 EndY=-25 EndZ=0
    g3: LineSegment StartX=-20 StartY=-25 StartZ=0 EndX=-20 EndY=25 EndZ=0
    g4: LineSegment StartX=-18 StartY=23 StartZ=0 EndX=18 EndY=23 EndZ=0
    g5: LineSegment StartX=18 StartY=23 StartZ=0 EndX=18 EndY=-23 EndZ=0
    g6: LineSegment StartX=18 StartY=-23 StartZ=0 EndX=-18 EndY=-23 EndZ=0
    g7: LineSegment StartX=-18 StartY=-23 StartZ=0 EndX=-18 EndY=23 EndZ=0
  constraints (24):
    c: Coincident(g0,g1)
    c: Coincident(g1,g2)
    c: Coincident(g2,g3)
    c: Coincident(g3,g0)
    c: Horizontal(g0)
    c: Horizontal(g2)
    c: Vertical(g1)
    c: Vertical(g3)
    c: Distance(g0,g2) = 50
    c: DistanceX(g0,g0) = -40
    c: Symmetric(g0,g0,g-2)
    c: Symmetric(g0,g2,g-1)
    c: Coincident(g4,g5)
    c: Coincident(g5,g6)
    c: Coincident(g6,g7)
    c: Coincident(g7,g4)
    c: Horizontal(g4)
    c: Horizontal(g6)
    c: Vertical(g5)
    c: Vertical(g7)
    c: DistanceY(g0,g4) = -2
    c: DistanceX(g4,g0) = -2
    c: DistanceX(g5,g1) = 2
    c: DistanceY(g5,g1) = -2
FEATURE [Part::Extrusion] Extrude531
  Base = -> Sketch468
  Dir = (0,1430,0)
  Placement = pos=(-1358.5,-2120,-53) rot=(0,0,1;1.5708rad)
  Solid = true
FEATURE [Sketcher::SketchObject] Sketch469
  ExternalGeometry = -> [Extrude531]
  Placement = pos=(-1358.5,-2140,-53) rot=(1,0,0;1.5708rad)
  Support = -> Extrude531 [Face4]
  sketch-geometry (8):
    g0: Circle CenterX=-84 CenterY=8 CenterZ=0 NormalX=0 NormalY=0 NormalZ=1 Radius=3.5
    g1: Circle CenterX=-59 CenterY=8 CenterZ=0 NormalX=0 NormalY=0 NormalZ=1 Radius=3.5
    g2: Circle CenterX=-84 CenterY=-12 CenterZ=0 NormalX=0 NormalY=0 NormalZ=1 Radius=3.5
    g3: Circle CenterX=-59 CenterY=-12 CenterZ=0 NormalX=0 NormalY=0 NormalZ=1 Radius=3.5
    g4: LineSegment [constr] StartX=-84 StartY=8 StartZ=0 EndX=-59 EndY=8 EndZ=0
    g5: LineSegment [constr] StartX=-59 StartY=8 StartZ=0 EndX=-59 EndY=-12 EndZ=0
    g6: LineSegment [constr] StartX=-59 StartY=-12 StartZ=0 EndX=-84 EndY=-12 EndZ=0
    g7: LineSegment [constr] StartX=-84 StartY=-12 StartZ=0 EndX=-84 EndY=8 EndZ=0
  constraints (20):
    c: Radius(g0) = 3.5
    c: Equal(g0,g1)
    c: Equal(g0,g3)
    c: Equal(g0,g2)
    c: Coincident(g4,g0)
    c: Coincident(g4,g1)
    c: Coincident(g4,g5)
    c: Coincident(g5,g3)
    c: Vertical(g5)
    c: Coincident(g5,g6)
    c: Coincident(g6,g2)
    c: Horizontal(g6)
    c: Coincident(g6,g7)
    c: Coincident(g7,g4)
    c: Vertical(g7)
    c: Horizontal(g4)
    c: DistanceX(g0,g1) = 25
    c: DistanceY(g0,g2) = -20
    c: DistanceX(g3,g-3) = 59
    c: DistanceY(g3,g-3) = -13
FEATURE [PartDesign::Pocket] Pocket008
  Length = 5
  Placement = pos=(-1358.5,-2120,-53) rot=(0,0,1;1.5708rad)
  Sketch = -> Sketch469
  Type = 1
FEATURE [PartDesign::LinearPattern] LinearPattern005
  Direction = -> Pocket008 [Edge1]
  Length = 1287
  Occurrences = 10
  Originals = -> [Pocket008]
  Placement = pos=(-1358.5,-2120,-53) rot=(0,0,1;1.5708rad)
FEATURE [Sketcher::SketchObject] Sketch470
  ExternalGeometry = -> [LinearPattern005]
  Placement = pos=(-1358.5,-2120,-78) rot=(0.707107,0.707107,0;3.14159rad)
  Support = -> LinearPattern005 [Face6]
  sketch-geometry (5):
    g0: Circle CenterX=-9 CenterY=-12.5 CenterZ=0 NormalX=0 NormalY=0 NormalZ=1 Radius=3.5
    g1: Circle CenterX=9 CenterY=-12.5 CenterZ=0 NormalX=0 NormalY=0 NormalZ=1 Radius=3.5
    g2: Circle CenterX=-9 CenterY=-1417.5 CenterZ=0 NormalX=0 NormalY=0 NormalZ=1 Radius=3.5
    g3: Circle CenterX=9 CenterY=-1417.5 CenterZ=0 NormalX=0 NormalY=0 NormalZ=1 Radius=3.5
    g4: LineSegment [constr] StartX=-9 StartY=-1417.5 StartZ=0 EndX=-9 EndY=-12.5 EndZ=0
  constraints (12):
    c: Radius(g0) = 3.5
    c: Equal(g0,g1)
    c: Symmetric(g0,g1,g-2)
    c: DistanceY(g-1,g0) = -12.5
    c: DistanceX(g0,g1) = 18
    c: Equal(g2,g3)
    c: Equal(g3,g0)
    c: Symmetric(g2,g3,g-2)
    c: Coincident(g4,g2)
    c: Coincident(g4,g0)
    c: Vertical(g4)
    c: DistanceY(g-3,g2) = 12.5
FEATURE [PartDesign::Pocket] Pocket009
  Length = 2
  Placement = pos=(-1358.5,-2120,-53) rot=(0,0,1;1.5708rad)
  Sketch = -> Sketch470
  Type = 1
FEATURE [App::DocumentObjectGroup] Groupe031  label="Tube_50x40x2_L1430_G_002"
  Group = -> [Extrude531,Pocket009,Pocket008,LinearPattern005]
FEATURE [Sketcher::SketchObject] Sketch473
  Placement = pos=(-2788.5,-535,-128) rot=(0.57735,0.57735,0.57735;2.0944rad)
  sketch-geometry (10):
    g0: LineSegment StartX=25 StartY=-25 StartZ=0 EndX=25 EndY=25 EndZ=0
    g1: LineSegment StartX=25 StartY=25 StartZ=0 EndX=-25 EndY=25 EndZ=0
    g2: LineSegment StartX=-25 StartY=25 StartZ=0 EndX=-25 EndY=-25 EndZ=0
    g3: LineSegment StartX=-25 StartY=-25 StartZ=0 EndX=25 EndY=-25 EndZ=0
    g4: Circle [constr] CenterX=0 CenterY=0 CenterZ=0 NormalX=0 NormalY=0 NormalZ=1 Radius=35.3553
    g5: LineSegment StartX=22 StartY=-22 StartZ=0 EndX=22 EndY=22 EndZ=0
    g6: LineSegment StartX=22 StartY=22 StartZ=0 EndX=-22 EndY=22 EndZ=0
    g7: LineSegment StartX=-22 StartY=22 StartZ=0 EndX=-22 EndY=-22 EndZ=0
    g8: LineSegment StartX=-22 StartY=-22 StartZ=0 EndX=22 EndY=-22 EndZ=0
    g9: Circle [constr] CenterX=0 CenterY=0 CenterZ=0 NormalX=0 NormalY=0 NormalZ=1 Radius=31.1127
  constraints (30):
    c: Coincident(g0,g1)
    c: Coincident(g1,g2)
    c: Coincident(g2,g3)
    c: Coincident(g3,g0)
    c: Equal(g0,g1)
    c: Equal(g0,g2)
    c: Equal(g0,g3)
    c: PointOnObject(g0,g4)
    c: PointOnObject(g1,g4)
    c: PointOnObject(g2,g4)
    c: PointOnObject(g3,g4)
    c: Coincident(g1,g-1)
    c: Coincident(g5,g6)
    c: Coincident(g6,g7)
    c: Coincident(g7,g8)
    c: Coincident(g8,g5)
    c: Equal(g5,g6)
    c: Equal(g5,g7)
    c: Equal(g5,g8)
    c: PointOnObject(g5,g9)
    c: PointOnObject(g6,g9)
    c: PointOnObject(g7,g9)
    c: PointOnObject(g8,g9)
    c: Coincident(g6,g-1)
    c: Horizontal(g1)
    c: DistanceX(g1,g0) = 50
    c: Coincident(g4,g-1)
    c: Coincident(g9,g-1)
    c: Horizontal(g6)
    c: DistanceX(g6,g5) = 44
FEATURE [PartDesign::Pad] Pad001
  Length = 2905
  Length2 = 100
  Placement = pos=(-2788.5,-535,-128) rot=(0.57735,0.57735,0.57735;2.0944rad)
  Sketch = -> Sketch473
  Type = 0
FEATURE [Sketcher::SketchObject] Sketch474
  ExternalGeometry = -> [Pad001]
  Placement = pos=(-2788.5,-510,-128) rot=(0.57735,0.57735,0.57735;4.18879rad)
  Support = -> Pad001 [Face1]
  sketch-geometry (3):
    g0: LineSegment StartX=25 StartY=2905 StartZ=0 EndX=-25 EndY=2859.98 EndZ=0
    g1: LineSegment StartX=-25 StartY=2859.98 StartZ=0 EndX=-25 EndY=2905 EndZ=0
    g2: LineSegment StartX=-25 StartY=2905 StartZ=0 EndX=25 EndY=2905 EndZ=0
  constraints (7):
    c: PointOnObject(g0,g-4)
    c: Coincident(g0,g-3)
    c: Angle(g0,g-5) = 0.837758
    c: Coincident(g0,g1)
    c: Coincident(g1,g-4)
    c: Coincident(g1,g2)
    c: Coincident(g2,g0)
FEATURE [PartDesign::Pocket] Pocket011
  Length = 5
  Placement = pos=(-2788.5,-535,-128) rot=(0.57735,0.57735,0.57735;2.0944rad)
  Sketch = -> Sketch474
  Type = 1
FEATURE [Sketcher::SketchObject] Sketch475
  Placement = pos=(-2788.5,-535,-103) rot=(0,0,-1;1.5708rad)
  Support = -> Pocket011 [Face3]
  sketch-geometry (9):
    g0: Circle CenterX=-12.5 CenterY=12.5 CenterZ=0 NormalX=0 NormalY=0 NormalZ=1 Radius=3.5
    g1: Circle CenterX=12.5 CenterY=12.5 CenterZ=0 NormalX=0 NormalY=0 NormalZ=1 Radius=3.5
    g2: Circle CenterX=-12.5 CenterY=1417.5 CenterZ=0 NormalX=0 NormalY=0 NormalZ=1 Radius=3.5
    g3: Circle CenterX=12.5 CenterY=1417.5 CenterZ=0 NormalX=0 NormalY=0 NormalZ=1 Radius=3.5
    g4: Circle CenterX=-12.5 CenterY=1442.5 CenterZ=0 NormalX=0 NormalY=0 NormalZ=1 Radius=3.5
    g5: Circle CenterX=12.5 CenterY=1442.5 CenterZ=0 NormalX=0 NormalY=0 NormalZ=1 Radius=3.5
    g6: Circle CenterX=-12.5 CenterY=2847.5 CenterZ=0 NormalX=0 NormalY=0 NormalZ=1 Radius=3.5
    g7: Circle CenterX=12.5 CenterY=2847.5 CenterZ=0 NormalX=0 NormalY=0 NormalZ=1 Radius=3.5
    g8: LineSegment [constr] StartX=-12.5 StartY=12.5 StartZ=0 EndX=-12.5 EndY=2847.5 EndZ=0
  constraints (16):
    c: Radius(g0) = 3.5
    c: Equal(g0, g1-g7) x7
    c: Symmetric(g0,g1,g-2)
    c: Symmetric(g2,g3,g-2)
    c: Symmetric(g4,g5,g-2)
    c: Symmetric(g7,g6,g-2)
    c: Coincident(g8,g0)
    c: Coincident(g8,g6)
    c: PointOnObject(g4,g8)
    c: PointOnObject(g2,g8)
    c: Vertical(g8)
    c: DistanceY(g-1,g0) = 12.5
    c: DistanceX(g0,g1) = 25
    c: DistanceY(g2,g0) = -1405
    c: DistanceY(g2,g4) = 25
    c: DistanceY(g4,g6) = 1405
FEATURE [PartDesign::Pocket] Pocket012
  Length = 5
  Placement = pos=(-2788.5,-535,-128) rot=(0.57735,0.57735,0.57735;2.0944rad)
  Sketch = -> Sketch475
  Type = 1
FEATURE [App::DocumentObjectGroup] Groupe032  label="Tube_50x50x3_L2890_001"
  Group = -> [Pocket012,Pad001,Pocket011]
FEATURE [Sketcher::SketchObject] Sketch476
  Placement = pos=(-2788.5,-1605,-128) rot=(0.57735,0.57735,0.57735;2.0944rad)
  sketch-geometry (10):
    g0: LineSegment StartX=25 StartY=-25 StartZ=0 EndX=25 EndY=25 EndZ=0
    g1: LineSegment StartX=25 StartY=25 StartZ=0 EndX=-25 EndY=25 EndZ=0
    g2: LineSegment StartX=-25 StartY=25 StartZ=0 EndX=-25 EndY=-25 EndZ=0
    g3: LineSegment StartX=-25 StartY=-25 StartZ=0 EndX=25 EndY=-25 EndZ=0
    g4: Circle [constr] CenterX=0 CenterY=0 CenterZ=0 NormalX=0 NormalY=0 NormalZ=1 Radius=35.3553
    g5: LineSegment StartX=22 StartY=-22 StartZ=0 EndX=22 EndY=22 EndZ=0
    g6: LineSegment StartX=22 StartY=22 StartZ=0 EndX=-22 EndY=22 EndZ=0
    g7: LineSegment StartX=-22 StartY=22 StartZ=0 EndX=-22 EndY=-22 EndZ=0
    g8: LineSegment StartX=-22 StartY=-22 StartZ=0 EndX=22 EndY=-22 EndZ=0
    g9: Circle [constr] CenterX=0 CenterY=0 CenterZ=0 NormalX=0 NormalY=0 NormalZ=1 Radius=31.1127
  constraints (30):
    c: Coincident(g0,g1)
    c: Coincident(g1,g2)
    c: Coincident(g2,g3)
    c: Coincident(g3,g0)
    c: Equal(g0,g1)
    c: Equal(g0,g2)
    c: Equal(g0,g3)
    c: PointOnObject(g0,g4)
    c: PointOnObject(g1,g4)
    c: PointOnObject(g2,g4)
    c: PointOnObject(g3,g4)
    c: Coincident(g1,g-1)
    c: Coincident(g5,g6)
    c: Coincident(g6,g7)
    c: Coincident(g7,g8)
    c: Coincident(g8,g5)
    c: Equal(g5,g6)
    c: Equal(g5,g7)
    c: Equal(g5,g8)
    c: PointOnObject(g5,g9)
    c: PointOnObject(g6,g9)
    c: PointOnObject(g7,g9)
    c: PointOnObject(g8,g9)
    c: Coincident(g6,g-1)
    c: Horizontal(g1)
    c: DistanceX(g1,g0) = 50
    c: Coincident(g4,g-1)
    c: Coincident(g9,g-1)
    c: Horizontal(g6)
    c: DistanceX(g6,g5) = 44
FEATURE [PartDesign::Pad] Pad
  Length = 2905
  Length2 = 100
  Placement = pos=(-2788.5,-1605,-128) rot=(0.57735,0.57735,0.57735;2.0944rad)
  Sketch = -> Sketch476
  Type = 0
FEATURE [Sketcher::SketchObject] Sketch477
  ExternalGeometry = -> [Pad]
  Placement = pos=(-2788.5,-1580,-128) rot=(0.57735,0.57735,0.57735;4.18879rad)
  Support = -> Pad [Face1]
  sketch-geometry (3):
    g0: LineSegment StartX=25 StartY=2905 StartZ=0 EndX=-25 EndY=2859.98 EndZ=0
    g1: LineSegment StartX=-25 StartY=2859.98 StartZ=0 EndX=-25 EndY=2905 EndZ=0
    g2: LineSegment StartX=-25 StartY=2905 StartZ=0 EndX=25 EndY=2905 EndZ=0
  constraints (7):
    c: PointOnObject(g0,g-4)
    c: Coincident(g0,g-3)
    c: Angle(g0,g-5) = 0.837758
    c: Coincident(g0,g1)
    c: Coincident(g1,g-4)
    c: Coincident(g1,g2)
    c: Coincident(g2,g0)
FEATURE [PartDesign::Pocket] Pocket013
  Length = 5
  Placement = pos=(-2788.5,-1605,-128) rot=(0.57735,0.57735,0.57735;2.0944rad)
  Sketch = -> Sketch477
  Type = 1
FEATURE [Sketcher::SketchObject] Sketch478
  Placement = pos=(-2788.5,-1605,-103) rot=(0,0,-1;1.5708rad)
  Support = -> Pocket013 [Face3]
  sketch-geometry (9):
    g0: Circle CenterX=-12.5 CenterY=12.5 CenterZ=0 NormalX=0 NormalY=0 NormalZ=1 Radius=3.5
    g1: Circle CenterX=12.5 CenterY=12.5 CenterZ=0 NormalX=0 NormalY=0 NormalZ=1 Radius=3.5
    g2: Circle CenterX=-12.5 CenterY=1417.5 CenterZ=0 NormalX=0 NormalY=0 NormalZ=1 Radius=3.5
    g3: Circle CenterX=12.5 CenterY=1417.5 CenterZ=0 NormalX=0 NormalY=0 NormalZ=1 Radius=3.5
    g4: Circle CenterX=-12.5 CenterY=1442.5 CenterZ=0 NormalX=0 NormalY=0 NormalZ=1 Radius=3.5
    g5: Circle CenterX=12.5 CenterY=1442.5 CenterZ=0 NormalX=0 NormalY=0 NormalZ=1 Radius=3.5
    g6: Circle CenterX=-12.5 CenterY=2847.5 CenterZ=0 NormalX=0 NormalY=0 NormalZ=1 Radius=3.5
    g7: Circle CenterX=12.5 CenterY=2847.5 CenterZ=0 NormalX=0 NormalY=0 NormalZ=1 Radius=3.5
    g8: LineSegment [constr] StartX=-12.5 StartY=12.5 StartZ=0 EndX=-12.5 EndY=2847.5 EndZ=0
  constraints (16):
    c: Radius(g0) = 3.5
    c: Equal(g0, g1-g7) x7
    c: Symmetric(g0,g1,g-2)
    c: Symmetric(g2,g3,g-2)
    c: Symmetric(g4,g5,g-2)
    c: Symmetric(g7,g6,g-2)
    c: Coincident(g8,g0)
    c: Coincident(g8,g6)
    c: PointOnObject(g4,g8)
    c: PointOnObject(g2,g8)
    c: Vertical(g8)
    c: DistanceY(g-1,g0) = 12.5
    c: DistanceX(g0,g1) = 25
    c: DistanceY(g2,g0) = -1405
    c: DistanceY(g2,g4) = 25
    c: DistanceY(g4,g6) = 1405
FEATURE [PartDesign::Pocket] Pocket014
  Length = 5
  Placement = pos=(-2788.5,-1605,-128) rot=(0.57735,0.57735,0.57735;2.0944rad)
  Sketch = -> Sketch478
  Type = 1
FEATURE [App::DocumentObjectGroup] Groupe033  label="Tube_50x50x3_L2890_002"
  Group = -> [Pocket014,Pad,Pocket013]
FEATURE [Sketcher::SketchObject] Sketch479
  Placement = pos=(0,0,0) rot=(1,0,0;1.5708rad)
  sketch-geometry (10):
    g0: LineSegment StartX=12.5 StartY=12.5 StartZ=0 EndX=-12.5 EndY=12.5 EndZ=0
    g1: LineSegment StartX=-12.5 StartY=12.5 StartZ=0 EndX=-12.5 EndY=-12.5 EndZ=0
    g2: LineSegment StartX=-12.5 StartY=-12.5 StartZ=0 EndX=12.5 EndY=-12.5 EndZ=0
    g3: LineSegment StartX=12.5 StartY=-12.5 StartZ=0 EndX=12.5 EndY=12.5 EndZ=0
    g4: Circle [constr] CenterX=0 CenterY=0 CenterZ=0 NormalX=0 NormalY=0 NormalZ=1 Radius=17.6777
    g5: LineSegment StartX=9.5 StartY=-9.5 StartZ=0 EndX=9.5 EndY=9.5 EndZ=0
    g6: LineSegment StartX=9.5 StartY=9.5 StartZ=0 EndX=-9.5 EndY=9.5 EndZ=0
    g7: LineSegment StartX=-9.5 StartY=9.5 StartZ=0 EndX=-9.5 EndY=-9.5 EndZ=0
    g8: LineSegment StartX=-9.5 StartY=-9.5 StartZ=0 EndX=9.5 EndY=-9.5 EndZ=0
    g9: Circle [constr] CenterX=0 CenterY=0 CenterZ=0 NormalX=0 NormalY=0 NormalZ=1 Radius=13.435
  constraints (30):
    c: Coincident(g0,g1)
    c: Coincident(g1,g2)
    c: Coincident(g2,g3)
    c: Coincident(g3,g0)
    c: Equal(g0,g1)
    c: Equal(g0,g2)
    c: Equal(g0,g3)
    c: PointOnObject(g0,g4)
    c: PointOnObject(g1,g4)
    c: PointOnObject(g2,g4)
    c: PointOnObject(g3,g4)
    c: Coincident(g1,g-1)
    c: Coincident(g5,g6)
    c: Coincident(g6,g7)
    c: Coincident(g7,g8)
    c: Coincident(g8,g5)
    c: Equal(g5,g6)
    c: Equal(g5,g7)
    c: Equal(g5,g8)
    c: PointOnObject(g5,g9)
    c: PointOnObject(g6,g9)
    c: PointOnObject(g7,g9)
    c: PointOnObject(g8,g9)
    c: Coincident(g6,g-1)
    c: DistanceX(g0,g0) = 25
    c: Horizontal(g0)
    c: Horizontal(g6)
    c: DistanceX(g6,g5) = 19
    c: Coincident(g9,g-1)
    c: Coincident(g4,g-1)
FEATURE [Part::Extrusion] Extrude532
  Base = -> Sketch479
  Dir = (0,2140,0)
  Placement = pos=(59,0,-90.5) rot=(0,0,1;3.14159rad)
  Solid = true
FEATURE [Sketcher::SketchObject] Sketch480
  Placement = pos=(59,0,-78) rot=(0,0,1;3.14159rad)
  Support = -> Extrude532 [Face1]
  sketch-geometry (8):
    g0: Circle CenterX=0 CenterY=11 CenterZ=0 NormalX=0 NormalY=0 NormalZ=1 Radius=3.5
    g1: Circle CenterX=0 CenterY=29 CenterZ=0 NormalX=0 NormalY=0 NormalZ=1 Radius=3.5
    g2: Circle CenterX=0 CenterY=522.5 CenterZ=0 NormalX=0 NormalY=0 NormalZ=1 Radius=3.5
    g3: Circle CenterX=0 CenterY=547.5 CenterZ=0 NormalX=0 NormalY=0 NormalZ=1 Radius=3.5
    g4: Circle CenterX=0 CenterY=1592.5 CenterZ=0 NormalX=0 NormalY=0 NormalZ=1 Radius=3.5
    g5: Circle CenterX=0 CenterY=1617.5 CenterZ=0 NormalX=0 NormalY=0 NormalZ=1 Radius=3.5
    g6: Circle CenterX=0 CenterY=2111 CenterZ=0 NormalX=0 NormalY=0 NormalZ=1 Radius=3.5
    g7: Circle CenterX=0 CenterY=2129 CenterZ=0 NormalX=0 NormalY=0 NormalZ=1 Radius=3.5
  constraints (18):
    c: PointOnObject(g0,g-2)
    c: PointOnObject(g1,g-2)
    c: DistanceY(g1,g0) = -18
    c: DistanceY(g-1,g0) = 11
    c: PointOnObject(g2,g-2)
    c: PointOnObject(g4,g-2)
    c: PointOnObject(g5,g-2)
    c: PointOnObject(g3,g-2)
    c: PointOnObject(g6,g-2)
    c: PointOnObject(g7,g-2)
    c: DistanceY(g7,g6) = -18
    c: DistanceY(g2,g3) = 25
    c: DistanceY(g5,g4) = -25
    c: Radius(g0) = 3.5
    c: Equal(g0, g1-g7) x7
    c: DistanceY(g6,g5) = -493.5
    c: DistanceY(g4,g3) = -1045
    c: DistanceY(g2,g1) = -493.5
FEATURE [PartDesign::Pocket] Pocket015
  Length = 5
  Placement = pos=(59,0,-90.5) rot=(0,0,1;3.14159rad)
  Sketch = -> Sketch480
  Type = 1
FEATURE [App::DocumentObjectGroup] Groupe034  label="Tube_25x25x3_L2140_001"
  Group = -> [Pocket015,Extrude532]
FEATURE [Sketcher::SketchObject] Sketch481
  Placement = pos=(0,0,0) rot=(1,0,0;1.5708rad)
  sketch-geometry (10):
    g0: LineSegment StartX=12.5 StartY=12.5 StartZ=0 EndX=-12.5 EndY=12.5 EndZ=0
    g1: LineSegment StartX=-12.5 StartY=12.5 StartZ=0 EndX=-12.5 EndY=-12.5 EndZ=0
    g2: LineSegment StartX=-12.5 StartY=-12.5 StartZ=0 EndX=12.5 EndY=-12.5 EndZ=0
    g3: LineSegment StartX=12.5 StartY=-12.5 StartZ=0 EndX=12.5 EndY=12.5 EndZ=0
    g4: Circle [constr] CenterX=0 CenterY=0 CenterZ=0 NormalX=0 NormalY=0 NormalZ=1 Radius=17.6777
    g5: LineSegment StartX=9.5 StartY=-9.5 StartZ=0 EndX=9.5 EndY=9.5 EndZ=0
    g6: LineSegment StartX=9.5 StartY=9.5 StartZ=0 EndX=-9.5 EndY=9.5 EndZ=0
    g7: LineSegment StartX=-9.5 StartY=9.5 StartZ=0 EndX=-9.5 EndY=-9.5 EndZ=0
    g8: LineSegment StartX=-9.5 StartY=-9.5 StartZ=0 EndX=9.5 EndY=-9.5 EndZ=0
    g9: Circle [constr] CenterX=0 CenterY=0 CenterZ=0 NormalX=0 NormalY=0 NormalZ=1 Radius=13.435
  constraints (30):
    c: Coincident(g0,g1)
    c: Coincident(g1,g2)
    c: Coincident(g2,g3)
    c: Coincident(g3,g0)
    c: Equal(g0,g1)
    c: Equal(g0,g2)
    c: Equal(g0,g3)
    c: PointOnObject(g0,g4)
    c: PointOnObject(g1,g4)
    c: PointOnObject(g2,g4)
    c: PointOnObject(g3,g4)
    c: Coincident(g1,g-1)
    c: Coincident(g5,g6)
    c: Coincident(g6,g7)
    c: Coincident(g7,g8)
    c: Coincident(g8,g5)
    c: Equal(g5,g6)
    c: Equal(g5,g7)
    c: Equal(g5,g8)
    c: PointOnObject(g5,g9)
    c: PointOnObject(g6,g9)
    c: PointOnObject(g7,g9)
    c: PointOnObject(g8,g9)
    c: Coincident(g6,g-1)
    c: DistanceX(g0,g0) = 25
    c: Horizontal(g0)
    c: Horizontal(g6)
    c: DistanceX(g6,g5) = 19
    c: Coincident(g9,g-1)
    c: Coincident(g4,g-1)
FEATURE [Part::Extrusion] Extrude533
  Base = -> Sketch481
  Dir = (0,2140,0)
  Placement = pos=(-1346,0,-90.5) rot=(0,0,1;3.14159rad)
  Solid = true
FEATURE [Sketcher::SketchObject] Sketch482
  Placement = pos=(-1346,0,-78) rot=(0,0,1;3.14159rad)
  Support = -> Extrude533 [Face1]
  sketch-geometry (8):
    g0: Circle CenterX=0 CenterY=11 CenterZ=0 NormalX=0 NormalY=0 NormalZ=1 Radius=3.5
    g1: Circle CenterX=0 CenterY=29 CenterZ=0 NormalX=0 NormalY=0 NormalZ=1 Radius=3.5
    g2: Circle CenterX=0 CenterY=522.5 CenterZ=0 NormalX=0 NormalY=0 NormalZ=1 Radius=3.5
    g3: Circle CenterX=0 CenterY=547.5 CenterZ=0 NormalX=0 NormalY=0 NormalZ=1 Radius=3.5
    g4: Circle CenterX=0 CenterY=1592.5 CenterZ=0 NormalX=0 NormalY=0 NormalZ=1 Radius=3.5
    g5: Circle CenterX=0 CenterY=1617.5 CenterZ=0 NormalX=0 NormalY=0 NormalZ=1 Radius=3.5
    g6: Circle CenterX=0 CenterY=2111 CenterZ=0 NormalX=0 NormalY=0 NormalZ=1 Radius=3.5
    g7: Circle CenterX=0 CenterY=2129 CenterZ=0 NormalX=0 NormalY=0 NormalZ=1 Radius=3.5
  constraints (18):
    c: PointOnObject(g0,g-2)
    c: PointOnObject(g1,g-2)
    c: DistanceY(g1,g0) = -18
    c: DistanceY(g-1,g0) = 11
    c: PointOnObject(g2,g-2)
    c: PointOnObject(g4,g-2)
    c: PointOnObject(g5,g-2)
    c: PointOnObject(g3,g-2)
    c: PointOnObject(g6,g-2)
    c: PointOnObject(g7,g-2)
    c: DistanceY(g7,g6) = -18
    c: DistanceY(g2,g3) = 25
    c: DistanceY(g5,g4) = -25
    c: Radius(g0) = 3.5
    c: Equal(g0, g1-g7) x7
    c: DistanceY(g6,g5) = -493.5
    c: DistanceY(g4,g3) = -1045
    c: DistanceY(g2,g1) = -493.5
FEATURE [PartDesign::Pocket] Pocket016
  Length = 5
  Placement = pos=(-1346,0,-90.5) rot=(0,0,1;3.14159rad)
  Sketch = -> Sketch482
  Type = 1
FEATURE [App::DocumentObjectGroup] Groupe035  label="Tube_25x25x3_L2140_002"
  Group = -> [Pocket016,Extrude533]
FEATURE [App::DocumentObjectGroup] Groupe013  label="Assemblage_cadre_001"
  Group = -> [Groupe028,Groupe030,Groupe034,Groupe035]
FEATURE [App::DocumentObjectGroup] Groupe015  label="Assemblage_cadre+miroirs_001"
  Group = -> [Groupe013,Groupe,Groupe001,Groupe005,Groupe006,Groupe007,Groupe008,Groupe009,Groupe010,Groupe011,Groupe012]
FEATURE [Sketcher::SketchObject] Sketch483
  Placement = pos=(0,0,0) rot=(1,0,0;1.5708rad)
  sketch-geometry (10):
    g0: LineSegment StartX=12.5 StartY=12.5 StartZ=0 EndX=-12.5 EndY=12.5 EndZ=0
    g1: LineSegment StartX=-12.5 StartY=12.5 StartZ=0 EndX=-12.5 EndY=-12.5 EndZ=0
    g2: LineSegment StartX=-12.5 StartY=-12.5 StartZ=0 EndX=12.5 EndY=-12.5 EndZ=0
    g3: LineSegment StartX=12.5 StartY=-12.5 StartZ=0 EndX=12.5 EndY=12.5 EndZ=0
    g4: Circle [constr] CenterX=0 CenterY=0 CenterZ=0 NormalX=0 NormalY=0 NormalZ=1 Radius=17.6777
    g5: LineSegment StartX=9.5 StartY=-9.5 StartZ=0 EndX=9.5 EndY=9.5 EndZ=0
    g6: LineSegment StartX=9.5 StartY=9.5 StartZ=0 EndX=-9.5 EndY=9.5 EndZ=0
    g7: LineSegment StartX=-9.5 StartY=9.5 StartZ=0 EndX=-9.5 EndY=-9.5 EndZ=0
    g8: LineSegment StartX=-9.5 StartY=-9.5 StartZ=0 EndX=9.5 EndY=-9.5 EndZ=0
    g9: Circle [constr] CenterX=0 CenterY=0 CenterZ=0 NormalX=0 NormalY=0 NormalZ=1 Radius=13.435
  constraints (30):
    c: Coincident(g0,g1)
    c: Coincident(g1,g2)
    c: Coincident(g2,g3)
    c: Coincident(g3,g0)
    c: Equal(g0,g1)
    c: Equal(g0,g2)
    c: Equal(g0,g3)
    c: PointOnObject(g0,g4)
    c: PointOnObject(g1,g4)
    c: PointOnObject(g2,g4)
    c: PointOnObject(g3,g4)
    c: Coincident(g1,g-1)
    c: Coincident(g5,g6)
    c: Coincident(g6,g7)
    c: Coincident(g7,g8)
    c: Coincident(g8,g5)
    c: Equal(g5,g6)
    c: Equal(g5,g7)
    c: Equal(g5,g8)
    c: PointOnObject(g5,g9)
    c: PointOnObject(g6,g9)
    c: PointOnObject(g7,g9)
    c: PointOnObject(g8,g9)
    c: Coincident(g6,g-1)
    c: DistanceX(g0,g0) = 25
    c: Horizontal(g0)
    c: Horizontal(g6)
    c: DistanceX(g6,g5) = 19
    c: Coincident(g9,g-1)
    c: Coincident(g4,g-1)
FEATURE [Part::Extrusion] Extrude534
  Base = -> Sketch483
  Dir = (0,2140,0)
  Placement = pos=(-1371,0,-90.5) rot=(0,0,1;3.14159rad)
  Solid = true
FEATURE [Sketcher::SketchObject] Sketch484
  Placement = pos=(-1371,0,-78) rot=(0,0,1;3.14159rad)
  Support = -> Extrude534 [Face1]
  sketch-geometry (8):
    g0: Circle CenterX=0 CenterY=11 CenterZ=0 NormalX=0 NormalY=0 NormalZ=1 Radius=3.5
    g1: Circle CenterX=0 CenterY=29 CenterZ=0 NormalX=0 NormalY=0 NormalZ=1 Radius=3.5
    g2: Circle CenterX=0 CenterY=522.5 CenterZ=0 NormalX=0 NormalY=0 NormalZ=1 Radius=3.5
    g3: Circle CenterX=0 CenterY=547.5 CenterZ=0 NormalX=0 NormalY=0 NormalZ=1 Radius=3.5
    g4: Circle CenterX=0 CenterY=1592.5 CenterZ=0 NormalX=0 NormalY=0 NormalZ=1 Radius=3.5
    g5: Circle CenterX=0 CenterY=1617.5 CenterZ=0 NormalX=0 NormalY=0 NormalZ=1 Radius=3.5
    g6: Circle CenterX=0 CenterY=2111 CenterZ=0 NormalX=0 NormalY=0 NormalZ=1 Radius=3.5
    g7: Circle CenterX=0 CenterY=2129 CenterZ=0 NormalX=0 NormalY=0 NormalZ=1 Radius=3.5
  constraints (18):
    c: PointOnObject(g0,g-2)
    c: PointOnObject(g1,g-2)
    c: DistanceY(g1,g0) = -18
    c: DistanceY(g-1,g0) = 11
    c: PointOnObject(g2,g-2)
    c: PointOnObject(g4,g-2)
    c: PointOnObject(g5,g-2)
    c: PointOnObject(g3,g-2)
    c: PointOnObject(g6,g-2)
    c: PointOnObject(g7,g-2)
    c: DistanceY(g7,g6) = -18
    c: DistanceY(g2,g3) = 25
    c: DistanceY(g5,g4) = -25
    c: Radius(g0) = 3.5
    c: Equal(g0, g1-g7) x7
    c: DistanceY(g6,g5) = -493.5
    c: DistanceY(g4,g3) = -1045
    c: DistanceY(g2,g1) = -493.5
FEATURE [PartDesign::Pocket] Pocket017
  Length = 5
  Placement = pos=(-1371,0,-90.5) rot=(0,0,1;3.14159rad)
  Sketch = -> Sketch484
  Type = 1
FEATURE [App::DocumentObjectGroup] Groupe036  label="Tube_25x25x3_L2140_003"
  Group = -> [Pocket017,Extrude534]
FEATURE [Sketcher::SketchObject] Sketch485
  Placement = pos=(0,0,0) rot=(1,0,0;1.5708rad)
  sketch-geometry (10):
    g0: LineSegment StartX=12.5 StartY=12.5 StartZ=0 EndX=-12.5 EndY=12.5 EndZ=0
    g1: LineSegment StartX=-12.5 StartY=12.5 StartZ=0 EndX=-12.5 EndY=-12.5 EndZ=0
    g2: LineSegment StartX=-12.5 StartY=-12.5 StartZ=0 EndX=12.5 EndY=-12.5 EndZ=0
    g3: LineSegment StartX=12.5 StartY=-12.5 StartZ=0 EndX=12.5 EndY=12.5 EndZ=0
    g4: Circle [constr] CenterX=0 CenterY=0 CenterZ=0 NormalX=0 NormalY=0 NormalZ=1 Radius=17.6777
    g5: LineSegment StartX=9.5 StartY=-9.5 StartZ=0 EndX=9.5 EndY=9.5 EndZ=0
    g6: LineSegment StartX=9.5 StartY=9.5 StartZ=0 EndX=-9.5 EndY=9.5 EndZ=0
    g7: LineSegment StartX=-9.5 StartY=9.5 StartZ=0 EndX=-9.5 EndY=-9.5 EndZ=0
    g8: LineSegment StartX=-9.5 StartY=-9.5 StartZ=0 EndX=9.5 EndY=-9.5 EndZ=0
    g9: Circle [constr] CenterX=0 CenterY=0 CenterZ=0 NormalX=0 NormalY=0 NormalZ=1 Radius=13.435
  constraints (30):
    c: Coincident(g0,g1)
    c: Coincident(g1,g2)
    c: Coincident(g2,g3)
    c: Coincident(g3,g0)
    c: Equal(g0,g1)
    c: Equal(g0,g2)
    c: Equal(g0,g3)
    c: PointOnObject(g0,g4)
    c: PointOnObject(g1,g4)
    c: PointOnObject(g2,g4)
    c: PointOnObject(g3,g4)
    c: Coincident(g1,g-1)
    c: Coincident(g5,g6)
    c: Coincident(g6,g7)
    c: Coincident(g7,g8)
    c: Coincident(g8,g5)
    c: Equal(g5,g6)
    c: Equal(g5,g7)
    c: Equal(g5,g8)
    c: PointOnObject(g5,g9)
    c: PointOnObject(g6,g9)
    c: PointOnObject(g7,g9)
    c: PointOnObject(g8,g9)
    c: Coincident(g6,g-1)
    c: DistanceX(g0,g0) = 25
    c: Horizontal(g0)
    c: Horizontal(g6)
    c: DistanceX(g6,g5) = 19
    c: Coincident(g9,g-1)
    c: Coincident(g4,g-1)
FEATURE [Part::Extrusion] Extrude535
  Base = -> Sketch485
  Dir = (0,2140,0)
  Placement = pos=(-2776,0,-90.5) rot=(0,0,1;3.14159rad)
  Solid = true
FEATURE [Sketcher::SketchObject] Sketch486
  Placement = pos=(-2776,0,-78) rot=(0,0,1;3.14159rad)
  Support = -> Extrude535 [Face1]
  sketch-geometry (8):
    g0: Circle CenterX=0 CenterY=11 CenterZ=0 NormalX=0 NormalY=0 NormalZ=1 Radius=3.5
    g1: Circle CenterX=0 CenterY=29 CenterZ=0 NormalX=0 NormalY=0 NormalZ=1 Radius=3.5
    g2: Circle CenterX=0 CenterY=522.5 CenterZ=0 NormalX=0 NormalY=0 NormalZ=1 Radius=3.5
    g3: Circle CenterX=0 CenterY=547.5 CenterZ=0 NormalX=0 NormalY=0 NormalZ=1 Radius=3.5
    g4: Circle CenterX=0 CenterY=1592.5 CenterZ=0 NormalX=0 NormalY=0 NormalZ=1 Radius=3.5
    g5: Circle CenterX=0 CenterY=1617.5 CenterZ=0 NormalX=0 NormalY=0 NormalZ=1 Radius=3.5
    g6: Circle CenterX=0 CenterY=2111 CenterZ=0 NormalX=0 NormalY=0 NormalZ=1 Radius=3.5
    g7: Circle CenterX=0 CenterY=2129 CenterZ=0 NormalX=0 NormalY=0 NormalZ=1 Radius=3.5
  constraints (18):
    c: PointOnObject(g0,g-2)
    c: PointOnObject(g1,g-2)
    c: DistanceY(g1,g0) = -18
    c: DistanceY(g-1,g0) = 11
    c: PointOnObject(g2,g-2)
    c: PointOnObject(g4,g-2)
    c: PointOnObject(g5,g-2)
    c: PointOnObject(g3,g-2)
    c: PointOnObject(g6,g-2)
    c: PointOnObject(g7,g-2)
    c: DistanceY(g7,g6) = -18
    c: DistanceY(g2,g3) = 25
    c: DistanceY(g5,g4) = -25
    c: Radius(g0) = 3.5
    c: Equal(g0, g1-g7) x7
    c: DistanceY(g6,g5) = -493.5
    c: DistanceY(g4,g3) = -1045
    c: DistanceY(g2,g1) = -493.5
FEATURE [PartDesign::Pocket] Pocket018
  Length = 5
  Placement = pos=(-2776,0,-90.5) rot=(0,0,1;3.14159rad)
  Sketch = -> Sketch486
  Type = 1
FEATURE [App::DocumentObjectGroup] Groupe037  label="Tube_25x25x3_L2140_004"
  Group = -> [Pocket018,Extrude535]
FEATURE [App::DocumentObjectGroup] Groupe026  label="Assemblage_cadre_002"
  Group = -> [Groupe029,Groupe031,Groupe036,Groupe037]
FEATURE [App::DocumentObjectGroup] Groupe027  label="Assemblage_cadre+miroirs_002"
  Group = -> [Groupe026,Groupe016,Groupe017,Groupe018,Groupe019,Groupe020,Groupe021,Groupe022,Groupe023,Groupe024,Groupe025]
